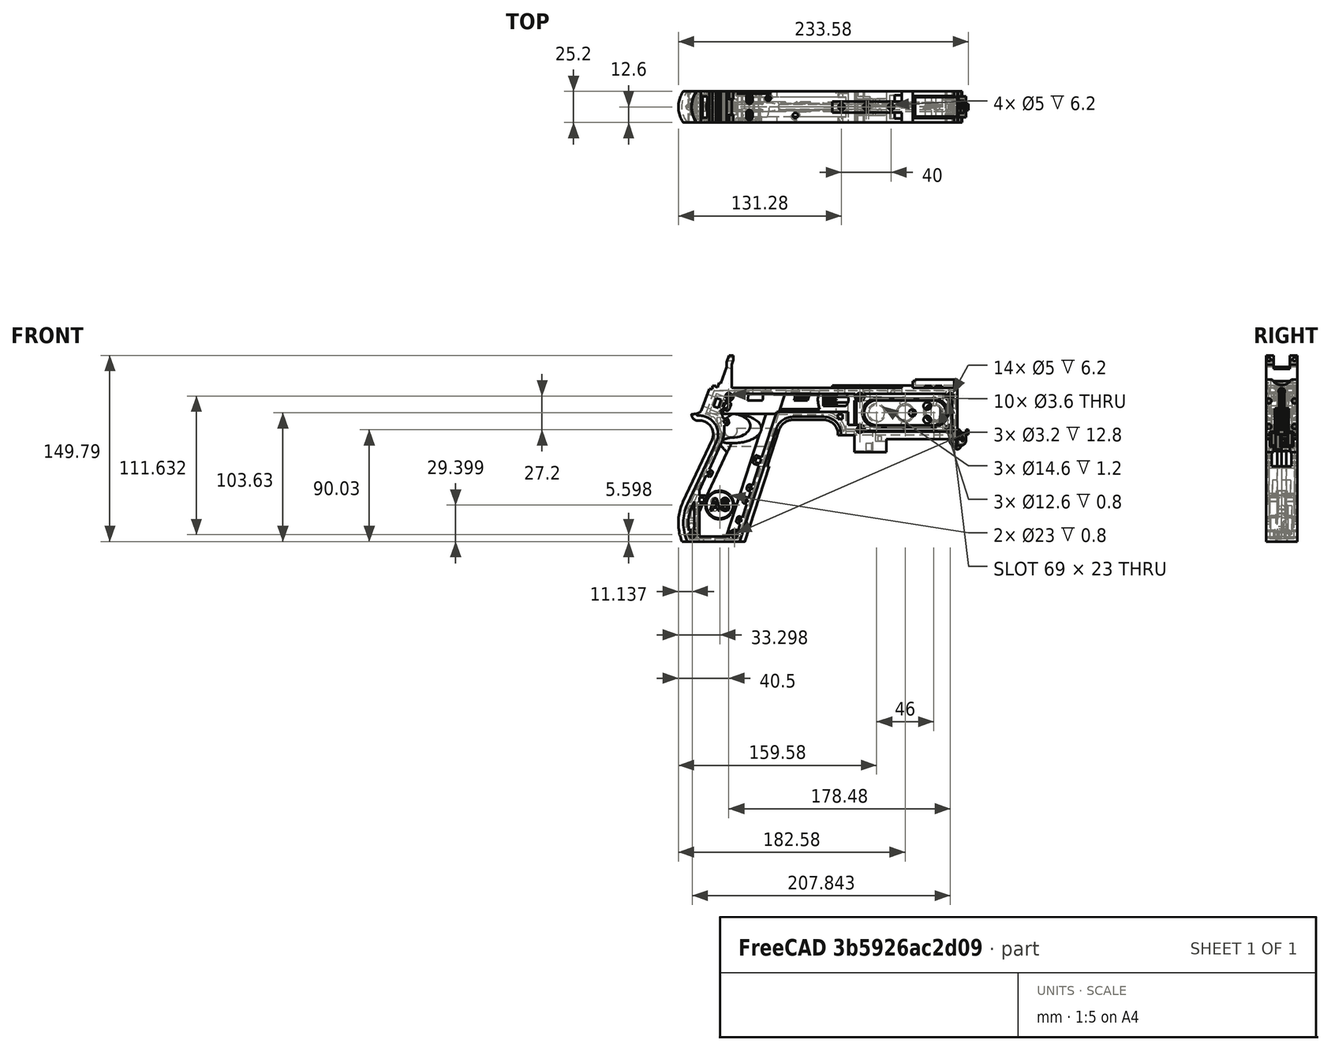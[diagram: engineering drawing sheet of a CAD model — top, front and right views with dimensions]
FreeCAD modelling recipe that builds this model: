
FCSTD DOCUMENT  (FreeCAD 1.0R39319 (Git))
Label: PICON-OF_ver_50
License: All rights reserved
LicenseURL: https://en.wikipedia.org/wiki/All_rights_reserved
objects: Sketcher::SketchObject×122, Part::Extrusion×62, Part::Cut×48, PartDesign::Pad×29, PartDesign::Pocket×20, PartDesign::Chamfer×15, PartDesign::Body×10, PartDesign::Fillet×6, Part::MultiFuse×4, Part::Part2DObjectPython×4, PartDesign::SubtractivePipe×4, PartDesign::SubtractiveLoft×4, PartDesign::Plane×3, PartDesign::SubShapeBinder×2, Part::Sweep×1, PartDesign::ShapeBinder×1, Mesh::Feature×1, PartDesign::Point×1, PartDesign::Groove×1
note: 617 computed .brp shape members not serialized (recipe doc carries the construction recipe); baked Part::Feature solids carry a one-line shape summary decoded from their .brp

FEATURE [Sketcher::SketchObject] Sketch  label="corpo principale"
  ArcFitTolerance = 1e-06
  AttacherType = Attacher::AttachEngine3D
  AttachmentSupport = -> [XZ_Plane]
  FullyConstrained = true
  MakeInternals = false
  MapMode = 5
  Placement = pos=(0,0,0) rot=(1,0,0;1.5708rad)
  sketch-geometry (65):
    g0: LineSegment StartX=0 StartY=0 StartZ=0 EndX=-57.2 EndY=0 EndZ=0
    g1: LineSegment StartX=-57.2 StartY=0 StartZ=0 EndX=-57.2 EndY=-10.4 EndZ=0
    g2: LineSegment StartX=-57.2 StartY=-10.4 StartZ=0 EndX=-82.8 EndY=-10.4 EndZ=0
    g3: LineSegment StartX=-82.8 StartY=-10.4 StartZ=0 EndX=-82.8 EndY=3.2 EndZ=0
    g4: LineSegment StartX=-82.8 StartY=3.2 StartZ=0 EndX=-93.6 EndY=3.2 EndZ=0
    g5: LineSegment StartX=-93.6 StartY=3.2 StartZ=0 EndX=-93.6 EndY=4 EndZ=0
    g6: LineSegment StartX=-107.6 StartY=18 StartZ=0 EndX=-132.428 EndY=18 EndZ=0
    g7: LineSegment StartX=-145.743 StartY=8.32624 StartZ=0 EndX=-175.232 EndY=-82.4316 EndZ=0
    g8: LineSegment StartX=-175.232 StartY=-82.4316 StartZ=0 EndX=-217.232 EndY=-82.4316 EndZ=0
    g9: LineSegment StartX=-217.232 StartY=-52.1862 StartZ=0 EndX=-193.988 EndY=-2.33927 EndZ=0
    g10: LineSegment StartX=-206.196 StartY=23.0857 StartZ=0 EndX=-199.861 EndY=40.4914 EndZ=0
    g11: LineSegment StartX=-199.861 StartY=40.4914 StartZ=0 EndX=-197.061 EndY=40.4914 EndZ=0
    g12: LineSegment StartX=-197.061 StartY=40.4914 StartZ=0 EndX=-197.061 EndY=42.8914 EndZ=0
    g13: LineSegment StartX=-197.061 StartY=42.8914 StartZ=0 EndX=-194.261 EndY=42.8914 EndZ=0
    g14: LineSegment StartX=-194.261 StartY=42.8914 StartZ=0 EndX=-194.535 EndY=42.1397 EndZ=0
    g15: LineSegment StartX=-194.535 StartY=42.1397 StartZ=0 EndX=-193.031 EndY=41.5924 EndZ=0
    g16: LineSegment StartX=-193.031 StartY=41.5924 StartZ=0 EndX=-191.663 EndY=45.3512 EndZ=0
    g17: LineSegment StartX=-191.663 StartY=45.3512 StartZ=0 EndX=-190.536 EndY=44.9408 EndZ=0
    g18: LineSegment StartX=-190.536 StartY=44.9408 StartZ=0 EndX=-185.747 EndY=58.0965 EndZ=0
    g19: LineSegment StartX=-185.747 StartY=58.0965 StartZ=0 EndX=-185.747 EndY=62.0965 EndZ=0
    g20: LineSegment StartX=-185.747 StartY=62.0965 StartZ=0 EndX=-183.832 EndY=67.3588 EndZ=0
    g21: LineSegment StartX=-183.832 StartY=67.3588 StartZ=0 EndX=-180.232 EndY=67.3588 EndZ=0
    g22: LineSegment StartX=-180.232 StartY=67.3588 StartZ=0 EndX=-180.232 EndY=63.7588 EndZ=0
    g23: LineSegment StartX=-180.232 StartY=63.7588 StartZ=0 EndX=-181.6 EndY=60 EndZ=0
    g24: LineSegment StartX=-181.6 StartY=60 StartZ=0 EndX=-181.6 EndY=41.2 EndZ=0
    g25: LineSegment StartX=-181.6 StartY=41.2 StartZ=0 EndX=-100.8 EndY=41.2 EndZ=0
    g26: LineSegment StartX=-36 StartY=43.2 StartZ=0 EndX=-36 EndY=41.2 EndZ=0
    g27: LineSegment StartX=0 StartY=48 StartZ=0 EndX=0 EndY=0 EndZ=0
    g28: LineSegment StartX=-209.901 StartY=19.85 StartZ=0 EndX=-209.901 EndY=20.1 EndZ=0
    g29: LineSegment StartX=-208.001 StartY=22 StartZ=0 EndX=-207.747 EndY=22 EndZ=0
    g30: LineSegment StartX=-207.583 StartY=19 StartZ=0 EndX=-209.051 EndY=19 EndZ=0
    g31: ArcOfCircle CenterX=-208.001 CenterY=20.1 CenterZ=0 NormalX=0 NormalY=0 NormalZ=1 AngleXU=0 Radius=1.9 StartAngle=1.5708 EndAngle=3.14159
    g32: GeomPoint [constr] X=-209.901 Y=22 Z=0
    g33: ArcOfCircle CenterX=-209.051 CenterY=19.85 CenterZ=0 NormalX=0 NormalY=0 NormalZ=1 AngleXU=0 Radius=0.85 StartAngle=3.14159 EndAngle=4.71239
    g34: GeomPoint [constr] X=-209.901 Y=19 Z=0
    g35: ArcOfCircle CenterX=-207.747 CenterY=23.65 CenterZ=0 NormalX=0 NormalY=0 NormalZ=1 AngleXU=0 Radius=1.65 StartAngle=4.71239 EndAngle=5.93412
    g36: GeomPoint [constr] X=-206.591 Y=22 Z=0
    g37: LineSegment StartX=-4 StartY=6 StartZ=0 EndX=-4 EndY=36.4 EndZ=0
    g38: LineSegment StartX=-4 StartY=36.4 StartZ=0 EndX=-185.2 EndY=36.4 EndZ=0
    g39: LineSegment StartX=-185.2 StartY=36.4 StartZ=0 EndX=-190.441 EndY=22 EndZ=0
    g40: LineSegment StartX=-214.575 StartY=-78.4316 StartZ=0 EndX=-178.142 EndY=-78.4316 EndZ=0
    g41: LineSegment StartX=-178.142 StartY=-78.4316 StartZ=0 EndX=-145.51 EndY=22 EndZ=0
    g42: LineSegment StartX=-145.51 StartY=22 StartZ=0 EndX=-87.91 EndY=22 EndZ=0
    g43: LineSegment StartX=-87.91 StartY=22 StartZ=0 EndX=-87.91 EndY=11.6 EndZ=0
    g44: LineSegment StartX=-87.91 StartY=11.6 StartZ=0 EndX=-80.11 EndY=11.6 EndZ=0
    g45: LineSegment StartX=-80.11 StartY=11.6 StartZ=0 EndX=-80.11 EndY=6 EndZ=0
    g46: LineSegment StartX=-80.11 StartY=6 StartZ=0 EndX=-4 EndY=6 EndZ=0
    g47: LineSegment StartX=-190.363 StartY=-4.02975 StartZ=0 EndX=-213.607 EndY=-53.8767 EndZ=0
    g48: ArcOfCircle CenterX=-132.428 CenterY=4 CenterZ=0 NormalX=0 NormalY=0 NormalZ=1 AngleXU=0 Radius=14 StartAngle=1.5708 EndAngle=2.82743
    g49: GeomPoint [constr] X=-142.6 Y=18 Z=0
    g50: ArcOfCircle CenterX=-107.6 CenterY=4 CenterZ=0 NormalX=0 NormalY=0 NormalZ=1 AngleXU=0 Radius=14 StartAngle=0 EndAngle=1.5708
    g51: GeomPoint [constr] X=-93.6 Y=18 Z=0
    g52: ArcOfCircle CenterX=-184.801 CenterY=-67.3089 CenterZ=0 NormalX=0 NormalY=0 NormalZ=1 AngleXU=0 Radius=35.7833 StartAngle=2.70526 EndAngle=3.57792
    g53: ArcOfCircle CenterX=-207.583 CenterY=4 CenterZ=0 NormalX=0 NormalY=0 NormalZ=1 AngleXU=0 Radius=15 StartAngle=5.84685 EndAngle=7.85398
    g54: LineSegment [constr] StartX=-213.607 StartY=-53.8767 StartZ=0 EndX=-217.232 EndY=-52.1862 EndZ=0
    g55: ArcOfCircle CenterX=-184.801 CenterY=-67.3089 CenterZ=0 NormalX=0 NormalY=0 NormalZ=1 AngleXU=0 Radius=31.7833 StartAngle=2.70526 EndAngle=3.49911
    g56: ArcOfCircle CenterX=-218.095 CenterY=8.90192 CenterZ=0 NormalX=0 NormalY=0 NormalZ=1 AngleXU=0 Radius=30.5989 StartAngle=5.84685 EndAngle=6.72553
    g57: LineSegment StartX=-44.6 StartY=43.2 StartZ=0 EndX=-36 EndY=43.2 EndZ=0
    g58: LineSegment StartX=-100.8 StartY=41.2 StartZ=0 EndX=-44.6 EndY=41.2 EndZ=0
    g59: LineSegment StartX=-44.6 StartY=41.2 StartZ=0 EndX=-44.6 EndY=43.2 EndZ=0
    g60: LineSegment StartX=-2.4 StartY=48 StartZ=0 EndX=0 EndY=48 EndZ=0
    g61: LineSegment StartX=-36 StartY=41.2 StartZ=0 EndX=-2.4 EndY=41.2 EndZ=0
    g62: LineSegment StartX=-2.4 StartY=41.2 StartZ=0 EndX=-2.4 EndY=48 EndZ=0
    g63: LineSegment [constr] StartX=-181.6 StartY=36.4 StartZ=0 EndX=-152.209 EndY=36.4 EndZ=0
    g64: LineSegment [constr] StartX=-181.6 StartY=36.4 StartZ=0 EndX=-130.41 EndY=36.4 EndZ=0
  constraints (183):
    c: Coincident(g-1,g0)
    c: PointOnObject(g0,g-1)
    c: Coincident(g0,g1)
    c: Vertical(g1)
    c: Coincident(g1,g2)
    c: Horizontal(g2)
    c: Coincident(g2,g3)
    c: Vertical(g3)
    c: Coincident(g3,g4)
    c: Coincident(g4,g5)
    c: Vertical(g5)
    c: Horizontal(g6)
    c: Coincident(g7,g8)
    c: Horizontal(g8)
    c: Coincident(g10,g11)
    c: Horizontal(g11)
    c: Coincident(g11,g12)
    c: Vertical(g12)
    c: Coincident(g12,g13)
    c: Horizontal(g13)
    c: Coincident(g13,g14)
    c: Coincident(g14,g15)
    c: Coincident(g15,g16)
    c: Coincident(g16,g17)
    c: Coincident(g17,g18)
    c: Coincident(g18,g19)
    c: Vertical(g19)
    c: Coincident(g19,g20)
    c: Coincident(g20,g21)
    c: Horizontal(g21)
    c: Coincident(g21,g22)
    c: Vertical(g22)
    c: Coincident(g22,g23)
    c: Coincident(g23,g24)
    c: Vertical(g24)
    c: Coincident(g24,g25)
    c: Horizontal(g25)
    c: Coincident(g57,g26)
    c: Vertical(g26)
    c: Coincident(g26,g61)
    c: PointOnObject(g60,g-2)
    c: Coincident(g60,g27)
    c: Coincident(g27,g0)
    c: DistanceY(g27,g27) = 48
    c: DistanceY(g1,g1) = 10.4
    c: DistanceX(g0,g0) = 57.2
    c: DistanceX(g2,g2) = 25.6
    c: Horizontal(g4)
    c: DistanceY(g3,g3) = 13.6
    c: DistanceX(g4,g4) = 10.8
    c: DistanceY(g5,g51) = 14.8
    c: DistanceX(g49,g51) = 49
    c: Distance(g7,g49) = 105.6
    c: DistanceX(g61,g60) = 36
    c: DistanceX(g25,g25) = 80.8
    c: DistanceY(g24,g24) = 18.8
    c: DistanceY(g22,g22) = 3.6
    c: Distance(g23) = 4
    c: Angle(g-1,g23) = 1.22173
    c: DistanceX(g21,g21) = 3.6
    c: Distance(g20) = 5.6
    c: Angle(g-1,g20) = 1.22173
    c: DistanceY(g19,g19) = 4
    c: Distance(g18) = 14
    c: Angle(g-1,g18) = 1.22173
    c: Distance(g17) = 1.2
    c: Distance(g16) = 4
    c: Angle(g16) = 1.22173
    c: Perpendicular(g18,g17)
    c: Distance(g15) = 1.6
    c: Perpendicular(g16,g15)
    c: Distance(g14) = 0.8
    c: DistanceX(g13,g13) = 2.8
    c: Perpendicular(g15,g14)
    c: DistanceY(g12,g12) = 2.4
    c: DistanceX(g11,g11) = 2.8
    c: Distance(g9) = 55
    c: Angle(g9,g-1) = 2.00713
    c: Horizontal(g29)
    c: Vertical(g28)
    c: Horizontal(g30)
    c: PointOnObject(g32,g29)
    c: PointOnObject(g32,g28)
    c: Tangent(g29,g31) = 1.5708
    c: Tangent(g28,g31) = 1.5708
    c: PointOnObject(g34,g28)
    c: PointOnObject(g34,g30)
    c: Tangent(g28,g33) = 1.5708
    c: Tangent(g30,g33) = 1.5708
    c: PointOnObject(g36,g29)
    c: PointOnObject(g36,g10)
    c: Tangent(g29,g35) = -1.5708
    c: Tangent(g10,g35) = -1.5708
    c: Angle(g-1,g10) = 1.22173
    c: Radius(g35) = 1.65
    c: Vertical(g37)
    c: Coincident(g37,g38)
    c: Horizontal(g38)
    c: Coincident(g38,g39)
    c: Horizontal(g40)
    c: Coincident(g40,g41)
    c: Coincident(g41,g42)
    c: Horizontal(g42)
    c: Coincident(g42,g43)
    c: Vertical(g43)
    c: Coincident(g43,g44)
    c: Horizontal(g44)
    c: Coincident(g44,g45)
    c: Vertical(g45)
    c: Coincident(g45,g46)
    c: Coincident(g46,g37)
    c: Horizontal(g46)
    c: DistanceY(g0,g37) = 6
    c: DistanceX(g37,g0) = 4
    c: DistanceY(g37,g25) = 4.8
    c: DistanceX(g38,g38) = 181.2
    c: DistanceX(g42,g42) = 57.6
    c: DistanceY(g49,g41) = 4
    c: DistanceX(g41,g49) = 2.91
    c: DistanceY(g43,g43) = 10.4
    c: DistanceX(g44,g44) = 7.8
    c: DistanceY(g7,g40) = 4
    c: Distance(g47) = 55
    c: Angle(g-1,g39) = 1.22173
    c: PointOnObject(g49,g7)
    c: PointOnObject(g49,g6)
    c: Tangent(g7,g48) = -1.5708
    c: Tangent(g6,g48) = -1.5708
    c: PointOnObject(g51,g5)
    c: PointOnObject(g51,g6)
    c: Tangent(g5,g50) = -1.5708
    c: Tangent(g6,g50) = -1.5708
    c: Radius(g50) = 14
    c: Radius(g48) = 14
    c: DistanceX(g8,g8) = 42
    c: Angle(g7,g-1) = 1.88496
    c: Parallel(g41,g7)
    c: Parallel(g47,g9)
    c: Coincident(g52,g8)
    c: Tangent(g52,g9) = 1.5708
    c: DistanceX(g9,g8) = 0
    c: Tangent(g53,g9) = -1.5708
    c: Tangent(g53,g30) = -1.5708
    c: Diameter(g53) = 30
    c: DistanceY(g53,g0) = -4
    c: Coincident(g54,g47)
    c: Distance(g54) = 4
    c: Coincident(g54,g9)
    c: Coincident(g55,g40)
    c: Tangent(g55,g47) = -1.5708
    c: Coincident(g52,g55)
    c: Coincident(g56,g39)
    c: Tangent(g56,g47) = 1.5708
    c: Horizontal(g57)
    c: DistanceX(g57,g57) = 8.6
    c: Coincident(g58,g25)
    c: Horizontal(g58)
    c: Coincident(g59,g58)
    c: Vertical(g59)
    c: DistanceY(g58,g57) = 2
    c: DistanceX(g58,g58) = 56.2
    c: Coincident(g59,g57)
    c: DistanceY(g41,g36) = 0
    c: DistanceY(g36,g39) = 0
    c: DistanceY(g28,g28) = 0.25
    c: DistanceX(g30,g36) = 2.46
    c: DistanceX(g28,g29) = 1.9
    c: Coincident(g62,g60)
    c: Horizontal(g60)
    c: DistanceX(g62,g27) = 2.4
    c: Coincident(g61,g62)
    c: DistanceY(g26,g26) = 2
    c: Vertical(g62)
    c: DistanceY(g61,g60) = 6.8
    c: Horizontal(g61)
    c: Distance(g63) = 29.391
    c: PointOnObject(g63,g38)
    c: PointOnObject(g63,g38)
    c: Distance(g64) = 51.19
    c: PointOnObject(g64,g38)
    c: PointOnObject(g64,g38)
    c: DistanceX(g24,g63) = 0
    c: DistanceX(g24,g64) = 0
FEATURE [Part::Extrusion] Extrude  label="Extrude corpo principale"
  Base = -> Sketch
  Dir = (0,-1,2e-16)
  DirMode = 2
  FaceMakerClass = Part::FaceMakerBullseye
  FaceMakerMode = 3
  LengthFwd = 25.2
  LengthRev = 12.6
  Solid = true
  Symmetric = true
FEATURE [Sketcher::SketchObject] Sketch002  label="scavo grilletto"
  ArcFitTolerance = 1e-06
  AttachmentSupport = -> [XZ_Plane]
  ExternalGeometry = -> [Sketch]
  FullyConstrained = true
  MakeInternals = false
  MapMode = 5
  Placement = pos=(0,0,0) rot=(1,0,0;1.5708rad)
  sketch-geometry (4):
    g0: LineSegment StartX=-89.51 StartY=22 StartZ=0 EndX=-152.71 EndY=22 EndZ=0
    g1: LineSegment StartX=-152.71 StartY=22 StartZ=0 EndX=-167.006 EndY=-22 EndZ=0
    g2: LineSegment StartX=-167.006 StartY=-22 StartZ=0 EndX=-89.51 EndY=-22 EndZ=0
    g3: LineSegment StartX=-89.51 StartY=-22 StartZ=0 EndX=-89.51 EndY=22 EndZ=0
  constraints (12):
    c: Horizontal(g0)
    c: Coincident(g0,g1)
    c: Coincident(g1,g2)
    c: Horizontal(g2)
    c: Coincident(g2,g3)
    c: Coincident(g3,g0)
    c: Vertical(g3)
    c: Angle(g1,g0) = 1.88496
    c: DistanceY(g3,g3) = 44
    c: DistanceX(g0,g0) = 63.2
    c: DistanceX(g0,g-3) = 1.6
    c: DistanceY(g-3,g0) = 0
FEATURE [Sketcher::SketchObject] Sketch004  label="traiettoria arrotondamento impugnatura anteriore"
  ArcFitTolerance = 1e-06
  AttachmentSupport = -> [XZ_Plane]
  ExternalGeometry = -> [Sketch]
  FullyConstrained = true
  MakeInternals = false
  MapMode = 5
  Placement = pos=(0,0,0) rot=(1,0,0;1.5708rad)
  sketch-geometry (13):
    g0: LineSegment StartX=-175.232 StartY=-82.4316 StartZ=0 EndX=-145.743 EndY=8.32624 EndZ=0
    g1: LineSegment StartX=-93.6 StartY=3.2 StartZ=0 EndX=-93.6 EndY=4 EndZ=0
    g2: LineSegment StartX=-132.428 StartY=18 StartZ=0 EndX=-107.6 EndY=18 EndZ=0
    g3: ArcOfCircle CenterX=-132.428 CenterY=4 CenterZ=0 NormalX=0 NormalY=0 NormalZ=1 AngleXU=0 Radius=14 StartAngle=1.5708 EndAngle=2.82743
    g4: ArcOfCircle CenterX=-107.6 CenterY=4 CenterZ=0 NormalX=0 NormalY=0 NormalZ=1 AngleXU=0 Radius=14 StartAngle=0 EndAngle=1.5708
    g5: LineSegment StartX=-175.232 StartY=-82.4316 StartZ=0 EndX=-217.232 EndY=-82.4316 EndZ=0
    g6: LineSegment StartX=-217.232 StartY=-52.1862 StartZ=0 EndX=-193.988 EndY=-2.33927 EndZ=0
    g7: LineSegment StartX=-209.051 StartY=19 StartZ=0 EndX=-207.583 EndY=19 EndZ=0
    g8: LineSegment StartX=-209.901 StartY=20.1 StartZ=0 EndX=-209.901 EndY=19.85 EndZ=0
    g9: ArcOfCircle CenterX=-184.801 CenterY=-67.3089 CenterZ=0 NormalX=0 NormalY=0 NormalZ=1 AngleXU=0 Radius=35.7833 StartAngle=2.70526 EndAngle=3.57792
    g10: ArcOfCircle CenterX=-207.583 CenterY=4 CenterZ=0 NormalX=0 NormalY=0 NormalZ=1 AngleXU=0 Radius=15 StartAngle=5.84685 EndAngle=7.85398
    g11: ArcOfCircle CenterX=-209.051 CenterY=19.85 CenterZ=0 NormalX=0 NormalY=0 NormalZ=1 AngleXU=0 Radius=0.85 StartAngle=3.14159 EndAngle=4.71239
    g12: ArcOfCircle CenterX=-208.001 CenterY=20.1 CenterZ=0 NormalX=0 NormalY=0 NormalZ=1 AngleXU=0 Radius=1.9 StartAngle=1.5708 EndAngle=3.14159
  constraints (26):
    c: Coincident(g0,g-3)
    c: Coincident(g0,g-6)
    c: Coincident(g1,g-8)
    c: Coincident(g1,g-7)
    c: Coincident(g2,g-5)
    c: Coincident(g2,g-4)
    c: Coincident(g3,g2)
    c: Tangent(g3,g0) = 1.5708
    c: Coincident(g4,g1)
    c: Tangent(g4,g2) = 1.5708
    c: Coincident(g5,g0)
    c: Coincident(g5,g-9)
    c: Coincident(g6,g-12)
    c: Coincident(g6,g-11)
    c: Coincident(g7,g-15)
    c: Coincident(g7,g-14)
    c: Coincident(g8,g-16)
    c: Coincident(g8,g-17)
    c: Tangent(g9,g6) = 1.5708
    c: Coincident(g9,g5)
    c: Coincident(g10,g7)
    c: Tangent(g10,g6) = -1.5708
    c: Tangent(g11,g7) = -1.5708
    c: Coincident(g11,g8)
    c: Tangent(g12,g8) = -1.5708
    c: Coincident(g12,g-17)
FEATURE [PartDesign::Plane] DatumPlane  label="Piano per disegno arrotondamento impugnatura"
  AttachmentSupport = -> [Sketch]
  Length = 73.6581
  MapMode = 7
  Placement = pos=(-145.743,1.8e-15,8.32624) rot=(0.154555,0.154555,0.97582;1.59527rad)
  ResizeMode = 0
  Width = 303.511
FEATURE [Sketcher::SketchObject] Sketch005  label="forma arrotondamento impugnatura anteriore"
  ArcFitTolerance = 1e-06
  AttachmentSupport = -> [DatumPlane]
  FullyConstrained = true
  MakeInternals = false
  MapMode = 5
  Placement = pos=(-145.743,1.8e-15,8.32624) rot=(0.154555,0.154555,0.97582;1.59527rad)
  sketch-geometry (5):
    g0: GeomPoint [constr] X=0 Y=-4 Z=0
    g1: GeomPoint [constr] X=-12.6 Y=7.1e-15 Z=0
    g2: GeomPoint [constr] X=12.6 Y=4.97e-14 Z=0
    g3: LineSegment StartX=-12.6 StartY=7.1e-15 StartZ=0 EndX=12.6 EndY=4.97e-14 EndZ=0
    g4: ArcOfCircle CenterX=-3.88e-14 CenterY=17.845 CenterZ=0 NormalX=0 NormalY=0 NormalZ=1 AngleXU=0 Radius=21.845 StartAngle=4.09759 EndAngle=5.32718
  constraints (11):
    c: DistanceY(g0,g-1) = 4
    c: DistanceX(g-1,g0) = 0
    c: DistanceX(g1,g-1) = 12.6
    c: DistanceX(g-1,g2) = 12.6
    c: DistanceY(g-1,g2) = 0
    c: DistanceY(g-1,g1) = 0
    c: Coincident(g3,g1)
    c: Coincident(g3,g2)
    c: Coincident(g4,g1)
    c: Coincident(g4,g2)
    c: PointOnObject(g0,g4)
FEATURE [Part::Sweep] Sweep  label="Sweep impugnatura"
  Frenet = true
  Sections = -> [Sketch005]
  Solid = true
  Spine = -> Sketch [Edge32,Edge33,Edge34,Edge35,Edge36,Edge37,Edge38,Edge39,Edge40,Edge41,Edge42,Edge43,Edge44]
  Transition = 1
FEATURE [Sketcher::SketchObject] Sketch008  label="buchi e pulizie varie"
  ArcFitTolerance = 1e-06
  AttachmentSupport = -> [XZ_Plane]
  ExternalGeometry = -> [Sketch]
  FullyConstrained = true
  MakeInternals = false
  MapMode = 5
  Placement = pos=(0,0,0) rot=(1,0,0;1.5708rad)
  sketch-geometry (26):
    g0: LineSegment StartX=-96.278 StartY=20.155 StartZ=0 EndX=-92.278 EndY=20.155 EndZ=0
    g1: LineSegment StartX=-92.278 StartY=20.155 StartZ=0 EndX=-92.278 EndY=16.155 EndZ=0
    g2: LineSegment StartX=-92.278 StartY=16.155 StartZ=0 EndX=-96.278 EndY=16.155 EndZ=0
    g3: LineSegment StartX=-96.278 StartY=16.155 StartZ=0 EndX=-96.278 EndY=20.155 EndZ=0
    g4: LineSegment StartX=-222.232 StartY=-82.4316 StartZ=0 EndX=-170.232 EndY=-82.4316 EndZ=0
    g5: LineSegment StartX=-170.232 StartY=-82.4316 StartZ=0 EndX=-170.232 EndY=-86.4316 EndZ=0
    g6: LineSegment StartX=-170.232 StartY=-86.4316 StartZ=0 EndX=-222.232 EndY=-86.4316 EndZ=0
    g7: LineSegment StartX=-222.232 StartY=-86.4316 StartZ=0 EndX=-222.232 EndY=-82.4316 EndZ=0
    g8: LineSegment StartX=-213.901 StartY=20.1 StartZ=0 EndX=-213.901 EndY=26 EndZ=0
    g9: LineSegment StartX=-213.901 StartY=26 StartZ=0 EndX=-206.196 EndY=26 EndZ=0
    g10: LineSegment StartX=-17.4 StartY=42.8 StartZ=0 EndX=-12.4 EndY=42.8 EndZ=0
    g11: LineSegment StartX=-12.4 StartY=42.8 StartZ=0 EndX=-12.4 EndY=41.2 EndZ=0
    g12: LineSegment StartX=-12.4 StartY=41.2 StartZ=0 EndX=-17.4 EndY=41.2 EndZ=0
    g13: LineSegment StartX=-17.4 StartY=41.2 StartZ=0 EndX=-17.4 EndY=42.8 EndZ=0
    g14: LineSegment StartX=-25.9 StartY=42.8 StartZ=0 EndX=-20.9 EndY=42.8 EndZ=0
    g15: LineSegment StartX=-20.9 StartY=42.8 StartZ=0 EndX=-20.9 EndY=41.2 EndZ=0
    g16: LineSegment StartX=-20.9 StartY=41.2 StartZ=0 EndX=-25.9 EndY=41.2 EndZ=0
    g17: LineSegment StartX=-25.9 StartY=41.2 StartZ=0 EndX=-25.9 EndY=42.8 EndZ=0
    g18: GeomPoint [constr] X=-206.196 Y=23.0857 Z=0
    g19: GeomPoint [constr] X=-213.901 Y=20.1 Z=0
    g20: BSplineCurve PolesCount=4 KnotsCount=2 Degree=3 IsPeriodic=0
    g21-g24: Circle [constr] x4 (B-spline internal-alignment scaffolding for g20; pole/knot coordinates omitted)
    g25: LineSegment StartX=-206.196 StartY=26 StartZ=0 EndX=-206.196 EndY=23.0857 EndZ=0
  constraints (73):
    c: Horizontal(g0)
    c: Coincident(g1,g0)
    c: Vertical(g1)
    c: Coincident(g2,g1)
    c: Horizontal(g2)
    c: Coincident(g3,g2)
    c: Coincident(g3,g0)
    c: Vertical(g3)
    c: DistanceX(g0,g-4) = 4.368
    c: DistanceY(g0,g-4) = 1.845
    c: DistanceY(g1,g1) = 4
    c: DistanceX(g2,g2) = 4
    c: Horizontal(g4)
    c: Coincident(g5,g4)
    c: Vertical(g5)
    c: Coincident(g6,g5)
    c: Horizontal(g6)
    c: Coincident(g7,g6)
    c: Coincident(g7,g4)
    c: Vertical(g7)
    c: DistanceY(g7,g7) = 4
    c: DistanceX(g4,g-5) = 5
    c: DistanceX(g-5,g4) = 5
    c: DistanceY(g4,g-5) = 0
    c: Coincident(g9,g8)
    c: Parallel(g9,g-6)
    c: DistanceX(g8,g-8) = 4
    c: Horizontal(g10)
    c: Coincident(g11,g10)
    c: Vertical(g11)
    c: Coincident(g12,g11)
    c: Horizontal(g12)
    c: Coincident(g13,g12)
    c: Coincident(g13,g10)
    c: Vertical(g13)
    c: Horizontal(g14)
    c: Coincident(g15,g14)
    c: Vertical(g15)
    c: Coincident(g16,g15)
    c: Horizontal(g16)
    c: Coincident(g17,g16)
    c: Coincident(g17,g14)
    c: Vertical(g17)
    c: DistanceY(g11,g10) = 1.6
    c: DistanceX(g10,g10) = 5
    c: DistanceY(g15,g14) = 1.6
    c: DistanceX(g14,g14) = 5
    c: DistanceX(g15,g12) = 3.5
    c: DistanceX(g11,g-9) = 10
    c: DistanceY(g-9,g11) = 0
    c: DistanceY(g-9,g15) = 0
    c: Perpendicular(g8,g9)
    c: DistanceY(g-7,g9) = 4
    c: DistanceY(g8,g-8) = 0
    c: InternalAlignment(g18,g20)
    c: InternalAlignment(g19,g20)
    c: InternalAlignment(g21,g20)
    c: Weight(g21) = 1
    c: InternalAlignment(g22,g20)
    c: Equal(g22,g21)
    c: InternalAlignment(g23,g20)
    c: Equal(g23,g21)
    c: InternalAlignment(g24,g20)
    c: Equal(g24,g21)
    c: Coincident(g18,g-12)
    c: Coincident(g19,g8)
    c: Coincident(g25,g9)
    c: Coincident(g25,g20)
    c: Vertical(g25)
    c: DistanceY(g20,g23) = 0
    c: DistanceY(g22,g18) = 2.26
    c: DistanceX(g22,g18) = 0.93
    c: DistanceX(g20,g23) = 2.9
FEATURE [Part::Extrusion] Extrude004  label="Extrude Buchi e pulizie varie"
  Base = -> Sketch008
  Dir = (0,-1,2e-16)
  DirMode = 2
  FaceMakerClass = Part::FaceMakerBullseye
  FaceMakerMode = 3
  LengthFwd = 25.2
  LengthRev = 0
  Solid = true
  Symmetric = true
FEATURE [Sketcher::SketchObject] Sketch009  label="rinforzi"
  ArcFitTolerance = 1e-06
  AttachmentSupport = -> [XZ_Plane]
  ExternalGeometry = -> [Sketch]
  FullyConstrained = true
  MakeInternals = false
  MapMode = 5
  Placement = pos=(0,0,0) rot=(1,0,0;1.5708rad)
  sketch-geometry (9):
    g0: LineSegment StartX=-87.91 StartY=22 StartZ=0 EndX=-87.91 EndY=36.4 EndZ=0
    g1: LineSegment StartX=-87.91 StartY=36.4 StartZ=0 EndX=-97.91 EndY=36.4 EndZ=0
    g2: LineSegment StartX=-97.91 StartY=36.4 StartZ=0 EndX=-97.91 EndY=22 EndZ=0
    g3: LineSegment StartX=-97.91 StartY=22 StartZ=0 EndX=-87.91 EndY=22 EndZ=0
    g4: LineSegment StartX=-149.713 StartY=9.06563 StartZ=0 EndX=-154.586 EndY=-5.93437 EndZ=0
    g5: LineSegment StartX=-154.586 StartY=-5.93437 StartZ=0 EndX=-191.863 EndY=-5.93437 EndZ=0
    g6: LineSegment StartX=-191.863 StartY=-5.93437 StartZ=0 EndX=-191.863 EndY=9.06563 EndZ=0
    g7: LineSegment StartX=-191.863 StartY=9.06563 StartZ=0 EndX=-149.713 EndY=9.06563 EndZ=0
    g8: LineSegment [constr] StartX=-145.51 StartY=22 StartZ=0 EndX=-149.713 EndY=9.06563 EndZ=0
  constraints (25):
    c: Vertical(g0)
    c: Coincident(g1,g0)
    c: Horizontal(g1)
    c: Coincident(g2,g1)
    c: Vertical(g2)
    c: Coincident(g3,g2)
    c: Coincident(g3,g0)
    c: Horizontal(g3)
    c: Coincident(g0,g-4)
    c: DistanceX(g3,g3) = 10
    c: DistanceY(g0,g-3) = 0
    c: Coincident(g5,g4)
    c: Horizontal(g5)
    c: Coincident(g6,g5)
    c: Vertical(g6)
    c: Coincident(g7,g6)
    c: Coincident(g7,g4)
    c: Horizontal(g7)
    c: Distance(g8) = 13.6
    c: Parallel(g-6,g8)
    c: Coincident(g-6,g8)
    c: Parallel(g4,g-6)
    c: DistanceY(g4,g4) = 15
    c: Coincident(g4,g8)
    c: DistanceX(g-5,g5) = -1.5
FEATURE [Part::Extrusion] Extrude001  label="Extrude scavo grilletto"
  Base = -> Sketch002
  Dir = (0,-1,2e-16)
  DirMode = 2
  FaceMakerClass = Part::FaceMakerBullseye
  FaceMakerMode = 3
  LengthFwd = 16
  LengthRev = 0
  Solid = true
  Symmetric = true
FEATURE [Part::Extrusion] Extrude005  label="Extrude Rinforzi"
  Base = -> Sketch009
  Dir = (0,-1,2e-16)
  DirMode = 2
  FaceMakerClass = Part::FaceMakerBullseye
  FaceMakerMode = 3
  LengthFwd = 2
  LengthRev = 0
  Placement = pos=(0,12.6,0) rot=(0,0,1;0rad)
  Solid = true
  Symmetric = false
FEATURE [PartDesign::ShapeBinder] CopyCut
  TraceSupport = false
FEATURE [PartDesign::Plane] DatumPlane001
  AttachmentSupport = -> [CopyCut]
  Length = 283.944
  MapMode = 5
  Placement = pos=(0,12.6,0) rot=(0,0.707107,0.707107;3.14159rad)
  ResizeMode = 0
  Width = 188.15
FEATURE [Sketcher::SketchObject] Sketch010  label="buco neopixel"
  ArcFitTolerance = 1e-06
  AttachmentSupport = -> [XZ_Plane]
  ExternalGeometry = -> [Sketch]
  FullyConstrained = true
  MakeInternals = false
  MapMode = 5
  Placement = pos=(0,0,0) rot=(1,0,0;1.5708rad)
  sketch-geometry (5):
    g0: LineSegment [constr] StartX=-199.861 StartY=40.4914 StartZ=0 EndX=-201.368 EndY=36.3521 EndZ=0
    g1: LineSegment StartX=-201.368 StartY=36.3521 StartZ=0 EndX=-204.932 EndY=26.5605 EndZ=0
    g2: LineSegment StartX=-201.368 StartY=36.3521 StartZ=0 EndX=-180.2 EndY=28.6477 EndZ=0
    g3: LineSegment StartX=-180.2 StartY=28.6477 StartZ=0 EndX=-183.764 EndY=18.8561 EndZ=0
    g4: LineSegment StartX=-183.764 StartY=18.8561 StartZ=0 EndX=-204.932 EndY=26.5605 EndZ=0
  constraints (14):
    c: Parallel(g0,g-3)
    c: Distance(g0) = 4.405
    c: Coincident(g0,g-3)
    c: Coincident(g2,g1)
    c: Coincident(g3,g2)
    c: Coincident(g4,g3)
    c: Coincident(g4,g1)
    c: Parallel(g1,g-3)
    c: Distance(g1) = 10.42
    c: Coincident(g1,g0)
    c: Parallel(g2,g4)
    c: Perpendicular(g1,g2)
    c: DistanceX(g-4,g2) = 5
    c: Parallel(g3,g1)
FEATURE [Part::Extrusion] Extrude006  label="Extrude buco neopixel"
  Base = -> Sketch010
  Dir = (0,-1,2e-16)
  DirMode = 2
  FaceMakerClass = Part::FaceMakerBullseye
  FaceMakerMode = 3
  LengthFwd = 17.2
  LengthRev = 0
  Solid = true
  Symmetric = true
FEATURE [Sketcher::SketchObject] Sketch011  label="fermo grilletto"
  ArcFitTolerance = 1e-06
  AttachmentSupport = -> [XZ_Plane]
  ExternalGeometry = -> [Sketch]
  FullyConstrained = true
  MakeInternals = false
  MapMode = 5
  Placement = pos=(0,0,0) rot=(1,0,0;1.5708rad)
  sketch-geometry (18):
    g0: LineSegment [constr] StartX=-145.51 StartY=22 StartZ=0 EndX=-157.347 EndY=-14.4293 EndZ=0
    g1: LineSegment [constr] StartX=-157.347 StartY=-14.4293 StartZ=0 EndX=-157.841 EndY=-15.951 EndZ=0
    g2: LineSegment StartX=-161.151 StartY=-13.1932 StartZ=0 EndX=-155.825 EndY=-14.9237 EndZ=0
    g3: LineSegment StartX=-163.167 StartY=-14.2205 StartZ=0 EndX=-164.403 EndY=-18.0247 EndZ=0
    g4: LineSegment StartX=-163.376 StartY=-20.0408 StartZ=0 EndX=-158.05 EndY=-21.7713 EndZ=0
    g5: LineSegment StartX=-158.05 StartY=-21.7713 StartZ=0 EndX=-155.825 EndY=-14.9237 EndZ=0
    g6: LineSegment StartX=-161.645 StartY=-14.7149 StartZ=0 EndX=-157.841 EndY=-15.951 EndZ=0
    g7: LineSegment StartX=-157.841 StartY=-15.951 StartZ=0 EndX=-159.077 EndY=-19.7552 EndZ=0
    g8: LineSegment StartX=-159.077 StartY=-19.7552 StartZ=0 EndX=-162.881 EndY=-18.5191 EndZ=0
    g9: LineSegment StartX=-162.881 StartY=-18.5191 StartZ=0 EndX=-161.645 EndY=-14.7149 EndZ=0
    g10: LineSegment [constr] StartX=-161.645 StartY=-14.7149 StartZ=0 EndX=-161.151 EndY=-13.1932 EndZ=0
    g11: LineSegment [constr] StartX=-159.077 StartY=-19.7552 StartZ=0 EndX=-157.555 EndY=-20.2496 EndZ=0
    g12: LineSegment [constr] StartX=-159.077 StartY=-19.7552 StartZ=0 EndX=-159.572 EndY=-21.2769 EndZ=0
    g13: LineSegment [constr] StartX=-161.645 StartY=-14.7149 StartZ=0 EndX=-163.167 EndY=-14.2205 EndZ=0
    g14: ArcOfCircle CenterX=-161.645 CenterY=-14.7149 CenterZ=0 NormalX=0 NormalY=0 NormalZ=1 AngleXU=0 Radius=1.6 StartAngle=1.25664 EndAngle=2.82743
    g15: GeomPoint [constr] X=-162.673 Y=-12.6988 Z=0
    g16: ArcOfCircle CenterX=-162.881 CenterY=-18.5191 CenterZ=0 NormalX=0 NormalY=0 NormalZ=1 AngleXU=0 Radius=1.6 StartAngle=2.82743 EndAngle=4.39823
    g17: GeomPoint [constr] X=-164.897 Y=-19.5464 Z=0
  constraints (48):
    c: Parallel(g0,g-3)
    c: Distance(g0) = 38.304
    c: Coincident(g0,g-3)
    c: Parallel(g1,g-3)
    c: Distance(g1) = 1.6
    c: Coincident(g1,g0)
    c: Coincident(g5,g4)
    c: Coincident(g5,g2)
    c: Coincident(g7,g6)
    c: Coincident(g8,g7)
    c: Coincident(g9,g8)
    c: Coincident(g9,g6)
    c: Parallel(g7,g-3)
    c: Parallel(g9,g7)
    c: Perpendicular(g6,g7)
    c: Parallel(g6,g8)
    c: Distance(g6) = 4
    c: Distance(g9) = 4
    c: Parallel(g5,g7)
    c: Parallel(g9,g3)
    c: Parallel(g2,g6)
    c: Parallel(g4,g8)
    c: Parallel(g13,g6)
    c: Parallel(g10,g9)
    c: Parallel(g11,g8)
    c: Parallel(g12,g7)
    c: Distance(g10) = 1.6
    c: Distance(g13) = 1.6
    c: Distance(g12) = 1.6
    c: Distance(g11) = 1.6
    c: Coincident(g10,g6)
    c: Coincident(g13,g6)
    c: Coincident(g12,g7)
    c: Coincident(g11,g7)
    c: Distance(g10,g15) = 1.6
    c: Distance(g15,g13) = 1.6
    c: Distance(g4,g12) = 1.6
    c: Distance(g4,g11) = 1.6
    c: PointOnObject(g15,g2)
    c: Tangent(g3,g14) = -1.5708
    c: Tangent(g2,g14) = 1.5708
    c: PointOnObject(g17,g4)
    c: PointOnObject(g17,g3)
    c: Tangent(g4,g16) = -1.5708
    c: Tangent(g3,g16) = -1.5708
    c: Equal(g16,g14)
    c: Coincident(g16,g8)
    c: Coincident(g6,g1)
FEATURE [Part::Extrusion] Extrude007  label="Extrude fermo grilletto"
  Base = -> Sketch011
  Dir = (0,-1,2e-16)
  DirMode = 2
  FaceMakerClass = Part::FaceMakerBullseye
  FaceMakerMode = 3
  LengthFwd = 25.2
  LengthRev = 0
  Solid = true
  Symmetric = true
FEATURE [Sketcher::SketchObject] Sketch012  label="buco oled"
  ArcFitTolerance = 1e-06
  AttachmentSupport = -> [XZ_Plane]
  ExternalGeometry = -> [Sketch]
  FullyConstrained = true
  MakeInternals = false
  MapMode = 5
  Placement = pos=(0,0,0) rot=(1,0,0;1.5708rad)
  sketch-geometry (4):
    g0: LineSegment StartX=-185.747 StartY=58.0965 StartZ=0 EndX=-180.232 EndY=56.0891 EndZ=0
    g1: LineSegment StartX=-185.747 StartY=58.0965 StartZ=0 EndX=-185.747 EndY=67.3588 EndZ=0
    g2: LineSegment StartX=-185.747 StartY=67.3588 StartZ=0 EndX=-180.232 EndY=67.3588 EndZ=0
    g3: LineSegment StartX=-180.232 StartY=67.3588 StartZ=0 EndX=-180.232 EndY=56.0891 EndZ=0
  constraints (10):
    c: Coincident(g1,g0)
    c: Coincident(g2,g1)
    c: Coincident(g3,g2)
    c: Coincident(g3,g0)
    c: Parallel(g1,g-5)
    c: Perpendicular(g-3,g0)
    c: Parallel(g2,g-6)
    c: Parallel(g3,g-4)
    c: Coincident(g0,g-5)
    c: Coincident(g2,g-6)
FEATURE [Part::Extrusion] Extrude008  label="Extrude buco oled"
  Base = -> Sketch012
  Dir = (0,-1,2e-16)
  DirMode = 2
  FaceMakerClass = Part::FaceMakerBullseye
  FaceMakerMode = 3
  LengthFwd = 12.8
  LengthRev = 0
  Solid = true
  Symmetric = true
FEATURE [Sketcher::SketchObject] Sketch013  label="buco pompa"
  ArcFitTolerance = 1e-06
  AttachmentSupport = -> [XZ_Plane]
  ExternalGeometry = -> [Sketch]
  FullyConstrained = true
  MakeInternals = false
  MapMode = 5
  Placement = pos=(0,0,0) rot=(1,0,0;1.5708rad)
  sketch-geometry (8):
    g0: LineSegment StartX=-82.8 StartY=-10.4 StartZ=0 EndX=-82.8 EndY=-9.6 EndZ=0
    g1: LineSegment StartX=-82.8 StartY=-9.6 StartZ=0 EndX=-67.9 EndY=-9.6 EndZ=0
    g2: LineSegment StartX=-67.9 StartY=-9.6 StartZ=0 EndX=-67.9 EndY=6 EndZ=0
    g3: LineSegment StartX=-67.9 StartY=6 StartZ=0 EndX=-65.9 EndY=6 EndZ=0
    g4: LineSegment StartX=-65.9 StartY=6 StartZ=0 EndX=-65.9 EndY=-1.7 EndZ=0
    g5: LineSegment StartX=-65.9 StartY=-1.7 StartZ=0 EndX=-57.2 EndY=-1.7 EndZ=0
    g6: LineSegment StartX=-57.2 StartY=-1.7 StartZ=0 EndX=-57.2 EndY=-10.4 EndZ=0
    g7: LineSegment StartX=-57.2 StartY=-10.4 StartZ=0 EndX=-82.8 EndY=-10.4 EndZ=0
  constraints (22):
    c: Vertical(g0)
    c: Coincident(g1,g0)
    c: Horizontal(g1)
    c: Coincident(g2,g1)
    c: Vertical(g2)
    c: Coincident(g3,g2)
    c: Horizontal(g3)
    c: Coincident(g4,g3)
    c: Vertical(g4)
    c: Coincident(g5,g4)
    c: Horizontal(g5)
    c: Coincident(g6,g5)
    c: Vertical(g6)
    c: Coincident(g7,g6)
    c: Coincident(g7,g0)
    c: DistanceY(g0,g0) = 0.8
    c: DistanceY(g6,g6) = 8.7
    c: DistanceX(g1,g1) = 14.9
    c: DistanceX(g3,g3) = 2
    c: Coincident(g0,g-4)
    c: DistanceY(g2,g-6) = 0
    c: Coincident(g6,g-5)
FEATURE [Part::Extrusion] Extrude009  label="Extrude buco pompa"
  Base = -> Sketch013
  Dir = (0,-1,2e-16)
  DirMode = 2
  FaceMakerClass = Part::FaceMakerBullseye
  FaceMakerMode = 3
  LengthFwd = 13.2
  LengthRev = 0
  Solid = true
  Symmetric = true
FEATURE [Sketcher::SketchObject] Sketch014  label="buco frontale"
  ArcFitTolerance = 1e-06
  AttachmentSupport = -> [XZ_Plane]
  ExternalGeometry = -> [Sketch]
  FullyConstrained = true
  MakeInternals = false
  MapMode = 5
  Placement = pos=(0,0,0) rot=(1,0,0;1.5708rad)
  sketch-geometry (10):
    g0: LineSegment StartX=0 StartY=0 StartZ=0 EndX=0 EndY=24.671 EndZ=0
    g1: LineSegment StartX=0 StartY=24.671 StartZ=0 EndX=-4 EndY=24.671 EndZ=0
    g2: LineSegment StartX=-4 StartY=24.671 StartZ=0 EndX=-4 EndY=16 EndZ=0
    g3: LineSegment StartX=-4 StartY=16 StartZ=0 EndX=-2.4 EndY=16 EndZ=0
    g4: LineSegment StartX=-2.4 StartY=16 StartZ=0 EndX=-2.4 EndY=10 EndZ=0
    g5: LineSegment StartX=-2.4 StartY=10 StartZ=0 EndX=-12 EndY=10 EndZ=0
    g6: LineSegment StartX=-12 StartY=10 StartZ=0 EndX=-12 EndY=6 EndZ=0
    g7: LineSegment StartX=-12 StartY=6 StartZ=0 EndX=-2.4 EndY=6 EndZ=0
    g8: LineSegment StartX=-2.4 StartY=6 StartZ=0 EndX=-2.4 EndY=0 EndZ=0
    g9: LineSegment StartX=-2.4 StartY=0 StartZ=0 EndX=0 EndY=0 EndZ=0
  constraints (29):
    c: Vertical(g0)
    c: Coincident(g1,g0)
    c: Horizontal(g1)
    c: Coincident(g2,g1)
    c: Vertical(g2)
    c: Coincident(g3,g2)
    c: Horizontal(g3)
    c: Coincident(g4,g3)
    c: Vertical(g4)
    c: Coincident(g5,g4)
    c: Horizontal(g5)
    c: Coincident(g6,g5)
    c: Vertical(g6)
    c: Coincident(g7,g6)
    c: Coincident(g8,g7)
    c: Vertical(g8)
    c: Coincident(g9,g8)
    c: Coincident(g9,g0)
    c: Horizontal(g9)
    c: DistanceY(g0,g0) = 24.671
    c: Horizontal(g7)
    c: DistanceY(g6,g6) = 4
    c: DistanceY(g4,g4) = 6
    c: DistanceX(g9,g9) = 2.4
    c: Coincident(g0,g-1)
    c: DistanceY(g-3,g7) = 0
    c: DistanceX(g8,g4) = 0
    c: DistanceX(g-3,g1) = 0
    c: DistanceX(g6,g-3) = 8
FEATURE [Part::Extrusion] Extrude010  label="Extrude buco frontale"
  Base = -> Sketch014
  Dir = (0,-1,2e-16)
  DirMode = 2
  FaceMakerClass = Part::FaceMakerBullseye
  FaceMakerMode = 3
  LengthFwd = 11.2
  LengthRev = 0
  Solid = true
  Symmetric = true
FEATURE [Sketcher::SketchObject] Sketch015  label="guida rail"
  ArcFitTolerance = 1e-06
  AttachmentSupport = -> [XZ_Plane]
  ExternalGeometry = -> [Sketch]
  FullyConstrained = true
  MakeInternals = false
  MapMode = 5
  Placement = pos=(0,0,0) rot=(1,0,0;1.5708rad)
  sketch-geometry (4):
    g0: LineSegment StartX=-100.8 StartY=43.2 StartZ=0 EndX=-44.6 EndY=43.2 EndZ=0
    g1: LineSegment StartX=-44.6 StartY=43.2 StartZ=0 EndX=-44.6 EndY=41.2 EndZ=0
    g2: LineSegment StartX=-44.6 StartY=41.2 StartZ=0 EndX=-100.8 EndY=41.2 EndZ=0
    g3: LineSegment StartX=-100.8 StartY=41.2 StartZ=0 EndX=-100.8 EndY=43.2 EndZ=0
  constraints (9):
    c: Horizontal(g0)
    c: Coincident(g1,g0)
    c: Coincident(g2,g1)
    c: Coincident(g3,g2)
    c: Coincident(g3,g0)
    c: Vertical(g3)
    c: Coincident(g2,g-3)
    c: Coincident(g1,g-3)
    c: Coincident(g0,g-4)
FEATURE [Part::Extrusion] Extrude011  label="Extrude guida rail"
  Base = -> Sketch015
  Dir = (0,-1,2e-16)
  DirMode = 2
  FaceMakerClass = Part::FaceMakerBullseye
  FaceMakerMode = 3
  LengthFwd = 9
  LengthRev = 0
  Solid = true
  Symmetric = true
FEATURE [Sketcher::SketchObject] Sketch016  label="guide per coperture laterali"
  ArcFitTolerance = 1e-06
  AttachmentSupport = -> [XZ_Plane]
  ExternalGeometry = -> [Sketch]
  FullyConstrained = true
  MakeInternals = false
  MapMode = 5
  Placement = pos=(0,0,0) rot=(1,0,0;1.5708rad)
  sketch-geometry (14):
    g0: Circle CenterX=-5.6 CenterY=7.6 CenterZ=0 NormalX=0 NormalY=0 NormalZ=1 AngleXU=0 Radius=1.6
    g1: Circle CenterX=-5.6 CenterY=7.6 CenterZ=0 NormalX=0 NormalY=0 NormalZ=1 AngleXU=0 Radius=4
    g2: Circle CenterX=-5.6 CenterY=34.8 CenterZ=0 NormalX=0 NormalY=0 NormalZ=1 AngleXU=0 Radius=1.6
    g3: Circle CenterX=-5.6 CenterY=34.8 CenterZ=0 NormalX=0 NormalY=0 NormalZ=1 AngleXU=0 Radius=4
    g4: Circle CenterX=-184.08 CenterY=34.8 CenterZ=0 NormalX=0 NormalY=0 NormalZ=1 AngleXU=0 Radius=1.6
    g5: Circle CenterX=-184.08 CenterY=34.8 CenterZ=0 NormalX=0 NormalY=0 NormalZ=1 AngleXU=0 Radius=4
    g6: Circle CenterX=-179.305 CenterY=-76.8316 CenterZ=0 NormalX=0 NormalY=0 NormalZ=1 AngleXU=0 Radius=1.6
    g7: Circle CenterX=-179.305 CenterY=-76.8316 CenterZ=0 NormalX=0 NormalY=0 NormalZ=1 AngleXU=0 Radius=4
    g8: Circle CenterX=-213.443 CenterY=-76.8316 CenterZ=0 NormalX=0 NormalY=0 NormalZ=1 AngleXU=0 Radius=1.6
    g9: Circle CenterX=-213.443 CenterY=-76.8316 CenterZ=0 NormalX=0 NormalY=0 NormalZ=1 AngleXU=0 Radius=4
    g10: Circle CenterX=-78.51 CenterY=7.6 CenterZ=0 NormalX=0 NormalY=0 NormalZ=1 AngleXU=0 Radius=1.6
    g11: Circle CenterX=-78.51 CenterY=7.6 CenterZ=0 NormalX=0 NormalY=0 NormalZ=1 AngleXU=0 Radius=4
    g12: Circle CenterX=-78.51 CenterY=34.8 CenterZ=0 NormalX=0 NormalY=0 NormalZ=1 AngleXU=0 Radius=1.6
    g13: Circle CenterX=-78.51 CenterY=34.8 CenterZ=0 NormalX=0 NormalY=0 NormalZ=1 AngleXU=0 Radius=4
  constraints (35):
    c: Diameter(g0) = 3.2
    c: Diameter(g1) = 8
    c: Coincident(g0,g1)
    c: Diameter(g2) = 3.2
    c: Diameter(g3) = 8
    c: Coincident(g3,g2)
    c: Tangent(g2,g-7)
    c: Diameter(g4) = 3.2
    c: Diameter(g5) = 8
    c: Coincident(g5,g4)
    c: Tangent(g4,g-7)
    c: Tangent(g4,g-8)
    c: Diameter(g6) = 3.2
    c: Diameter(g7) = 8
    c: Coincident(g7,g6)
    c: Tangent(g6,g-9)
    c: Tangent(g6,g-10)
    c: Diameter(g8) = 3.2
    c: Diameter(g9) = 8
    c: Coincident(g9,g8)
    c: Tangent(g8,g-10)
    c: Tangent(g8,g-11)
    c: Diameter(g10) = 3.2
    c: Diameter(g11) = 8
    c: Diameter(g12) = 3.2
    c: Diameter(g13) = 8
    c: Coincident(g12,g13)
    c: Coincident(g10,g11)
    c: Tangent(g12,g-7)
    c: DistanceX(g12,g10) = 0
    c: Tangent(g2,g-6)
    c: Tangent(g0,g-6)
    c: Tangent(g0,g-3)
    c: Tangent(g10,g-3)
    c: Tangent(g10,g-4)
FEATURE [Part::Extrusion] Extrude012  label="extrude guide per coperture laterali"
  Base = -> Sketch016
  Dir = (0,-1,2e-16)
  DirMode = 2
  FaceMakerClass = Part::FaceMakerBullseye
  FaceMakerMode = 3
  LengthFwd = 25.2
  LengthRev = 0
  Solid = true
  Symmetric = true
FEATURE [Sketcher::SketchObject] Sketch017  label="supporto CAM"
  ArcFitTolerance = 1e-06
  AttachmentSupport = -> [XZ_Plane]
  ExternalGeometry = -> [Sketch]
  FullyConstrained = true
  MakeInternals = false
  MapMode = 5
  Placement = pos=(0,0,0) rot=(1,0,0;1.5708rad)
  sketch-geometry (6):
    g0: LineSegment StartX=-2.4 StartY=48 StartZ=0 EndX=-2.4 EndY=41.2 EndZ=0
    g1: LineSegment StartX=-2.4 StartY=48 StartZ=0 EndX=-34 EndY=48 EndZ=0
    g2: LineSegment StartX=-34 StartY=48 StartZ=0 EndX=-34 EndY=46.72 EndZ=0
    g3: LineSegment StartX=-34 StartY=46.72 StartZ=0 EndX=-36 EndY=46.72 EndZ=0
    g4: LineSegment StartX=-36 StartY=46.72 StartZ=0 EndX=-36 EndY=41.2 EndZ=0
    g5: LineSegment StartX=-36 StartY=41.2 StartZ=0 EndX=-2.4 EndY=41.2 EndZ=0
  constraints (15):
    c: Coincident(g1,g0)
    c: Horizontal(g1)
    c: Coincident(g2,g1)
    c: Vertical(g2)
    c: Coincident(g3,g2)
    c: Horizontal(g3)
    c: Coincident(g4,g3)
    c: Coincident(g5,g4)
    c: DistanceX(g1,g0) = 31.6
    c: Coincident(g5,g0)
    c: Vertical(g4)
    c: DistanceY(g2,g1) = 1.28
    c: Coincident(g0,g-3)
    c: Coincident(g0,g-3)
    c: Coincident(g4,g-4)
FEATURE [Part::Extrusion] Extrude013  label="Extrude supporto CAM"
  Base = -> Sketch017
  Dir = (0,-1,2e-16)
  DirMode = 2
  FaceMakerClass = Part::FaceMakerBullseye
  FaceMakerMode = 3
  LengthFwd = 17.8
  LengthRev = 0
  Solid = true
  Symmetric = true
FEATURE [Sketcher::SketchObject] Sketch018  label="Scavo CAM"
  ArcFitTolerance = 1e-06
  AttachmentSupport = -> [YZ_Plane]
  ExternalGeometry = -> [Sketch]
  FullyConstrained = true
  MakeInternals = false
  MapMode = 5
  Placement = pos=(0,0,0) rot=(0.57735,0.57735,0.57735;2.0944rad)
  sketch-geometry (4):
    g0: LineSegment StartX=-7.73 StartY=48 StartZ=0 EndX=7.73 EndY=48 EndZ=0
    g1: LineSegment [constr] StartX=1.07e-14 StartY=48 StartZ=0 EndX=0 EndY=43.5155 EndZ=0
    g2: ArcOfCircle CenterX=9e-15 CenterY=52.42 CenterZ=0 NormalX=0 NormalY=0 NormalZ=1 AngleXU=0 Radius=8.90445 StartAngle=3.66102 EndAngle=5.76376
    g3: Circle [constr] CenterX=9e-15 CenterY=52.42 CenterZ=0 NormalX=0 NormalY=0 NormalZ=1 AngleXU=0 Radius=8.9
  constraints (13):
    c: Horizontal(g0)
    c: DistanceY(g-3,g0) = 0
    c: DistanceX(g0,g0) = 15.46
    c: DistanceX(g0,g-3) = 7.73
    c: DistanceX(g-3) = 0
    c: Coincident(g1,g-3)
    c: PointOnObject(g1,g-2)
    c: Coincident(g2,g0)
    c: Coincident(g2,g0)
    c: PointOnObject(g1,g2)
    c: Diameter(g3) = 17.8
    c: DistanceY(g1,g3) = 4.42
    c: Coincident(g2,g3)
FEATURE [Part::Extrusion] Extrude014  label="Extrude Scavo CAM"
  Base = -> Sketch018
  Dir = (1,0,0)
  DirMode = 2
  FaceMakerClass = Part::FaceMakerBullseye
  FaceMakerMode = 3
  LengthFwd = -34
  LengthRev = 0
  Solid = true
  Symmetric = false
FEATURE [Sketcher::SketchObject] Sketch019  label="scavo rumble"
  ArcFitTolerance = 1e-06
  AttachmentSupport = -> [XZ_Plane]
  ExternalGeometry = -> [Sketch]
  FullyConstrained = true
  MakeInternals = false
  MapMode = 5
  Placement = pos=(0,0,0) rot=(1,0,0;1.5708rad)
  sketch-geometry (6):
    g0: LineSegment StartX=-163.771 StartY=-21.9058 StartZ=0 EndX=-158.636 EndY=-23.5745 EndZ=0
    g1: LineSegment StartX=-158.636 StartY=-23.5745 StartZ=0 EndX=-165.743 EndY=-45.4488 EndZ=0
    g2: LineSegment StartX=-165.743 StartY=-45.4488 StartZ=0 EndX=-170.879 EndY=-43.7801 EndZ=0
    g3: LineSegment StartX=-170.879 StartY=-43.7801 StartZ=0 EndX=-163.771 EndY=-21.9058 EndZ=0
    g4: LineSegment [constr] StartX=-145.51 StartY=22 StartZ=0 EndX=-160.157 EndY=-23.0801 EndZ=0
    g5: LineSegment [constr] StartX=-158.636 StartY=-23.5745 StartZ=0 EndX=-160.157 EndY=-23.0801 EndZ=0
  constraints (17):
    c: Coincident(g1,g0)
    c: Coincident(g2,g1)
    c: Coincident(g3,g2)
    c: Coincident(g3,g0)
    c: Parallel(g3,g-3)
    c: Parallel(g3,g1)
    c: Perpendicular(g3,g0)
    c: Perpendicular(g2,g3)
    c: Distance(g2,g0) = 23
    c: Parallel(g4,g-3)
    c: Distance(g4) = 47.4
    c: Coincident(g4,g-3)
    c: Parallel(g5,g0)
    c: Distance(g5) = 1.6
    c: Coincident(g5,g0)
    c: Distance(g5,g0) = 3.8
    c: Coincident(g5,g4)
FEATURE [Part::Extrusion] Extrude015  label="scavo rumble001"
  Base = -> Sketch019
  Dir = (0,-1,2e-16)
  DirMode = 2
  FaceMakerClass = Part::FaceMakerBullseye
  FaceMakerMode = 3
  LengthFwd = 21
  LengthRev = 0
  Solid = true
  Symmetric = true
FEATURE [Sketcher::SketchObject] Sketch020  label="fermo rumble"
  ArcFitTolerance = 1e-06
  AttachmentSupport = -> [XZ_Plane]
  ExternalGeometry = -> [Sketch019,Sketch]
  FullyConstrained = true
  MakeInternals = false
  MapMode = 5
  Placement = pos=(0,0,0) rot=(1,0,0;1.5708rad)
  sketch-geometry (16):
    g0: LineSegment [constr] StartX=-165.905 StartY=-40.7697 StartZ=0 EndX=-167.265 EndY=-44.9544 EndZ=0
    g1: LineSegment [constr] StartX=-167.265 StartY=-44.9544 StartZ=0 EndX=-165.743 EndY=-45.4488 EndZ=0
    g2: LineSegment StartX=-167.318 StartY=-37.9976 StartZ=0 EndX=-165.225 EndY=-38.6774 EndZ=0
    g3: LineSegment StartX=-165.225 StartY=-38.6774 StartZ=0 EndX=-165.905 EndY=-40.7697 EndZ=0
    g4: LineSegment StartX=-165.905 StartY=-40.7697 StartZ=0 EndX=-167.997 EndY=-40.0899 EndZ=0
    g5: LineSegment StartX=-167.997 StartY=-40.0899 StartZ=0 EndX=-167.318 EndY=-37.9976 EndZ=0
    g6: LineSegment StartX=-166.823 StartY=-36.4759 StartZ=0 EndX=-163.399 EndY=-37.5883 EndZ=0
    g7: LineSegment StartX=-163.399 StartY=-37.5883 StartZ=0 EndX=-165.006 EndY=-42.5338 EndZ=0
    g8: LineSegment StartX=-165.006 StartY=-42.5338 StartZ=0 EndX=-168.43 EndY=-41.4214 EndZ=0
    g9: LineSegment StartX=-169.457 StartY=-39.4053 StartZ=0 EndX=-168.839 EndY=-37.5031 EndZ=0
    g10: LineSegment [constr] StartX=-168.839 StartY=-37.5031 StartZ=0 EndX=-168.345 EndY=-35.9815 EndZ=0
    g11: LineSegment [constr] StartX=-168.345 StartY=-35.9815 StartZ=0 EndX=-166.823 EndY=-36.4759 EndZ=0
    g12: ArcOfCircle CenterX=-167.936 CenterY=-39.8997 CenterZ=0 NormalX=0 NormalY=0 NormalZ=1 AngleXU=0 Radius=1.6 StartAngle=2.82743 EndAngle=4.39823
    g13: GeomPoint [constr] X=-169.952 Y=-40.9269 Z=0
    g14: ArcOfCircle CenterX=-167.318 CenterY=-37.9976 CenterZ=0 NormalX=0 NormalY=0 NormalZ=1 AngleXU=0 Radius=1.6 StartAngle=1.25664 EndAngle=2.82743
    g15: GeomPoint [constr] X=-168.345 Y=-35.9815 Z=0
  constraints (42):
    c: Parallel(g0,g-4)
    c: Distance(g0) = 4.4
    c: Coincident(g1,g0)
    c: Perpendicular(g0,g1)
    c: Distance(g1) = 1.6
    c: Coincident(g1,g-5)
    c: Coincident(g3,g2)
    c: Coincident(g4,g3)
    c: Coincident(g5,g4)
    c: Coincident(g5,g2)
    c: Parallel(g3,g-4)
    c: Parallel(g3,g5)
    c: Perpendicular(g2,g3)
    c: Parallel(g4,g2)
    c: Distance(g2) = 2.2
    c: Distance(g3) = 2.2
    c: Coincident(g7,g6)
    c: Coincident(g8,g7)
    c: Parallel(g7,g-4)
    c: Parallel(g7,g9)
    c: Perpendicular(g6,g7)
    c: Parallel(g6,g8)
    c: Distance(g6,g15) = 5.2
    c: Distance(g7) = 5.2
    c: Coincident(g11,g10)
    c: Parallel(g10,g9)
    c: Parallel(g11,g6)
    c: Distance(g10) = 1.6
    c: Distance(g11) = 1.6
    c: Coincident(g10,g15)
    c: Distance(g11,g2) = 1.6
    c: Distance(g2,g10) = 1.6
    c: PointOnObject(g13,g8)
    c: PointOnObject(g13,g9)
    c: Tangent(g8,g12) = 1.5708
    c: Tangent(g9,g12) = 1.5708
    c: PointOnObject(g15,g9)
    c: Tangent(g6,g14) = 1.5708
    c: Tangent(g9,g14) = 1.5708
    c: Equal(g12,g14)
    c: Coincident(g6,g11)
    c: Coincident(g3,g0)
FEATURE [Part::Extrusion] Extrude016  label="Extrude fermo rumble"
  Base = -> Sketch020
  Dir = (0,-1,2e-16)
  DirMode = 2
  FaceMakerClass = Part::FaceMakerBullseye
  FaceMakerMode = 3
  LengthFwd = 25.2
  LengthRev = 0
  Solid = true
  Symmetric = true
FEATURE [Sketcher::SketchObject] Sketch021  label="perno fermo rumble001"
  ArcFitTolerance = 1e-06
  AttachmentSupport = -> [XZ_Plane001]
  FullyConstrained = true
  MakeInternals = false
  MapMode = 5
  Placement = pos=(0,0,0) rot=(1,0,0;1.5708rad)
  sketch-geometry (16):
    g0: LineSegment StartX=0 StartY=0.45 StartZ=0 EndX=0 EndY=1.55 EndZ=0
    g1: LineSegment StartX=0.45 StartY=2 StartZ=0 EndX=1.55 EndY=2 EndZ=0
    g2: LineSegment StartX=2 StartY=1.55 StartZ=0 EndX=2 EndY=0.45 EndZ=0
    g3: LineSegment StartX=1.55 StartY=0 StartZ=0 EndX=0.45 EndY=0 EndZ=0
    g4: ArcOfCircle [constr] CenterX=0.45 CenterY=1.55 CenterZ=0 NormalX=0 NormalY=0 NormalZ=1 AngleXU=0 Radius=0.45 StartAngle=1.5708 EndAngle=3.14159
    g5: GeomPoint [constr] X=0 Y=2 Z=0
    g6: LineSegment StartX=0.45 StartY=2 StartZ=0 EndX=0 EndY=1.55 EndZ=0
    g7: ArcOfCircle [constr] CenterX=1.55 CenterY=1.55 CenterZ=0 NormalX=0 NormalY=0 NormalZ=1 AngleXU=0 Radius=0.45 StartAngle=0 EndAngle=1.5708
    g8: GeomPoint [constr] X=2 Y=2 Z=0
    g9: LineSegment StartX=2 StartY=1.55 StartZ=0 EndX=1.55 EndY=2 EndZ=0
    g10: ArcOfCircle [constr] CenterX=1.55 CenterY=0.45 CenterZ=0 NormalX=0 NormalY=0 NormalZ=1 AngleXU=0 Radius=0.45 StartAngle=4.71239 EndAngle=6.28319
    g11: GeomPoint [constr] X=2 Y=0 Z=0
    g12: LineSegment StartX=1.55 StartY=0 StartZ=0 EndX=2 EndY=0.45 EndZ=0
    g13: ArcOfCircle [constr] CenterX=0.45 CenterY=0.45 CenterZ=0 NormalX=0 NormalY=0 NormalZ=1 AngleXU=0 Radius=0.45 StartAngle=3.14159 EndAngle=4.71239
    g14: GeomPoint [constr] X=0 Y=0 Z=0
    g15: LineSegment StartX=0 StartY=0.45 StartZ=0 EndX=0.45 EndY=0 EndZ=0
  constraints (35):
    c: Coincident(g14,g-1)
    c: PointOnObject(g5,g-2)
    c: Horizontal(g1)
    c: Vertical(g2)
    c: Horizontal(g3)
    c: DistanceX(g5,g8) = 2
    c: DistanceY(g11,g8) = 2
    c: PointOnObject(g5,g0)
    c: PointOnObject(g5,g1)
    c: Tangent(g0,g4) = 1.5708
    c: Tangent(g1,g4) = 1.5708
    c: Coincident(g6,g0)
    c: Coincident(g6,g1)
    c: PointOnObject(g8,g2)
    c: PointOnObject(g8,g1)
    c: Tangent(g2,g7) = 1.5708
    c: Tangent(g1,g7) = 1.5708
    c: Coincident(g9,g2)
    c: Coincident(g9,g1)
    c: PointOnObject(g11,g2)
    c: PointOnObject(g11,g3)
    c: Tangent(g2,g10) = 1.5708
    c: Tangent(g3,g10) = 1.5708
    c: Coincident(g12,g2)
    c: Coincident(g12,g3)
    c: PointOnObject(g14,g0)
    c: PointOnObject(g14,g3)
    c: Tangent(g0,g13) = 1.5708
    c: Tangent(g3,g13) = 1.5708
    c: Coincident(g15,g0)
    c: Coincident(g15,g3)
    c: Equal(g6,g9)
    c: Equal(g9,g12)
    c: Equal(g12,g15)
    c: DistanceX(g14,g3) = 0.45
FEATURE [Sketcher::SketchObject] Sketch022  label="fori per M3x5(OD)x6(L)"
  ArcFitTolerance = 1e-06
  AttachmentSupport = -> [XZ_Plane]
  ExternalGeometry = -> [Sketch016]
  FullyConstrained = true
  MakeInternals = false
  MapMode = 5
  Placement = pos=(0,0,0) rot=(1,0,0;1.5708rad)
  sketch-geometry (7):
    g0: Circle CenterX=-5.6 CenterY=34.8 CenterZ=0 NormalX=0 NormalY=0 NormalZ=1 AngleXU=0 Radius=2.5
    g1: Circle CenterX=-5.6 CenterY=7.6 CenterZ=0 NormalX=0 NormalY=0 NormalZ=1 AngleXU=0 Radius=2.5
    g2: Circle CenterX=-78.51 CenterY=34.8 CenterZ=0 NormalX=0 NormalY=0 NormalZ=1 AngleXU=0 Radius=2.5
    g3: Circle CenterX=-78.51 CenterY=7.6 CenterZ=0 NormalX=0 NormalY=0 NormalZ=1 AngleXU=0 Radius=2.5
    g4: Circle CenterX=-184.08 CenterY=34.8 CenterZ=0 NormalX=0 NormalY=0 NormalZ=1 AngleXU=0 Radius=2.5
    g5: Circle CenterX=-179.305 CenterY=-76.8316 CenterZ=0 NormalX=0 NormalY=0 NormalZ=1 AngleXU=0 Radius=2.5
    g6: Circle CenterX=-213.443 CenterY=-76.8316 CenterZ=0 NormalX=0 NormalY=0 NormalZ=1 AngleXU=0 Radius=2.5
  constraints (14):
    c: Diameter(g0) = 5
    c: Diameter(g1) = 5
    c: Diameter(g2) = 5
    c: Diameter(g3) = 5
    c: Diameter(g4) = 5
    c: Diameter(g5) = 5
    c: Diameter(g6) = 5
    c: Coincident(g0,g-8)
    c: Coincident(g1,g-9)
    c: Coincident(g2,g-6)
    c: Coincident(g3,g-7)
    c: Coincident(g4,g-5)
    c: Coincident(g5,g-4)
    c: Coincident(g6,g-3)
FEATURE [Part::Extrusion] Extrude018  label="Extrude fori M3x5x6 - dx"
  Base = -> Sketch022
  Dir = (0,-1,2e-16)
  DirMode = 2
  FaceMakerClass = Part::FaceMakerBullseye
  FaceMakerMode = 3
  LengthFwd = 6.2
  LengthRev = 0
  Placement = pos=(0,-9.5,0) rot=(0,0,1;0rad)
  Solid = true
  Symmetric = true
FEATURE [Part::Extrusion] Extrude019  label="Extrude fori M3x5x6 - sx"
  Base = -> Sketch022
  Dir = (0,-1,2e-16)
  DirMode = 2
  FaceMakerClass = Part::FaceMakerBullseye
  FaceMakerMode = 3
  LengthFwd = 6.2
  LengthRev = 0
  Placement = pos=(0,9.5,0) rot=(0,0,1;0rad)
  Solid = true
  Symmetric = true
FEATURE [Sketcher::SketchObject] Sketch023  label="foro anteriore M3x5x6"
  ArcFitTolerance = 1e-06
  AttachmentSupport = -> [YZ_Plane]
  FullyConstrained = true
  MakeInternals = false
  MapMode = 5
  Placement = pos=(0,0,0) rot=(0.57735,0.57735,0.57735;2.0944rad)
  sketch-geometry (2):
    g0: LineSegment [constr] StartX=0 StartY=0 StartZ=0 EndX=0 EndY=38.6 EndZ=0
    g1: Circle CenterX=0 CenterY=38.6 CenterZ=0 NormalX=0 NormalY=0 NormalZ=1 AngleXU=0 Radius=2.5
  constraints (5):
    c: Coincident(g0,g-1)
    c: PointOnObject(g0,g-2)
    c: DistanceY(g0,g0) = 38.6
    c: Diameter(g1) = 5
    c: Coincident(g1,g0)
FEATURE [Part::Extrusion] Extrude020  label="Extrude foro anteriore M3x5x6"
  Base = -> Sketch023
  Dir = (1,0,0)
  DirMode = 2
  FaceMakerClass = Part::FaceMakerBullseye
  FaceMakerMode = 3
  LengthFwd = -6.2
  LengthRev = 0
  Solid = true
  Symmetric = false
FEATURE [Sketcher::SketchObject] Sketch024  label="fori per viti frontale"
  ArcFitTolerance = 1e-06
  AttachmentSupport = -> [YZ_Plane]
  FullyConstrained = true
  MakeInternals = false
  MapMode = 5
  Placement = pos=(0,0,0) rot=(0.57735,0.57735,0.57735;2.0944rad)
  sketch-geometry (9):
    g0: LineSegment [constr] StartX=-10.3 StartY=30.721 StartZ=0 EndX=10.3 EndY=30.721 EndZ=0
    g1: LineSegment [constr] StartX=10.3 StartY=30.721 StartZ=0 EndX=10.3 EndY=10.121 EndZ=0
    g2: LineSegment [constr] StartX=10.3 StartY=10.121 StartZ=0 EndX=-10.3 EndY=10.121 EndZ=0
    g3: LineSegment [constr] StartX=-10.3 StartY=10.121 StartZ=0 EndX=-10.3 EndY=30.721 EndZ=0
    g4: LineSegment [constr] StartX=0 StartY=0 StartZ=0 EndX=0 EndY=10.121 EndZ=0
    g5: Circle CenterX=-10.3 CenterY=30.721 CenterZ=0 NormalX=0 NormalY=0 NormalZ=1 AngleXU=0 Radius=2
    g6: Circle CenterX=10.3 CenterY=30.721 CenterZ=0 NormalX=0 NormalY=0 NormalZ=1 AngleXU=0 Radius=2
    g7: Circle CenterX=-10.3 CenterY=10.121 CenterZ=0 NormalX=0 NormalY=0 NormalZ=1 AngleXU=0 Radius=2
    g8: Circle CenterX=10.3 CenterY=10.121 CenterZ=0 NormalX=0 NormalY=0 NormalZ=1 AngleXU=0 Radius=2
  constraints (22):
    c: Horizontal(g0)
    c: Coincident(g1,g0)
    c: Vertical(g1)
    c: Coincident(g2,g1)
    c: Horizontal(g2)
    c: Coincident(g3,g2)
    c: Coincident(g3,g0)
    c: Vertical(g3)
    c: DistanceX(g0,g0) = 20.6
    c: DistanceY(g3,g3) = 20.6
    c: Coincident(g4,g-1)
    c: PointOnObject(g4,g-2)
    c: DistanceY(g4,g4) = 10.121
    c: Symmetric(g2,g2,g4)
    c: Diameter(g5) = 4
    c: Diameter(g6) = 4
    c: Diameter(g7) = 4
    c: Diameter(g8) = 4
    c: Coincident(g5,g0)
    c: Coincident(g6,g0)
    c: Coincident(g7,g2)
    c: Coincident(g8,g1)
FEATURE [Part::Extrusion] Extrude021  label="Extrude fori per viti frontale"
  Base = -> Sketch024
  Dir = (1,0,0)
  DirMode = 2
  FaceMakerClass = Part::FaceMakerBullseye
  FaceMakerMode = 3
  LengthFwd = -2.4
  LengthRev = 0
  Solid = true
  Symmetric = false
FEATURE [Sketcher::SketchObject] Sketch025  label="foro per filo CAM"
  ArcFitTolerance = 1e-06
  AttachmentSupport = -> [XZ_Plane]
  ExternalGeometry = -> [Sketch]
  FullyConstrained = true
  MakeInternals = false
  MapMode = 5
  Placement = pos=(0,0,0) rot=(1,0,0;1.5708rad)
  sketch-geometry (4):
    g0: LineSegment StartX=-44.6 StartY=41.2 StartZ=0 EndX=-44.6 EndY=36.4 EndZ=0
    g1: LineSegment StartX=-44.6 StartY=36.4 StartZ=0 EndX=-54.6 EndY=36.4 EndZ=0
    g2: LineSegment StartX=-54.6 StartY=36.4 StartZ=0 EndX=-50.4 EndY=41.2 EndZ=0
    g3: LineSegment StartX=-50.4 StartY=41.2 StartZ=0 EndX=-44.6 EndY=41.2 EndZ=0
  constraints (11):
    c: Vertical(g0)
    c: Coincident(g1,g0)
    c: Horizontal(g1)
    c: Coincident(g2,g1)
    c: Coincident(g3,g2)
    c: Coincident(g3,g0)
    c: Horizontal(g3)
    c: Coincident(g0,g-3)
    c: DistanceY(g0,g-4) = 0
    c: DistanceX(g3,g3) = 5.8
    c: DistanceX(g1,g1) = 10
FEATURE [Part::Extrusion] Extrude022  label="Extrude foro per filo CAM dx"
  Base = -> Sketch025
  Dir = (0,-1,2e-16)
  DirMode = 2
  FaceMakerClass = Part::FaceMakerBullseye
  FaceMakerMode = 3
  LengthFwd = 4.9
  LengthRev = 0
  Placement = pos=(0,6.95,0) rot=(0,0,1;0rad)
  Solid = true
  Symmetric = true
FEATURE [Part::Extrusion] Extrude023  label="Extrude foro per filo CAM sx"
  Base = -> Sketch025
  Dir = (0,-1,2e-16)
  DirMode = 2
  FaceMakerClass = Part::FaceMakerBullseye
  FaceMakerMode = 3
  LengthFwd = 4.9
  LengthRev = 0
  Placement = pos=(0,-6.95,0) rot=(0,0,1;0rad)
  Solid = true
  Symmetric = true
FEATURE [Sketcher::SketchObject] Sketch026  label="foro sotto anteriore M3x5x6"
  ArcFitTolerance = 1e-06
  AttachmentSupport = -> [XY_Plane]
  FullyConstrained = true
  MakeInternals = false
  MapMode = 5
  sketch-geometry (2):
    g0: LineSegment [constr] StartX=0 StartY=0 StartZ=0 EndX=-16.5 EndY=0 EndZ=0
    g1: Circle CenterX=-16.5 CenterY=0 CenterZ=0 NormalX=0 NormalY=0 NormalZ=1 AngleXU=0 Radius=2.5
  constraints (5):
    c: Distance(g0) = 16.5
    c: Coincident(g0,g-1)
    c: PointOnObject(g0,g-1)
    c: Diameter(g1) = 5
    c: Coincident(g0,g1)
FEATURE [Sketcher::SketchObject] Sketch027  label="foro sotto posteriore M3x5x6"
  ArcFitTolerance = 1e-06
  AttachmentSupport = -> [XY_Plane]
  ExternalGeometry = -> [Sketch]
  FullyConstrained = true
  MakeInternals = false
  MapMode = 5
  sketch-geometry (2):
    g0: LineSegment [constr] StartX=-82.8 StartY=2e-16 StartZ=0 EndX=-71.3 EndY=2e-16 EndZ=0
    g1: Circle CenterX=-71.3 CenterY=2e-16 CenterZ=0 NormalX=0 NormalY=0 NormalZ=1 AngleXU=0 Radius=2.5
  constraints (5):
    c: Distance(g0) = 11.5
    c: Coincident(g0,g-3)
    c: PointOnObject(g0,g-3)
    c: Diameter(g1) = 5
    c: Coincident(g1,g0)
FEATURE [Sketcher::SketchObject] Sketch029  label="fori sotto impugnatura"
  ArcFitTolerance = 1e-06
  AttachmentSupport = -> [XY_Plane]
  ExternalGeometry = -> [Sketch]
  FullyConstrained = true
  MakeInternals = false
  MapMode = 5
  sketch-geometry (15):
    g0: LineSegment [constr] StartX=-175.232 StartY=-1.83e-14 StartZ=0 EndX=-191.232 EndY=0 EndZ=0
    g1: Circle CenterX=-191.232 CenterY=0 CenterZ=0 NormalX=0 NormalY=0 NormalZ=1 AngleXU=0 Radius=3.95
    g2: LineSegment [constr] StartX=-175.232 StartY=-1.83e-14 StartZ=0 EndX=-204.275 EndY=0 EndZ=0
    g3: LineSegment StartX=-204.275 StartY=3.525 StartZ=0 EndX=-204.275 EndY=-3.525 EndZ=0
    g4: LineSegment StartX=-205.4 StartY=-4.65 StartZ=0 EndX=-206.65 EndY=-4.65 EndZ=0
    g5: LineSegment StartX=-207.775 StartY=-3.525 StartZ=0 EndX=-207.775 EndY=3.525 EndZ=0
    g6: LineSegment StartX=-206.65 StartY=4.65 StartZ=0 EndX=-205.4 EndY=4.65 EndZ=0
    g7: ArcOfCircle CenterX=-206.65 CenterY=3.525 CenterZ=0 NormalX=0 NormalY=0 NormalZ=1 AngleXU=0 Radius=1.125 StartAngle=1.5708 EndAngle=3.14159
    g8: GeomPoint [constr] X=-207.775 Y=4.65 Z=0
    g9: ArcOfCircle CenterX=-205.4 CenterY=3.525 CenterZ=0 NormalX=0 NormalY=0 NormalZ=1 AngleXU=0 Radius=1.125 StartAngle=0 EndAngle=1.5708
    g10: GeomPoint [constr] X=-204.275 Y=4.65 Z=0
    g11: ArcOfCircle CenterX=-205.4 CenterY=-3.525 CenterZ=0 NormalX=0 NormalY=0 NormalZ=1 AngleXU=0 Radius=1.125 StartAngle=4.71239 EndAngle=6.28319
    g12: GeomPoint [constr] X=-204.275 Y=-4.65 Z=0
    g13: ArcOfCircle CenterX=-206.65 CenterY=-3.525 CenterZ=0 NormalX=0 NormalY=0 NormalZ=1 AngleXU=0 Radius=1.125 StartAngle=3.14159 EndAngle=4.71239
    g14: GeomPoint [constr] X=-207.775 Y=-4.65 Z=0
  constraints (35):
    c: Distance(g0) = 16
    c: Coincident(g0,g-3)
    c: PointOnObject(g0,g-1)
    c: Diameter(g1) = 7.9
    c: Coincident(g1,g0)
    c: Coincident(g2,g0)
    c: PointOnObject(g2,g-1)
    c: Vertical(g3)
    c: Horizontal(g4)
    c: Vertical(g5)
    c: Horizontal(g6)
    c: DistanceY(g12,g10) = 9.3
    c: DistanceX(g8,g10) = 3.5
    c: Symmetric(g10,g12,g2)
    c: PointOnObject(g8,g5)
    c: PointOnObject(g8,g6)
    c: Tangent(g5,g7) = 1.5708
    c: Tangent(g6,g7) = 1.5708
    c: PointOnObject(g10,g3)
    c: PointOnObject(g10,g6)
    c: Tangent(g3,g9) = 1.5708
    c: Tangent(g6,g9) = 1.5708
    c: PointOnObject(g12,g3)
    c: PointOnObject(g12,g4)
    c: Tangent(g3,g11) = 1.5708
    c: Tangent(g4,g11) = 1.5708
    c: PointOnObject(g14,g4)
    c: PointOnObject(g14,g5)
    c: Tangent(g4,g13) = 1.5708
    c: Tangent(g5,g13) = 1.5708
    c: Equal(g7,g9)
    c: Equal(g9,g11)
    c: Equal(g11,g13)
    c: DistanceX(g6,g6) = 1.25
    c: DistanceX(g-5,g5) = 6.8
FEATURE [Sketcher::SketchObject] Sketch030  label="fori superiori per solenoide e oled"
  ArcFitTolerance = 1e-06
  AttachmentSupport = -> [XY_Plane]
  ExternalGeometry = -> [Sketch]
  FullyConstrained = true
  MakeInternals = false
  MapMode = 5
  sketch-geometry (33):
    g0: LineSegment [constr] StartX=-181.6 StartY=1.12e-14 StartZ=0 EndX=-169.91 EndY=0 EndZ=0
    g1: LineSegment [constr] StartX=-169.91 StartY=0 StartZ=0 EndX=-169.91 EndY=-2.6 EndZ=0
    g2: LineSegment [constr] StartX=-169.91 StartY=0 StartZ=0 EndX=-169.91 EndY=2.6 EndZ=0
    g3: LineSegment StartX=-169.91 StartY=4.975 StartZ=0 EndX=-169.91 EndY=8.225 EndZ=0
    g4: LineSegment StartX=-167.535 StartY=10.6 StartZ=0 EndX=-167.285 EndY=10.6 EndZ=0
    g5: LineSegment StartX=-164.91 StartY=8.225 StartZ=0 EndX=-164.91 EndY=4.975 EndZ=0
    g6: LineSegment StartX=-167.285 StartY=2.6 StartZ=0 EndX=-167.535 EndY=2.6 EndZ=0
    g7: LineSegment StartX=-169.91 StartY=-4.975 StartZ=0 EndX=-169.91 EndY=-8.225 EndZ=0
    g8: LineSegment StartX=-167.535 StartY=-10.6 StartZ=0 EndX=-167.285 EndY=-10.6 EndZ=0
    g9: LineSegment StartX=-164.91 StartY=-8.225 StartZ=0 EndX=-164.91 EndY=-4.975 EndZ=0
    g10: LineSegment StartX=-167.285 StartY=-2.6 StartZ=0 EndX=-167.535 EndY=-2.6 EndZ=0
    g11: ArcOfCircle CenterX=-167.535 CenterY=8.225 CenterZ=0 NormalX=0 NormalY=0 NormalZ=1 AngleXU=0 Radius=2.375 StartAngle=1.5708 EndAngle=3.14159
    g12: GeomPoint [constr] X=-169.91 Y=10.6 Z=0
    g13: ArcOfCircle CenterX=-167.285 CenterY=8.225 CenterZ=0 NormalX=0 NormalY=0 NormalZ=1 AngleXU=0 Radius=2.375 StartAngle=0 EndAngle=1.5708
    g14: GeomPoint [constr] X=-164.91 Y=10.6 Z=0
    g15: ArcOfCircle CenterX=-167.285 CenterY=4.975 CenterZ=0 NormalX=0 NormalY=0 NormalZ=1 AngleXU=0 Radius=2.375 StartAngle=4.71239 EndAngle=6.28319
    g16: GeomPoint [constr] X=-164.91 Y=2.6 Z=0
    g17: ArcOfCircle CenterX=-167.535 CenterY=4.975 CenterZ=0 NormalX=0 NormalY=0 NormalZ=1 AngleXU=0 Radius=2.375 StartAngle=3.14159 EndAngle=4.71239
    g18: GeomPoint [constr] X=-169.91 Y=2.6 Z=0
    g19: ArcOfCircle CenterX=-167.535 CenterY=-4.975 CenterZ=0 NormalX=0 NormalY=0 NormalZ=1 AngleXU=0 Radius=2.375 StartAngle=1.5708 EndAngle=3.14159
    g20: GeomPoint [constr] X=-169.91 Y=-2.6 Z=0
    g21: ArcOfCircle CenterX=-167.285 CenterY=-4.975 CenterZ=0 NormalX=0 NormalY=0 NormalZ=1 AngleXU=0 Radius=2.375 StartAngle=0 EndAngle=1.5708
    g22: GeomPoint [constr] X=-164.91 Y=-2.6 Z=0
    g23: ArcOfCircle CenterX=-167.285 CenterY=-8.225 CenterZ=0 NormalX=0 NormalY=0 NormalZ=1 AngleXU=0 Radius=2.375 StartAngle=4.71239 EndAngle=6.28319
    g24: GeomPoint [constr] X=-164.91 Y=-10.6 Z=0
    g25: ArcOfCircle CenterX=-167.535 CenterY=-8.225 CenterZ=0 NormalX=0 NormalY=0 NormalZ=1 AngleXU=0 Radius=2.375 StartAngle=3.14159 EndAngle=4.71239
    g26: GeomPoint [constr] X=-169.91 Y=-10.6 Z=0
    g27: LineSegment [constr] StartX=-181.6 StartY=1.12e-14 StartZ=0 EndX=-152.209 EndY=0 EndZ=0
    g28: LineSegment [constr] StartX=-181.6 StartY=1.12e-14 StartZ=0 EndX=-130.41 EndY=0 EndZ=0
    g29: LineSegment [constr] StartX=-152.209 StartY=0 StartZ=0 EndX=-152.209 EndY=6.95 EndZ=0
    g30: LineSegment [constr] StartX=-130.41 StartY=0 StartZ=0 EndX=-130.41 EndY=-6.95 EndZ=0
    g31: Circle CenterX=-152.209 CenterY=6.95 CenterZ=0 NormalX=0 NormalY=0 NormalZ=1 AngleXU=0 Radius=2.1
    g32: Circle CenterX=-130.41 CenterY=-6.95 CenterZ=0 NormalX=0 NormalY=0 NormalZ=1 AngleXU=0 Radius=2.1
  constraints (79):
    c: Distance(g0) = 11.69
    c: PointOnObject(g0,g-1)
    c: Coincident(g-4,g0)
    c: Distance(g1) = 2.6
    c: Coincident(g1,g0)
    c: Vertical(g1)
    c: Distance(g2) = 2.6
    c: Coincident(g2,g0)
    c: Vertical(g2)
    c: Distance(g18,g12) = 8
    c: Coincident(g18,g2)
    c: Vertical(g3)
    c: Distance(g14,g12) = 5
    c: Horizontal(g4)
    c: Distance(g16,g14) = 8
    c: Vertical(g5)
    c: Distance(g26,g20) = 8
    c: Coincident(g20,g1)
    c: Vertical(g7)
    c: Distance(g26,g24) = 5
    c: Horizontal(g8)
    c: Distance(g24,g22) = 8
    c: Vertical(g9)
    c: PointOnObject(g12,g3)
    c: PointOnObject(g12,g4)
    c: Tangent(g3,g11) = 1.5708
    c: Tangent(g4,g11) = 1.5708
    c: PointOnObject(g14,g5)
    c: PointOnObject(g14,g4)
    c: Tangent(g5,g13) = 1.5708
    c: Tangent(g4,g13) = 1.5708
    c: PointOnObject(g16,g5)
    c: PointOnObject(g16,g6)
    c: Tangent(g5,g15) = 1.5708
    c: Tangent(g6,g15) = 1.5708
    c: PointOnObject(g18,g3)
    c: PointOnObject(g18,g6)
    c: Tangent(g3,g17) = 1.5708
    c: Tangent(g6,g17) = 1.5708
    c: Equal(g11,g13)
    c: Equal(g13,g15)
    c: Equal(g15,g17)
    c: DistanceX(g4,g4) = 0.25
    c: PointOnObject(g20,g7)
    c: PointOnObject(g20,g10)
    c: Tangent(g7,g19) = -1.5708
    c: Tangent(g10,g19) = -1.5708
    c: PointOnObject(g22,g9)
    c: PointOnObject(g22,g10)
    c: Tangent(g9,g21) = -1.5708
    c: Tangent(g10,g21) = -1.5708
    c: PointOnObject(g24,g9)
    c: PointOnObject(g24,g8)
    c: Tangent(g9,g23) = -1.5708
    c: Tangent(g8,g23) = -1.5708
    c: PointOnObject(g26,g8)
    c: PointOnObject(g26,g7)
    c: Tangent(g8,g25) = -1.5708
    c: Tangent(g7,g25) = -1.5708
    c: Equal(g19,g21)
    c: Equal(g21,g23)
    c: Equal(g23,g25)
    c: DistanceX(g10,g10) = 0.25
    c: Distance(g27) = 29.391
    c: Coincident(g27,g0)
    c: PointOnObject(g27,g-1)
    c: Distance(g28) = 51.19
    c: Coincident(g28,g0)
    c: PointOnObject(g28,g-1)
    c: Distance(g29) = 6.95
    c: Coincident(g29,g27)
    c: Vertical(g29)
    c: Distance(g30) = 6.95
    c: Coincident(g30,g28)
    c: Vertical(g30)
    c: Diameter(g31) = 4.2
    c: Diameter(g32) = 4.2
    c: Coincident(g32,g30)
    c: Coincident(g31,g29)
FEATURE [Sketcher::SketchObject] Sketch031  label="fori inferiori switch pompa"
  ArcFitTolerance = 1e-06
  AttachmentSupport = -> [XY_Plane]
  ExternalGeometry = -> [Sketch]
  FullyConstrained = true
  MakeInternals = false
  MapMode = 5
  sketch-geometry (4):
    g0: LineSegment [constr] StartX=-57.2 StartY=1.9e-15 StartZ=0 EndX=-62.45 EndY=1.9e-15 EndZ=0
    g1: LineSegment [constr] StartX=-62.45 StartY=3.25 StartZ=0 EndX=-62.45 EndY=-3.25 EndZ=0
    g2: Circle CenterX=-62.45 CenterY=3.25 CenterZ=0 NormalX=0 NormalY=0 NormalZ=1 AngleXU=0 Radius=1.6
    g3: Circle CenterX=-62.45 CenterY=-3.25 CenterZ=0 NormalX=0 NormalY=0 NormalZ=1 AngleXU=0 Radius=1.6
  constraints (10):
    c: Distance(g0) = 5.25
    c: Coincident(g0,g-3)
    c: PointOnObject(g0,g-3)
    c: Vertical(g1)
    c: DistanceY(g1,g1) = 6.5
    c: Symmetric(g1,g1,g0)
    c: Diameter(g2) = 3.2
    c: Diameter(g3) = 3.2
    c: Coincident(g2,g1)
    c: Coincident(g3,g1)
FEATURE [Sketcher::SketchObject] Sketch032  label="spazio per PILA 18650"
  ArcFitTolerance = 1e-06
  AttachmentSupport = -> [XY_Plane]
  ExternalGeometry = -> [Sketch]
  FullyConstrained = true
  MakeInternals = false
  MapMode = 5
  sketch-geometry (2):
    g0: LineSegment [constr] StartX=-178.142 StartY=-1.74e-14 StartZ=0 EndX=-191.142 EndY=-1.83e-14 EndZ=0
    g1: Circle CenterX=-191.142 CenterY=-1.83e-14 CenterZ=0 NormalX=0 NormalY=0 NormalZ=1 AngleXU=0 Radius=10.5
  constraints (5):
    c: Distance(g0) = 13
    c: Coincident(g0,g-3)
    c: PointOnObject(g0,g-4)
    c: Diameter(g1) = 21
    c: Coincident(g1,g0)
FEATURE [Part::Extrusion] Extrude030  label="Extrude spazio per PILA 18650"
  Base = -> Sketch032
  Dir = (0,0,1)
  DirLink = -> Sketch [Edge45]
  DirMode = 2
  FaceMakerClass = Part::FaceMakerBullseye
  FaceMakerMode = 3
  LengthFwd = 76
  LengthRev = 0
  Placement = pos=(6,0,-72) rot=(0,0,1;0rad)
  Solid = true
  Symmetric = false
FEATURE [Sketcher::SketchObject] Sketch033  label="fermo per scheda micro"
  ArcFitTolerance = 1e-06
  AttachmentSupport = -> [XZ_Plane]
  ExternalGeometry = -> [Sketch]
  FullyConstrained = true
  MakeInternals = false
  MapMode = 5
  Placement = pos=(0,0,0) rot=(1,0,0;1.5708rad)
  sketch-geometry (12):
    g0: LineSegment StartX=-11.6 StartY=6 StartZ=0 EndX=-4 EndY=6 EndZ=0
    g1: LineSegment StartX=-4 StartY=6 StartZ=0 EndX=-4 EndY=36.4 EndZ=0
    g2: LineSegment StartX=-4 StartY=36.4 StartZ=0 EndX=-11.6 EndY=36.4 EndZ=0
    g3: LineSegment StartX=-11.6 StartY=36.4 StartZ=0 EndX=-11.6 EndY=6 EndZ=0
    g4: LineSegment StartX=-80.11 StartY=11.6 StartZ=0 EndX=-70.51 EndY=11.6 EndZ=0
    g5: LineSegment StartX=-70.51 StartY=11.6 StartZ=0 EndX=-70.51 EndY=6 EndZ=0
    g6: LineSegment StartX=-70.51 StartY=6 StartZ=0 EndX=-80.11 EndY=6 EndZ=0
    g7: LineSegment StartX=-80.11 StartY=6 StartZ=0 EndX=-80.11 EndY=11.6 EndZ=0
    g8: LineSegment StartX=-78.51 StartY=36.4 StartZ=0 EndX=-70.51 EndY=36.4 EndZ=0
    g9: LineSegment StartX=-70.51 StartY=36.4 StartZ=0 EndX=-70.51 EndY=30.8 EndZ=0
    g10: LineSegment StartX=-70.51 StartY=30.8 StartZ=0 EndX=-78.51 EndY=30.8 EndZ=0
    g11: LineSegment StartX=-78.51 StartY=30.8 StartZ=0 EndX=-78.51 EndY=36.4 EndZ=0
  constraints (33):
    c: Horizontal(g0)
    c: Coincident(g1,g0)
    c: Coincident(g2,g1)
    c: Horizontal(g2)
    c: Coincident(g3,g2)
    c: Coincident(g3,g0)
    c: Vertical(g3)
    c: DistanceX(g2,g2) = 7.6
    c: Coincident(g1,g-3)
    c: Coincident(g0,g-3)
    c: Horizontal(g4)
    c: Coincident(g5,g4)
    c: Vertical(g5)
    c: Coincident(g6,g5)
    c: Horizontal(g6)
    c: Coincident(g7,g6)
    c: Coincident(g7,g4)
    c: Vertical(g7)
    c: DistanceY(g5,g5) = 5.6
    c: DistanceX(g4,g4) = 9.6
    c: Coincident(g9,g8)
    c: Vertical(g9)
    c: Coincident(g10,g9)
    c: Horizontal(g10)
    c: Coincident(g11,g10)
    c: Coincident(g11,g8)
    c: Vertical(g11)
    c: DistanceY(g9,g9) = 5.6
    c: DistanceX(g10,g10) = 8
    c: Coincident(g4,g-4)
    c: DistanceX(g4,g10) = 1.6
    c: Horizontal(g8)
    c: DistanceY(g8,g1) = 0
FEATURE [Sketcher::SketchObject] Sketch034  label="buchi guida rail"
  ArcFitTolerance = 1e-06
  AttachmentSupport = -> [XY_Plane]
  ExternalGeometry = -> [Sketch]
  FullyConstrained = true
  MakeInternals = false
  MapMode = 5
  sketch-geometry (6):
    g0: LineSegment [constr] StartX=-100.8 StartY=9.1e-15 StartZ=0 EndX=-93.3 EndY=0 EndZ=0
    g1: LineSegment [constr] StartX=-93.3 StartY=0 StartZ=0 EndX=-73.3 EndY=0 EndZ=0
    g2: LineSegment [constr] StartX=-73.3 StartY=0 StartZ=0 EndX=-53.3 EndY=0 EndZ=0
    g3: Circle CenterX=-93.3 CenterY=0 CenterZ=0 NormalX=0 NormalY=0 NormalZ=1 AngleXU=0 Radius=2.5
    g4: Circle CenterX=-73.3 CenterY=0 CenterZ=0 NormalX=0 NormalY=0 NormalZ=1 AngleXU=0 Radius=2.5
    g5: Circle CenterX=-53.3 CenterY=0 CenterZ=0 NormalX=0 NormalY=0 NormalZ=1 AngleXU=0 Radius=2.5
  constraints (15):
    c: Distance(g0) = 7.5
    c: Coincident(g0,g-3)
    c: PointOnObject(g0,g-1)
    c: Distance(g1) = 20
    c: Coincident(g1,g0)
    c: PointOnObject(g1,g-1)
    c: Distance(g2) = 20
    c: Coincident(g2,g1)
    c: PointOnObject(g2,g-1)
    c: Diameter(g3) = 5
    c: Diameter(g4) = 5
    c: Diameter(g5) = 5
    c: Coincident(g3,g0)
    c: Coincident(g4,g1)
    c: Coincident(g5,g2)
FEATURE [Part::Extrusion] Extrude032  label="Extrude buchi guida rail"
  Base = -> Sketch034
  Dir = (0,0,1)
  DirMode = 2
  FaceMakerClass = Part::FaceMakerBullseye
  FaceMakerMode = 3
  LengthFwd = -6.2
  LengthRev = 0
  Placement = pos=(0,0,43.2) rot=(0,0,1;0rad)
  Solid = true
  Symmetric = false
FEATURE [Part::Extrusion] Extrude033  label="Extrude fori superiori per solenoide e oled001"
  Base = -> Sketch030
  Dir = (0,0,1)
  DirMode = 2
  FaceMakerClass = Part::FaceMakerBullseye
  FaceMakerMode = 3
  LengthFwd = -4.8
  LengthRev = 0
  Placement = pos=(0,0,41.2) rot=(0,0,1;0rad)
  Solid = true
  Symmetric = false
FEATURE [Part::Extrusion] Extrude034  label="Extrude fori sotto impugnatura001"
  Base = -> Sketch029
  Dir = (0,0,1)
  DirMode = 2
  FaceMakerClass = Part::FaceMakerBullseye
  FaceMakerMode = 3
  LengthFwd = 5
  LengthRev = 0
  Placement = pos=(0,0,-83) rot=(0,0,1;0rad)
  Solid = true
  Symmetric = false
FEATURE [Part::Extrusion] Extrude035  label="Extrude fori inferiori switch pompa001"
  Base = -> Sketch031
  Dir = (0,0,1)
  DirMode = 2
  FaceMakerClass = Part::FaceMakerBullseye
  FaceMakerMode = 3
  LengthFwd = 4
  LengthRev = 0
  Placement = pos=(0,0,-1.7) rot=(0,0,1;0rad)
  Solid = true
  Symmetric = false
FEATURE [Part::Extrusion] Extrude036  label="Extrude foro sotto posteriore M3x5x007"
  Base = -> Sketch027
  Dir = (0,0,1)
  DirMode = 2
  FaceMakerClass = Part::FaceMakerBullseye
  FaceMakerMode = 3
  LengthFwd = 6.2
  LengthRev = 0
  Placement = pos=(0,0,-9.6) rot=(0,0,1;0rad)
  Solid = true
  Symmetric = false
FEATURE [Part::Extrusion] Extrude037  label="Extrude foro sotto anteriore M3x5x007"
  Base = -> Sketch026
  Dir = (0,0,1)
  DirMode = 2
  FaceMakerClass = Part::FaceMakerBullseye
  FaceMakerMode = 3
  LengthFwd = 6.2
  LengthRev = 0
  Solid = true
  Symmetric = false
FEATURE [Sketcher::SketchObject] Sketch035  label="foro per fissaggio micro"
  ArcFitTolerance = 1e-06
  AttachmentSupport = -> [XZ_Plane]
  ExternalGeometry = -> [Sketch,Sketch033]
  FullyConstrained = true
  MakeInternals = false
  MapMode = 5
  Placement = pos=(0,0,0) rot=(1,0,0;1.5708rad)
  sketch-geometry (3):
    g0: Circle CenterX=-7.8 CenterY=21.2 CenterZ=0 NormalX=0 NormalY=0 NormalZ=1 AngleXU=0 Radius=1.6
    g1: GeomPoint [constr] X=-4 Y=21.2 Z=0
    g2: LineSegment [constr] StartX=-4 StartY=21.2 StartZ=0 EndX=-11.6 EndY=21.2 EndZ=0
  constraints (6):
    c: Diameter(g0) = 3.2
    c: Symmetric(g-3,g-3,g1)
    c: Coincident(g2,g1)
    c: Horizontal(g2)
    c: DistanceX(g-4,g2) = 0
    c: Symmetric(g2,g1,g0)
FEATURE [Part::Extrusion] Extrude038  label="Extrude foro per fissaggio micro"
  Base = -> Sketch035
  Dir = (0,-1,2e-16)
  DirMode = 2
  FaceMakerClass = Part::FaceMakerBullseye
  FaceMakerMode = 3
  LengthFwd = 3
  LengthRev = 0
  Placement = pos=(0,8.6,0) rot=(0,0,1;0rad)
  Solid = true
  Symmetric = false
FEATURE [Sketcher::SketchObject] Sketch036  label="supporto per alimentatore"
  ArcFitTolerance = 1e-06
  AttachmentSupport = -> [XZ_Plane]
  ExternalGeometry = -> [Sketch,Sketch016,Sketch022]
  FullyConstrained = true
  MakeInternals = false
  MapMode = 5
  Placement = pos=(0,0,0) rot=(1,0,0;1.5708rad)
  sketch-geometry (5):
    g0: LineSegment StartX=-211.843 StartY=-50.0944 StartZ=0 EndX=-211.843 EndY=-80.4316 EndZ=0
    g1: LineSegment StartX=-211.843 StartY=-50.0944 StartZ=0 EndX=-207.775 EndY=-41.3701 EndZ=0
    g2: LineSegment [constr] StartX=-209.443 StartY=-50.0944 StartZ=0 EndX=-209.443 EndY=-80.4316 EndZ=0
    g3: LineSegment StartX=-207.775 StartY=-41.3701 StartZ=0 EndX=-207.775 EndY=-80.4316 EndZ=0
    g4: LineSegment StartX=-211.843 StartY=-80.4316 StartZ=0 EndX=-207.775 EndY=-80.4316 EndZ=0
  constraints (15):
    c: Vertical(g0)
    c: Coincident(g1,g0)
    c: Vertical(g2)
    c: Tangent(g2,g-5)
    c: Coincident(g3,g1)
    c: Vertical(g3)
    c: DistanceY(g-3,g3) = -2
    c: Tangent(g1,g-8)
    c: DistanceY(g-3,g0) = -2
    c: Coincident(g4,g0)
    c: Coincident(g4,g3)
    c: Tangent(g0,g-6)
    c: DistanceY(g-3,g2) = -2
    c: DistanceY(g2,g0) = 0
    c: DistanceX(g-3,g3) = 6.8
FEATURE [Part::Extrusion] Extrude039  label="Extrude039 supporto alimentatore"
  Base = -> Sketch036
  Dir = (0,-1,2e-16)
  DirMode = 2
  FaceMakerClass = Part::FaceMakerBullseye
  FaceMakerMode = 3
  LengthFwd = 25.2
  LengthRev = 0
  Solid = true
  Symmetric = true
FEATURE [Sketcher::SketchObject] Sketch037  label="scavo per alimentatore"
  ArcFitTolerance = 1e-06
  AttachmentSupport = -> [XZ_Plane]
  ExternalGeometry = -> [Sketch036]
  FullyConstrained = true
  MakeInternals = false
  MapMode = 5
  Placement = pos=(0,0,0) rot=(1,0,0;1.5708rad)
  sketch-geometry (4):
    g0: LineSegment StartX=-209.575 StartY=-50.4316 StartZ=0 EndX=-209.575 EndY=-80.4316 EndZ=0
    g1: LineSegment StartX=-209.575 StartY=-50.4316 StartZ=0 EndX=-207.775 EndY=-50.4316 EndZ=0
    g2: LineSegment StartX=-207.775 StartY=-50.4316 StartZ=0 EndX=-207.775 EndY=-80.4316 EndZ=0
    g3: LineSegment StartX=-207.775 StartY=-80.4316 StartZ=0 EndX=-209.575 EndY=-80.4316 EndZ=0
  constraints (11):
    c: Vertical(g0)
    c: Coincident(g1,g0)
    c: Horizontal(g1)
    c: Coincident(g2,g1)
    c: Vertical(g2)
    c: Coincident(g3,g2)
    c: Coincident(g3,g0)
    c: Horizontal(g3)
    c: DistanceX(g1,g1) = 1.8
    c: Coincident(g2,g-3)
    c: DistanceY(g2,g2) = 30
FEATURE [Part::Extrusion] Extrude040  label="Extrude040 scavo alimentatore"
  Base = -> Sketch037
  Dir = (0,-1,2e-16)
  DirMode = 2
  FaceMakerClass = Part::FaceMakerBullseye
  FaceMakerMode = 3
  LengthFwd = 19.5
  LengthRev = 0
  Solid = true
  Symmetric = true
FEATURE [Part::Extrusion] Extrude031  label="Extrude fermo per scheda micro"
  Base = -> Sketch033
  Dir = (0,-1,2e-16)
  DirMode = 2
  FaceMakerClass = Part::FaceMakerBullseye
  FaceMakerMode = 3
  LengthFwd = 3
  LengthRev = 0
  Placement = pos=(0,8.6,0) rot=(0,0,1;0rad)
  Solid = true
  Symmetric = false
FEATURE [Sketcher::SketchObject] Sketch038  label="scavo driver solenoide"
  ArcFitTolerance = 1e-06
  AttachmentSupport = -> [XZ_Plane]
  ExternalGeometry = -> [Sketch,Sketch036]
  FullyConstrained = true
  MakeInternals = false
  MapMode = 5
  Placement = pos=(0,0,0) rot=(1,0,0;1.5708rad)
  sketch-geometry (7):
    g0: LineSegment StartX=-192.222 StartY=-8.0175 StartZ=0 EndX=-194.941 EndY=-6.74965 EndZ=0
    g1: LineSegment StartX=-194.941 StartY=-6.74965 StartZ=0 EndX=-212.269 EndY=-43.9083 EndZ=0
    g2: LineSegment StartX=-192.222 StartY=-8.0175 StartZ=0 EndX=-188.779 EndY=-9.62345 EndZ=0
    g3: LineSegment StartX=-188.779 StartY=-9.62345 StartZ=0 EndX=-205.357 EndY=-45.1761 EndZ=0
    g4: LineSegment StartX=-205.357 StartY=-45.1761 StartZ=0 EndX=-209.55 EndY=-45.1761 EndZ=0
    g5: LineSegment [constr] StartX=-212.269 StartY=-43.9083 StartZ=0 EndX=-209.55 EndY=-45.1761 EndZ=0
    g6: LineSegment StartX=-212.269 StartY=-43.9083 StartZ=0 EndX=-209.55 EndY=-45.1761 EndZ=0
  constraints (20):
    c: Coincident(g1,g0)
    c: Coincident(g3,g2)
    c: Coincident(g4,g3)
    c: Distance(g2) = 3.8
    c: Distance(g1) = 41
    c: Coincident(g5,g1)
    c: Distance(g5) = 3
    c: Perpendicular(g5,g-3)
    c: Parallel(g1,g-3)
    c: Perpendicular(g1,g0)
    c: Distance(g0) = 3
    c: Coincident(g6,g1)
    c: Parallel(g3,g-3)
    c: Perpendicular(g2,g3)
    c: Coincident(g2,g0)
    c: Perpendicular(g-4,g4)
    c: PointOnObject(g5,g-3)
    c: Distance(g-3,g5) = 9.6
    c: Coincident(g4,g5)
    c: Coincident(g6,g4)
FEATURE [Part::Extrusion] Extrude041  label="Extrude scavo driver solenoide"
  Base = -> Sketch038
  Dir = (0,-1,2e-16)
  DirMode = 2
  FaceMakerClass = Part::FaceMakerBullseye
  FaceMakerMode = 3
  LengthFwd = 20.6
  LengthRev = 0
  Solid = true
  Symmetric = true
FEATURE [Sketcher::SketchObject] Sketch039  label="scavo per cavo usb per micro"
  ArcFitTolerance = 1e-06
  AttachmentSupport = -> [XZ_Plane]
  ExternalGeometry = -> [Sketch,Sketch016]
  FullyConstrained = true
  MakeInternals = false
  MapMode = 5
  Placement = pos=(0,0,0) rot=(1,0,0;1.5708rad)
  sketch-geometry (4):
    g0: LineSegment StartX=-82.51 StartY=36.4 StartZ=0 EndX=-74.51 EndY=36.4 EndZ=0
    g1: LineSegment StartX=-74.51 StartY=36.4 StartZ=0 EndX=-74.51 EndY=30.8 EndZ=0
    g2: LineSegment StartX=-74.51 StartY=30.8 StartZ=0 EndX=-82.51 EndY=30.8 EndZ=0
    g3: LineSegment StartX=-82.51 StartY=30.8 StartZ=0 EndX=-82.51 EndY=36.4 EndZ=0
  constraints (11):
    c: Coincident(g1,g0)
    c: Vertical(g1)
    c: Coincident(g2,g1)
    c: Horizontal(g2)
    c: Coincident(g3,g2)
    c: Coincident(g3,g0)
    c: Vertical(g3)
    c: Tangent(g0,g-3)
    c: Tangent(g2,g-4)
    c: Tangent(g3,g-4)
    c: Tangent(g1,g-4)
FEATURE [Part::Extrusion] Extrude042  label="Extrude scavo per cavo usb per micro"
  Base = -> Sketch039
  Dir = (0,-1,2e-16)
  DirMode = 2
  FaceMakerClass = Part::FaceMakerBullseye
  FaceMakerMode = 3
  LengthFwd = 11.2
  LengthRev = 0
  Solid = true
  Symmetric = true
FEATURE [Sketcher::SketchObject] Sketch040  label="scavo saldature alimentatore connettore 5v"
  ArcFitTolerance = 1e-06
  AttachmentSupport = -> [XZ_Plane]
  ExternalGeometry = -> [Sketch037]
  FullyConstrained = true
  MakeInternals = false
  MapMode = 5
  Placement = pos=(0,0,0) rot=(1,0,0;1.5708rad)
  sketch-geometry (4):
    g0: LineSegment StartX=-211.175 StartY=-52.4316 StartZ=0 EndX=-211.175 EndY=-56.4316 EndZ=0
    g1: LineSegment StartX=-211.175 StartY=-52.4316 StartZ=0 EndX=-209.575 EndY=-52.4316 EndZ=0
    g2: LineSegment StartX=-209.575 StartY=-52.4316 StartZ=0 EndX=-209.575 EndY=-56.4316 EndZ=0
    g3: LineSegment StartX=-209.575 StartY=-56.4316 StartZ=0 EndX=-211.175 EndY=-56.4316 EndZ=0
  constraints (11):
    c: Vertical(g0)
    c: Coincident(g1,g0)
    c: Horizontal(g1)
    c: Coincident(g2,g1)
    c: Coincident(g3,g2)
    c: Coincident(g3,g0)
    c: Horizontal(g3)
    c: DistanceX(g1,g1) = 1.6
    c: DistanceY(g2,g2) = 4
    c: Tangent(g2,g-3)
    c: DistanceY(g1,g-3) = 2
FEATURE [Part::Extrusion] Extrude043  label="Extrude scavo saldature alimentatore connettore 5v"
  Base = -> Sketch040
  Dir = (0,-1,2e-16)
  DirMode = 2
  FaceMakerClass = Part::FaceMakerBullseye
  FaceMakerMode = 3
  LengthFwd = 8
  LengthRev = 0
  Solid = true
  Symmetric = true
FEATURE [Sketcher::SketchObject] Sketch041  label="scavo saldature alimentatore connettore 5v verticali"
  ArcFitTolerance = 1e-06
  AttachmentSupport = -> [XZ_Plane]
  ExternalGeometry = -> [Sketch037]
  FullyConstrained = true
  MakeInternals = false
  MapMode = 5
  Placement = pos=(0,0,0) rot=(1,0,0;1.5708rad)
  sketch-geometry (4):
    g0: LineSegment StartX=-211.175 StartY=-53.6316 StartZ=0 EndX=-209.575 EndY=-53.6316 EndZ=0
    g1: LineSegment StartX=-209.575 StartY=-53.6316 StartZ=0 EndX=-209.575 EndY=-76.6316 EndZ=0
    g2: LineSegment StartX=-209.575 StartY=-76.6316 StartZ=0 EndX=-211.175 EndY=-76.6316 EndZ=0
    g3: LineSegment StartX=-211.175 StartY=-76.6316 StartZ=0 EndX=-211.175 EndY=-53.6316 EndZ=0
  constraints (11):
    c: Horizontal(g0)
    c: Coincident(g1,g0)
    c: Coincident(g2,g1)
    c: Horizontal(g2)
    c: Coincident(g3,g2)
    c: Coincident(g3,g0)
    c: Vertical(g3)
    c: DistanceY(g3,g3) = 23
    c: DistanceX(g0,g0) = 1.6
    c: Tangent(g1,g-3)
    c: DistanceY(g0,g-3) = 3.2
FEATURE [Part::Extrusion] Extrude044  label="Extrude scavo saldature alimentatore connettore 5v verticali"
  Base = -> Sketch041
  Dir = (0,-1,2e-16)
  DirMode = 2
  FaceMakerClass = Part::FaceMakerBullseye
  FaceMakerMode = 3
  LengthFwd = 3.2
  LengthRev = 0
  Placement = pos=(0,8.3,0) rot=(0,0,1;0rad)
  Solid = true
  Symmetric = false
FEATURE [Sketcher::SketchObject] Sketch042  label="fermi per driver solenoide e alimentatore"
  ArcFitTolerance = 1e-06
  AttachmentSupport = -> [XZ_Plane]
  ExternalGeometry = -> [Sketch036,Sketch037,Sketch,Sketch038]
  FullyConstrained = true
  MakeInternals = false
  MapMode = 5
  Placement = pos=(0,0,0) rot=(1,0,0;1.5708rad)
  sketch-geometry (27):
    g0: LineSegment StartX=-200.506 StartY=-25.7811 StartZ=0 EndX=-201.436 EndY=-27.775 EndZ=0
    g1: LineSegment StartX=-201.436 StartY=-27.775 StartZ=0 EndX=-199.442 EndY=-28.7048 EndZ=0
    g2: LineSegment StartX=-199.442 StartY=-28.7048 StartZ=0 EndX=-198.512 EndY=-26.7109 EndZ=0
    g3: LineSegment StartX=-198.512 StartY=-26.7109 StartZ=0 EndX=-200.506 EndY=-25.7811 EndZ=0
    g4: LineSegment StartX=-201.28 StartY=-23.6549 StartZ=0 EndX=-203.562 EndY=-28.5489 EndZ=0
    g5: LineSegment StartX=-203.562 StartY=-28.5489 StartZ=0 EndX=-200.118 EndY=-30.1549 EndZ=0
    g6: LineSegment StartX=-197.992 StartY=-29.381 StartZ=0 EndX=-197.062 EndY=-27.3871 EndZ=0
    g7: LineSegment StartX=-197.836 StartY=-25.2608 StartZ=0 EndX=-201.28 EndY=-23.6549 EndZ=0
    g8: LineSegment [constr] StartX=-198.668 StartY=-30.8311 StartZ=0 EndX=-197.992 EndY=-29.381 EndZ=0
    g9: LineSegment [constr] StartX=-198.668 StartY=-30.8311 StartZ=0 EndX=-200.118 EndY=-30.1549 EndZ=0
    g10: ArcOfCircle CenterX=-198.512 CenterY=-26.7109 CenterZ=0 NormalX=0 NormalY=0 NormalZ=1 AngleXU=0 Radius=1.6 StartAngle=5.84685 EndAngle=7.41765
    g11: GeomPoint [constr] X=-196.386 Y=-25.937 Z=0
    g12: ArcOfCircle CenterX=-199.442 CenterY=-28.7048 CenterZ=0 NormalX=0 NormalY=0 NormalZ=1 AngleXU=0 Radius=1.6 StartAngle=4.27606 EndAngle=5.84685
    g13: GeomPoint [constr] X=-198.668 Y=-30.8311 Z=0
    g14: LineSegment StartX=-207.775 StartY=-46.8316 StartZ=0 EndX=-207.775 EndY=-50.8316 EndZ=0
    g15: LineSegment StartX=-207.775 StartY=-46.8316 StartZ=0 EndX=-203.775 EndY=-46.8316 EndZ=0
    g16: LineSegment StartX=-203.775 StartY=-46.8316 StartZ=0 EndX=-203.775 EndY=-50.8316 EndZ=0
    g17: LineSegment StartX=-207.775 StartY=-50.8316 StartZ=0 EndX=-203.775 EndY=-50.8316 EndZ=0
    g18: LineSegment StartX=-209.375 StartY=-52.4316 StartZ=0 EndX=-203.775 EndY=-52.4316 EndZ=0
    g19: LineSegment StartX=-202.175 StartY=-50.8316 StartZ=0 EndX=-202.175 EndY=-46.8316 EndZ=0
    g20: LineSegment StartX=-203.775 StartY=-45.2316 StartZ=0 EndX=-209.375 EndY=-45.2316 EndZ=0
    g21: LineSegment StartX=-209.375 StartY=-45.2316 StartZ=0 EndX=-209.375 EndY=-52.4316 EndZ=0
    g22: ArcOfCircle CenterX=-203.775 CenterY=-46.8316 CenterZ=0 NormalX=0 NormalY=0 NormalZ=1 AngleXU=0 Radius=1.6 StartAngle=1.8e-15 EndAngle=1.5708
    g23: GeomPoint [constr] X=-202.175 Y=-45.2316 Z=0
    g24: ArcOfCircle CenterX=-203.775 CenterY=-50.8316 CenterZ=0 NormalX=0 NormalY=0 NormalZ=1 AngleXU=0 Radius=1.6 StartAngle=4.71239 EndAngle=6.28319
    g25: GeomPoint [constr] X=-202.175 Y=-52.4316 Z=0
    g26: LineSegment [constr] StartX=-207.775 StartY=-50.4316 StartZ=0 EndX=-207.775 EndY=-50.8316 EndZ=0
  constraints (69):
    c: Coincident(g1,g0)
    c: Coincident(g2,g1)
    c: Coincident(g3,g2)
    c: Coincident(g3,g0)
    c: Parallel(g0,g2)
    c: Perpendicular(g3,g0)
    c: Perpendicular(g1,g0)
    c: Coincident(g5,g4)
    c: Coincident(g7,g4)
    c: Distance(g3) = 2.2
    c: Distance(g2) = 2.2
    c: Parallel(g6,g2)
    c: Parallel(g6,g4)
    c: Perpendicular(g5,g6)
    c: Perpendicular(g7,g6)
    c: Distance(g13,g11) = 5.4
    c: Distance(g5,g13) = 5.4
    c: Coincident(g9,g8)
    c: Distance(g8) = 1.6
    c: Distance(g9) = 1.6
    c: Perpendicular(g9,g8)
    c: Parallel(g8,g6)
    c: Coincident(g8,g13)
    c: Distance(g8,g1) = 1.6
    c: Distance(g9,g1) = 1.6
    c: Tangent(g0,g-5)
    c: Distance(g0,g-6) = 19.2
    c: PointOnObject(g11,g7)
    c: PointOnObject(g11,g6)
    c: Tangent(g7,g10) = -1.5708
    c: Tangent(g6,g10) = -1.5708
    c: PointOnObject(g13,g5)
    c: Tangent(g5,g12) = -1.5708
    c: Tangent(g6,g12) = -1.5708
    c: Equal(g10,g12)
    c: Coincident(g10,g2)
    c: Vertical(g14)
    c: Coincident(g15,g14)
    c: Horizontal(g15)
    c: Coincident(g16,g15)
    c: Vertical(g16)
    c: Coincident(g17,g14)
    c: Coincident(g17,g16)
    c: Horizontal(g17)
    c: Distance(g16) = 4
    c: Distance(g15) = 4
    c: Horizontal(g18)
    c: Vertical(g19)
    c: Horizontal(g20)
    c: Coincident(g21,g20)
    c: Coincident(g21,g18)
    c: Vertical(g21)
    c: Distance(g20,g23) = 7.2
    c: Distance(g25,g23) = 7.2
    c: DistanceY(g18,g14) = 1.6
    c: DistanceX(g18,g14) = 1.6
    c: PointOnObject(g23,g20)
    c: PointOnObject(g23,g19)
    c: Tangent(g20,g22) = -1.5708
    c: Tangent(g19,g22) = -1.5708
    c: PointOnObject(g25,g19)
    c: Tangent(g18,g24) = -1.5708
    c: Tangent(g19,g24) = -1.5708
    c: Equal(g22,g24)
    c: Coincident(g22,g15)
    c: Vertical(g26)
    c: Distance(g26) = 0.4
    c: Coincident(g26,g-4)
    c: Coincident(g14,g26)
FEATURE [Part::Extrusion] Extrude045  label="Extrude fermi per driver solenoide e alimentatore"
  Base = -> Sketch042
  Dir = (0,-1,2e-16)
  DirMode = 2
  FaceMakerClass = Part::FaceMakerBullseye
  FaceMakerMode = 3
  LengthFwd = 25.2
  LengthRev = 0
  Solid = true
  Symmetric = true
FEATURE [Sketcher::SketchObject] Sketch043  label="scavo pulizia fermo alimentatore"
  ArcFitTolerance = 1e-06
  AttachmentSupport = -> [XZ_Plane]
  ExternalGeometry = -> [Sketch042,Sketch036,Sketch037]
  FullyConstrained = true
  MakeInternals = false
  MapMode = 5
  Placement = pos=(0,0,0) rot=(1,0,0;1.5708rad)
  sketch-geometry (6):
    g0: LineSegment StartX=-209.375 StartY=-52.4316 StartZ=0 EndX=-209.375 EndY=-50.4316 EndZ=0
    g1: LineSegment StartX=-209.375 StartY=-50.4316 StartZ=0 EndX=-207.775 EndY=-50.4316 EndZ=0
    g2: LineSegment StartX=-207.775 StartY=-50.4316 StartZ=0 EndX=-207.775 EndY=-45.2316 EndZ=0
    g3: LineSegment StartX=-207.775 StartY=-45.2316 StartZ=0 EndX=-202.175 EndY=-45.2316 EndZ=0
    g4: LineSegment StartX=-202.175 StartY=-45.2316 StartZ=0 EndX=-202.175 EndY=-52.4316 EndZ=0
    g5: LineSegment StartX=-202.175 StartY=-52.4316 StartZ=0 EndX=-209.375 EndY=-52.4316 EndZ=0
  constraints (13):
    c: Vertical(g0)
    c: Coincident(g1,g0)
    c: Coincident(g2,g1)
    c: Coincident(g3,g2)
    c: Coincident(g4,g3)
    c: Coincident(g5,g4)
    c: Coincident(g5,g0)
    c: Horizontal(g5)
    c: Coincident(g0,g-6)
    c: Tangent(g1,g-8)
    c: Tangent(g2,g-4)
    c: Tangent(g3,g-7)
    c: Tangent(g4,g-3)
FEATURE [Part::Extrusion] Extrude046  label="Extrude scavo pulizia fermo alimentatore"
  Base = -> Sketch043
  Dir = (0,-1,2e-16)
  DirMode = 2
  FaceMakerClass = Part::FaceMakerBullseye
  FaceMakerMode = 3
  LengthFwd = 19.5
  LengthRev = 0
  Solid = true
  Symmetric = true
FEATURE [Sketcher::SketchObject] Sketch044  label="buchini per fissaggio oled"
  ArcFitTolerance = 1e-06
  AttachmentSupport = -> [YZ_Plane]
  ExternalGeometry = -> [Sketch]
  FullyConstrained = true
  MakeInternals = false
  MapMode = 5
  Placement = pos=(0,0,0) rot=(0.57735,0.57735,0.57735;2.0944rad)
  sketch-geometry (5):
    g0: LineSegment [constr] StartX=1.5e-14 StartY=67.3588 StartZ=0 EndX=0 EndY=64.3588 EndZ=0
    g1: LineSegment [constr] StartX=0 StartY=64.3588 StartZ=0 EndX=10.4 EndY=64.3588 EndZ=0
    g2: LineSegment [constr] StartX=0 StartY=64.3588 StartZ=0 EndX=-10.4 EndY=64.3588 EndZ=0
    g3: Circle CenterX=10.4 CenterY=64.3588 CenterZ=0 NormalX=0 NormalY=0 NormalZ=1 AngleXU=0 Radius=1.5
    g4: Circle CenterX=-10.4 CenterY=64.3588 CenterZ=0 NormalX=0 NormalY=0 NormalZ=1 AngleXU=0 Radius=1.5
  constraints (13):
    c: Distance(g0) = 3
    c: PointOnObject(g0,g-2)
    c: Coincident(g1,g0)
    c: Horizontal(g1)
    c: Coincident(g2,g0)
    c: Horizontal(g2)
    c: DistanceX(g1,g1) = 10.4
    c: Coincident(g3,g1)
    c: Diameter(g4) = 3
    c: Coincident(g4,g2)
    c: Coincident(g0,g-7)
    c: Equal(g1,g2)
    c: Equal(g4,g3)
FEATURE [Part::Extrusion] Extrude047  label="Extrude buchini per fissaggio oled"
  Base = -> Sketch044
  Dir = (1,0,0)
  DirMode = 2
  FaceMakerClass = Part::FaceMakerBullseye
  FaceMakerMode = 3
  LengthFwd = 10
  LengthRev = 0
  Placement = pos=(-186,0,0) rot=(0,0,1;0rad)
  Solid = true
  Symmetric = false
FEATURE [Sketcher::SketchObject] Sketch046  label="scavo 5x5 neopixel"
  ArcFitTolerance = 1e-06
  AttachmentSupport = -> [YZ_Plane002]
  FullyConstrained = true
  MakeInternals = false
  MapMode = 5
  Placement = pos=(0,0,0) rot=(0.57735,0.57735,0.57735;2.0944rad)
  sketch-geometry (4):
    g0: LineSegment StartX=-2.7 StartY=2.7 StartZ=0 EndX=2.7 EndY=2.7 EndZ=0
    g1: LineSegment StartX=2.7 StartY=2.7 StartZ=0 EndX=2.7 EndY=-2.7 EndZ=0
    g2: LineSegment StartX=2.7 StartY=-2.7 StartZ=0 EndX=-2.7 EndY=-2.7 EndZ=0
    g3: LineSegment StartX=-2.7 StartY=-2.7 StartZ=0 EndX=-2.7 EndY=2.7 EndZ=0
  constraints (11):
    c: Horizontal(g0)
    c: Coincident(g1,g0)
    c: Vertical(g1)
    c: Coincident(g2,g1)
    c: Horizontal(g2)
    c: Coincident(g3,g2)
    c: Coincident(g3,g0)
    c: Vertical(g3)
    c: DistanceX(g0,g0) = 5.4
    c: DistanceY(g1,g1) = 5.4
    c: Symmetric(g0,g1,g-1)
FEATURE [Sketcher::SketchObject] Sketch047  label="scavo 10x10 neopixel corpo"
  ArcFitTolerance = 1e-06
  AttachmentOffset = pos=(0,0,1) rot=(0,0,1;0rad)
  AttachmentSupport = -> [YZ_Plane002]
  FullyConstrained = true
  MakeInternals = false
  MapMode = 5
  Placement = pos=(1,0,0) rot=(0.57735,0.57735,0.57735;2.0944rad)
  sketch-geometry (4):
    g0: LineSegment StartX=-5 StartY=5.1 StartZ=0 EndX=5 EndY=5.1 EndZ=0
    g1: LineSegment StartX=5 StartY=5.1 StartZ=0 EndX=5 EndY=-5.1 EndZ=0
    g2: LineSegment StartX=5 StartY=-5.1 StartZ=0 EndX=-5 EndY=-5.1 EndZ=0
    g3: LineSegment StartX=-5 StartY=-5.1 StartZ=0 EndX=-5 EndY=5.1 EndZ=0
  constraints (11):
    c: Horizontal(g0)
    c: Coincident(g1,g0)
    c: Vertical(g1)
    c: Coincident(g2,g1)
    c: Horizontal(g2)
    c: Coincident(g3,g2)
    c: Coincident(g3,g0)
    c: Vertical(g3)
    c: DistanceX(g0,g0) = 10
    c: DistanceY(g1,g1) = 10.2
    c: Symmetric(g0,g2,g-1)
FEATURE [Sketcher::SketchObject] Sketch048  label="buco per perno blocco neopixel"
  ArcFitTolerance = 1e-06
  AttachmentSupport = -> [XZ_Plane002]
  FullyConstrained = true
  MakeInternals = false
  MapMode = 5
  Placement = pos=(0,0,0) rot=(1,0,0;1.5708rad)
  sketch-geometry (4):
    g0: LineSegment StartX=3 StartY=1.2 StartZ=0 EndX=3 EndY=-1.2 EndZ=0
    g1: LineSegment StartX=3 StartY=-1.2 StartZ=0 EndX=5.4 EndY=-1.2 EndZ=0
    g2: LineSegment StartX=5.4 StartY=-1.2 StartZ=0 EndX=5.4 EndY=1.2 EndZ=0
    g3: LineSegment StartX=5.4 StartY=1.2 StartZ=0 EndX=3 EndY=1.2 EndZ=0
  constraints (11):
    c: Coincident(g1,g0)
    c: Horizontal(g1)
    c: Coincident(g2,g1)
    c: Vertical(g2)
    c: Coincident(g3,g2)
    c: Coincident(g3,g0)
    c: Horizontal(g3)
    c: DistanceX(g1,g1) = 2.4
    c: DistanceY(g2,g2) = 2.4
    c: Symmetric(g0,g0,g-1)
    c: DistanceX(g-1,g0) = 3
FEATURE [Sketcher::SketchObject] Sketch045  label="blocco principale per neopixel"
  ArcFitTolerance = 1e-06
  AttachmentSupport = -> [XZ_Plane002]
  ExternalGeometry = -> [Sketch048]
  FullyConstrained = true
  MakeInternals = false
  MapMode = 5
  Placement = pos=(0,0,0) rot=(1,0,0;1.5708rad)
  sketch-geometry (6):
    g0: LineSegment StartX=0 StartY=5.1 StartZ=0 EndX=0 EndY=-5.1 EndZ=0
    g1: LineSegment StartX=0 StartY=-5.1 StartZ=0 EndX=3 EndY=-5.1 EndZ=0
    g2: LineSegment StartX=7 StartY=-1.1 StartZ=0 EndX=7 EndY=5.1 EndZ=0
    g3: LineSegment StartX=7 StartY=5.1 StartZ=0 EndX=0 EndY=5.1 EndZ=0
    g4: ArcOfCircle CenterX=3 CenterY=-1.1 CenterZ=0 NormalX=0 NormalY=0 NormalZ=1 AngleXU=0 Radius=4 StartAngle=4.71239 EndAngle=6.28319
    g5: GeomPoint [constr] X=7 Y=-5.1 Z=0
  constraints (15):
    c: Vertical(g0)
    c: Coincident(g1,g0)
    c: Horizontal(g1)
    c: Vertical(g2)
    c: Coincident(g3,g2)
    c: Coincident(g3,g0)
    c: Horizontal(g3)
    c: DistanceY(g0,g0) = 10.2
    c: Symmetric(g0,g0,g-1)
    c: DistanceX(g3,g3) = 7
    c: PointOnObject(g5,g2)
    c: PointOnObject(g5,g1)
    c: Tangent(g2,g4) = -1.5708
    c: Tangent(g1,g4) = -1.5708
    c: DistanceX(g-3,g1) = 0
FEATURE [Sketcher::SketchObject] Sketch049  label="rinforzi esterni per corpo neopoixel"
  ArcFitTolerance = 1e-06
  AttachmentSupport = -> [XZ_Plane002]
  ExternalGeometry = -> [Sketch045]
  FullyConstrained = true
  MakeInternals = false
  MapMode = 5
  Placement = pos=(0,0,0) rot=(1,0,0;1.5708rad)
  sketch-geometry (8):
    g0: LineSegment StartX=1 StartY=-4.1 StartZ=0 EndX=2 EndY=-4.1 EndZ=0
    g1: LineSegment StartX=2 StartY=-4.1 StartZ=0 EndX=2 EndY=-5.1 EndZ=0
    g2: LineSegment StartX=2 StartY=-5.1 StartZ=0 EndX=1 EndY=-5.1 EndZ=0
    g3: LineSegment StartX=1 StartY=-5.1 StartZ=0 EndX=1 EndY=-4.1 EndZ=0
    g4: LineSegment StartX=1 StartY=5.1 StartZ=0 EndX=2 EndY=5.1 EndZ=0
    g5: LineSegment StartX=2 StartY=5.1 StartZ=0 EndX=2 EndY=4.1 EndZ=0
    g6: LineSegment StartX=2 StartY=4.1 StartZ=0 EndX=1 EndY=4.1 EndZ=0
    g7: LineSegment StartX=1 StartY=4.1 StartZ=0 EndX=1 EndY=5.1 EndZ=0
  constraints (24):
    c: Horizontal(g0)
    c: Coincident(g1,g0)
    c: Vertical(g1)
    c: Coincident(g2,g1)
    c: Horizontal(g2)
    c: Coincident(g3,g2)
    c: Coincident(g3,g0)
    c: Vertical(g3)
    c: Horizontal(g4)
    c: Coincident(g5,g4)
    c: Vertical(g5)
    c: Coincident(g6,g5)
    c: Horizontal(g6)
    c: Coincident(g7,g6)
    c: Coincident(g7,g4)
    c: Vertical(g7)
    c: DistanceX(g4,g4) = 1
    c: DistanceY(g5,g5) = 1
    c: DistanceX(g0,g0) = 1
    c: DistanceY(g1,g1) = 1
    c: DistanceX(g-3,g4) = 1
    c: DistanceY(g-3,g4) = 0
    c: DistanceX(g-4,g2) = 1
    c: DistanceY(g2,g-4) = 0
FEATURE [Sketcher::SketchObject] Sketch052  label="scavo saldature driver solenoide"
  ArcFitTolerance = 1e-06
  AttachmentSupport = -> [XZ_Plane]
  ExternalGeometry = -> [Sketch038]
  FullyConstrained = true
  MakeInternals = false
  MapMode = 5
  Placement = pos=(0,0,0) rot=(1,0,0;1.5708rad)
  sketch-geometry (4):
    g0: LineSegment StartX=-195.304 StartY=-6.5806 StartZ=0 EndX=-196.994 EndY=-10.2058 EndZ=0
    g1: LineSegment StartX=-196.994 StartY=-10.2058 StartZ=0 EndX=-196.632 EndY=-10.3749 EndZ=0
    g2: LineSegment StartX=-196.632 StartY=-10.3749 StartZ=0 EndX=-194.941 EndY=-6.74965 EndZ=0
    g3: LineSegment StartX=-194.941 StartY=-6.74965 StartZ=0 EndX=-195.304 EndY=-6.5806 EndZ=0
  constraints (11):
    c: Coincident(g1,g0)
    c: Coincident(g2,g1)
    c: Coincident(g3,g2)
    c: Coincident(g3,g0)
    c: Parallel(g2,g0)
    c: Perpendicular(g2,g3)
    c: Perpendicular(g1,g2,g1) = 1.5708
    c: Parallel(g2,g-3)
    c: Distance(g2) = 4
    c: Distance(g3) = 0.4
    c: Coincident(g2,g-3)
FEATURE [Part::Extrusion] Extrude055  label="Extrude scavo saldature driver solenoide"
  Base = -> Sketch052
  Dir = (0,-1,2e-16)
  DirMode = 2
  FaceMakerClass = Part::FaceMakerBullseye
  FaceMakerMode = 3
  LengthFwd = 6
  LengthRev = 0
  Solid = true
  Symmetric = true
FEATURE [Sketcher::SketchObject] Sketch053  label="scavo saldature rumble"
  ArcFitTolerance = 1e-06
  AttachmentSupport = -> [XZ_Plane]
  ExternalGeometry = -> [Sketch019]
  FullyConstrained = true
  MakeInternals = false
  MapMode = 5
  Placement = pos=(0,0,0) rot=(1,0,0;1.5708rad)
  sketch-geometry (4):
    g0: LineSegment StartX=-164.507 StartY=-41.6446 StartZ=0 EndX=-165.743 EndY=-45.4488 EndZ=0
    g1: LineSegment StartX=-165.743 StartY=-45.4488 StartZ=0 EndX=-164.602 EndY=-45.8196 EndZ=0
    g2: LineSegment StartX=-164.602 StartY=-45.8196 StartZ=0 EndX=-163.366 EndY=-42.0154 EndZ=0
    g3: LineSegment StartX=-163.366 StartY=-42.0154 StartZ=0 EndX=-164.507 EndY=-41.6446 EndZ=0
  constraints (11):
    c: Coincident(g1,g0)
    c: Coincident(g2,g1)
    c: Coincident(g3,g2)
    c: Coincident(g3,g0)
    c: Parallel(g0,g2)
    c: Perpendicular(g3,g0)
    c: Perpendicular(g1,g0)
    c: Parallel(g0,g-3)
    c: Distance(g0) = 4
    c: Distance(g1) = 1.2
    c: Coincident(g0,g-3)
FEATURE [Part::Extrusion] Extrude056  label="Extrude scavo saldature rumble"
  Base = -> Sketch053
  Dir = (0,-1,2e-16)
  DirMode = 2
  FaceMakerClass = Part::FaceMakerBullseye
  FaceMakerMode = 3
  LengthFwd = 8.4
  LengthRev = 0
  Solid = true
  Symmetric = true
FEATURE [Sketcher::SketchObject] Sketch054  label="scavo saldature alimentatore connettore USB"
  ArcFitTolerance = 1e-06
  AttachmentSupport = -> [XZ_Plane]
  ExternalGeometry = -> [Sketch037]
  FullyConstrained = true
  MakeInternals = false
  MapMode = 5
  Placement = pos=(0,0,0) rot=(1,0,0;1.5708rad)
  sketch-geometry (4):
    g0: LineSegment StartX=-209.575 StartY=-80.4316 StartZ=0 EndX=-210.375 EndY=-80.4316 EndZ=0
    g1: LineSegment StartX=-210.375 StartY=-80.4316 StartZ=0 EndX=-210.375 EndY=-72.4316 EndZ=0
    g2: LineSegment StartX=-210.375 StartY=-72.4316 StartZ=0 EndX=-209.575 EndY=-72.4316 EndZ=0
    g3: LineSegment StartX=-209.575 StartY=-72.4316 StartZ=0 EndX=-209.575 EndY=-80.4316 EndZ=0
  constraints (11):
    c: Horizontal(g0)
    c: Coincident(g1,g0)
    c: Vertical(g1)
    c: Coincident(g2,g1)
    c: Horizontal(g2)
    c: Coincident(g3,g2)
    c: Coincident(g3,g0)
    c: Vertical(g3)
    c: DistanceX(g0,g0) = 0.8
    c: DistanceY(g3,g3) = 8
    c: Coincident(g0,g-4)
FEATURE [Part::Extrusion] Extrude057  label="Extrude scavo saldature alimentatore connettore USB"
  Base = -> Sketch054
  Dir = (0,-1,2e-16)
  DirMode = 2
  FaceMakerClass = Part::FaceMakerBullseye
  FaceMakerMode = 3
  LengthFwd = 11
  LengthRev = 0
  Solid = true
  Symmetric = true
FEATURE [Sketcher::SketchObject] Sketch055  label="buco interno per micro switch"
  ArcFitTolerance = 1e-06
  AttachmentSupport = -> [XZ_Plane]
  ExternalGeometry = -> [Sketch]
  FullyConstrained = true
  MakeInternals = false
  MapMode = 5
  Placement = pos=(0,0,0) rot=(1,0,0;1.5708rad)
  sketch-geometry (11):
    g0: LineSegment [constr] StartX=-194.483 StartY=34.2854 StartZ=0 EndX=-196.022 EndY=30.0568 EndZ=0
    g1: LineSegment [constr] StartX=-196.022 StartY=30.0568 StartZ=0 EndX=-197.561 EndY=25.8282 EndZ=0
    g2: LineSegment [constr] StartX=-196.022 StartY=30.0568 StartZ=0 EndX=-194.143 EndY=29.3727 EndZ=0
    g3: LineSegment [constr] StartX=-196.022 StartY=30.0568 StartZ=0 EndX=-197.902 EndY=30.7408 EndZ=0
    g4: LineSegment StartX=-196.362 StartY=34.9694 StartZ=0 EndX=-192.604 EndY=33.6014 EndZ=0
    g5: LineSegment StartX=-199.441 StartY=26.5122 StartZ=0 EndX=-195.682 EndY=25.1441 EndZ=0
    g6: LineSegment StartX=-192.604 StartY=33.6014 StartZ=0 EndX=-195.682 EndY=25.1441 EndZ=0
    g7: LineSegment StartX=-196.362 StartY=34.9694 StartZ=0 EndX=-199.441 EndY=26.5122 EndZ=0
    g8: GeomPoint [constr] X=-187.821 Y=29.2 Z=0
    g9: LineSegment [constr] StartX=-188.505 StartY=27.3206 StartZ=0 EndX=-196.022 EndY=30.0568 EndZ=0
    g10: LineSegment [constr] StartX=-187.821 StartY=29.2 StartZ=0 EndX=-188.505 EndY=27.3206 EndZ=0
  constraints (27):
    c: Coincident(g2,g0)
    c: Parallel(g0,g-3)
    c: Tangent(g1,g0) = -1.5708
    c: Perpendicular(g0,g2)
    c: Tangent(g2,g3)
    c: Distance(g0,g1) = 9
    c: Equal(g0,g1)
    c: Distance(g3,g2) = 4
    c: Equal(g2,g3)
    c: Parallel(g3,g4)
    c: Symmetric(g4,g4,g0)
    c: Parallel(g6,g1)
    c: Parallel(g7,g1)
    c: Symmetric(g6,g6,g2)
    c: Symmetric(g5,g5,g1)
    c: Symmetric(g7,g7,g3)
    c: Coincident(g7,g4)
    c: Coincident(g6,g4)
    c: Coincident(g5,g6)
    c: Symmetric(g-3,g-3,g8)
    c: Perpendicular(g-3,g9)
    c: Distance(g9) = 8
    c: Coincident(g3,g9)
    c: Coincident(g10,g8)
    c: Parallel(g10,g-3)
    c: Distance(g10) = 2
    c: Coincident(g10,g9)
FEATURE [Sketcher::SketchObject] Sketch056  label="buco esterno per micro switch"
  ArcFitTolerance = 1e-06
  AttachmentSupport = -> [XZ_Plane]
  ExternalGeometry = -> [Sketch055]
  FullyConstrained = true
  MakeInternals = false
  MapMode = 5
  Placement = pos=(0,0,0) rot=(1,0,0;1.5708rad)
  sketch-geometry (17):
    g0: GeomPoint [constr] X=-194.143 Y=29.3727 Z=0
    g1: GeomPoint [constr] X=-194.483 Y=34.2854 Z=0
    g2: GeomPoint [constr] X=-197.902 Y=30.7408 Z=0
    g3: GeomPoint [constr] X=-197.561 Y=25.8282 Z=0
    g4: GeomPoint [constr] X=-196.022 Y=30.0568 Z=0
    g5: LineSegment [constr] StartX=-194.483 StartY=34.2854 StartZ=0 EndX=-196.022 EndY=30.0568 EndZ=0
    g6: LineSegment [constr] StartX=-196.022 StartY=30.0568 StartZ=0 EndX=-197.561 EndY=25.8282 EndZ=0
    g7: LineSegment [constr] StartX=-197.902 StartY=30.7408 StartZ=0 EndX=-196.022 EndY=30.0568 EndZ=0
    g8: LineSegment [constr] StartX=-196.022 StartY=30.0568 StartZ=0 EndX=-194.143 EndY=29.3727 EndZ=0
    g9: LineSegment [constr] StartX=-195.338 StartY=31.9362 StartZ=0 EndX=-196.022 EndY=30.0568 EndZ=0
    g10: LineSegment [constr] StartX=-196.022 StartY=30.0568 StartZ=0 EndX=-196.706 EndY=28.1774 EndZ=0
    g11: LineSegment [constr] StartX=-196.022 StartY=30.0568 StartZ=0 EndX=-196.821 EndY=30.3475 EndZ=0
    g12: LineSegment [constr] StartX=-196.022 StartY=30.0568 StartZ=0 EndX=-195.223 EndY=29.7661 EndZ=0
    g13: LineSegment StartX=-194.539 StartY=31.6454 StartZ=0 EndX=-195.907 EndY=27.8867 EndZ=0
    g14: LineSegment StartX=-196.137 StartY=32.2269 StartZ=0 EndX=-197.505 EndY=28.4681 EndZ=0
    g15: LineSegment StartX=-196.137 StartY=32.2269 StartZ=0 EndX=-194.539 EndY=31.6454 EndZ=0
    g16: LineSegment StartX=-197.505 StartY=28.4681 StartZ=0 EndX=-195.907 EndY=27.8867 EndZ=0
  constraints (34):
    c: Symmetric(g-5,g-5,g1)
    c: Symmetric(g-5,g-6,g0)
    c: Symmetric(g-6,g-6,g3)
    c: Symmetric(g-5,g-6,g2)
    c: Coincident(g5,g1)
    c: Coincident(g5,g4)
    c: Coincident(g6,g4)
    c: Coincident(g6,g3)
    c: Equal(g5,g6)
    c: Coincident(g7,g2)
    c: Coincident(g7,g4)
    c: Coincident(g8,g4)
    c: Coincident(g8,g0)
    c: Equal(g7,g8)
    c: Coincident(g11,g9)
    c: Coincident(g12,g9)
    c: Tangent(g10,g9) = -1.5708
    c: Perpendicular(g11,g9)
    c: Parallel(g9,g-4)
    c: Equal(g9,g10)
    c: Parallel(g12,g11)
    c: Equal(g11,g12)
    c: Distance(g11,g12) = 1.7
    c: Distance(g9,g10) = 4
    c: Symmetric(g13,g13,g12)
    c: Parallel(g13,g9)
    c: Symmetric(g14,g14,g11)
    c: Symmetric(g15,g15,g9)
    c: Parallel(g15,g11)
    c: Symmetric(g16,g16,g10)
    c: Coincident(g16,g14)
    c: Coincident(g15,g14)
    c: Coincident(g13,g15)
    c: Coincident(g9,g4)
FEATURE [Sketcher::SketchObject] Sketch057  label="buco interno per SWITCH"
  ArcFitTolerance = 1e-06
  AttachmentSupport = -> [XZ_Plane]
  ExternalGeometry = -> [Sketch]
  FullyConstrained = true
  MakeInternals = false
  MapMode = 5
  Placement = pos=(0,0,0) rot=(1,0,0;1.5708rad)
  sketch-geometry (10):
    g0: GeomPoint [constr] X=-187.821 Y=29.2 Z=0
    g1: LineSegment [constr] StartX=-188.505 StartY=27.3206 StartZ=0 EndX=-193.203 EndY=29.0307 EndZ=0
    g2: LineSegment [constr] StartX=-190.809 StartY=35.6086 StartZ=0 EndX=-195.597 EndY=22.4529 EndZ=0
    g3: GeomPoint [constr] X=-193.203 Y=29.0307 Z=0
    g4: LineSegment [constr] StartX=-196.492 StartY=30.2278 StartZ=0 EndX=-189.914 EndY=27.8336 EndZ=0
    g5: LineSegment StartX=-194.098 StartY=36.8056 StartZ=0 EndX=-187.52 EndY=34.4115 EndZ=0
    g6: LineSegment StartX=-194.098 StartY=36.8056 StartZ=0 EndX=-198.886 EndY=23.6499 EndZ=0
    g7: LineSegment StartX=-187.52 StartY=34.4115 StartZ=0 EndX=-192.308 EndY=21.2558 EndZ=0
    g8: LineSegment StartX=-198.886 StartY=23.6499 StartZ=0 EndX=-192.308 EndY=21.2558 EndZ=0
    g9: LineSegment [constr] StartX=-187.821 StartY=29.2 StartZ=0 EndX=-188.505 EndY=27.3206 EndZ=0
  constraints (23):
    c: Symmetric(g-3,g-3,g0)
    c: Perpendicular(g1,g-3)
    c: Parallel(g2,g-3)
    c: Symmetric(g2,g2,g3)
    c: Perpendicular(g2,g4)
    c: Symmetric(g4,g4,g3)
    c: Distance(g2) = 14
    c: Distance(g4) = 7
    c: Distance(g1) = 5
    c: Parallel(g5,g4)
    c: Parallel(g7,g2)
    c: Symmetric(g5,g5,g2)
    c: Symmetric(g6,g6,g4)
    c: Symmetric(g7,g7,g4)
    c: Symmetric(g8,g8,g2)
    c: Coincident(g6,g5)
    c: Coincident(g7,g5)
    c: Coincident(g8,g7)
    c: Coincident(g3,g1)
    c: Coincident(g9,g0)
    c: Parallel(g9,g-3)
    c: Distance(g9) = 2
    c: Coincident(g1,g9)
FEATURE [Sketcher::SketchObject] Sketch058  label="buco esterno per SWITCH"
  ArcFitTolerance = 1e-06
  AttachmentSupport = -> [XZ_Plane]
  ExternalGeometry = -> [Sketch057]
  FullyConstrained = true
  MakeInternals = false
  MapMode = 5
  Placement = pos=(0,0,0) rot=(1,0,0;1.5708rad)
  sketch-geometry (12):
    g0: GeomPoint [constr] X=-190.809 Y=35.6086 Z=0
    g1: GeomPoint [constr] X=-196.492 Y=30.2278 Z=0
    g2: GeomPoint [constr] X=-189.914 Y=27.8336 Z=0
    g3: GeomPoint [constr] X=-195.597 Y=22.4529 Z=0
    g4: GeomPoint [constr] X=-193.203 Y=29.0307 Z=0
    g5: LineSegment [constr] StartX=-192.006 StartY=32.3196 StartZ=0 EndX=-194.4 EndY=25.7418 EndZ=0
    g6: GeomPoint [constr] X=-193.203 Y=29.0307 Z=0
    g7: LineSegment [constr] StartX=-195.082 StartY=29.7148 StartZ=0 EndX=-191.324 EndY=28.3467 EndZ=0
    g8: LineSegment StartX=-193.885 StartY=33.0037 StartZ=0 EndX=-190.127 EndY=31.6356 EndZ=0
    g9: LineSegment StartX=-190.127 StartY=31.6356 StartZ=0 EndX=-192.521 EndY=25.0578 EndZ=0
    g10: LineSegment StartX=-196.28 StartY=26.4258 StartZ=0 EndX=-192.521 EndY=25.0578 EndZ=0
    g11: LineSegment StartX=-193.885 StartY=33.0037 StartZ=0 EndX=-196.28 EndY=26.4258 EndZ=0
  constraints (21):
    c: Symmetric(g-6,g-6,g3)
    c: Symmetric(g-4,g-6,g2)
    c: Symmetric(g-5,g-4,g0)
    c: Symmetric(g-5,g-6,g1)
    c: Symmetric(g1,g2,g4)
    c: Parallel(g5,g-4)
    c: Symmetric(g5,g5,g6)
    c: Perpendicular(g7,g5)
    c: Symmetric(g7,g7,g6)
    c: Distance(g5) = 7
    c: Distance(g7) = 4
    c: Parallel(g8,g7)
    c: Parallel(g11,g5)
    c: Symmetric(g8,g8,g5)
    c: Symmetric(g9,g9,g7)
    c: Symmetric(g10,g10,g5)
    c: Symmetric(g11,g11,g7)
    c: Coincident(g11,g8)
    c: Coincident(g9,g8)
    c: Coincident(g9,g10)
    c: Coincident(g6,g4)
FEATURE [Part::Extrusion] Extrude060  label="Extrude buco interno per SWITCH destro"
  Base = -> Sketch057
  Dir = (0,-1,2e-16)
  DirMode = 2
  FaceMakerClass = Part::FaceMakerBullseye
  FaceMakerMode = 3
  LengthFwd = 13.2
  LengthRev = 0
  Placement = pos=(0,2.6,0) rot=(0,0,1;0rad)
  Solid = true
  Symmetric = false
FEATURE [Part::Extrusion] Extrude061  label="Extrude buco esterno per SWITCH destro"
  Base = -> Sketch058
  Dir = (0,-1,2e-16)
  DirMode = 2
  FaceMakerClass = Part::FaceMakerBullseye
  FaceMakerMode = 3
  LengthFwd = 2
  LengthRev = 0
  Placement = pos=(0,-10.6,0) rot=(0,0,1;0rad)
  Solid = true
  Symmetric = false
FEATURE [Sketcher::SketchObject] Sketch059  label="buco per spazio introduzione SWITCH"
  ArcFitTolerance = 1e-06
  AttachmentSupport = -> [XZ_Plane]
  ExternalGeometry = -> [Sketch057,Sketch010]
  FullyConstrained = true
  MakeInternals = false
  MapMode = 5
  Placement = pos=(0,0,0) rot=(1,0,0;1.5708rad)
  sketch-geometry (8):
    g0: LineSegment [constr] StartX=-201.368 StartY=36.3521 StartZ=0 EndX=-195.094 EndY=34.0687 EndZ=0
    g1: LineSegment [constr] StartX=-194.098 StartY=36.8056 StartZ=0 EndX=-195.094 EndY=34.0687 EndZ=0
    g2: LineSegment StartX=-198.658 StartY=24.2771 StartZ=0 EndX=-199.654 EndY=21.5401 EndZ=0
    g3: LineSegment StartX=-199.654 StartY=21.5401 StartZ=0 EndX=-181.196 EndY=14.822 EndZ=0
    g4: LineSegment StartX=-181.196 StartY=14.822 StartZ=0 EndX=-180.2 EndY=17.559 EndZ=0
    g5: LineSegment StartX=-180.2 StartY=17.559 StartZ=0 EndX=-198.658 EndY=24.2771 EndZ=0
    g6: LineSegment [constr] StartX=-204.932 StartY=26.5605 StartZ=0 EndX=-198.658 EndY=24.2771 EndZ=0
    g7: LineSegment [constr] StartX=-198.658 StartY=24.2771 StartZ=0 EndX=-199.654 EndY=21.5401 EndZ=0
  constraints (20):
    c: Parallel(g1,g-3)
    c: Parallel(g0,g-4)
    c: Coincident(g0,g-4)
    c: Coincident(g1,g-3)
    c: Coincident(g0,g1)
    c: Coincident(g3,g2)
    c: Coincident(g4,g3)
    c: Coincident(g5,g4)
    c: Coincident(g5,g2)
    c: Parallel(g5,g-5)
    c: Parallel(g3,g-5)
    c: Parallel(g4,g-6)
    c: DistanceX(g-6,g4) = 0
    c: Coincident(g6,g-5)
    c: Equal(g6,g0)
    c: Coincident(g7,g6)
    c: Equal(g7,g1)
    c: Tangent(g7,g-3)
    c: Coincident(g2,g6)
    c: Coincident(g2,g7)
FEATURE [Part::Extrusion] Extrude062  label="Extrude buco per spazio introduzione SWITCH"
  Base = -> Sketch059
  Dir = (0,-1,2e-16)
  DirMode = 2
  FaceMakerClass = Part::FaceMakerBullseye
  FaceMakerMode = 3
  LengthFwd = 13.2
  LengthRev = 0
  Solid = true
  Symmetric = true
FEATURE [Part::Extrusion] Extrude063  label="Extrude buco interno per SWITCH sinistro"
  Base = -> Sketch057
  Dir = (0,-1,2e-16)
  DirMode = 2
  FaceMakerClass = Part::FaceMakerBullseye
  FaceMakerMode = 3
  LengthFwd = 13.2
  LengthRev = 0
  Placement = pos=(0,10.6,0) rot=(0,0,1;0rad)
  Solid = true
  Symmetric = false
FEATURE [Part::Extrusion] Extrude064  label="Extrude buco esterno per SWITCH sinistro"
  Base = -> Sketch058
  Dir = (0,-1,2e-16)
  DirMode = 2
  FaceMakerClass = Part::FaceMakerBullseye
  FaceMakerMode = 3
  LengthFwd = 2
  LengthRev = 0
  Placement = pos=(0,12.6,0) rot=(0,0,1;0rad)
  Solid = true
  Symmetric = false
FEATURE [Sketcher::SketchObject] Sketch061  label="struttura esterna blocco switch"
  ArcFitTolerance = 1e-06
  AttachmentSupport = -> [XZ_Plane003]
  FullyConstrained = true
  MakeInternals = false
  MapMode = 5
  Placement = pos=(0,0,0) rot=(1,0,0;1.5708rad)
  sketch-geometry (5):
    g0: LineSegment StartX=-1 StartY=-5.1 StartZ=0 EndX=1 EndY=-5.1 EndZ=0
    g1: LineSegment StartX=1 StartY=-5.1 StartZ=0 EndX=1 EndY=5.1 EndZ=0
    g2: LineSegment StartX=1 StartY=5.1 StartZ=0 EndX=-1 EndY=5.1 EndZ=0
    g3: LineSegment StartX=-1 StartY=5.1 StartZ=0 EndX=-1 EndY=-5.1 EndZ=0
    g4: GeomPoint [constr] X=0 Y=0 Z=0
  constraints (12):
    c: Coincident(g0,g1)
    c: Coincident(g1,g2)
    c: Coincident(g2,g3)
    c: Coincident(g3,g0)
    c: Horizontal(g0)
    c: Horizontal(g2)
    c: Vertical(g1)
    c: Vertical(g3)
    c: Symmetric(g2,g0,g4)
    c: Distance(g1,g3) = 2
    c: Distance(g0,g2) = 10.2
    c: Coincident(g4,g-1)
FEATURE [Sketcher::SketchObject] Sketch062  label="struttura interna blocco switch"
  ArcFitTolerance = 1e-06
  AttachmentSupport = -> [XZ_Plane003]
  ExternalGeometry = -> [Sketch061]
  FullyConstrained = true
  MakeInternals = false
  MapMode = 5
  Placement = pos=(0,0,0) rot=(1,0,0;1.5708rad)
  sketch-geometry (5):
    g0: LineSegment StartX=-1 StartY=3.1 StartZ=0 EndX=-1 EndY=-3.1 EndZ=0
    g1: LineSegment StartX=-1 StartY=-3.1 StartZ=0 EndX=1 EndY=-3.1 EndZ=0
    g2: LineSegment StartX=1 StartY=-3.1 StartZ=0 EndX=1 EndY=3.1 EndZ=0
    g3: LineSegment StartX=1 StartY=3.1 StartZ=0 EndX=-1 EndY=3.1 EndZ=0
    g4: GeomPoint [constr] X=0 Y=0 Z=0
  constraints (12):
    c: Coincident(g0,g1)
    c: Coincident(g1,g2)
    c: Coincident(g2,g3)
    c: Coincident(g3,g0)
    c: Vertical(g0)
    c: Vertical(g2)
    c: Horizontal(g1)
    c: Horizontal(g3)
    c: Symmetric(g2,g0,g4)
    c: Coincident(g4,g-1)
    c: Distance(g0) = 6.2
    c: Equal(g3,g-3)
FEATURE [Sketcher::SketchObject] Sketch063  label="blocchi tra switch"
  ArcFitTolerance = 1e-06
  AttachmentSupport = -> [XZ_Plane003]
  ExternalGeometry = -> [Sketch061,Sketch062]
  FullyConstrained = true
  MakeInternals = false
  MapMode = 5
  Placement = pos=(0,0,0) rot=(1,0,0;1.5708rad)
  sketch-geometry (8):
    g0: LineSegment StartX=-3 StartY=5.1 StartZ=0 EndX=-1 EndY=5.1 EndZ=0
    g1: LineSegment StartX=-1 StartY=5.1 StartZ=0 EndX=-1 EndY=3.1 EndZ=0
    g2: LineSegment StartX=-1 StartY=3.1 StartZ=0 EndX=-3 EndY=3.1 EndZ=0
    g3: LineSegment StartX=-3 StartY=3.1 StartZ=0 EndX=-3 EndY=5.1 EndZ=0
    g4: LineSegment StartX=-3 StartY=-3.1 StartZ=0 EndX=-1 EndY=-3.1 EndZ=0
    g5: LineSegment StartX=-1 StartY=-3.1 StartZ=0 EndX=-1 EndY=-5.1 EndZ=0
    g6: LineSegment StartX=-1 StartY=-5.1 StartZ=0 EndX=-3 EndY=-5.1 EndZ=0
    g7: LineSegment StartX=-3 StartY=-5.1 StartZ=0 EndX=-3 EndY=-3.1 EndZ=0
  constraints (20):
    c: Horizontal(g0)
    c: Coincident(g1,g0)
    c: Coincident(g2,g1)
    c: Horizontal(g2)
    c: Coincident(g3,g2)
    c: Coincident(g3,g0)
    c: Vertical(g3)
    c: Horizontal(g4)
    c: Coincident(g5,g4)
    c: Coincident(g6,g5)
    c: Horizontal(g6)
    c: Coincident(g7,g6)
    c: Coincident(g7,g4)
    c: Vertical(g7)
    c: Coincident(g0,g-4)
    c: Coincident(g1,g-5)
    c: Coincident(g4,g-6)
    c: Coincident(g5,g-7)
    c: Distance(g0) = 2
    c: Distance(g4) = 2
FEATURE [Sketcher::SketchObject] Sketch066  label="piano per rampino"
  ArcFitTolerance = 1e-06
  AttachmentSupport = -> [XZ_Plane002]
  ExternalGeometry = -> [Sketch045]
  FullyConstrained = true
  MakeInternals = false
  MapMode = 5
  Placement = pos=(0,0,0) rot=(1,0,0;1.5708rad)
  sketch-geometry (4):
    g0: LineSegment StartX=5.4 StartY=5.1 StartZ=0 EndX=5.4 EndY=3.9 EndZ=0
    g1: LineSegment StartX=5.4 StartY=3.9 StartZ=0 EndX=7 EndY=3.9 EndZ=0
    g2: LineSegment StartX=7 StartY=3.9 StartZ=0 EndX=7 EndY=5.1 EndZ=0
    g3: LineSegment StartX=7 StartY=5.1 StartZ=0 EndX=5.4 EndY=5.1 EndZ=0
  constraints (11):
    c: Coincident(g0,g1)
    c: Coincident(g1,g2)
    c: Coincident(g2,g3)
    c: Coincident(g3,g0)
    c: Vertical(g0)
    c: Vertical(g2)
    c: Horizontal(g1)
    c: Horizontal(g3)
    c: Distance(g0,g2) = 1.6
    c: Distance(g1,g3) = 1.2
    c: Coincident(g2,g-3)
FEATURE [Sketcher::SketchObject] Sketch064  label="rampini_per_serraggio_struttura"
  ArcFitTolerance = 1e-06
  AttachmentSupport = -> [XZ_Plane002]
  ExternalGeometry = -> [Sketch066,Sketch045]
  FullyConstrained = true
  MakeInternals = false
  MapMode = 5
  Placement = pos=(0,0,0) rot=(1,0,0;1.5708rad)
  sketch-geometry (7):
    g0: LineSegment StartX=7 StartY=5.1 StartZ=0 EndX=7 EndY=3.9 EndZ=0
    g1: LineSegment StartX=7 StartY=3.9 StartZ=0 EndX=9 EndY=3.9 EndZ=0
    g2: LineSegment StartX=7 StartY=5.1 StartZ=0 EndX=7 EndY=5.1 EndZ=0
    g3: LineSegment StartX=7 StartY=5.1 StartZ=0 EndX=7 EndY=7.5 EndZ=0
    g4: LineSegment StartX=9 StartY=5.1 StartZ=0 EndX=9 EndY=3.9 EndZ=0
    g5: LineSegment StartX=7 StartY=7.5 StartZ=0 EndX=9 EndY=7.5 EndZ=0
    g6: LineSegment StartX=9 StartY=7.5 StartZ=0 EndX=9 EndY=5.1 EndZ=0
  constraints (20):
    c: Vertical(g0)
    c: Coincident(g1,g0)
    c: Horizontal(g1)
    c: Coincident(g2,g0)
    c: Horizontal(g2)
    c: Coincident(g3,g2)
    c: Vertical(g3)
    c: Coincident(g5,g3)
    c: Coincident(g4,g6)
    c: Coincident(g4,g1)
    c: Vertical(g4)
    c: Coincident(g0,g-3)
    c: DistanceY(g-4,g3) = 2.4
    c: DistanceX(g1,g1) = 2
    c: DistanceY(g2,g6) = 0
    c: DistanceX(g2,g2) = 0
    c: DistanceY(g0,g0) = 1.2
    c: Coincident(g5,g6)
    c: Horizontal(g5)
    c: Vertical(g6)
FEATURE [Sketcher::SketchObject] Sketch067  label="perno per blocco switch"
  ArcFitTolerance = 1e-06
  AttachmentSupport = -> [XZ_Plane]
  ExternalGeometry = -> [Sketch,Sketch010]
  FullyConstrained = true
  MakeInternals = false
  MapMode = 5
  Placement = pos=(0,0,0) rot=(1,0,0;1.5708rad)
  sketch-geometry (14):
    g0: LineSegment StartX=-191.073 StartY=24.9429 StartZ=0 EndX=-185.81 EndY=23.0276 EndZ=0
    g1: LineSegment StartX=-183.76 StartY=23.9839 StartZ=0 EndX=-182.392 EndY=27.7427 EndZ=0
    g2: LineSegment StartX=-183.348 StartY=29.7934 StartZ=0 EndX=-188.61 EndY=31.7087 EndZ=0
    g3: LineSegment StartX=-188.61 StartY=31.7087 StartZ=0 EndX=-191.073 EndY=24.9429 EndZ=0
    g4: GeomPoint [constr] X=-186.459 Y=27.0946 Z=0
    g5: LineSegment StartX=-189.022 StartY=25.8992 StartZ=0 EndX=-185.263 EndY=24.5311 EndZ=0
    g6: LineSegment StartX=-185.263 StartY=24.5311 StartZ=0 EndX=-183.895 EndY=28.2899 EndZ=0
    g7: LineSegment StartX=-183.895 StartY=28.2899 StartZ=0 EndX=-187.654 EndY=29.658 EndZ=0
    g8: LineSegment StartX=-187.654 StartY=29.658 StartZ=0 EndX=-189.022 EndY=25.8992 EndZ=0
    g9: GeomPoint [constr] X=-186.459 Y=27.0946 Z=0
    g10: ArcOfCircle CenterX=-185.263 CenterY=24.5311 CenterZ=0 NormalX=0 NormalY=0 NormalZ=1 AngleXU=0 Radius=1.6 StartAngle=4.36332 EndAngle=5.93412
    g11: GeomPoint [constr] X=-184.307 Y=22.4804 Z=0
    g12: ArcOfCircle CenterX=-183.895 CenterY=28.2899 CenterZ=0 NormalX=0 NormalY=0 NormalZ=1 AngleXU=0 Radius=1.6 StartAngle=5.93412 EndAngle=7.50492
    g13: GeomPoint [constr] X=-181.844 Y=29.2462 Z=0
  constraints (30):
    c: Coincident(g2,g3)
    c: Coincident(g3,g0)
    c: Symmetric(g13,g0,g4)
    c: Distance(g11,g3) = 7.2
    c: Distance(g0,g2) = 7.2
    c: Parallel(g3,g1)
    c: Parallel(g2,g0)
    c: Perpendicular(g2,g3)
    c: Coincident(g5,g6)
    c: Coincident(g6,g7)
    c: Coincident(g7,g8)
    c: Coincident(g8,g5)
    c: Symmetric(g7,g5,g9)
    c: Distance(g6,g8) = 4
    c: Distance(g5,g7) = 4
    c: Coincident(g9,g4)
    c: Parallel(g8,g6)
    c: Parallel(g7,g5)
    c: Perpendicular(g7,g8)
    c: Tangent(g8,g-3)
    c: Tangent(g2,g-4)
    c: PointOnObject(g11,g1)
    c: PointOnObject(g11,g0)
    c: Tangent(g1,g10) = -1.5708
    c: Tangent(g0,g10) = -1.5708
    c: PointOnObject(g13,g1)
    c: Tangent(g1,g12) = -1.5708
    c: Tangent(g2,g12) = -1.5708
    c: Equal(g10,g12)
    c: Coincident(g10,g5)
FEATURE [Part::Extrusion] Extrude072  label="Extrude perno per blocco switch"
  Base = -> Sketch067
  Dir = (0,-1,2e-16)
  DirMode = 2
  FaceMakerClass = Part::FaceMakerBullseye
  FaceMakerMode = 3
  LengthFwd = 25.2
  LengthRev = 0
  Solid = true
  Symmetric = true
FEATURE [Part::MultiFuse] Fusion
  Refine = true
  Shapes = -> [Extrude,Sweep,Extrude007,Extrude011,Extrude005,Extrude012,Extrude013,Extrude016,Extrude031,Extrude039,Extrude045,Extrude072]
FEATURE [Part::Cut] Cut
  Base = -> Fusion
  Refine = true
  Tool = -> Extrude001
FEATURE [Part::Cut] Cut001
  Base = -> Cut
  Refine = true
  Tool = -> Extrude004
FEATURE [Part::Cut] Cut002
  Base = -> Cut001
  Refine = true
  Tool = -> Extrude006
FEATURE [Part::Cut] Cut003
  Base = -> Cut002
  Refine = true
  Tool = -> Extrude008
FEATURE [Part::Cut] Cut004
  Base = -> Cut003
  Refine = true
  Tool = -> Extrude009
FEATURE [Part::Cut] Cut005
  Base = -> Cut004
  Refine = true
  Tool = -> Extrude010
FEATURE [Part::Cut] Cut006
  Base = -> Cut005
  Refine = true
  Tool = -> Extrude014
FEATURE [Part::Cut] Cut007
  Base = -> Cut006
  Refine = true
  Tool = -> Extrude015
FEATURE [Part::Cut] Cut008
  Base = -> Cut007
  Refine = true
  Tool = -> Extrude018
FEATURE [Part::Cut] Cut009
  Base = -> Cut008
  Refine = true
  Tool = -> Extrude019
FEATURE [Part::Cut] Cut010
  Base = -> Cut009
  Refine = true
  Tool = -> Extrude020
FEATURE [Part::Cut] Cut011
  Base = -> Cut010
  Refine = true
  Tool = -> Extrude021
FEATURE [Part::Cut] Cut012
  Base = -> Cut011
  Refine = true
  Tool = -> Extrude022
FEATURE [Part::Cut] Cut013
  Base = -> Cut012
  Refine = true
  Tool = -> Extrude023
FEATURE [Part::Cut] Cut014
  Base = -> Cut013
  Refine = true
  Tool = -> Extrude032
FEATURE [Part::Cut] Cut015
  Base = -> Cut014
  Refine = true
  Tool = -> Extrude033
FEATURE [Part::Cut] Cut016
  Base = -> Cut015
  Refine = true
  Tool = -> Extrude034
FEATURE [Part::Cut] Cut017
  Base = -> Cut016
  Refine = true
  Tool = -> Extrude035
FEATURE [Part::Cut] Cut018
  Base = -> Cut017
  Refine = true
  Tool = -> Extrude036
FEATURE [Part::Cut] Cut019
  Base = -> Cut018
  Refine = true
  Tool = -> Extrude037
FEATURE [Part::Cut] Cut020
  Base = -> Cut019
  Refine = true
  Tool = -> Extrude030
FEATURE [Part::Cut] Cut022
  Base = -> Cut020
  Refine = true
  Tool = -> Extrude038
FEATURE [Part::Cut] Cut023
  Base = -> Cut022
  Refine = true
  Tool = -> Extrude041
FEATURE [Part::Cut] Cut024
  Base = -> Cut023
  Refine = true
  Tool = -> Extrude040
FEATURE [Part::Cut] Cut025
  Base = -> Cut024
  Refine = true
  Tool = -> Extrude042
FEATURE [Part::Cut] Cut026
  Base = -> Cut025
  Refine = true
  Tool = -> Extrude043
FEATURE [Part::Cut] Cut027
  Base = -> Cut026
  Refine = true
  Tool = -> Extrude044
FEATURE [Part::Cut] Cut028
  Base = -> Cut027
  Refine = true
  Tool = -> Extrude046
FEATURE [Part::Cut] Cut029
  Base = -> Cut028
  Refine = true
  Tool = -> Extrude047
FEATURE [Part::Cut] Cut033
  Base = -> Cut029
  Refine = true
  Tool = -> Extrude055
FEATURE [Part::Cut] Cut034
  Base = -> Cut033
  Refine = true
  Tool = -> Extrude056
FEATURE [Part::Cut] Cut035
  Base = -> Cut034
  Refine = true
  Tool = -> Extrude057
FEATURE [Part::Cut] Cut037
  Base = -> Cut035
  Refine = true
  Tool = -> Extrude060
FEATURE [Part::Cut] Cut038
  Base = -> Cut037
  Refine = true
  Tool = -> Extrude061
FEATURE [Part::Cut] Cut039
  Base = -> Cut038
  Refine = true
  Tool = -> Extrude063
FEATURE [Part::Cut] Cut040
  Base = -> Cut039
  Refine = true
  Tool = -> Extrude064
FEATURE [Part::Cut] Cut041
  Base = -> Cut040
  Refine = true
  Tool = -> Extrude062
FEATURE [Sketcher::SketchObject] Sketch068  label="base con smusso sopra neopixel"
  ArcFitTolerance = 1e-06
  AttachmentSupport = -> [YZ_Plane002]
  FullyConstrained = true
  MakeInternals = false
  MapMode = 5
  Placement = pos=(0,0,0) rot=(0.57735,0.57735,0.57735;2.0944rad)
  sketch-geometry (5):
    g0: LineSegment StartX=-9.5 StartY=-6.1 StartZ=0 EndX=9.5 EndY=-6.1 EndZ=0
    g1: LineSegment StartX=9.5 StartY=-6.1 StartZ=0 EndX=9.5 EndY=6.1 EndZ=0
    g2: LineSegment StartX=9.5 StartY=6.1 StartZ=0 EndX=-9.5 EndY=6.1 EndZ=0
    g3: LineSegment StartX=-9.5 StartY=6.1 StartZ=0 EndX=-9.5 EndY=-6.1 EndZ=0
    g4: GeomPoint [constr] X=0 Y=0 Z=0
  constraints (12):
    c: Coincident(g0,g1)
    c: Coincident(g1,g2)
    c: Coincident(g2,g3)
    c: Coincident(g3,g0)
    c: Horizontal(g0)
    c: Horizontal(g2)
    c: Vertical(g1)
    c: Vertical(g3)
    c: Symmetric(g2,g0,g4)
    c: Distance(g1,g3) = 19
    c: Distance(g0,g2) = 12.2
    c: Coincident(g4,g-1)
FEATURE [Sketcher::SketchObject] Sketch069  label="cilindro minore"
  ArcFitTolerance = 1e-06
  AttachmentSupport = -> [XZ_Plane004]
  FullyConstrained = true
  MakeInternals = false
  MapMode = 5
  Placement = pos=(0,0,0) rot=(1,0,0;1.5708rad)
  sketch-geometry (1):
    g0: Circle CenterX=0 CenterY=0 CenterZ=0 NormalX=0 NormalY=0 NormalZ=1 AngleXU=0 Radius=5.8
  constraints (2):
    c: Diameter(g0) = 11.6
    c: Coincident(g0,g-1)
FEATURE [Sketcher::SketchObject] Sketch070  label="cilindro maggiore"
  ArcFitTolerance = 1e-06
  AttachmentSupport = -> [XZ_Plane004]
  ExternalGeometry = -> [Sketch069]
  FullyConstrained = true
  MakeInternals = false
  MapMode = 5
  Placement = pos=(0,0,0) rot=(1,0,0;1.5708rad)
  sketch-geometry (1):
    g0: Circle CenterX=0 CenterY=0 CenterZ=0 NormalX=0 NormalY=0 NormalZ=1 AngleXU=0 Radius=6.5
  constraints (2):
    c: Coincident(g0,g-1)
    c: Diameter(g0) = 13
FEATURE [Sketcher::SketchObject] Sketch071  label="buco interno"
  ArcFitTolerance = 1e-06
  AttachmentSupport = -> [XZ_Plane004]
  ExternalGeometry = -> [Sketch069]
  FullyConstrained = true
  MakeInternals = false
  MapMode = 5
  Placement = pos=(0,0,0) rot=(1,0,0;1.5708rad)
  sketch-geometry (1):
    g0: Circle CenterX=0 CenterY=0 CenterZ=0 NormalX=0 NormalY=0 NormalZ=1 AngleXU=0 Radius=5
  constraints (2):
    c: Coincident(g0,g-1)
    c: Diameter(g0) = 10
FEATURE [PartDesign::Pad] Pad
  Direction = (0,-1,2e-16)
  Length = 1.2
  Length2 = 10
  Placement = pos=(0,0,0) rot=(1,0,0;1.5708rad)
  Profile = -> Sketch070
  ReferenceAxis = -> Sketch070 [N_Axis]
  Refine = true
  Suppressed = false
  Type = 0
FEATURE [PartDesign::Pad] Pad001
  BaseFeature = -> Pad
  Direction = (0,-1,2e-16)
  Length = 5.6
  Length2 = 10
  Placement = pos=(0,0,0) rot=(1,0,0;1.5708rad)
  Profile = -> Sketch069
  ReferenceAxis = -> Sketch069 [N_Axis]
  Refine = true
  Suppressed = false
  Type = 0
FEATURE [PartDesign::Pocket] Pocket
  BaseFeature = -> Pad001
  Direction = (0,1,-2e-16)
  Length = 7
  Length2 = 5
  Midplane = true
  Placement = pos=(0,0,0) rot=(1,0,0;1.5708rad)
  Profile = -> Sketch071
  ReferenceAxis = -> Sketch071 [N_Axis]
  Refine = true
  Suppressed = false
  Type = 0
FEATURE [PartDesign::Fillet] Fillet
  Base = -> Pocket [Face7]
  BaseFeature = -> Pocket
  Placement = pos=(0,0,0) rot=(1,0,0;1.5708rad)
  Radius = 1
  Refine = true
  SupportTransform = false
  Suppressed = false
  UseAllEdges = false
FEATURE [PartDesign::Body] Body004  label="pulsanti lato sinistro"
  AllowCompound = false
  Group = -> [Sketch069,Sketch070,Sketch071,Pad,Pad001,Pocket,Fillet]
  Origin = -> Origin004
  Tip = -> Fillet
FEATURE [Sketcher::SketchObject] Sketch072  label="buco per saldature e diodo driver solenoide"
  ArcFitTolerance = 1e-06
  AttachmentSupport = -> [XZ_Plane]
  ExternalGeometry = -> [Sketch038]
  FullyConstrained = true
  MakeInternals = false
  MapMode = 5
  Placement = pos=(0,0,0) rot=(1,0,0;1.5708rad)
  sketch-geometry (4):
    g0: LineSegment StartX=-212.269 StartY=-43.9083 StartZ=0 EndX=-207.197 EndY=-33.0326 EndZ=0
    g1: LineSegment StartX=-207.197 StartY=-33.0326 StartZ=0 EndX=-207.56 EndY=-32.8635 EndZ=0
    g2: LineSegment StartX=-207.56 StartY=-32.8635 StartZ=0 EndX=-212.631 EndY=-43.7392 EndZ=0
    g3: LineSegment StartX=-212.631 StartY=-43.7392 StartZ=0 EndX=-212.269 EndY=-43.9083 EndZ=0
  constraints (11):
    c: Coincident(g1,g0)
    c: Coincident(g2,g1)
    c: Coincident(g3,g2)
    c: Coincident(g3,g0)
    c: Parallel(g-3,g0)
    c: Parallel(g0,g2)
    c: Perpendicular(g0,g3)
    c: Perpendicular(g1,g0)
    c: Distance(g3) = 0.4
    c: Distance(g2) = 12
    c: Coincident(g0,g-3)
FEATURE [Part::Extrusion] Extrude074  label="Extrude buco per saldature e diodo driver solenoide"
  Base = -> Sketch072
  Dir = (0,-1,2e-16)
  DirMode = 2
  FaceMakerClass = Part::FaceMakerBullseye
  FaceMakerMode = 3
  LengthFwd = 14.6
  LengthRev = 0
  Solid = true
  Symmetric = true
FEATURE [Part::Cut] Cut042
  Base = -> Cut041
  Refine = true
  Tool = -> Extrude074
FEATURE [Sketcher::SketchObject] Sketch073  label="fori slargati blocco solenoide"
  ArcFitTolerance = 1e-06
  AttachmentSupport = -> [XY_Plane]
  ExternalGeometry = -> [Sketch030]
  FullyConstrained = true
  MakeInternals = false
  MapMode = 5
  sketch-geometry (2):
    g0: Circle CenterX=-152.209 CenterY=6.95 CenterZ=0 NormalX=0 NormalY=0 NormalZ=1 AngleXU=0 Radius=3.7
    g1: Circle CenterX=-130.41 CenterY=-6.95 CenterZ=0 NormalX=0 NormalY=0 NormalZ=1 AngleXU=0 Radius=3.7
  constraints (4):
    c: Diameter(g0) = 7.4
    c: Coincident(g0,g-3)
    c: Diameter(g1) = 7.4
    c: Coincident(g1,g-4)
FEATURE [Part::Extrusion] Extrude075  label="Extrude fori slargati blocco solenoide"
  Base = -> Sketch073
  Dir = (0,0,1)
  DirMode = 2
  FaceMakerClass = Part::FaceMakerBullseye
  FaceMakerMode = 3
  LengthFwd = 1.5
  LengthRev = 0
  Placement = pos=(0,0,36.4) rot=(0,0,1;0rad)
  Solid = true
  Symmetric = false
FEATURE [Part::Cut] Cut043
  Base = -> Cut042
  Refine = true
  Tool = -> Extrude075
FEATURE [Sketcher::SketchObject] Sketch074  label="lato sx pistola"
  ArcFitTolerance = 1e-06
  AttachmentSupport = -> [XZ_Plane]
  ExternalGeometry = -> [Sketch016,Sketch,Sketch058]
  FullyConstrained = true
  MakeInternals = false
  MapMode = 5
  Placement = pos=(0,0,0) rot=(1,0,0;1.5708rad)
  sketch-geometry (37):
    g0: LineSegment StartX=-82.8 StartY=3.2 StartZ=0 EndX=0 EndY=3.2 EndZ=0
    g1: LineSegment StartX=-82.8 StartY=3.2 StartZ=0 EndX=-82.8 EndY=6.2 EndZ=0
    g2: LineSegment [constr] StartX=-107.6 StartY=18 StartZ=0 EndX=-107.6 EndY=20 EndZ=0
    g3: LineSegment [constr] StartX=-132.428 StartY=18 StartZ=0 EndX=-132.428 EndY=20 EndZ=0
    g4: LineSegment StartX=-132.428 StartY=20 StartZ=0 EndX=-107.6 EndY=20 EndZ=0
    g5: ArcOfCircle CenterX=-107.6 CenterY=4 CenterZ=0 NormalX=0 NormalY=0 NormalZ=1 AngleXU=0 Radius=16 StartAngle=0.137937 EndAngle=1.5708
    g6: LineSegment StartX=-82.8 StartY=6.2 StartZ=0 EndX=-91.752 EndY=6.2 EndZ=0
    g7: LineSegment [constr] StartX=-145.743 StartY=8.32624 StartZ=0 EndX=-147.645 EndY=8.94427 EndZ=0
    g8: ArcOfCircle CenterX=-132.428 CenterY=4 CenterZ=0 NormalX=0 NormalY=0 NormalZ=1 AngleXU=0 Radius=16 StartAngle=1.5708 EndAngle=2.82743
    g9: LineSegment StartX=-215.932 StartY=-80.4316 StartZ=0 EndX=-176.685 EndY=-80.4316 EndZ=0
    g10: LineSegment StartX=-147.645 StartY=8.94427 StartZ=0 EndX=-176.685 EndY=-80.4316 EndZ=0
    g11: LineSegment [constr] StartX=-193.988 StartY=-2.33927 StartZ=0 EndX=-192.176 EndY=-3.18451 EndZ=0
    g12: LineSegment [constr] StartX=-217.232 StartY=-52.1862 StartZ=0 EndX=-215.42 EndY=-53.0314 EndZ=0
    g13: LineSegment StartX=-192.176 StartY=-3.18451 StartZ=0 EndX=-215.42 EndY=-53.0314 EndZ=0
    g14: ArcOfCircle CenterX=-184.801 CenterY=-67.3089 CenterZ=0 NormalX=0 NormalY=0 NormalZ=1 AngleXU=0 Radius=33.7833 StartAngle=2.70526 EndAngle=3.54053
    g15: ArcOfCircle CenterX=-207.583 CenterY=4 CenterZ=0 NormalX=0 NormalY=0 NormalZ=1 AngleXU=0 Radius=17 StartAngle=5.84685 EndAngle=7.56663
    g16: LineSegment StartX=-202.765 StartY=20.303 StartZ=0 EndX=-195.887 EndY=39.2 EndZ=0
    g17: LineSegment [constr] StartX=-193.885 StartY=33.0037 StartZ=0 EndX=-197.644 EndY=34.3718 EndZ=0
    g18: LineSegment StartX=-195.887 StartY=39.2 StartZ=0 EndX=0 EndY=39.2 EndZ=0
    g19: LineSegment StartX=0 StartY=3.2 StartZ=0 EndX=0 EndY=39.2 EndZ=0
    g20: LineSegment StartX=-189.939 StartY=31.5672 StartZ=0 EndX=-192.333 EndY=24.9893 EndZ=0
    g21: LineSegment StartX=-196.467 StartY=26.4942 StartZ=0 EndX=-194.073 EndY=33.0721 EndZ=0
    g22: Circle CenterX=-213.443 CenterY=-76.8316 CenterZ=0 NormalX=0 NormalY=0 NormalZ=1 AngleXU=0 Radius=1.8
    g23: Circle CenterX=-179.305 CenterY=-76.8316 CenterZ=0 NormalX=0 NormalY=0 NormalZ=1 AngleXU=0 Radius=1.8
    g24: Circle CenterX=-184.08 CenterY=34.8 CenterZ=0 NormalX=0 NormalY=0 NormalZ=1 AngleXU=0 Radius=1.8
    g25: Circle CenterX=-78.51 CenterY=34.8 CenterZ=0 NormalX=0 NormalY=0 NormalZ=1 AngleXU=0 Radius=1.8
    g26: Circle CenterX=-78.51 CenterY=7.6 CenterZ=0 NormalX=0 NormalY=0 NormalZ=1 AngleXU=0 Radius=1.8
    g27: Circle CenterX=-5.6 CenterY=34.8 CenterZ=0 NormalX=0 NormalY=0 NormalZ=1 AngleXU=0 Radius=1.8
    g28: Circle CenterX=-5.6 CenterY=7.6 CenterZ=0 NormalX=0 NormalY=0 NormalZ=1 AngleXU=0 Radius=1.8
    g29: LineSegment StartX=-190.127 StartY=31.6356 StartZ=0 EndX=-189.939 EndY=31.5672 EndZ=0
    g30: LineSegment StartX=-194.073 StartY=33.0721 StartZ=0 EndX=-193.885 EndY=33.0037 EndZ=0
    g31: LineSegment StartX=-193.885 StartY=33.0037 StartZ=0 EndX=-190.127 EndY=31.6356 EndZ=0
    g32: LineSegment StartX=-196.467 StartY=26.4942 StartZ=0 EndX=-192.333 EndY=24.9893 EndZ=0
    g33: Circle CenterX=-19 CenterY=21.2 CenterZ=0 NormalX=0 NormalY=0 NormalZ=1 AngleXU=0 Radius=6.3
    g34: Circle CenterX=-42 CenterY=21.2 CenterZ=0 NormalX=0 NormalY=0 NormalZ=1 AngleXU=0 Radius=6.3
    g35: Circle CenterX=-65 CenterY=21.2 CenterZ=0 NormalX=0 NormalY=0 NormalZ=1 AngleXU=0 Radius=6.3
    g36: LineSegment [constr] StartX=-4 StartY=21.2 StartZ=0 EndX=-65 EndY=21.2 EndZ=0
  constraints (96):
    c: Coincident(g0,g-41)
    c: Horizontal(g0)
    c: PointOnObject(g0,g-39)
    c: Coincident(g1,g0)
    c: Vertical(g1)
    c: DistanceY(g1,g1) = 3
    c: Coincident(g2,g-17)
    c: Vertical(g2)
    c: Coincident(g3,g-16)
    c: Vertical(g3)
    c: DistanceY(g2,g2) = 2
    c: DistanceY(g3,g3) = 2
    c: Coincident(g4,g3)
    c: Coincident(g4,g2)
    c: Coincident(g5,g-17)
    c: Coincident(g5,g2)
    c: Coincident(g6,g1)
    c: Horizontal(g6)
    c: Coincident(g6,g5)
    c: Coincident(g7,g-15)
    c: Coincident(g8,g7)
    c: Coincident(g8,g3)
    c: Coincident(g8,g-15)
    c: Horizontal(g9)
    c: DistanceY(g-13,g9) = 2
    c: Coincident(g10,g7)
    c: Parallel(g10,g-14)
    c: Coincident(g9,g10)
    c: Distance(g11) = 2
    c: Coincident(g11,g-11)
    c: Perpendicular(g-11,g11)
    c: Distance(g12) = 2
    c: Coincident(g12,g-12)
    c: Perpendicular(g-11,g12)
    c: Coincident(g13,g11)
    c: Coincident(g13,g12)
    c: Coincident(g14,g-32)
    c: Coincident(g14,g12)
    c: Coincident(g14,g9)
    c: Coincident(g15,g-10)
    c: Coincident(g15,g11)
    c: Parallel(g16,g-22)
    c: Distance(g17) = 4
    c: PointOnObject(g17,g16)
    c: Coincident(g15,g16)
    c: Horizontal(g18)
    c: Coincident(g18,g16)
    c: Coincident(g19,g0)
    c: PointOnObject(g19,g-39)
    c: DistanceY(g19,g-36) = 2
    c: Coincident(g18,g19)
    c: Diameter(g22) = 3.6
    c: Coincident(g22,g-9)
    c: Diameter(g23) = 3.6
    c: Coincident(g23,g-8)
    c: Diameter(g24) = 3.6
    c: Diameter(g25) = 3.6
    c: Diameter(g26) = 3.6
    c: Diameter(g27) = 3.6
    c: Diameter(g28) = 3.6
    c: Coincident(g27,g-4)
    c: Coincident(g28,g-3)
    c: Coincident(g25,g-6)
    c: Coincident(g26,g-5)
    c: Coincident(g24,g-7)
    c: Parallel(g20,g-21)
    c: Equal(g20,g-21)
    c: Parallel(g21,g-19)
    c: Equal(g21,g-19)
    c: Distance(g29) = 0.2
    c: Distance(g30) = 0.2
    c: Parallel(g29,g-20)
    c: Parallel(g31,g-20)
    c: Equal(g31,g-20)
    c: Coincident(g30,g31)
    c: Coincident(g31,g29)
    c: Coincident(g29,g-21)
    c: Parallel(g30,g31)
    c: Coincident(g17,g30)
    c: Coincident(g20,g29)
    c: Coincident(g21,g30)
    c: Perpendicular(g16,g17)
    c: Coincident(g32,g21)
    c: Coincident(g32,g20)
    c: Perpendicular(g10,g7)
    c: Diameter(g33) = 12.6
    c: Diameter(g34) = 12.6
    c: Diameter(g35) = 12.6
    c: Horizontal(g36)
    c: PointOnObject(g33,g36)
    c: PointOnObject(g34,g36)
    c: DistanceX(g34,g33) = 23
    c: DistanceX(g35,g34) = 23
    c: DistanceX(g33,g36) = 15
    c: Symmetric(g-24,g-24,g36)
    c: Coincident(g36,g35)
FEATURE [Sketcher::SketchObject] Sketch075  label="lato dx pistola"
  ArcFitTolerance = 1e-06
  AttachmentSupport = -> [XZ_Plane]
  ExternalGeometry = -> [Sketch016,Sketch,Sketch058,Sketch074]
  FullyConstrained = true
  MakeInternals = false
  MapMode = 5
  Placement = pos=(0,0,0) rot=(1,0,0;1.5708rad)
  sketch-geometry (61):
    g0: LineSegment StartX=-82.8 StartY=3.2 StartZ=0 EndX=0 EndY=3.2 EndZ=0
    g1: LineSegment StartX=-82.8 StartY=3.2 StartZ=0 EndX=-82.8 EndY=6.2 EndZ=0
    g2: LineSegment [constr] StartX=-107.6 StartY=18 StartZ=0 EndX=-107.6 EndY=20 EndZ=0
    g3: LineSegment [constr] StartX=-132.428 StartY=18 StartZ=0 EndX=-132.428 EndY=20 EndZ=0
    g4: LineSegment StartX=-132.428 StartY=20 StartZ=0 EndX=-107.6 EndY=20 EndZ=0
    g5: ArcOfCircle CenterX=-107.6 CenterY=4 CenterZ=0 NormalX=0 NormalY=0 NormalZ=1 AngleXU=0 Radius=16 StartAngle=0.137937 EndAngle=1.5708
    g6: LineSegment StartX=-82.8 StartY=6.2 StartZ=0 EndX=-91.752 EndY=6.2 EndZ=0
    g7: LineSegment [constr] StartX=-145.743 StartY=8.32624 StartZ=0 EndX=-147.645 EndY=8.94427 EndZ=0
    g8: ArcOfCircle CenterX=-132.428 CenterY=4 CenterZ=0 NormalX=0 NormalY=0 NormalZ=1 AngleXU=0 Radius=16 StartAngle=1.5708 EndAngle=2.82743
    g9: LineSegment StartX=-215.932 StartY=-80.4316 StartZ=0 EndX=-176.685 EndY=-80.4316 EndZ=0
    g10: LineSegment StartX=-147.645 StartY=8.94427 StartZ=0 EndX=-176.685 EndY=-80.4316 EndZ=0
    g11: LineSegment [constr] StartX=-193.988 StartY=-2.33927 StartZ=0 EndX=-192.176 EndY=-3.18451 EndZ=0
    g12: LineSegment [constr] StartX=-217.232 StartY=-52.1862 StartZ=0 EndX=-215.42 EndY=-53.0314 EndZ=0
    g13: LineSegment StartX=-192.176 StartY=-3.18451 StartZ=0 EndX=-215.42 EndY=-53.0314 EndZ=0
    g14: ArcOfCircle CenterX=-184.801 CenterY=-67.3089 CenterZ=0 NormalX=0 NormalY=0 NormalZ=1 AngleXU=0 Radius=33.7833 StartAngle=2.70526 EndAngle=3.54053
    g15: ArcOfCircle CenterX=-207.583 CenterY=4 CenterZ=0 NormalX=0 NormalY=0 NormalZ=1 AngleXU=0 Radius=17 StartAngle=5.84685 EndAngle=7.56663
    g16: LineSegment StartX=-202.765 StartY=20.303 StartZ=0 EndX=-195.887 EndY=39.2 EndZ=0
    g17: LineSegment [constr] StartX=-193.885 StartY=33.0037 StartZ=0 EndX=-197.644 EndY=34.3718 EndZ=0
    g18: LineSegment StartX=-195.887 StartY=39.2 StartZ=0 EndX=0 EndY=39.2 EndZ=0
    g19: LineSegment StartX=0 StartY=3.2 StartZ=0 EndX=0 EndY=39.2 EndZ=0
    g20: LineSegment StartX=-189.939 StartY=31.5672 StartZ=0 EndX=-192.333 EndY=24.9893 EndZ=0
    g21: LineSegment StartX=-196.467 StartY=26.4942 StartZ=0 EndX=-194.073 EndY=33.0721 EndZ=0
    g22: Circle CenterX=-213.443 CenterY=-76.8316 CenterZ=0 NormalX=0 NormalY=0 NormalZ=1 AngleXU=0 Radius=1.8
    g23: Circle CenterX=-179.305 CenterY=-76.8316 CenterZ=0 NormalX=0 NormalY=0 NormalZ=1 AngleXU=0 Radius=1.8
    g24: Circle CenterX=-184.08 CenterY=34.8 CenterZ=0 NormalX=0 NormalY=0 NormalZ=1 AngleXU=0 Radius=1.8
    g25: Circle CenterX=-78.51 CenterY=34.8 CenterZ=0 NormalX=0 NormalY=0 NormalZ=1 AngleXU=0 Radius=1.8
    g26: Circle CenterX=-78.51 CenterY=7.6 CenterZ=0 NormalX=0 NormalY=0 NormalZ=1 AngleXU=0 Radius=1.8
    g27: Circle CenterX=-5.6 CenterY=34.8 CenterZ=0 NormalX=0 NormalY=0 NormalZ=1 AngleXU=0 Radius=1.8
    g28: Circle CenterX=-5.6 CenterY=7.6 CenterZ=0 NormalX=0 NormalY=0 NormalZ=1 AngleXU=0 Radius=1.8
    g29: LineSegment StartX=-190.127 StartY=31.6356 StartZ=0 EndX=-189.939 EndY=31.5672 EndZ=0
    g30: LineSegment StartX=-194.073 StartY=33.0721 StartZ=0 EndX=-193.885 EndY=33.0037 EndZ=0
    g31: LineSegment StartX=-193.885 StartY=33.0037 StartZ=0 EndX=-190.127 EndY=31.6356 EndZ=0
    g32: LineSegment StartX=-196.467 StartY=26.4942 StartZ=0 EndX=-192.333 EndY=24.9893 EndZ=0
    g33: LineSegment [constr] StartX=-4 StartY=21.2 StartZ=0 EndX=-87.91 EndY=21.2 EndZ=0
    g34: GeomPoint [constr] X=-4 Y=21.2 Z=0
    g35: LineSegment [constr] StartX=-15.2 StartY=33.7 StartZ=0 EndX=-15.2 EndY=8.7 EndZ=0
    g36: LineSegment [constr] StartX=-15.2 StartY=33.7 StartZ=0 EndX=-56.2 EndY=33.7 EndZ=0
    g37: LineSegment [constr] StartX=-15.2 StartY=8.7 StartZ=0 EndX=-56.2 EndY=8.7 EndZ=0
    g38: LineSegment [constr] StartX=-56.2 StartY=33.7 StartZ=0 EndX=-56.2 EndY=8.7 EndZ=0
    g39: Circle CenterX=-18.6 CenterY=30.3 CenterZ=0 NormalX=0 NormalY=0 NormalZ=1 AngleXU=0 Radius=3.4
    g40: Circle CenterX=-18.6 CenterY=12.1 CenterZ=0 NormalX=0 NormalY=0 NormalZ=1 AngleXU=0 Radius=3.4
    g41: Circle CenterX=-43.2 CenterY=30.3 CenterZ=0 NormalX=0 NormalY=0 NormalZ=1 AngleXU=0 Radius=3.4
    g42: Circle CenterX=-43.2 CenterY=12.1 CenterZ=0 NormalX=0 NormalY=0 NormalZ=1 AngleXU=0 Radius=3.4
    g43: LineSegment [constr] StartX=-4 StartY=21.2 StartZ=0 EndX=-15.2 EndY=21.2 EndZ=0
    g44: LineSegment [constr] StartX=-15.2 StartY=21.2 StartZ=0 EndX=-36.2 EndY=21.2 EndZ=0
    g45: LineSegment [constr] StartX=-41.5 StartY=16.2 StartZ=0 EndX=-30.9 EndY=16.2 EndZ=0
    g46: LineSegment [constr] StartX=-30.9 StartY=16.2 StartZ=0 EndX=-30.9 EndY=26.2 EndZ=0
    g47: LineSegment [constr] StartX=-30.9 StartY=26.2 StartZ=0 EndX=-41.5 EndY=26.2 EndZ=0
    g48: LineSegment [constr] StartX=-41.5 StartY=26.2 StartZ=0 EndX=-41.5 EndY=16.2 EndZ=0
    g49: GeomPoint [constr] X=-36.2 Y=21.2 Z=0
    g50: Circle CenterX=-36.2 CenterY=21.2 CenterZ=0 NormalX=0 NormalY=0 NormalZ=1 AngleXU=0 Radius=2.8
    g51: LineSegment [constr] StartX=-24.2 StartY=26.7 StartZ=0 EndX=-24.2 EndY=15.7 EndZ=0
    g52: Circle CenterX=-24.2 CenterY=26.7 CenterZ=0 NormalX=0 NormalY=0 NormalZ=1 AngleXU=0 Radius=3
    g53: Circle CenterX=-24.2 CenterY=15.7 CenterZ=0 NormalX=0 NormalY=0 NormalZ=1 AngleXU=0 Radius=3
    g54: GeomPoint X=-18.6 Y=30.3 Z=0
    g55: GeomPoint X=-18.6 Y=12.1 Z=0
    g56: GeomPoint X=-43.2 Y=12.1 Z=0
    g57: GeomPoint X=-43.2 Y=30.3 Z=0
    g58: Circle CenterX=-65 CenterY=21.2 CenterZ=0 NormalX=0 NormalY=0 NormalZ=1 AngleXU=0 Radius=1.5
    g59: Circle CenterX=-42 CenterY=21.2 CenterZ=0 NormalX=0 NormalY=0 NormalZ=1 AngleXU=0 Radius=1.5
    g60: Circle CenterX=-19 CenterY=21.2 CenterZ=0 NormalX=0 NormalY=0 NormalZ=1 AngleXU=0 Radius=1.5
  constraints (149):
    c: Coincident(g0,g-41)
    c: Horizontal(g0)
    c: PointOnObject(g0,g-39)
    c: Coincident(g1,g0)
    c: Vertical(g1)
    c: DistanceY(g1,g1) = 3
    c: Coincident(g2,g-17)
    c: Vertical(g2)
    c: Coincident(g3,g-16)
    c: Vertical(g3)
    c: DistanceY(g2,g2) = 2
    c: DistanceY(g3,g3) = 2
    c: Coincident(g4,g3)
    c: Coincident(g4,g2)
    c: Coincident(g5,g-17)
    c: Coincident(g5,g2)
    c: Coincident(g6,g1)
    c: Horizontal(g6)
    c: Coincident(g6,g5)
    c: Coincident(g7,g-15)
    c: Coincident(g8,g7)
    c: Coincident(g8,g3)
    c: Coincident(g8,g-15)
    c: Horizontal(g9)
    c: DistanceY(g-13,g9) = 2
    c: Coincident(g10,g7)
    c: Parallel(g10,g-14)
    c: Coincident(g9,g10)
    c: Distance(g11) = 2
    c: Coincident(g11,g-11)
    c: Perpendicular(g-11,g11)
    c: Distance(g12) = 2
    c: Coincident(g12,g-12)
    c: Perpendicular(g-11,g12)
    c: Coincident(g13,g11)
    c: Coincident(g13,g12)
    c: Coincident(g14,g-32)
    c: Coincident(g14,g12)
    c: Coincident(g14,g9)
    c: Coincident(g15,g-10)
    c: Coincident(g15,g11)
    c: Parallel(g16,g-22)
    c: Distance(g17) = 4
    c: PointOnObject(g17,g16)
    c: Coincident(g15,g16)
    c: Horizontal(g18)
    c: Coincident(g18,g16)
    c: Coincident(g19,g0)
    c: PointOnObject(g19,g-39)
    c: DistanceY(g19,g-36) = 2
    c: Coincident(g18,g19)
    c: Diameter(g22) = 3.6
    c: Coincident(g22,g-9)
    c: Diameter(g23) = 3.6
    c: Coincident(g23,g-8)
    c: Diameter(g24) = 3.6
    c: Diameter(g25) = 3.6
    c: Diameter(g26) = 3.6
    c: Diameter(g27) = 3.6
    c: Diameter(g28) = 3.6
    c: Coincident(g27,g-4)
    c: Coincident(g28,g-3)
    c: Coincident(g25,g-6)
    c: Coincident(g26,g-5)
    c: Coincident(g24,g-7)
    c: Parallel(g20,g-21)
    c: Equal(g20,g-21)
    c: Parallel(g21,g-19)
    c: Equal(g21,g-19)
    c: Distance(g29) = 0.2
    c: Distance(g30) = 0.2
    c: Parallel(g29,g-20)
    c: Parallel(g31,g-20)
    c: Equal(g31,g-20)
    c: Coincident(g30,g31)
    c: Coincident(g31,g29)
    c: Coincident(g29,g-21)
    c: Parallel(g30,g31)
    c: Coincident(g17,g30)
    c: Coincident(g20,g29)
    c: Coincident(g21,g30)
    c: Perpendicular(g16,g17)
    c: Coincident(g32,g21)
    c: Coincident(g32,g20)
    c: Perpendicular(g10,g7)
    c: Horizontal(g33)
    c: Symmetric(g-24,g-24,g33)
    c: PointOnObject(g33,g-28)
    c: Symmetric(g-24,g-24,g34)
    c: DistanceY(g35,g35) = 25
    c: Symmetric(g35,g35,g33)
    c: Distance(g36) = 41
    c: Coincident(g36,g35)
    c: Horizontal(g36)
    c: Coincident(g37,g35)
    c: Horizontal(g37)
    c: Coincident(g38,g36)
    c: Vertical(g38)
    c: Coincident(g37,g38)
    c: Diameter(g39) = 6.8
    c: Diameter(g40) = 6.8
    c: Tangent(g39,g36)
    c: Tangent(g40,g37)
    c: Tangent(g39,g35)
    c: Tangent(g40,g35)
    c: Diameter(g41) = 6.8
    c: Diameter(g42) = 6.8
    c: Tangent(g41,g36)
    c: Tangent(g42,g37)
    c: DistanceX(g41,g39) = 24.6
    c: DistanceX(g42,g40) = 24.6
    c: Distance(g43) = 11.2
    c: Coincident(g43,g33)
    c: PointOnObject(g43,g33)
    c: PointOnObject(g43,g35)
    c: Distance(g44) = 21
    c: Coincident(g44,g43)
    c: PointOnObject(g44,g33)
    c: Coincident(g45,g46)
    c: Coincident(g46,g47)
    c: Coincident(g47,g48)
    c: Coincident(g48,g45)
    c: Horizontal(g45)
    c: Horizontal(g47)
    c: Vertical(g46)
    c: Vertical(g48)
    c: Symmetric(g47,g45,g49)
    c: Distance(g46,g48) = 10.6
    c: Distance(g45,g47) = 10
    c: Coincident(g49,g44)
    c: Diameter(g50) = 5.6
    c: Coincident(g50,g44)
    c: Distance(g51) = 11
    c: Symmetric(g51,g51,g33)
    c: DistanceX(g51,g43) = 9
    c: Diameter(g52) = 6
    c: Coincident(g52,g51)
    c: Diameter(g53) = 6
    c: Coincident(g53,g51)
    c: Coincident(g40,g55)
    c: Coincident(g39,g54)
    c: Coincident(g41,g57)
    c: Coincident(g42,g56)
    c: Diameter(g58) = 3
    c: Diameter(g59) = 3
    c: Diameter(g60) = 3
    c: Coincident(g58,g-44)
    c: Coincident(g59,g-46)
    c: Coincident(g60,g-45)
FEATURE [Sketcher::SketchObject] Sketch078
  ArcFitTolerance = 1e-06
  AttachmentSupport = -> [XZ_Plane005]
  FullyConstrained = true
  MakeInternals = false
  MapMode = 5
  Placement = pos=(0,0,0) rot=(1,0,0;1.5708rad)
  sketch-geometry (5):
    g0: LineSegment [constr] StartX=0 StartY=5.5 StartZ=0 EndX=0 EndY=-5.5 EndZ=0
    g1: ArcOfCircle CenterX=0 CenterY=5.5 CenterZ=0 NormalX=0 NormalY=0 NormalZ=1 AngleXU=0 Radius=2.7 StartAngle=0 EndAngle=3.14159
    g2: ArcOfCircle CenterX=0 CenterY=-5.5 CenterZ=0 NormalX=0 NormalY=0 NormalZ=1 AngleXU=0 Radius=2.7 StartAngle=3.1416 EndAngle=6.28318
    g3: LineSegment StartX=-2.7 StartY=5.5 StartZ=0 EndX=-2.7 EndY=-5.50001 EndZ=0
    g4: LineSegment StartX=2.7 StartY=5.5 StartZ=0 EndX=2.7 EndY=-5.50001 EndZ=0
  constraints (13):
    c: Distance(g0) = 11
    c: Vertical(g0)
    c: Symmetric(g0,g0,g-1)
    c: Radius(g1) = 2.7
    c: Coincident(g1,g0)
    c: Radius(g2) = 2.7
    c: Coincident(g2,g0)
    c: Vertical(g3)
    c: Vertical(g4)
    c: Coincident(g2,g4)
    c: Coincident(g2,g3)
    c: Tangent(g3,g1) = -1.5708
    c: Tangent(g4,g1) = 1.5708
FEATURE [PartDesign::Pad] Pad002
  Direction = (0,-1,2e-16)
  Length = 0.8
  Length2 = 10
  Placement = pos=(0,0,0) rot=(1,0,0;1.5708rad)
  Profile = -> Sketch078
  ReferenceAxis = -> Sketch078 [N_Axis]
  Refine = true
  Suppressed = false
  Type = 0
FEATURE [Sketcher::SketchObject] Sketch079
  ArcFitTolerance = 1e-06
  AttachmentSupport = -> [XZ_Plane005]
  ExternalGeometry = -> [Sketch078]
  FullyConstrained = true
  MakeInternals = false
  MapMode = 5
  Placement = pos=(0,0,0) rot=(1,0,0;1.5708rad)
  sketch-geometry (2):
    g0: Circle CenterX=-1e-16 CenterY=5.5 CenterZ=0 NormalX=0 NormalY=0 NormalZ=1 AngleXU=0 Radius=2.7
    g1: Circle CenterX=0 CenterY=-5.5 CenterZ=0 NormalX=0 NormalY=0 NormalZ=1 AngleXU=0 Radius=2.7
  constraints (4):
    c: Coincident(g0,g-3)
    c: PointOnObject(g-3,g0)
    c: Coincident(g1,g-4)
    c: Equal(g1,g-4)
FEATURE [PartDesign::Pad] Pad003
  BaseFeature = -> Pad002
  Direction = (0,-1,2e-16)
  Length = 5
  Length2 = 10
  Placement = pos=(0,0,0) rot=(1,0,0;1.5708rad)
  Profile = -> Sketch079
  ReferenceAxis = -> Sketch079 [N_Axis]
  Refine = true
  Suppressed = false
  Type = 0
FEATURE [PartDesign::Fillet] Fillet001
  Base = -> Pad003 [Edge16,Edge14]
  BaseFeature = -> Pad003
  Placement = pos=(0,0,0) rot=(1,0,0;1.5708rad)
  Radius = 0.4
  Refine = true
  SupportTransform = false
  Suppressed = false
  UseAllEdges = false
FEATURE [PartDesign::Body] Body005  label="pulsanti lato destro"
  AllowCompound = false
  Group = -> [Sketch078,Pad002,Sketch079,Pad003,Fillet001]
  Origin = -> Origin005
  Tip = -> Fillet001
FEATURE [PartDesign::SubShapeBinder] Binder
  BindCopyOnChange = 0
  BindMode = 0
  ClaimChildren = false
  Context = -> Body006 [Binder.]
  Fuse = false
  MakeFace = true
  OffsetFill = false
  OffsetIntersection = false
  OffsetJoinType = 0
  OffsetOpenResult = false
  PartialLoad = false
  Refine = true
  Relative = true
  Support = -> [Body[Sketch074.]]
  _Version = 2
FEATURE [PartDesign::SubShapeBinder] Binder001
  BindCopyOnChange = 0
  BindMode = 0
  ClaimChildren = false
  Context = -> Body007 [Binder001.]
  Fuse = false
  MakeFace = true
  OffsetFill = false
  OffsetIntersection = false
  OffsetJoinType = 0
  OffsetOpenResult = false
  PartialLoad = false
  Refine = true
  Relative = true
  Support = -> [Body[Sketch075.]]
  _Version = 2
FEATURE [Mesh::Feature] logo_per_PCB_definitivo_positivo
  Placement = pos=(-191,17,-66) rot=(0,1,1;0rad)
FEATURE [Sketcher::SketchObject] Sketch114  label="Sketch114 - base lato DX"
  ArcFitTolerance = 1e-06
  AttachmentSupport = -> [Binder001]
  ExternalGeometry = -> [Binder001]
  FullyConstrained = true
  MakeInternals = false
  MapMode = 5
  Placement = pos=(0,1e-15,0) rot=(0,0.707107,0.707107;3.14159rad)
  sketch-geometry (30):
    g0: Circle CenterX=5.6 CenterY=34.8 CenterZ=0 NormalX=0 NormalY=0 NormalZ=1 AngleXU=0 Radius=1.8
    g1: Circle CenterX=5.6 CenterY=7.6 CenterZ=0 NormalX=0 NormalY=0 NormalZ=1 AngleXU=0 Radius=1.8
    g2: Circle CenterX=24.2 CenterY=26.7 CenterZ=0 NormalX=0 NormalY=0 NormalZ=1 AngleXU=0 Radius=3
    g3: Circle CenterX=24.2 CenterY=15.7 CenterZ=0 NormalX=0 NormalY=0 NormalZ=1 AngleXU=0 Radius=3
    g4: Circle CenterX=36.2 CenterY=21.2 CenterZ=0 NormalX=0 NormalY=0 NormalZ=1 AngleXU=0 Radius=2.8
    g5: Circle CenterX=78.51 CenterY=34.8 CenterZ=0 NormalX=0 NormalY=0 NormalZ=1 AngleXU=0 Radius=1.8
    g6: Circle CenterX=78.51 CenterY=7.6 CenterZ=0 NormalX=0 NormalY=0 NormalZ=1 AngleXU=0 Radius=1.8
    g7: Circle CenterX=184.08 CenterY=34.8 CenterZ=0 NormalX=0 NormalY=0 NormalZ=1 AngleXU=0 Radius=1.8
    g8: Circle CenterX=213.443 CenterY=-76.8316 CenterZ=0 NormalX=0 NormalY=0 NormalZ=1 AngleXU=0 Radius=1.8
    g9: Circle CenterX=179.305 CenterY=-76.8316 CenterZ=0 NormalX=0 NormalY=0 NormalZ=1 AngleXU=0 Radius=1.8
    g10: ArcOfCircle [constr] CenterX=132.428 CenterY=4 CenterZ=0 NormalX=0 NormalY=0 NormalZ=1 AngleXU=0 Radius=16 StartAngle=0.314159 EndAngle=1.5708
    g11: ArcOfCircle CenterX=107.6 CenterY=4 CenterZ=0 NormalX=0 NormalY=0 NormalZ=1 AngleXU=0 Radius=16 StartAngle=1.5708 EndAngle=3.00366
    g12: ArcOfCircle CenterX=207.583 CenterY=4 CenterZ=0 NormalX=0 NormalY=0 NormalZ=1 AngleXU=0 Radius=17 StartAngle=1.85815 EndAngle=3.57792
    g13: ArcOfCircle CenterX=184.801 CenterY=-67.3089 CenterZ=0 NormalX=0 NormalY=0 NormalZ=1 AngleXU=0 Radius=33.7833 StartAngle=5.88425 EndAngle=6.71952
    g14: LineSegment StartX=0 StartY=39.2 StartZ=0 EndX=0 EndY=3.2 EndZ=0
    g15: LineSegment StartX=0 StartY=3.2 StartZ=0 EndX=82.8 EndY=3.2 EndZ=0
    g16: LineSegment StartX=82.8 StartY=3.2 StartZ=0 EndX=82.8 EndY=6.2 EndZ=0
    g17: LineSegment StartX=82.8 StartY=6.2 StartZ=0 EndX=91.752 EndY=6.2 EndZ=0
    g18: LineSegment StartX=107.6 StartY=20 StartZ=0 EndX=132.428 EndY=20 EndZ=0
    g19: LineSegment StartX=147.645 StartY=8.94427 StartZ=0 EndX=176.685 EndY=-80.4316 EndZ=0
    g20: LineSegment StartX=176.685 StartY=-80.4316 StartZ=0 EndX=215.932 EndY=-80.4316 EndZ=0
    g21: LineSegment StartX=215.42 StartY=-53.0314 StartZ=0 EndX=192.176 EndY=-3.18451 EndZ=0
    g22: LineSegment StartX=202.765 StartY=20.303 StartZ=0 EndX=195.887 EndY=39.2 EndZ=0
    g23: LineSegment StartX=195.887 StartY=39.2 StartZ=0 EndX=0 EndY=39.2 EndZ=0
    g24: LineSegment StartX=196.467 StartY=26.4942 StartZ=0 EndX=194.073 EndY=33.0721 EndZ=0
    g25: LineSegment StartX=194.073 StartY=33.0721 StartZ=0 EndX=189.939 EndY=31.5672 EndZ=0
    g26: LineSegment StartX=189.939 StartY=31.5672 StartZ=0 EndX=192.333 EndY=24.9893 EndZ=0
    g27: LineSegment StartX=192.333 StartY=24.9893 StartZ=0 EndX=196.467 EndY=26.4942 EndZ=0
    g28: LineSegment StartX=132.428 StartY=20 StartZ=0 EndX=144.053 EndY=20 EndZ=0
    g29: LineSegment StartX=144.053 StartY=20 StartZ=0 EndX=147.645 EndY=8.94427 EndZ=0
  constraints (65):
    c: Equal(g0,g-25)
    c: Equal(g2,g-29)
    c: Equal(g3,g-30)
    c: Equal(g4,g-28)
    c: Equal(g1,g-26)
    c: Coincident(g0,g-25)
    c: Coincident(g1,g-26)
    c: Coincident(g2,g-29)
    c: Coincident(g3,g-30)
    c: Coincident(g4,g-28)
    c: Equal(g5,g-23)
    c: Equal(g6,g-24)
    c: Coincident(g5,g-23)
    c: Coincident(g6,g-24)
    c: Equal(g7,g-20)
    c: Coincident(g7,g-20)
    c: Equal(g9,g-22)
    c: Coincident(g9,g-22)
    c: Equal(g8,g-21)
    c: Coincident(g8,g-21)
    c: Equal(g13,g-12)
    c: Equal(g12,g-14)
    c: Equal(g10,g-9)
    c: Equal(g11,g-7)
    c: Coincident(g14,g-27)
    c: Coincident(g14,g-27)
    c: Coincident(g15,g14)
    c: Coincident(g15,g-5)
    c: Coincident(g16,g15)
    c: Coincident(g16,g-6)
    c: Coincident(g17,g16)
    c: Coincident(g17,g-7)
    c: Coincident(g11,g17)
    c: Coincident(g11,g-8)
    c: Coincident(g18,g11)
    c: Coincident(g18,g-9)
    c: Coincident(g10,g18)
    c: Coincident(g10,g-10)
    c: Coincident(g19,g10)
    c: Coincident(g19,g-11)
    c: Coincident(g20,g19)
    c: Coincident(g20,g-12)
    c: Coincident(g13,g20)
    c: Coincident(g13,g-13)
    c: Coincident(g21,g13)
    c: Coincident(g21,g-14)
    c: Coincident(g12,g21)
    c: Coincident(g12,g-15)
    c: Coincident(g22,g12)
    c: Coincident(g22,g-15)
    c: Coincident(g23,g22)
    c: Coincident(g23,g14)
    c: Coincident(g24,g-18)
    c: Coincident(g24,g-16)
    c: Coincident(g25,g24)
    c: Coincident(g25,g-19)
    c: Coincident(g26,g25)
    c: Coincident(g26,g-19)
    c: Coincident(g27,g26)
    c: Coincident(g27,g24)
    c: Coincident(g29,g10)
    c: Coincident(g28,g10)
    c: Coincident(g29,g28)
    c: Parallel(g28,g18)
    c: Parallel(g29,g19)
FEATURE [PartDesign::Pad] Pad011
  Direction = (0,1,-2e-16)
  Length = 2
  Length2 = 10
  Profile = -> Sketch114
  ReferenceAxis = -> Sketch114 [N_Axis]
  Refine = true
  Reversed = true
  Suppressed = false
  Type = 0
FEATURE [Sketcher::SketchObject] Sketch115
  ArcFitTolerance = 1e-06
  AttachmentSupport = -> [Pad011]
  ExternalGeometry = -> [Binder001]
  FullyConstrained = true
  MakeInternals = false
  MapMode = 5
  Placement = pos=(0,1.7e-15,0) rot=(0,0.707107,0.707107;3.14159rad)
  sketch-geometry (4):
    g0: ArcOfCircle CenterX=24.2 CenterY=26.7 CenterZ=0 NormalX=0 NormalY=0 NormalZ=1 AngleXU=0 Radius=3 StartAngle=4.48384e-08 EndAngle=3.14159
    g1: ArcOfCircle CenterX=24.2 CenterY=15.7 CenterZ=0 NormalX=0 NormalY=0 NormalZ=1 AngleXU=0 Radius=3 StartAngle=3.14159 EndAngle=6.28318
    g2: LineSegment StartX=21.2 StartY=26.7 StartZ=0 EndX=21.2 EndY=15.7 EndZ=0
    g3: LineSegment StartX=27.2 StartY=26.7 StartZ=0 EndX=27.2 EndY=15.7 EndZ=0
  constraints (12):
    c: Equal(g1,g-4)
    c: Equal(g0,g-3)
    c: Coincident(g0,g-3)
    c: Coincident(g1,g-4)
    c: Vertical(g2)
    c: Vertical(g3)
    c: Tangent(g3,g-3)
    c: Tangent(g2,g-3)
    c: Coincident(g0,g2)
    c: Coincident(g0,g3)
    c: Coincident(g1,g2)
    c: Coincident(g3,g1)
FEATURE [Sketcher::SketchObject] Sketch117  label="Sketch117 - fori per inserto M3 x 3 x 4.5"
  ArcFitTolerance = 1e-06
  AttachmentSupport = -> [Pad011]
  ExternalGeometry = -> [Binder001]
  FullyConstrained = true
  MakeInternals = false
  MapMode = 5
  Placement = pos=(0,1.7e-15,0) rot=(0,0.707107,0.707107;3.14159rad)
  sketch-geometry (4):
    g0: Circle CenterX=43.2 CenterY=30.3 CenterZ=0 NormalX=0 NormalY=0 NormalZ=1 AngleXU=0 Radius=2.25
    g1: Circle CenterX=43.2 CenterY=12.1 CenterZ=0 NormalX=0 NormalY=0 NormalZ=1 AngleXU=0 Radius=2.25
    g2: Circle CenterX=18.6 CenterY=30.3 CenterZ=0 NormalX=0 NormalY=0 NormalZ=1 AngleXU=0 Radius=2.25
    g3: Circle CenterX=18.6 CenterY=12.1 CenterZ=0 NormalX=0 NormalY=0 NormalZ=1 AngleXU=0 Radius=2.25
  constraints (8):
    c: Diameter(g0) = 4.5
    c: Diameter(g1) = 4.5
    c: Diameter(g2) = 4.5
    c: Diameter(g3) = 4.5
    c: Coincident(g2,g-3)
    c: Coincident(g3,g-6)
    c: Coincident(g0,g-4)
    c: Coincident(g1,g-5)
FEATURE [Sketcher::SketchObject] Sketch118
  ArcFitTolerance = 1e-06
  AttachmentSupport = -> [Pad011]
  ExternalGeometry = -> [Binder001]
  FullyConstrained = true
  MakeInternals = false
  MapMode = 5
  Placement = pos=(0,-2,0) rot=(1,0,0;1.5708rad)
  sketch-geometry (12):
    g0: Circle CenterX=-78.51 CenterY=34.8 CenterZ=0 NormalX=0 NormalY=0 NormalZ=1 AngleXU=0 Radius=1.8
    g1: Circle CenterX=-78.51 CenterY=7.6 CenterZ=0 NormalX=0 NormalY=0 NormalZ=1 AngleXU=0 Radius=1.8
    g2: Circle CenterX=-5.6 CenterY=34.8 CenterZ=0 NormalX=0 NormalY=0 NormalZ=1 AngleXU=0 Radius=1.8
    g3: Circle CenterX=-5.6 CenterY=7.6 CenterZ=0 NormalX=0 NormalY=0 NormalZ=1 AngleXU=0 Radius=1.8
    g4: LineSegment StartX=0 StartY=39.2 StartZ=0 EndX=0 EndY=3.2 EndZ=0
    g5: LineSegment StartX=0 StartY=3.2 StartZ=0 EndX=-82.8 EndY=3.2 EndZ=0
    g6: LineSegment StartX=-82.8 StartY=3.2 StartZ=0 EndX=-82.8 EndY=39.2 EndZ=0
    g7: LineSegment StartX=-82.8 StartY=39.2 StartZ=0 EndX=0 EndY=39.2 EndZ=0
    g8: ArcOfCircle CenterX=-65 CenterY=21.2 CenterZ=0 NormalX=0 NormalY=0 NormalZ=1 AngleXU=0 Radius=10 StartAngle=1.5708 EndAngle=4.71239
    g9: ArcOfCircle CenterX=-19 CenterY=21.2 CenterZ=0 NormalX=0 NormalY=0 NormalZ=1 AngleXU=0 Radius=10 StartAngle=4.71239 EndAngle=7.85398
    g10: LineSegment StartX=-65 StartY=31.2 StartZ=0 EndX=-19 EndY=31.2 EndZ=0
    g11: LineSegment StartX=-65 StartY=11.2 StartZ=0 EndX=-19 EndY=11.2 EndZ=0
  constraints (25):
    c: Equal(g2,g-5)
    c: Equal(g3,g-7)
    c: Equal(g1,g-6)
    c: Equal(g0,g-4)
    c: Coincident(g0,g-4)
    c: Coincident(g1,g-6)
    c: Coincident(g3,g-7)
    c: Coincident(g2,g-5)
    c: Coincident(g4,g-8)
    c: Coincident(g4,g-9)
    c: Coincident(g5,g4)
    c: Coincident(g5,g-10)
    c: Coincident(g6,g5)
    c: PointOnObject(g6,g-3)
    c: Vertical(g6)
    c: Coincident(g7,g6)
    c: Coincident(g7,g4)
    c: Tangent(g8,g10) = 1.5708
    c: Tangent(g8,g11) = -1.5708
    c: Tangent(g9,g10) = 1.5708
    c: Tangent(g9,g11) = -1.5708
    c: Equal(g8,g9)
    c: Radius(g8) = 10
    c: Coincident(g8,g-11)
    c: Coincident(g9,g-12)
FEATURE [Sketcher::SketchObject] Sketch120
  ArcFitTolerance = 1e-06
  AttachmentSupport = -> [Pad011]
  ExternalGeometry = -> [Binder001]
  FullyConstrained = true
  MakeInternals = false
  MapMode = 5
  Placement = pos=(0,-2,0) rot=(1,0,0;1.5708rad)
  sketch-geometry (4):
    g0: LineSegment StartX=-137.815 StartY=39.2 StartZ=0 EndX=-142.655 EndY=24.303 EndZ=0
    g1: LineSegment StartX=-137.815 StartY=39.2 StartZ=0 EndX=-110.815 EndY=39.2 EndZ=0
    g2: LineSegment StartX=-142.655 StartY=24.303 StartZ=0 EndX=-110.815 EndY=24.303 EndZ=0
    g3: ArcOfCircle CenterX=-92.2534 CenterY=31.7515 CenterZ=0 NormalX=0 NormalY=0 NormalZ=1 AngleXU=0 Radius=20 StartAngle=2.75997 EndAngle=3.52321
  constraints (12):
    c: PointOnObject(g0,g-3)
    c: Coincident(g1,g0)
    c: PointOnObject(g1,g-3)
    c: Coincident(g2,g0)
    c: Horizontal(g2)
    c: Tangent(g0,g-4)
    c: Vertical(g2,g1)
    c: DistanceX(g1,g1) = 27
    c: DistanceY(g-6,g0) = 4
    c: Radius(g3) = 20
    c: Coincident(g3,g1)
    c: Coincident(g3,g2)
FEATURE [Sketcher::SketchObject] Sketch121
  ArcFitTolerance = 1e-06
  AttachmentSupport = -> [Pad011]
  ExternalGeometry = -> [Binder001]
  FullyConstrained = true
  MakeInternals = false
  MapMode = 5
  Placement = pos=(0,-2,0) rot=(1,0,0;1.5708rad)
  sketch-geometry (15):
    g0: LineSegment StartX=-137.815 StartY=39.2 StartZ=0 EndX=-143.955 EndY=20.303 EndZ=0
    g1: LineSegment StartX=-143.955 StartY=20.303 StartZ=0 EndX=-190.141 EndY=20.303 EndZ=0
    g2: LineSegment StartX=-190.141 StartY=20.303 StartZ=0 EndX=-186.139 EndY=31.3 EndZ=0
    g3: LineSegment StartX=-178.754 StartY=39.2 StartZ=0 EndX=-180.791 EndY=33.6029 EndZ=0
    g4: ArcOfCircle CenterX=-184.08 CenterY=34.8 CenterZ=0 NormalX=0 NormalY=0 NormalZ=1 AngleXU=0 Radius=3.5 StartAngle=4.71239 EndAngle=5.93412
    g5: LineSegment StartX=-184.08 StartY=31.3 StartZ=0 EndX=-186.139 EndY=31.3 EndZ=0
    g6: LineSegment StartX=-137.815 StartY=39.2 StartZ=0 EndX=-156.815 EndY=39.2 EndZ=0
    g7: LineSegment StartX=-168.815 StartY=39.2 StartZ=0 EndX=-178.754 EndY=39.2 EndZ=0
    g8: LineSegment StartX=-157.815 StartY=39.2 StartZ=0 EndX=-167.815 EndY=39.2 EndZ=0
    g9: LineSegment StartX=-168.815 StartY=31.2 StartZ=0 EndX=-156.815 EndY=31.2 EndZ=0
    g10: LineSegment StartX=-167.436 StartY=36.2 StartZ=0 EndX=-157.436 EndY=36.2 EndZ=0
    g11: ArcOfCircle CenterX=-176.411 CenterY=35.2 CenterZ=0 NormalX=0 NormalY=0 NormalZ=1 AngleXU=0 Radius=20 StartAngle=6.08183 EndAngle=6.48454
    g12: ArcOfCircle CenterX=-188.411 CenterY=35.2 CenterZ=0 NormalX=0 NormalY=0 NormalZ=1 AngleXU=0 Radius=20 StartAngle=6.08183 EndAngle=6.48454
    g13: ArcOfCircle CenterX=-177.411 CenterY=35.2 CenterZ=0 NormalX=0 NormalY=0 NormalZ=1 AngleXU=0 Radius=20 StartAngle=0.0500209 EndAngle=0.201358
    g14: ArcOfCircle CenterX=-187.411 CenterY=35.2 CenterZ=0 NormalX=0 NormalY=0 NormalZ=1 AngleXU=0 Radius=20 StartAngle=0.0500209 EndAngle=0.201358
  constraints (46):
    c: PointOnObject(g0,g-3)
    c: Tangent(g0,g-5)
    c: Coincident(g1,g0)
    c: Horizontal(g1)
    c: Coincident(g2,g1)
    c: PointOnObject(g3,g-3)
    c: Parallel(g3,g-6)
    c: Parallel(g2,g-6)
    c: Radius(g4) = 3.5
    c: Coincident(g4,g-7)
    c: Tangent(g3,g4) = 1.5708
    c: Horizontal(g5)
    c: Tangent(g5,g4) = 1.5708
    c: DistanceX(g-8,g5) = 3.8
    c: Coincident(g2,g5)
    c: Coincident(g6,g0)
    c: PointOnObject(g6,g-3)
    c: DistanceX(g6,g6) = 19
    c: PointOnObject(g7,g-3)
    c: DistanceX(g7,g6) = 12
    c: Coincident(g7,g3)
    c: PointOnObject(g8,g-3)
    c: PointOnObject(g8,g-3)
    c: DistanceX(g8,g8) = 10
    c: DistanceX(g8,g6) = 1
    c: Horizontal(g9)
    c: Vertical(g7,g9)
    c: Vertical(g6,g9)
    c: DistanceY(g9,g7) = 8
    c: Horizontal(g10)
    c: Equal(g8,g10)
    c: DistanceY(g10,g8) = 3
    c: Radius(g11) = 20
    c: Coincident(g11,g6)
    c: Coincident(g11,g9)
    c: Radius(g12) = 20
    c: Coincident(g12,g7)
    c: Coincident(g12,g9)
    c: Equal(g13,g11)
    c: Coincident(g13,g8)
    c: Coincident(g13,g10)
    c: Horizontal(g13,g11)
    c: Equal(g14,g12)
    c: Coincident(g14,g8)
    c: Coincident(g14,g10)
    c: Horizontal(g1,g-6)
FEATURE [Sketcher::SketchObject] Sketch122
  ArcFitTolerance = 1e-06
  AttachmentSupport = -> [Pad011]
  ExternalGeometry = -> [Binder001]
  FullyConstrained = true
  MakeInternals = false
  MapMode = 5
  Placement = pos=(0,-2,0) rot=(1,0,0;1.5708rad)
  sketch-geometry (8):
    g0: LineSegment StartX=-202.765 StartY=20.303 StartZ=0 EndX=-143.955 EndY=20.303 EndZ=0
    g1: ArcOfCircle CenterX=-184.801 CenterY=-67.3089 CenterZ=0 NormalX=0 NormalY=0 NormalZ=1 AngleXU=0 Radius=33.7833 StartAngle=2.70526 EndAngle=3.54053
    g2: LineSegment StartX=-176.685 StartY=-80.4316 StartZ=0 EndX=-215.932 EndY=-80.4316 EndZ=0
    g3: LineSegment StartX=-215.42 StartY=-53.0315 StartZ=0 EndX=-192.176 EndY=-3.18454 EndZ=0
    g4: ArcOfCircle CenterX=-207.583 CenterY=4 CenterZ=0 NormalX=0 NormalY=0 NormalZ=1 AngleXU=0 Radius=17 StartAngle=5.84685 EndAngle=7.56663
    g5: Circle CenterX=-213.443 CenterY=-76.8316 CenterZ=0 NormalX=0 NormalY=0 NormalZ=1 AngleXU=0 Radius=3
    g6: Circle CenterX=-179.305 CenterY=-76.8316 CenterZ=0 NormalX=0 NormalY=0 NormalZ=1 AngleXU=0 Radius=3
    g7: LineSegment StartX=-143.955 StartY=20.303 StartZ=0 EndX=-176.685 EndY=-80.4316 EndZ=0
  constraints (18):
    c: Coincident(g0,g-6)
    c: Coincident(g1,g-7)
    c: Coincident(g1,g-8)
    c: Coincident(g2,g1)
    c: Tangent(g3,g-5)
    c: Coincident(g4,g-6)
    c: Coincident(g4,g0)
    c: Coincident(g3,g4)
    c: Coincident(g1,g3)
    c: Diameter(g5) = 6
    c: Diameter(g6) = 6
    c: Coincident(g5,g-9)
    c: Coincident(g6,g-10)
    c: Horizontal(g0)
    c: Horizontal(g2)
    c: Coincident(g7,g0)
    c: Coincident(g7,g2)
    c: Tangent(g7,g-4)
FEATURE [Sketcher::SketchObject] Sketch123
  ArcFitTolerance = 1e-06
  AttachmentSupport = -> [Pad011]
  ExternalGeometry = -> [Binder001]
  FullyConstrained = true
  MakeInternals = false
  MapMode = 5
  Placement = pos=(0,-2,0) rot=(1,0,0;1.5708rad)
  sketch-geometry (4):
    g0: LineSegment StartX=-108 StartY=36.8 StartZ=0 EndX=-90 EndY=36.8 EndZ=0
    g1: LineSegment StartX=-108 StartY=36.8 StartZ=0 EndX=-108 EndY=26.8 EndZ=0
    g2: LineSegment StartX=-108 StartY=26.8 StartZ=0 EndX=-90 EndY=26.8 EndZ=0
    g3: ArcOfCircle CenterX=-94 CenterY=31.8 CenterZ=0 NormalX=0 NormalY=0 NormalZ=1 AngleXU=0 Radius=6.40312 StartAngle=5.38713 EndAngle=7.17924
  constraints (13):
    c: Horizontal(g0)
    c: Coincident(g1,g0)
    c: Vertical(g1)
    c: Coincident(g2,g1)
    c: Horizontal(g2)
    c: DistanceX(g0,g0) = 18
    c: DistanceY(g1,g1) = 10
    c: Equal(g0,g2)
    c: DistanceX(g0,g-3) = 90
    c: DistanceY(g0,g-3) = 2.4
    c: Coincident(g3,g0)
    c: Coincident(g3,g2)
    c: DistanceX(g3,g0) = 4
FEATURE [PartDesign::Chamfer] Chamfer014
  Angle = 45
  Base = -> Pad011 [Edge80,Edge4,Edge7]
  BaseFeature = -> Pad011
  ChamferType = 0
  FlipDirection = false
  Refine = true
  Size = 1.9
  Size2 = 1
  SupportTransform = false
  Suppressed = false
  UseAllEdges = false
FEATURE [PartDesign::Pocket] Pocket006
  BaseFeature = -> Chamfer014
  Direction = (0,-1,2e-16)
  Length = 1.2
  Length2 = 5
  Profile = -> Sketch115
  ReferenceAxis = -> Sketch115 [N_Axis]
  Refine = true
  Suppressed = false
  Type = 0
FEATURE [Sketcher::SketchObject] Sketch116  label="Sketch116 - pieno per inserto M3 x 3 x 4,5"
  ArcFitTolerance = 1e-06
  AttachmentSupport = -> [Pocket006]
  ExternalGeometry = -> [Binder001]
  FullyConstrained = true
  MakeInternals = false
  MapMode = 5
  Placement = pos=(0,1.7e-15,0) rot=(0,0.707107,0.707107;3.14159rad)
  sketch-geometry (4):
    g0: Circle CenterX=43.2 CenterY=30.3 CenterZ=0 NormalX=0 NormalY=0 NormalZ=1 AngleXU=0 Radius=3.4
    g1: Circle CenterX=43.2 CenterY=12.1 CenterZ=0 NormalX=0 NormalY=0 NormalZ=1 AngleXU=0 Radius=3.4
    g2: Circle CenterX=18.6 CenterY=30.3 CenterZ=0 NormalX=0 NormalY=0 NormalZ=1 AngleXU=0 Radius=3.4
    g3: Circle CenterX=18.6 CenterY=12.1 CenterZ=0 NormalX=0 NormalY=0 NormalZ=1 AngleXU=0 Radius=3.4
  constraints (8):
    c: Diameter(g0) = 6.8
    c: Diameter(g1) = 6.8
    c: Diameter(g2) = 6.8
    c: Diameter(g3) = 6.8
    c: Coincident(g2,g-3)
    c: Coincident(g0,g-4)
    c: Coincident(g3,g-6)
    c: Coincident(g1,g-5)
FEATURE [PartDesign::Pad] Pad012
  BaseFeature = -> Pocket006
  Direction = (0,1,-2e-16)
  Length = 2.4
  Length2 = 10
  Profile = -> Sketch116
  ReferenceAxis = -> Sketch116 [N_Axis]
  Refine = true
  Suppressed = false
  Type = 0
FEATURE [PartDesign::Pocket] Pocket007
  BaseFeature = -> Pad012
  Direction = (0,-1,2e-16)
  Length = 0.6
  Length2 = 2.4
  Profile = -> Sketch117
  ReferenceAxis = -> Sketch117 [N_Axis]
  Refine = true
  Suppressed = false
  Type = 4
FEATURE [PartDesign::Pad] Pad013
  BaseFeature = -> Pocket007
  Direction = (0,-1,2e-16)
  Length = 1.6
  Length2 = 10
  Profile = -> Sketch118
  ReferenceAxis = -> Sketch118 [N_Axis]
  Refine = true
  Suppressed = false
  Type = 0
FEATURE [Sketcher::SketchObject] Sketch119
  ArcFitTolerance = 1e-06
  AttachmentSupport = -> [Pad013]
  ExternalGeometry = -> [Binder001]
  FullyConstrained = true
  MakeInternals = false
  MapMode = 5
  Placement = pos=(0,-3.6,0) rot=(1,0,0;1.5708rad)
  sketch-geometry (21):
    g0: LineSegment [constr] StartX=-82.8 StartY=3.2 StartZ=0 EndX=-82.8 EndY=39.2 EndZ=0
    g1: ArcOfCircle CenterX=-78.51 CenterY=34.8 CenterZ=0 NormalX=0 NormalY=0 NormalZ=1 AngleXU=0 Radius=3.5 StartAngle=4.71239 EndAngle=6.28319
    g2: ArcOfCircle CenterX=-78.51 CenterY=7.6 CenterZ=0 NormalX=0 NormalY=0 NormalZ=1 AngleXU=0 Radius=3.5 StartAngle=0 EndAngle=1.5708
    g3: ArcOfCircle CenterX=-5.6 CenterY=34.8 CenterZ=0 NormalX=0 NormalY=0 NormalZ=1 AngleXU=0 Radius=3.5 StartAngle=3.14159 EndAngle=4.71239
    g4: ArcOfCircle CenterX=-5.6 CenterY=7.6 CenterZ=0 NormalX=0 NormalY=0 NormalZ=1 AngleXU=0 Radius=3.5 StartAngle=1.5708 EndAngle=3.14159
    g5: LineSegment StartX=0 StartY=39.2 StartZ=0 EndX=0 EndY=31.3 EndZ=0
    g6: LineSegment StartX=0 StartY=39.2 StartZ=0 EndX=-9.1 EndY=39.2 EndZ=0
    g7: LineSegment StartX=0 StartY=3.2 StartZ=0 EndX=0 EndY=11.1 EndZ=0
    g8: LineSegment StartX=0 StartY=3.2 StartZ=0 EndX=-9.1 EndY=3.2 EndZ=0
    g9: LineSegment StartX=-82.8 StartY=3.2 StartZ=0 EndX=-75.01 EndY=3.2 EndZ=0
    g10: LineSegment StartX=-82.8 StartY=3.2 StartZ=0 EndX=-82.8 EndY=11.1 EndZ=0
    g11: LineSegment StartX=-82.8 StartY=39.2 StartZ=0 EndX=-82.8 EndY=31.3 EndZ=0
    g12: LineSegment StartX=-82.8 StartY=39.2 StartZ=0 EndX=-75.01 EndY=39.2 EndZ=0
    g13: LineSegment StartX=-82.8 StartY=31.3 StartZ=0 EndX=-78.51 EndY=31.3 EndZ=0
    g14: LineSegment StartX=-75.01 StartY=39.2 StartZ=0 EndX=-75.01 EndY=34.8 EndZ=0
    g15: LineSegment StartX=-82.8 StartY=11.1 StartZ=0 EndX=-78.51 EndY=11.1 EndZ=0
    g16: LineSegment StartX=-75.01 StartY=3.2 StartZ=0 EndX=-75.01 EndY=7.6 EndZ=0
    g17: LineSegment StartX=-9.1 StartY=39.2 StartZ=0 EndX=-9.1 EndY=34.8 EndZ=0
    g18: LineSegment StartX=0 StartY=31.3 StartZ=0 EndX=-5.6 EndY=31.3 EndZ=0
    g19: LineSegment StartX=0 StartY=11.1 StartZ=0 EndX=-5.6 EndY=11.1 EndZ=0
    g20: LineSegment StartX=-9.1 StartY=3.2 StartZ=0 EndX=-9.1 EndY=7.6 EndZ=0
  constraints (51):
    c: Coincident(g0,g-10)
    c: PointOnObject(g0,g-8)
    c: Vertical(g0)
    c: Coincident(g1,g-3)
    c: Coincident(g2,g-4)
    c: Coincident(g3,g-5)
    c: Coincident(g4,g-6)
    c: Radius(g4) = 3.5
    c: Radius(g3) = 3.5
    c: Radius(g1) = 3.5
    c: Radius(g2) = 3.5
    c: Coincident(g5,g-9)
    c: PointOnObject(g5,g-9)
    c: Coincident(g6,g5)
    c: PointOnObject(g6,g-8)
    c: Coincident(g7,g-9)
    c: PointOnObject(g7,g-9)
    c: Coincident(g8,g7)
    c: PointOnObject(g8,g-7)
    c: Coincident(g9,g0)
    c: PointOnObject(g9,g-7)
    c: Coincident(g10,g0)
    c: PointOnObject(g10,g0)
    c: Coincident(g11,g0)
    c: PointOnObject(g11,g0)
    c: Coincident(g12,g0)
    c: PointOnObject(g12,g-8)
    c: Coincident(g13,g11)
    c: Horizontal(g13)
    c: Coincident(g14,g12)
    c: Vertical(g14)
    c: Coincident(g15,g10)
    c: Horizontal(g15)
    c: Coincident(g16,g9)
    c: Vertical(g16)
    c: Coincident(g17,g6)
    c: Vertical(g17)
    c: Coincident(g18,g5)
    c: Horizontal(g18)
    c: Coincident(g19,g7)
    c: Horizontal(g19)
    c: Coincident(g20,g8)
    c: Vertical(g20)
    c: Tangent(g20,g4) = 1.5708
    c: Tangent(g4,g19) = -1.5708
    c: Tangent(g18,g3) = 1.5708
    c: Tangent(g3,g17) = -1.5708
    c: Tangent(g13,g1) = -1.5708
    c: Tangent(g1,g14) = 1.5708
    c: Tangent(g16,g2) = -1.5708
    c: Tangent(g2,g15) = 1.5708
FEATURE [PartDesign::Pocket] Pocket008
  BaseFeature = -> Pad013
  Direction = (0,1,-2e-16)
  Length = 1.6
  Length2 = 5
  Profile = -> Sketch119
  ReferenceAxis = -> Sketch119 [N_Axis]
  Refine = true
  Suppressed = false
  Type = 0
FEATURE [PartDesign::Pad] Pad017
  BaseFeature = -> Pocket008
  Direction = (0,-1,2e-16)
  Length = 1.6
  Length2 = 10
  Profile = -> Sketch123
  ReferenceAxis = -> Sketch123 [N_Axis]
  Refine = true
  Suppressed = false
  Type = 0
FEATURE [Sketcher::SketchObject] Sketch125
  ArcFitTolerance = 1e-06
  AttachmentSupport = -> [Pad017]
  ExternalGeometry = -> [Pad017]
  FullyConstrained = true
  MakeInternals = false
  MapMode = 5
  Placement = pos=(0,-3.6,8e-16) rot=(1,0,0;1.5708rad)
  sketch-geometry (20):
    g0: LineSegment StartX=-108 StartY=35.8 StartZ=0 EndX=-108 EndY=35 EndZ=0
    g1: LineSegment StartX=-108 StartY=35 StartZ=0 EndX=-97 EndY=35 EndZ=0
    g2: LineSegment StartX=-97 StartY=35 StartZ=0 EndX=-97 EndY=35.8 EndZ=0
    g3: LineSegment StartX=-97 StartY=35.8 StartZ=0 EndX=-108 EndY=35.8 EndZ=0
    g4: LineSegment StartX=-108 StartY=28.6 StartZ=0 EndX=-108 EndY=27.8 EndZ=0
    g5: LineSegment StartX=-108 StartY=27.8 StartZ=0 EndX=-97 EndY=27.8 EndZ=0
    g6: LineSegment StartX=-97 StartY=27.8 StartZ=0 EndX=-97 EndY=28.6 EndZ=0
    g7: LineSegment StartX=-97 StartY=28.6 StartZ=0 EndX=-108 EndY=28.6 EndZ=0
    g8: LineSegment StartX=-108 StartY=30.4 StartZ=0 EndX=-108 EndY=29.6 EndZ=0
    g9: LineSegment StartX=-108 StartY=29.6 StartZ=0 EndX=-97 EndY=29.6 EndZ=0
    g10: LineSegment StartX=-97 StartY=29.6 StartZ=0 EndX=-97 EndY=30.4 EndZ=0
    g11: LineSegment StartX=-97 StartY=30.4 StartZ=0 EndX=-108 EndY=30.4 EndZ=0
    g12: LineSegment StartX=-108 StartY=32.2 StartZ=0 EndX=-108 EndY=31.4 EndZ=0
    g13: LineSegment StartX=-108 StartY=31.4 StartZ=0 EndX=-97 EndY=31.4 EndZ=0
    g14: LineSegment StartX=-97 StartY=31.4 StartZ=0 EndX=-97 EndY=32.2 EndZ=0
    g15: LineSegment StartX=-97 StartY=32.2 StartZ=0 EndX=-108 EndY=32.2 EndZ=0
    g16: LineSegment StartX=-108 StartY=34 StartZ=0 EndX=-108 EndY=33.2 EndZ=0
    g17: LineSegment StartX=-108 StartY=33.2 StartZ=0 EndX=-97 EndY=33.2 EndZ=0
    g18: LineSegment StartX=-97 StartY=33.2 StartZ=0 EndX=-97 EndY=34 EndZ=0
    g19: LineSegment StartX=-97 StartY=34 StartZ=0 EndX=-108 EndY=34 EndZ=0
  constraints (55):
    c: Coincident(g1,g0)
    c: Horizontal(g1)
    c: Coincident(g2,g1)
    c: Vertical(g2)
    c: Coincident(g3,g2)
    c: Horizontal(g3)
    c: Coincident(g3,g0)
    c: DistanceX(g1,g1) = 11
    c: DistanceY(g2,g2) = 0.8
    c: Coincident(g5,g4)
    c: Horizontal(g5)
    c: Coincident(g6,g5)
    c: Vertical(g6)
    c: Coincident(g7,g6)
    c: Horizontal(g7)
    c: Coincident(g7,g4)
    c: Coincident(g9,g8)
    c: Horizontal(g9)
    c: Coincident(g10,g9)
    c: Vertical(g10)
    c: Coincident(g11,g10)
    c: Horizontal(g11)
    c: Coincident(g11,g8)
    c: Coincident(g13,g12)
    c: Horizontal(g13)
    c: Coincident(g14,g13)
    c: Vertical(g14)
    c: Coincident(g15,g14)
    c: Horizontal(g15)
    c: Coincident(g15,g12)
    c: Coincident(g17,g16)
    c: Horizontal(g17)
    c: Coincident(g18,g17)
    c: Vertical(g18)
    c: Coincident(g19,g18)
    c: Horizontal(g19)
    c: Coincident(g19,g16)
    c: Equal(g3,g19)
    c: Equal(g3,g15)
    c: Equal(g3,g11)
    c: Equal(g3,g7)
    c: Equal(g2,g18)
    c: Equal(g2,g14)
    c: Equal(g2,g10)
    c: Equal(g2,g6)
    c: DistanceY(g-4,g4) = 1
    c: DistanceY(g4,g8) = 1
    c: DistanceY(g8,g12) = 1
    c: DistanceY(g12,g16) = 1
    c: DistanceY(g16,g0) = 1
    c: Tangent(g0,g-5)
    c: Tangent(g16,g-5)
    c: Tangent(g12,g-5)
    c: Tangent(g8,g-5)
    c: Tangent(g4,g-5)
FEATURE [PartDesign::Chamfer] Chamfer009
  Angle = 45
  Base = -> Pad017 [Edge151,Edge154]
  BaseFeature = -> Pad017
  ChamferType = 1
  FlipDirection = false
  Refine = true
  Size = 1.5
  Size2 = 2.8
  SupportTransform = false
  Suppressed = false
  UseAllEdges = false
FEATURE [PartDesign::Pocket] Pocket009
  BaseFeature = -> Chamfer009
  Direction = (0,1,-2e-16)
  Length = 1
  Length2 = 5
  Profile = -> Sketch125
  ReferenceAxis = -> Sketch125 [N_Axis]
  Refine = true
  Suppressed = false
  Type = 0
FEATURE [PartDesign::Pad] Pad014
  BaseFeature = -> Pocket009
  Direction = (0,-1,2e-16)
  Length = 0.8
  Length2 = 10
  Profile = -> Sketch120
  ReferenceAxis = -> Sketch120 [N_Axis]
  Refine = true
  Suppressed = false
  Type = 0
FEATURE [Sketcher::SketchObject] Sketch124
  ArcFitTolerance = 1e-06
  AttachmentSupport = -> [Pad014]
  ExternalGeometry = -> [Binder001]
  FullyConstrained = true
  MakeInternals = false
  MapMode = 5
  Placement = pos=(0,-2.8,6e-16) rot=(1,0,0;1.5708rad)
  sketch-geometry (4):
    g0: LineSegment StartX=-129 StartY=39.2 StartZ=0 EndX=-131.599 EndY=31.2 EndZ=0
    g1: LineSegment StartX=-118 StartY=39.2 StartZ=0 EndX=-120.599 EndY=31.2 EndZ=0
    g2: LineSegment StartX=-129 StartY=39.2 StartZ=0 EndX=-118 EndY=39.2 EndZ=0
    g3: LineSegment StartX=-120.599 StartY=31.2 StartZ=0 EndX=-131.599 EndY=31.2 EndZ=0
  constraints (12):
    c: PointOnObject(g0,g-3)
    c: PointOnObject(g1,g-3)
    c: Parallel(g-4,g0)
    c: Parallel(g-4,g1)
    c: Coincident(g2,g0)
    c: Coincident(g2,g1)
    c: DistanceX(g2,g2) = 11
    c: DistanceY(g1,g1) = 8
    c: Coincident(g3,g1)
    c: Horizontal(g3)
    c: Coincident(g3,g0)
    c: DistanceX(g1,g-3) = 118
FEATURE [PartDesign::Pad] Pad018
  BaseFeature = -> Pad014
  Direction = (0,-1,2e-16)
  Length = 1.2
  Length2 = 10
  Profile = -> Sketch124
  ReferenceAxis = -> Sketch124 [N_Axis]
  Refine = true
  Suppressed = false
  Type = 0
FEATURE [Sketcher::SketchObject] Sketch126
  ArcFitTolerance = 1e-06
  AttachmentSupport = -> [Pad018]
  ExternalGeometry = -> [Pad018]
  FullyConstrained = true
  MakeInternals = false
  MapMode = 5
  Placement = pos=(0,-4,0) rot=(1,0,0;1.5708rad)
  sketch-geometry (8):
    g0: LineSegment StartX=-129.877 StartY=36.5 StartZ=0 EndX=-130.137 EndY=35.7 EndZ=0
    g1: LineSegment StartX=-130.69 StartY=34 StartZ=0 EndX=-130.95 EndY=33.2 EndZ=0
    g2: LineSegment StartX=-129.877 StartY=36.5 StartZ=0 EndX=-118.877 EndY=36.5 EndZ=0
    g3: LineSegment StartX=-130.137 StartY=35.7 StartZ=0 EndX=-119.137 EndY=35.7 EndZ=0
    g4: LineSegment StartX=-130.69 StartY=34 StartZ=0 EndX=-119.69 EndY=34 EndZ=0
    g5: LineSegment StartX=-130.95 StartY=33.2 StartZ=0 EndX=-119.95 EndY=33.2 EndZ=0
    g6: LineSegment StartX=-118.877 StartY=36.5 StartZ=0 EndX=-119.137 EndY=35.7 EndZ=0
    g7: LineSegment StartX=-119.69 StartY=34 StartZ=0 EndX=-119.95 EndY=33.2 EndZ=0
  constraints (20):
    c: Coincident(g2,g0)
    c: Horizontal(g2)
    c: Coincident(g3,g0)
    c: Horizontal(g3)
    c: Coincident(g4,g1)
    c: Horizontal(g4)
    c: Coincident(g5,g1)
    c: Horizontal(g5)
    c: Coincident(g6,g2)
    c: Coincident(g6,g3)
    c: Coincident(g7,g4)
    c: Coincident(g7,g5)
    c: Tangent(g0,g-4)
    c: Tangent(g6,g-5)
    c: Tangent(g1,g-4)
    c: Tangent(g7,g-5)
    c: DistanceY(g3,g2) = 0.8
    c: DistanceY(g5,g4) = 0.8
    c: DistanceY(g-6,g1) = 2
    c: DistanceY(g-6,g0) = 4.5
FEATURE [PartDesign::Chamfer] Chamfer008
  Angle = 45
  Base = -> Pad018 [Edge257]
  BaseFeature = -> Pad018
  ChamferType = 1
  FlipDirection = false
  Refine = true
  Size = 1
  Size2 = 6
  SupportTransform = false
  Suppressed = false
  UseAllEdges = false
FEATURE [PartDesign::Pocket] Pocket010
  BaseFeature = -> Chamfer008
  Direction = (0,1,-2e-16)
  Length = 1
  Length2 = 5
  Profile = -> Sketch126
  ReferenceAxis = -> Sketch126 [N_Axis]
  Refine = true
  Suppressed = false
  Type = 0
FEATURE [PartDesign::Pad] Pad015
  BaseFeature = -> Pocket010
  Direction = (0,-1,2e-16)
  Length = 2
  Length2 = 10
  Profile = -> Sketch121
  ReferenceAxis = -> Sketch121 [N_Axis]
  Refine = true
  Suppressed = false
  Type = 0
FEATURE [PartDesign::Pad] Pad016
  BaseFeature = -> Pad015
  Direction = (0,-1,2e-16)
  Length = 1.6
  Length2 = 10
  Profile = -> Sketch122
  ReferenceAxis = -> Sketch122 [N_Axis]
  Refine = true
  Suppressed = false
  Type = 0
FEATURE [Sketcher::SketchObject] Sketch129
  ArcFitTolerance = 1e-06
  AttachmentSupport = -> [Pad016]
  ExternalGeometry = -> [Binder001]
  FullyConstrained = true
  MakeInternals = false
  MapMode = 5
  Placement = pos=(0,-3.6,0) rot=(1,0,0;1.5708rad)
  sketch-geometry (12):
    g0: LineSegment [constr] StartX=-192.176 StartY=-3.18451 StartZ=0 EndX=-181.223 EndY=20.303 EndZ=0
    g1: LineSegment [constr] StartX=-202.765 StartY=20.303 StartZ=0 EndX=-181.223 EndY=20.303 EndZ=0
    g2: LineSegment StartX=-202.765 StartY=20.303 StartZ=0 EndX=-181.223 EndY=20.303 EndZ=0
    g3: LineSegment StartX=-192.176 StartY=-3.18451 StartZ=0 EndX=-196.804 EndY=-13.1107 EndZ=0
    g4: ArcOfCircle CenterX=-207.583 CenterY=4 CenterZ=0 NormalX=0 NormalY=0 NormalZ=1 AngleXU=0 Radius=17 StartAngle=5.84685 EndAngle=7.56663
    g5: ArcOfEllipse CenterX=-181.223 CenterY=8.55923 CenterZ=0 NormalX=0 NormalY=0 NormalZ=1 MajorRadius=23.4779 MinorRadius=11.7437 AngleXU=2e-16 StartAngle=4.71239 EndAngle=7.85398
    g6: LineSegment [constr] StartX=-157.745 StartY=8.55923 StartZ=0 EndX=-204.701 EndY=8.55923 EndZ=0
    g7: LineSegment [constr] StartX=-181.223 StartY=20.303 StartZ=0 EndX=-181.223 EndY=-3.18451 EndZ=0
    g8: GeomPoint [constr] X=-160.894 Y=8.55923 Z=0
    g9: GeomPoint [constr] X=-201.553 Y=8.55923 Z=0
    g10: ArcOfCircle CenterX=-181.223 CenterY=-20.3763 CenterZ=0 NormalX=0 NormalY=0 NormalZ=1 AngleXU=0 Radius=17.1918 StartAngle=1.57079 EndAngle=2.70526
    g11: GeomPoint [constr] X=-181.223 Y=-3.18451 Z=0
  constraints (23):
    c: Coincident(g0,g-5)
    c: Coincident(g1,g-6)
    c: Horizontal(g1)
    c: Coincident(g1,g0)
    c: Parallel(g0,g-4)
    c: Coincident(g2,g1)
    c: Coincident(g2,g0)
    c: Coincident(g3,g0)
    c: Equal(g4,g-5)
    c: Coincident(g4,g1)
    c: Coincident(g4,g0)
    c: InternalAlignment(g6-g9 -> g5) x4
    c: Vertical(g5,g0)
    c: Horizontal(g6)
    c: Coincident(g5,g0)
    c: DistanceX(g6,g-3) = 10.1
    c: Tangent(g10,g3) = -1.5708
    c: PointOnObject(g11,g10)
    c: Tangent(g5,g10,g11) = 1.5708
    c: Coincident(g10,g5)
    c: Coincident(g11,g7)
    c: Parallel(g3,g-4)
    c: Horizontal(g5,g0)
FEATURE [Sketcher::SketchObject] Sketch130
  ArcFitTolerance = 1e-06
  AttachmentOffset = pos=(0,0,-1.6) rot=(0,0,1;0rad)
  AttachmentSupport = -> [Pad016]
  ExternalGeometry = -> [Binder001]
  FullyConstrained = true
  MakeInternals = false
  MapMode = 5
  Placement = pos=(0,-2,-4e-16) rot=(1,0,0;1.5708rad)
  sketch-geometry (12):
    g0: LineSegment [constr] StartX=-192.176 StartY=-3.18451 StartZ=0 EndX=-181.223 EndY=20.303 EndZ=0
    g1: LineSegment [constr] StartX=-202.765 StartY=20.303 StartZ=0 EndX=-181.223 EndY=20.303 EndZ=0
    g2: LineSegment StartX=-202.765 StartY=20.303 StartZ=0 EndX=-181.223 EndY=20.303 EndZ=0
    g3: LineSegment StartX=-192.176 StartY=-3.18451 StartZ=0 EndX=-193.827 EndY=-6.72678 EndZ=0
    g4: ArcOfCircle CenterX=-207.583 CenterY=4 CenterZ=0 NormalX=0 NormalY=0 NormalZ=1 AngleXU=0 Radius=17 StartAngle=5.84685 EndAngle=7.56663
    g5: ArcOfEllipse CenterX=-181.223 CenterY=10.803 CenterZ=0 NormalX=0 NormalY=0 NormalZ=1 MajorRadius=14.4779 MinorRadius=9.5 AngleXU=0 StartAngle=4.71239 EndAngle=7.85398
    g6: LineSegment [constr] StartX=-166.745 StartY=10.803 StartZ=0 EndX=-195.701 EndY=10.803 EndZ=0
    g7: LineSegment [constr] StartX=-181.223 StartY=20.303 StartZ=0 EndX=-181.223 EndY=1.30297 EndZ=0
    g8: GeomPoint [constr] X=-170.298 Y=10.803 Z=0
    g9: GeomPoint [constr] X=-192.148 Y=10.803 Z=0
    g10: ArcOfCircle CenterX=-181.223 CenterY=-12.6042 CenterZ=0 NormalX=0 NormalY=0 NormalZ=1 AngleXU=0 Radius=13.9072 StartAngle=1.5708 EndAngle=2.70526
    g11: GeomPoint [constr] X=-181.223 Y=1.30297 Z=0
  constraints (23):
    c: Coincident(g0,g-5)
    c: Coincident(g1,g-6)
    c: Horizontal(g1)
    c: Coincident(g1,g0)
    c: Parallel(g0,g-4)
    c: Coincident(g2,g1)
    c: Coincident(g2,g0)
    c: Coincident(g3,g0)
    c: Equal(g4,g-5)
    c: Coincident(g4,g1)
    c: Coincident(g4,g0)
    c: InternalAlignment(g6-g9 -> g5) x4
    c: Vertical(g5,g0)
    c: Horizontal(g6)
    c: Coincident(g5,g0)
    c: DistanceX(g6,g-3) = 19.1
    c: Tangent(g10,g3) = -1.5708
    c: PointOnObject(g11,g10)
    c: Tangent(g5,g10,g11) = 1.5708
    c: Coincident(g10,g5)
    c: Coincident(g11,g7)
    c: Parallel(g3,g-4)
    c: DistanceY(g5,g0) = 19
FEATURE [Part::Part2DObjectPython] Clone2D001  label="Sketch130 (2D)"  # Draft 2D object (typed FeaturePython)
  Fuse = false
  Objects = -> [Sketch130]
  Placement = pos=(0,-2,-4e-16) rot=(1,0,0;1.5708rad)
  Scale = (1,1,1)
FEATURE [Sketcher::SketchObject] Sketch131
  ArcFitTolerance = 1e-06
  AttachmentOffset = pos=(0,0,-3.5) rot=(0,0,1;0rad)
  AttachmentSupport = -> [Pad016]
  ExternalGeometry = -> [Binder001]
  FullyConstrained = true
  MakeInternals = false
  MapMode = 5
  Placement = pos=(0,-0.1,-8e-16) rot=(1,0,0;1.5708rad)
  sketch-geometry (1):
    g0: GeomPoint X=-197.47 Y=8.55923 Z=0
  constraints (1):
    c: Symmetric(g-6,g-4,g0)
FEATURE [Sketcher::SketchObject] Sketch132
  ArcFitTolerance = 1e-06
  AttachmentSupport = -> [Pad016]
  ExternalGeometry = -> [Binder001]
  FullyConstrained = true
  MakeInternals = false
  MapMode = 5
  Placement = pos=(0,-3.6,0) rot=(1,0,0;1.5708rad)
  sketch-geometry (3):
    g0: LineSegment [constr] StartX=-215.42 StartY=-53.0314 StartZ=0 EndX=-167.782 EndY=-53.0314 EndZ=0
    g1: Circle CenterX=-191.282 CenterY=-53.0314 CenterZ=0 NormalX=0 NormalY=0 NormalZ=1 AngleXU=0 Radius=11.5
    g2: Circle CenterX=-191.282 CenterY=-53.0314 CenterZ=0 NormalX=0 NormalY=0 NormalZ=1 AngleXU=0 Radius=10.7
  constraints (8):
    c: Coincident(g0,g-3)
    c: PointOnObject(g0,g-4)
    c: Horizontal(g0)
    c: Diameter(g1) = 23
    c: PointOnObject(g1,g0)
    c: DistanceX(g1,g0) = 23.5
    c: Diameter(g2) = 21.4
    c: Coincident(g2,g1)
FEATURE [Part::Part2DObjectPython] ShapeString  # Draft 2D object (typed FeaturePython)
  FontFile = <path>
  Fuse = false
  Justification = 6
  JustificationReference = 0
  KeepLeftMargin = false
  MakeFace = true
  ObliqueAngle = 0
  Placement = pos=(-199,-3.6,-57.5) rot=(1,0,0;1.5708rad)
  ScaleToSize = true
  Size = 10
  String = AS
  Tracking = 0
FEATURE [Sketcher::SketchObject] Sketch133
  ArcFitTolerance = 1e-06
  AttachmentSupport = -> [Binder]
  ExternalGeometry = -> [Binder]
  FullyConstrained = true
  MakeInternals = false
  MapMode = 5
  Placement = pos=(0,9e-16,0) rot=(0,0.707107,0.707107;3.14159rad)
  sketch-geometry (30):
    g0: LineSegment StartX=0 StartY=39.2 StartZ=0 EndX=0 EndY=3.2 EndZ=0
    g1: LineSegment StartX=0 StartY=3.2 StartZ=0 EndX=82.8 EndY=3.2 EndZ=0
    g2: LineSegment StartX=82.8 StartY=3.2 StartZ=0 EndX=82.8 EndY=6.2 EndZ=0
    g3: LineSegment StartX=82.8 StartY=6.2 StartZ=0 EndX=91.752 EndY=6.2 EndZ=0
    g4: LineSegment StartX=0 StartY=39.2 StartZ=0 EndX=195.887 EndY=39.2 EndZ=0
    g5: LineSegment StartX=195.887 StartY=39.2 StartZ=0 EndX=202.765 EndY=20.303 EndZ=0
    g6: LineSegment StartX=192.333 StartY=24.9893 StartZ=0 EndX=196.467 EndY=26.4942 EndZ=0
    g7: LineSegment StartX=196.467 StartY=26.4942 StartZ=0 EndX=194.073 EndY=33.0721 EndZ=0
    g8: LineSegment StartX=194.073 StartY=33.0721 StartZ=0 EndX=189.939 EndY=31.5672 EndZ=0
    g9: LineSegment StartX=189.939 StartY=31.5672 StartZ=0 EndX=192.333 EndY=24.9893 EndZ=0
    g10: ArcOfCircle CenterX=107.6 CenterY=4 CenterZ=0 NormalX=0 NormalY=0 NormalZ=1 AngleXU=0 Radius=16 StartAngle=1.5708 EndAngle=3.00366
    g11: LineSegment StartX=107.6 StartY=20 StartZ=0 EndX=132.428 EndY=20 EndZ=0
    g12: ArcOfCircle [constr] CenterX=132.428 CenterY=4 CenterZ=0 NormalX=0 NormalY=0 NormalZ=1 AngleXU=0 Radius=16 StartAngle=0.314159 EndAngle=1.5708
    g13: LineSegment StartX=147.645 StartY=8.94427 StartZ=0 EndX=176.685 EndY=-80.4316 EndZ=0
    g14: LineSegment StartX=176.685 StartY=-80.4316 StartZ=0 EndX=215.932 EndY=-80.4316 EndZ=0
    g15: ArcOfCircle CenterX=207.583 CenterY=4 CenterZ=0 NormalX=0 NormalY=0 NormalZ=1 AngleXU=0 Radius=17 StartAngle=1.85815 EndAngle=3.57792
    g16: ArcOfCircle CenterX=184.801 CenterY=-67.3089 CenterZ=0 NormalX=0 NormalY=0 NormalZ=1 AngleXU=0 Radius=33.7833 StartAngle=5.88425 EndAngle=6.71952
    g17: LineSegment StartX=192.176 StartY=-3.18451 StartZ=0 EndX=215.42 EndY=-53.0314 EndZ=0
    g18: Circle CenterX=5.6 CenterY=34.8 CenterZ=0 NormalX=0 NormalY=0 NormalZ=1 AngleXU=0 Radius=1.8
    g19: Circle CenterX=5.6 CenterY=7.6 CenterZ=0 NormalX=0 NormalY=0 NormalZ=1 AngleXU=0 Radius=1.8
    g20: Circle CenterX=78.51 CenterY=34.8 CenterZ=0 NormalX=0 NormalY=0 NormalZ=1 AngleXU=0 Radius=1.8
    g21: Circle CenterX=78.51 CenterY=7.6 CenterZ=0 NormalX=0 NormalY=0 NormalZ=1 AngleXU=0 Radius=1.8
    g22: Circle CenterX=184.08 CenterY=34.8 CenterZ=0 NormalX=0 NormalY=0 NormalZ=1 AngleXU=0 Radius=1.8
    g23: Circle CenterX=179.305 CenterY=-76.8316 CenterZ=0 NormalX=0 NormalY=0 NormalZ=1 AngleXU=0 Radius=1.8
    g24: Circle CenterX=213.443 CenterY=-76.8316 CenterZ=0 NormalX=0 NormalY=0 NormalZ=1 AngleXU=0 Radius=1.8
    g25: Circle CenterX=19 CenterY=21.2 CenterZ=0 NormalX=0 NormalY=0 NormalZ=1 AngleXU=0 Radius=6.3
    g26: Circle CenterX=42 CenterY=21.2 CenterZ=0 NormalX=0 NormalY=0 NormalZ=1 AngleXU=0 Radius=6.3
    g27: Circle CenterX=65 CenterY=21.2 CenterZ=0 NormalX=0 NormalY=0 NormalZ=1 AngleXU=0 Radius=6.3
    g28: LineSegment StartX=132.428 StartY=20 StartZ=0 EndX=144.053 EndY=20 EndZ=0
    g29: LineSegment StartX=147.645 StartY=8.94427 StartZ=0 EndX=144.053 EndY=20 EndZ=0
  constraints (65):
    c: Coincident(g0,g-4)
    c: Coincident(g0,g-5)
    c: Coincident(g1,g0)
    c: Coincident(g1,g-6)
    c: Coincident(g2,g1)
    c: Coincident(g2,g-7)
    c: Coincident(g3,g2)
    c: Coincident(g3,g-8)
    c: Coincident(g4,g0)
    c: Coincident(g4,g-16)
    c: Coincident(g5,g4)
    c: Coincident(g5,g-16)
    c: Coincident(g6,g-20)
    c: Coincident(g6,g-21)
    c: Coincident(g7,g6)
    c: Coincident(g7,g-23)
    c: Coincident(g8,g7)
    c: Coincident(g8,g-22)
    c: Coincident(g9,g8)
    c: Coincident(g9,g6)
    c: Equal(g10,g-8)
    c: Coincident(g10,g3)
    c: Coincident(g10,g-9)
    c: Coincident(g11,g10)
    c: Coincident(g11,g-10)
    c: Equal(g12,g-10)
    c: Coincident(g12,g11)
    c: Coincident(g12,g-11)
    c: Coincident(g13,g12)
    c: Coincident(g13,g-12)
    c: Coincident(g14,g13)
    c: Coincident(g14,g-13)
    c: Equal(g15,g-15)
    c: Coincident(g15,g5)
    c: Coincident(g15,g-15)
    c: Equal(g16,g-13)
    c: Coincident(g16,g14)
    c: Coincident(g16,g-14)
    c: Coincident(g17,g15)
    c: Coincident(g17,g16)
    c: Equal(g18,g-28)
    c: Equal(g19,g-29)
    c: Equal(g20,g-26)
    c: Equal(g21,g-27)
    c: Equal(g22,g-17)
    c: Equal(g24,g-25)
    c: Equal(g23,g-24)
    c: Coincident(g23,g-24)
    c: Coincident(g24,g-25)
    c: Coincident(g22,g-17)
    c: Coincident(g20,g-26)
    c: Coincident(g21,g-27)
    c: Coincident(g18,g-28)
    c: Coincident(g19,g-29)
    c: Equal(g25,g-30)
    c: Equal(g26,g-31)
    c: Equal(g27,g-32)
    c: Coincident(g25,g-30)
    c: Coincident(g26,g-31)
    c: Coincident(g27,g-32)
    c: Parallel(g28,g11)
    c: Parallel(g29,g13)
    c: Coincident(g28,g11)
    c: Coincident(g29,g12)
    c: Coincident(g29,g28)
FEATURE [PartDesign::Pad] Pad019
  Direction = (0,1,-2e-16)
  Length = 2
  Length2 = 10
  Profile = -> Sketch133
  ReferenceAxis = -> Sketch133 [N_Axis]
  Refine = true
  Suppressed = false
  Type = 0
FEATURE [Sketcher::SketchObject] Sketch091  label="Sketch091 - forma anteriore"
  ArcFitTolerance = 1e-06
  AttachmentSupport = -> [Pad019]
  ExternalGeometry = -> [Binder]
  FullyConstrained = true
  MakeInternals = false
  MapMode = 5
  Placement = pos=(0,2,0) rot=(0,0.707107,0.707107;3.14159rad)
  sketch-geometry (12):
    g0: Circle CenterX=5.6 CenterY=34.8 CenterZ=0 NormalX=0 NormalY=0 NormalZ=1 AngleXU=0 Radius=1.8
    g1: Circle CenterX=5.6 CenterY=7.6 CenterZ=0 NormalX=0 NormalY=0 NormalZ=1 AngleXU=0 Radius=1.8
    g2: Circle CenterX=78.51 CenterY=34.8 CenterZ=0 NormalX=0 NormalY=0 NormalZ=1 AngleXU=0 Radius=1.8
    g3: Circle CenterX=78.51 CenterY=7.6 CenterZ=0 NormalX=0 NormalY=0 NormalZ=1 AngleXU=0 Radius=1.8
    g4: LineSegment StartX=0 StartY=39.2 StartZ=0 EndX=0 EndY=3.2 EndZ=0
    g5: LineSegment StartX=0 StartY=3.2 StartZ=0 EndX=82.8 EndY=3.2 EndZ=0
    g6: LineSegment StartX=82.8 StartY=3.2 StartZ=0 EndX=82.8 EndY=39.2 EndZ=0
    g7: LineSegment StartX=82.8 StartY=39.2 StartZ=0 EndX=0 EndY=39.2 EndZ=0
    g8: ArcOfCircle CenterX=19 CenterY=21.2 CenterZ=0 NormalX=0 NormalY=0 NormalZ=1 AngleXU=0 Radius=10 StartAngle=1.5708 EndAngle=4.71239
    g9: ArcOfCircle CenterX=65 CenterY=21.2 CenterZ=0 NormalX=0 NormalY=0 NormalZ=1 AngleXU=0 Radius=10 StartAngle=4.71239 EndAngle=7.85398
    g10: LineSegment StartX=19 StartY=31.2 StartZ=0 EndX=65 EndY=31.2 EndZ=0
    g11: LineSegment StartX=19 StartY=11.2 StartZ=0 EndX=65 EndY=11.2 EndZ=0
  constraints (25):
    c: Equal(g2,g-7)
    c: Equal(g3,g-8)
    c: Equal(g1,g-13)
    c: Equal(g0,g-12)
    c: Coincident(g0,g-12)
    c: Coincident(g1,g-13)
    c: Coincident(g3,g-8)
    c: Coincident(g2,g-7)
    c: Coincident(g4,g-4)
    c: Coincident(g4,g-5)
    c: Coincident(g5,g4)
    c: Coincident(g5,g-6)
    c: Coincident(g6,g5)
    c: PointOnObject(g6,g-3)
    c: Vertical(g6)
    c: Coincident(g7,g6)
    c: Coincident(g7,g4)
    c: Tangent(g8,g10) = 1.5708
    c: Tangent(g8,g11) = -1.5708
    c: Tangent(g9,g10) = 1.5708
    c: Tangent(g9,g11) = -1.5708
    c: Equal(g8,g9)
    c: Radius(g8) = 10
    c: Coincident(g8,g-11)
    c: Coincident(g9,g-9)
FEATURE [Sketcher::SketchObject] Sketch093  label="Sketch093 - scavi interni pulsanti"
  ArcFitTolerance = 1e-06
  AttachmentSupport = -> [Pad019]
  ExternalGeometry = -> [Binder]
  FullyConstrained = true
  MakeInternals = false
  MapMode = 5
  Placement = pos=(0,1.8e-15,0) rot=(1,0,0;1.5708rad)
  sketch-geometry (3):
    g0: Circle CenterX=-65 CenterY=21.2 CenterZ=0 NormalX=0 NormalY=0 NormalZ=1 AngleXU=0 Radius=7.3
    g1: Circle CenterX=-42 CenterY=21.2 CenterZ=0 NormalX=0 NormalY=0 NormalZ=1 AngleXU=0 Radius=7.3
    g2: Circle CenterX=-19 CenterY=21.2 CenterZ=0 NormalX=0 NormalY=0 NormalZ=1 AngleXU=0 Radius=7.3
  constraints (6):
    c: Coincident(g0,g-3)
    c: Coincident(g1,g-4)
    c: Coincident(g2,g-5)
    c: Diameter(g0) = 14.6
    c: Diameter(g1) = 14.6
    c: Diameter(g2) = 14.6
FEATURE [Sketcher::SketchObject] Sketch094  label="Sketch094 - forma centrale"
  ArcFitTolerance = 1e-06
  AttachmentSupport = -> [Pad019]
  ExternalGeometry = -> [Binder]
  FullyConstrained = true
  MakeInternals = false
  MapMode = 5
  Placement = pos=(0,2,0) rot=(0,0.707107,0.707107;3.14159rad)
  sketch-geometry (4):
    g0: LineSegment StartX=137.815 StartY=39.2 StartZ=0 EndX=142.655 EndY=24.303 EndZ=0
    g1: LineSegment StartX=110.815 StartY=24.303 StartZ=0 EndX=142.655 EndY=24.303 EndZ=0
    g2: LineSegment StartX=137.815 StartY=39.2 StartZ=0 EndX=110.815 EndY=39.2 EndZ=0
    g3: ArcOfCircle CenterX=92.2534 CenterY=31.7515 CenterZ=0 NormalX=0 NormalY=0 NormalZ=1 AngleXU=0 Radius=20 StartAngle=5.90156 EndAngle=6.66481
  constraints (12):
    c: PointOnObject(g0,g-3)
    c: Tangent(g0,g-5)
    c: Horizontal(g1)
    c: Coincident(g1,g0)
    c: Coincident(g2,g0)
    c: PointOnObject(g2,g-3)
    c: DistanceX(g2,g2) = 27
    c: Vertical(g1,g2)
    c: Coincident(g3,g2)
    c: Radius(g3) = 20
    c: Coincident(g3,g1)
    c: DistanceY(g-6,g0) = 4
FEATURE [Sketcher::SketchObject] Sketch095  label="Sketch095 - forma posteriore"
  ArcFitTolerance = 1e-06
  AttachmentSupport = -> [Pad019]
  ExternalGeometry = -> [Binder]
  FullyConstrained = true
  MakeInternals = false
  MapMode = 5
  Placement = pos=(0,2,0) rot=(0,0.707107,0.707107;3.14159rad)
  sketch-geometry (15):
    g0: LineSegment StartX=137.815 StartY=39.2 StartZ=0 EndX=143.955 EndY=20.303 EndZ=0
    g1: LineSegment StartX=143.955 StartY=20.303 StartZ=0 EndX=190.141 EndY=20.303 EndZ=0
    g2: ArcOfCircle CenterX=184.08 CenterY=34.8 CenterZ=0 NormalX=0 NormalY=0 NormalZ=1 AngleXU=0 Radius=3.5 StartAngle=3.49066 EndAngle=4.71239
    g3: LineSegment StartX=180.791 StartY=33.6029 StartZ=0 EndX=178.754 EndY=39.2 EndZ=0
    g4: LineSegment StartX=184.08 StartY=31.3 StartZ=0 EndX=186.139 EndY=31.3 EndZ=0
    g5: LineSegment StartX=190.141 StartY=20.303 StartZ=0 EndX=186.139 EndY=31.3 EndZ=0
    g6: LineSegment StartX=137.815 StartY=39.2 StartZ=0 EndX=156.815 EndY=39.2 EndZ=0
    g7: LineSegment StartX=178.754 StartY=39.2 StartZ=0 EndX=168.815 EndY=39.2 EndZ=0
    g8: LineSegment StartX=156.815 StartY=31.2 StartZ=0 EndX=168.815 EndY=31.2 EndZ=0
    g9: ArcOfCircle CenterX=176.411 CenterY=35.2 CenterZ=0 NormalX=0 NormalY=0 NormalZ=1 AngleXU=0 Radius=20 StartAngle=2.94023 EndAngle=3.34295
    g10: ArcOfCircle CenterX=188.411 CenterY=35.2 CenterZ=0 NormalX=0 NormalY=0 NormalZ=1 AngleXU=0 Radius=20 StartAngle=2.94023 EndAngle=3.34295
    g11: LineSegment StartX=157.815 StartY=39.2 StartZ=0 EndX=167.815 EndY=39.2 EndZ=0
    g12: LineSegment StartX=157.436 StartY=36.2 StartZ=0 EndX=167.436 EndY=36.2 EndZ=0
    g13: ArcOfCircle CenterX=177.411 CenterY=35.2 CenterZ=0 NormalX=0 NormalY=0 NormalZ=1 AngleXU=0 Radius=20 StartAngle=2.94023 EndAngle=3.09157
    g14: ArcOfCircle CenterX=187.411 CenterY=35.2 CenterZ=0 NormalX=0 NormalY=0 NormalZ=1 AngleXU=0 Radius=20 StartAngle=2.94023 EndAngle=3.09157
  constraints (46):
    c: PointOnObject(g0,g-3)
    c: Tangent(g0,g-6)
    c: Coincident(g1,g0)
    c: Horizontal(g1)
    c: Radius(g2) = 3.5
    c: Coincident(g2,g-5)
    c: PointOnObject(g3,g-3)
    c: Parallel(g3,g-4)
    c: Tangent(g3,g2) = 1.5708
    c: Horizontal(g4)
    c: Tangent(g4,g2) = -1.5708
    c: Coincident(g5,g1)
    c: Parallel(g5,g-4)
    c: Coincident(g5,g4)
    c: DistanceX(g4,g-8) = 3.8
    c: Coincident(g6,g0)
    c: PointOnObject(g6,g-3)
    c: Coincident(g7,g3)
    c: PointOnObject(g7,g-3)
    c: Horizontal(g8)
    c: DistanceX(g6,g7) = 12
    c: Vertical(g8,g6)
    c: Vertical(g7,g8)
    c: DistanceY(g8,g6) = 8
    c: Coincident(g9,g8)
    c: Coincident(g9,g6)
    c: Coincident(g10,g7)
    c: Coincident(g10,g8)
    c: Radius(g9) = 20
    c: Radius(g10) = 20
    c: PointOnObject(g11,g-3)
    c: PointOnObject(g11,g-3)
    c: DistanceX(g11,g11) = 10
    c: DistanceX(g6,g11) = 1
    c: Horizontal(g12)
    c: Equal(g12,g11)
    c: DistanceY(g12,g11) = 3
    c: Coincident(g13,g11)
    c: Coincident(g13,g12)
    c: Radius(g13) = 20
    c: Coincident(g14,g11)
    c: Coincident(g14,g12)
    c: Radius(g14) = 20
    c: DistanceX(g0,g6) = 19
    c: Horizontal(g9,g13)
    c: Horizontal(g0,g-4)
FEATURE [Sketcher::SketchObject] Sketch096  label="Sketch096 - forma impugnatura"
  ArcFitTolerance = 1e-06
  AttachmentSupport = -> [Pad019]
  ExternalGeometry = -> [Binder]
  FullyConstrained = true
  MakeInternals = false
  MapMode = 5
  Placement = pos=(0,2,0) rot=(0,0.707107,0.707107;3.14159rad)
  sketch-geometry (8):
    g0: LineSegment StartX=176.685 StartY=-80.4316 StartZ=0 EndX=143.955 EndY=20.303 EndZ=0
    g1: LineSegment StartX=176.685 StartY=-80.4316 StartZ=0 EndX=215.932 EndY=-80.4316 EndZ=0
    g2: Circle CenterX=179.305 CenterY=-76.8316 CenterZ=0 NormalX=0 NormalY=0 NormalZ=1 AngleXU=0 Radius=3
    g3: Circle CenterX=213.443 CenterY=-76.8316 CenterZ=0 NormalX=0 NormalY=0 NormalZ=1 AngleXU=0 Radius=3
    g4: LineSegment StartX=143.955 StartY=20.303 StartZ=0 EndX=202.765 EndY=20.303 EndZ=0
    g5: LineSegment StartX=215.42 StartY=-53.0314 StartZ=0 EndX=192.176 EndY=-3.18451 EndZ=0
    g6: ArcOfCircle CenterX=184.801 CenterY=-67.3089 CenterZ=0 NormalX=0 NormalY=0 NormalZ=1 AngleXU=0 Radius=33.7833 StartAngle=5.88425 EndAngle=6.71952
    g7: ArcOfCircle CenterX=207.583 CenterY=4 CenterZ=0 NormalX=0 NormalY=0 NormalZ=1 AngleXU=0 Radius=17 StartAngle=1.85815 EndAngle=3.57792
  constraints (19):
    c: Coincident(g0,g-4)
    c: PointOnObject(g0,g-3)
    c: Horizontal(g0,g-7)
    c: Coincident(g1,g0)
    c: Coincident(g1,g-5)
    c: Diameter(g2) = 6
    c: Diameter(g3) = 6
    c: Coincident(g2,g-9)
    c: Coincident(g3,g-10)
    c: Coincident(g4,g0)
    c: Coincident(g5,g-6)
    c: Coincident(g6,g1)
    c: Coincident(g6,g5)
    c: Equal(g-5,g6)
    c: Coincident(g5,g-7)
    c: Coincident(g4,g-7)
    c: Tangent(g7,g-7)
    c: Coincident(g7,g4)
    c: Coincident(g7,g5)
FEATURE [Sketcher::SketchObject] Sketch097
  ArcFitTolerance = 1e-06
  AttachmentSupport = -> [Pad019]
  ExternalGeometry = -> [Binder]
  FullyConstrained = true
  MakeInternals = false
  MapMode = 5
  Placement = pos=(0,2,0) rot=(0,0.707107,0.707107;3.14159rad)
  sketch-geometry (4):
    g0: LineSegment StartX=90 StartY=36.8 StartZ=0 EndX=108 EndY=36.8 EndZ=0
    g1: LineSegment StartX=108 StartY=36.8 StartZ=0 EndX=108 EndY=26.8 EndZ=0
    g2: LineSegment StartX=108 StartY=26.8 StartZ=0 EndX=90 EndY=26.8 EndZ=0
    g3: ArcOfCircle CenterX=94 CenterY=31.8 CenterZ=0 NormalX=0 NormalY=0 NormalZ=1 AngleXU=0 Radius=6.40312 StartAngle=2.24554 EndAngle=4.03765
  constraints (13):
    c: Horizontal(g0)
    c: Coincident(g1,g0)
    c: Vertical(g1)
    c: DistanceX(g0,g0) = 18
    c: DistanceY(g1,g1) = 10
    c: Coincident(g2,g1)
    c: Horizontal(g2)
    c: Equal(g2,g0)
    c: DistanceY(g0,g-3) = 2.4
    c: Coincident(g3,g0)
    c: Coincident(g3,g2)
    c: DistanceX(g2,g3) = 4
    c: DistanceX(g-3,g0) = 90
FEATURE [PartDesign::Chamfer] Chamfer015
  Angle = 45
  Base = -> Pad019 [Edge19,Edge22,Edge79]
  BaseFeature = -> Pad019
  ChamferType = 0
  FlipDirection = false
  Refine = true
  Size = 1.9
  Size2 = 1
  SupportTransform = false
  Suppressed = false
  UseAllEdges = false
FEATURE [PartDesign::Pocket] Pocket002
  BaseFeature = -> Chamfer015
  Direction = (0,1,-2e-16)
  Length = 1.2
  Length2 = 5
  Profile = -> Sketch093
  ReferenceAxis = -> Sketch093 [N_Axis]
  Refine = true
  Suppressed = false
  Type = 0
FEATURE [PartDesign::Pad] Pad005
  BaseFeature = -> Pocket002
  Direction = (0,1,-2e-16)
  Length = 1.6
  Length2 = 10
  Profile = -> Sketch091
  ReferenceAxis = -> Sketch091 [N_Axis]
  Refine = true
  Suppressed = false
  Type = 0
FEATURE [Sketcher::SketchObject] Sketch092  label="Sketch092 - scavi per viti anteriori"
  ArcFitTolerance = 1e-06
  AttachmentSupport = -> [Pad005]
  ExternalGeometry = -> [Binder]
  FullyConstrained = true
  MakeInternals = false
  MapMode = 5
  Placement = pos=(0,3.6,0) rot=(0,0.707107,0.707107;3.14159rad)
  sketch-geometry (20):
    g0: ArcOfCircle CenterX=5.6 CenterY=7.6 CenterZ=0 NormalX=0 NormalY=0 NormalZ=1 AngleXU=0 Radius=3.5 StartAngle=0 EndAngle=1.5708
    g1: ArcOfCircle CenterX=5.6 CenterY=34.8 CenterZ=0 NormalX=0 NormalY=0 NormalZ=1 AngleXU=0 Radius=3.5 StartAngle=4.71239 EndAngle=6.28319
    g2: ArcOfCircle CenterX=78.51 CenterY=34.8 CenterZ=0 NormalX=0 NormalY=0 NormalZ=1 AngleXU=0 Radius=3.5 StartAngle=3.14159 EndAngle=4.71239
    g3: ArcOfCircle CenterX=78.51 CenterY=7.6 CenterZ=0 NormalX=0 NormalY=0 NormalZ=1 AngleXU=0 Radius=3.5 StartAngle=1.5708 EndAngle=3.14159
    g4: LineSegment StartX=0 StartY=3.2 StartZ=0 EndX=0 EndY=11.1 EndZ=0
    g5: LineSegment StartX=0 StartY=11.1 StartZ=0 EndX=5.6 EndY=11.1 EndZ=0
    g6: LineSegment StartX=0 StartY=3.2 StartZ=0 EndX=9.1 EndY=3.2 EndZ=0
    g7: LineSegment StartX=9.1 StartY=3.2 StartZ=0 EndX=9.1 EndY=7.6 EndZ=0
    g8: LineSegment StartX=0 StartY=39.2 StartZ=0 EndX=0 EndY=31.3 EndZ=0
    g9: LineSegment StartX=0 StartY=31.3 StartZ=0 EndX=5.6 EndY=31.3 EndZ=0
    g10: LineSegment StartX=0 StartY=39.2 StartZ=0 EndX=9.1 EndY=39.2 EndZ=0
    g11: LineSegment StartX=9.1 StartY=39.2 StartZ=0 EndX=9.1 EndY=34.8 EndZ=0
    g12: LineSegment StartX=82.8 StartY=39.2 StartZ=0 EndX=75.01 EndY=39.2 EndZ=0
    g13: LineSegment StartX=82.8 StartY=39.2 StartZ=0 EndX=82.8 EndY=31.3 EndZ=0
    g14: LineSegment StartX=82.8 StartY=31.3 StartZ=0 EndX=78.51 EndY=31.3 EndZ=0
    g15: LineSegment StartX=82.8 StartY=3.2 StartZ=0 EndX=75.01 EndY=3.2 EndZ=0
    g16: LineSegment StartX=75.01 StartY=3.2 StartZ=0 EndX=75.01 EndY=7.6 EndZ=0
    g17: LineSegment StartX=82.8 StartY=3.2 StartZ=0 EndX=82.8 EndY=11.1 EndZ=0
    g18: LineSegment StartX=82.8 StartY=11.1 StartZ=0 EndX=78.51 EndY=11.1 EndZ=0
    g19: LineSegment StartX=75.01 StartY=39.2 StartZ=0 EndX=75.01 EndY=34.8 EndZ=0
  constraints (48):
    c: Radius(g0) = 3.5
    c: Coincident(g0,g-10)
    c: Radius(g1) = 3.5
    c: Coincident(g1,g-9)
    c: Radius(g2) = 3.5
    c: Coincident(g2,g-8)
    c: Radius(g3) = 3.5
    c: Coincident(g3,g-7)
    c: Coincident(g4,g-5)
    c: PointOnObject(g4,g-4)
    c: Coincident(g5,g4)
    c: Horizontal(g5)
    c: Coincident(g6,g4)
    c: PointOnObject(g6,g-5)
    c: Coincident(g7,g6)
    c: Vertical(g7)
    c: Coincident(g8,g-4)
    c: PointOnObject(g8,g-4)
    c: Coincident(g9,g8)
    c: Horizontal(g9)
    c: Coincident(g10,g8)
    c: PointOnObject(g10,g-3)
    c: Coincident(g11,g10)
    c: Vertical(g11)
    c: PointOnObject(g12,g-3)
    c: PointOnObject(g12,g-3)
    c: Coincident(g13,g12)
    c: Vertical(g13)
    c: Coincident(g14,g13)
    c: Horizontal(g14)
    c: Coincident(g15,g-6)
    c: PointOnObject(g15,g-5)
    c: Coincident(g16,g15)
    c: Vertical(g16)
    c: Coincident(g17,g15)
    c: Coincident(g18,g17)
    c: Horizontal(g18)
    c: Tangent(g3,g18) = -1.5708
    c: Tangent(g16,g3) = 1.5708
    c: Coincident(g19,g12)
    c: Vertical(g19)
    c: Tangent(g2,g19) = -1.5708
    c: Tangent(g2,g14) = 1.5708
    c: Tangent(g0,g7) = -1.5708
    c: Tangent(g0,g5) = 1.5708
    c: Tangent(g9,g1) = -1.5708
    c: Tangent(g1,g11) = 1.5708
    c: Tangent(g17,g13)
FEATURE [PartDesign::Pocket] Pocket001
  BaseFeature = -> Pad005
  Direction = (0,-1,2e-16)
  Length = 1.6
  Length2 = 5
  Profile = -> Sketch092
  ReferenceAxis = -> Sketch092 [N_Axis]
  Refine = true
  Suppressed = false
  Type = 0
FEATURE [PartDesign::Pad] Pad006
  BaseFeature = -> Pocket001
  Direction = (0,1,-2e-16)
  Length = 0.8
  Length2 = 10
  Profile = -> Sketch094
  ReferenceAxis = -> Sketch094 [N_Axis]
  Refine = true
  Suppressed = false
  Type = 0
FEATURE [PartDesign::Pad] Pad007
  BaseFeature = -> Pad006
  Direction = (0,1,-2e-16)
  Length = 2
  Length2 = 10
  Profile = -> Sketch095
  ReferenceAxis = -> Sketch095 [N_Axis]
  Refine = true
  Suppressed = false
  Type = 0
FEATURE [PartDesign::Pad] Pad008  label="Pad008 - forma impugnatura"
  BaseFeature = -> Pad007
  Direction = (0,1,-2e-16)
  Length = 1.6
  Length2 = 10
  Profile = -> Sketch096
  ReferenceAxis = -> Sketch096 [N_Axis]
  Refine = true
  Suppressed = false
  Type = 0
FEATURE [PartDesign::Pad] Pad009
  BaseFeature = -> Pad008
  Direction = (0,1,-2e-16)
  Length = 1.6
  Length2 = 10
  Profile = -> Sketch097
  ReferenceAxis = -> Sketch097 [N_Axis]
  Refine = true
  Suppressed = false
  Type = 0
FEATURE [Sketcher::SketchObject] Sketch098
  ArcFitTolerance = 1e-06
  AttachmentSupport = -> [Pad006]
  ExternalGeometry = -> [Binder]
  FullyConstrained = true
  MakeInternals = false
  MapMode = 5
  Placement = pos=(0,2.8,-7e-16) rot=(0,0.707107,0.707107;3.14159rad)
  sketch-geometry (4):
    g0: LineSegment StartX=118 StartY=39.2 StartZ=0 EndX=129 EndY=39.2 EndZ=0
    g1: LineSegment StartX=120.599 StartY=31.2 StartZ=0 EndX=131.599 EndY=31.2 EndZ=0
    g2: LineSegment StartX=129 StartY=39.2 StartZ=0 EndX=131.599 EndY=31.2 EndZ=0
    g3: LineSegment StartX=118 StartY=39.2 StartZ=0 EndX=120.599 EndY=31.2 EndZ=0
  constraints (12):
    c: PointOnObject(g0,g-3)
    c: PointOnObject(g0,g-3)
    c: DistanceX(g0,g0) = 11
    c: Horizontal(g1)
    c: Equal(g1,g0)
    c: Coincident(g2,g0)
    c: Coincident(g3,g0)
    c: Parallel(g-4,g2)
    c: Coincident(g1,g2)
    c: Coincident(g1,g3)
    c: DistanceY(g1,g0) = 8
    c: DistanceX(g-3,g0) = 118
FEATURE [Sketcher::SketchObject] Sketch099
  ArcFitTolerance = 1e-06
  AttachmentSupport = -> [Pad008]
  ExternalGeometry = -> [Binder]
  FullyConstrained = true
  MakeInternals = false
  MapMode = 5
  Placement = pos=(0,3.6,0) rot=(0,0.707107,0.707107;3.14159rad)
  sketch-geometry (13):
    g0: LineSegment StartX=192.176 StartY=-3.18451 StartZ=0 EndX=196.804 EndY=-13.1108 EndZ=0
    g1: LineSegment [constr] StartX=202.765 StartY=20.303 StartZ=0 EndX=181.223 EndY=20.303 EndZ=0
    g2: LineSegment [constr] StartX=181.223 StartY=20.303 StartZ=0 EndX=181.223 EndY=-3.18451 EndZ=0
    g3: ArcOfCircle CenterX=181.223 CenterY=-20.3764 CenterZ=0 NormalX=0 NormalY=0 NormalZ=1 AngleXU=0 Radius=17.1918 StartAngle=0.436332 EndAngle=1.57079
    g4: ArcOfEllipse CenterX=181.223 CenterY=8.55923 CenterZ=0 NormalX=0 NormalY=0 NormalZ=1 MajorRadius=23.4779 MinorRadius=11.7437 AngleXU=0 StartAngle=1.5708 EndAngle=4.71239
    g5: LineSegment [constr] StartX=204.701 StartY=8.55923 StartZ=0 EndX=157.745 EndY=8.55923 EndZ=0
    g6: LineSegment [constr] StartX=181.223 StartY=20.303 StartZ=0 EndX=181.223 EndY=-3.18451 EndZ=0
    g7: GeomPoint [constr] X=201.553 Y=8.55923 Z=0
    g8: GeomPoint [constr] X=160.894 Y=8.55923 Z=0
    g9: GeomPoint [constr] X=181.223 Y=-3.18451 Z=0
    g10: LineSegment StartX=181.223 StartY=20.303 StartZ=0 EndX=202.765 EndY=20.303 EndZ=0
    g11: ArcOfCircle CenterX=207.583 CenterY=4 CenterZ=0 NormalX=0 NormalY=0 NormalZ=1 AngleXU=0 Radius=17 StartAngle=1.85815 EndAngle=3.57792
    g12: LineSegment [constr] StartX=172.411 StartY=39.2 StartZ=0 EndX=192.176 EndY=-3.18451 EndZ=0
  constraints (27):
    c: Coincident(g1,g-7)
    c: Horizontal(g1)
    c: Coincident(g2,g1)
    c: Vertical(g2)
    c: Horizontal(g2,g0)
    c: Coincident(g3,g0)
    c: Coincident(g3,g2)
    c: InternalAlignment(g5-g8 -> g4) x4
    c: Horizontal(g5)
    c: PointOnObject(g4,g2)
    c: Coincident(g4,g1)
    c: DistanceX(g-3,g5) = 10.1
    c: Coincident(g4,g2)
    c: Tangent(g3,g-5)
    c: PointOnObject(g9,g4)
    c: PointOnObject(g9,g3)
    c: Tangent(g4,g3,g9) = 1.5708
    c: Coincident(g10,g1)
    c: Coincident(g10,g1)
    c: Equal(g11,g-4)
    c: Coincident(g11,g1)
    c: Coincident(g11,g0)
    c: PointOnObject(g12,g-6)
    c: PointOnObject(g1,g12)
    c: Tangent(g12,g-5) = -1.5708
    c: Tangent(g0,g-5) = -1.5708
    c: Horizontal(g9,g12)
FEATURE [Sketcher::SketchObject] Sketch106  label="Sketch106 - smusso impuniatura interno"
  ArcFitTolerance = 1e-06
  AttachmentSupport = -> [Pad008]
  ExternalGeometry = -> [Pad008]
  FullyConstrained = true
  MakeInternals = false
  MapMode = 5
  Placement = pos=(0,-1.585e-13,-80.4316) rot=(1,0,0;3.14159rad)
  sketch-geometry (9):
    g0: LineSegment StartX=-176.685 StartY=-3.6 StartZ=0 EndX=-176.685 EndY=2.66e-14 EndZ=0
    g1: LineSegment [constr] StartX=-176.685 StartY=-7.37e-14 StartZ=0 EndX=-176.685 EndY=2.65e-14 EndZ=0
    g2: LineSegment [constr] StartX=-186.685 StartY=-3.6 StartZ=0 EndX=-186.685 EndY=2.66e-14 EndZ=0
    g3: ArcOfEllipse CenterX=-186.685 CenterY=2.65e-14 CenterZ=0 NormalX=0 NormalY=0 NormalZ=1 MajorRadius=10 MinorRadius=3.6 AngleXU=-3.14159 StartAngle=1.5708 EndAngle=3.14159
    g4: LineSegment [constr] StartX=-196.685 StartY=-5.9e-15 StartZ=0 EndX=-176.685 EndY=-5.9e-15 EndZ=0
    g5: LineSegment [constr] StartX=-186.685 StartY=-3.6 StartZ=0 EndX=-186.685 EndY=3.6 EndZ=0
    g6: GeomPoint [constr] X=-196.015 Y=-9.7e-15 Z=0
    g7: GeomPoint [constr] X=-177.356 Y=-4.9e-15 Z=0
    g8: LineSegment StartX=-176.685 StartY=-3.6 StartZ=0 EndX=-186.685 EndY=-3.6 EndZ=0
  constraints (15):
    c: PointOnObject(g2,g-3)
    c: Coincident(g1,g-5)
    c: DistanceY(g1,g1) = 0
    c: Coincident(g0,g1)
    c: DistanceX(g2,g-5) = 10
    c: Vertical(g2)
    c: Horizontal(g2,g0)
    c: InternalAlignment(g4-g7 -> g3) x4
    c: Coincident(g3,g2)
    c: Horizontal(g4)
    c: Coincident(g3,g0)
    c: Tangent(g0,g-5) = 1.5708
    c: Coincident(g3,g2)
    c: Coincident(g8,g0)
    c: Coincident(g8,g2)
FEATURE [Sketcher::SketchObject] Sketch107  label="Sketch107 - smusso impugnatura esterno"
  ArcFitTolerance = 1e-06
  AttachmentSupport = -> [Pad008]
  ExternalGeometry = -> [Pad008]
  FullyConstrained = true
  MakeInternals = false
  MapMode = 5
  Placement = pos=(0,-1.585e-13,-80.4316) rot=(1,0,0;3.14159rad)
  sketch-geometry (9):
    g0: LineSegment [constr] StartX=-215.932 StartY=-1.416e-13 StartZ=0 EndX=-215.932 EndY=-3.86e-14 EndZ=0
    g1: LineSegment StartX=-215.932 StartY=-3.6 StartZ=0 EndX=-215.932 EndY=-3.86e-14 EndZ=0
    g2: LineSegment StartX=-215.932 StartY=-3.6 StartZ=0 EndX=-205.932 EndY=-3.6 EndZ=0
    g3: LineSegment [constr] StartX=-205.932 StartY=-3.6 StartZ=0 EndX=-205.932 EndY=-3.86e-14 EndZ=0
    g4: ArcOfEllipse CenterX=-205.932 CenterY=-3.86e-14 CenterZ=0 NormalX=0 NormalY=0 NormalZ=1 MajorRadius=10 MinorRadius=3.6 AngleXU=-3.14159 StartAngle=-2.66e-14 EndAngle=1.5708
    g5: LineSegment [constr] StartX=-215.932 StartY=-1.416e-13 StartZ=0 EndX=-195.932 EndY=-1.416e-13 EndZ=0
    g6: LineSegment [constr] StartX=-205.932 StartY=-3.6 StartZ=0 EndX=-205.932 EndY=3.6 EndZ=0
    g7: GeomPoint [constr] X=-215.262 Y=-1.309e-13 Z=0
    g8: GeomPoint [constr] X=-196.602 Y=-1.551e-13 Z=0
  constraints (16):
    c: Coincident(g0,g-6)
    c: PointOnObject(g0,g-6)
    c: DistanceY(g0,g0) = 0
    c: Coincident(g1,g-6)
    c: Coincident(g1,g0)
    c: Tangent(g2,g-3)
    c: DistanceX(g2,g2) = 10
    c: Coincident(g3,g2)
    c: Vertical(g3)
    c: Horizontal(g3,g0)
    c: InternalAlignment(g5-g8 -> g4) x4
    c: Coincident(g4,g3)
    c: Horizontal(g5)
    c: Coincident(g4,g0)
    c: Coincident(g4,g2)
    c: PointOnObject(g2,g1)
FEATURE [Sketcher::SketchObject] Sketch108
  ArcFitTolerance = 1e-06
  AttachmentOffset = pos=(0,0,-1.6) rot=(0,0,1;0rad)
  AttachmentSupport = -> [Pad008]
  ExternalGeometry = -> [Binder]
  FullyConstrained = true
  MakeInternals = false
  MapMode = 5
  Placement = pos=(0,2,4e-16) rot=(0,0.707107,0.707107;3.14159rad)
  sketch-geometry (14):
    g0: LineSegment StartX=192.176 StartY=-3.18451 StartZ=0 EndX=193.827 EndY=-6.72678 EndZ=0
    g1: LineSegment [constr] StartX=202.765 StartY=20.303 StartZ=0 EndX=181.223 EndY=20.303 EndZ=0
    g2: LineSegment [constr] StartX=181.223 StartY=20.303 StartZ=0 EndX=181.223 EndY=1.30297 EndZ=0
    g3: ArcOfCircle CenterX=181.223 CenterY=-12.6042 CenterZ=0 NormalX=0 NormalY=0 NormalZ=1 AngleXU=0 Radius=13.9072 StartAngle=0.436332 EndAngle=1.5708
    g4: ArcOfEllipse CenterX=181.223 CenterY=10.803 CenterZ=0 NormalX=0 NormalY=0 NormalZ=1 MajorRadius=14.4779 MinorRadius=9.5 AngleXU=0 StartAngle=1.5708 EndAngle=4.71239
    g5: LineSegment [constr] StartX=195.701 StartY=10.803 StartZ=0 EndX=166.745 EndY=10.803 EndZ=0
    g6: LineSegment [constr] StartX=181.223 StartY=20.303 StartZ=0 EndX=181.223 EndY=1.30297 EndZ=0
    g7: GeomPoint [constr] X=192.148 Y=10.803 Z=0
    g8: GeomPoint [constr] X=170.298 Y=10.803 Z=0
    g9: LineSegment StartX=181.223 StartY=20.303 StartZ=0 EndX=202.765 EndY=20.303 EndZ=0
    g10: ArcOfCircle CenterX=207.583 CenterY=4 CenterZ=0 NormalX=0 NormalY=0 NormalZ=1 AngleXU=0 Radius=17 StartAngle=1.85815 EndAngle=3.57792
    g11: LineSegment [constr] StartX=172.411 StartY=39.2 StartZ=0 EndX=192.176 EndY=-3.18451 EndZ=0
    g12: GeomPoint [constr] X=181.223 Y=1.30297 Z=0
    g13: GeomPoint [constr] X=181.223 Y=1.30297 Z=0
  constraints (28):
    c: Coincident(g1,g-7)
    c: Horizontal(g1)
    c: Coincident(g2,g1)
    c: Vertical(g2)
    c: Coincident(g3,g2)
    c: InternalAlignment(g5-g8 -> g4) x4
    c: Horizontal(g5)
    c: PointOnObject(g4,g2)
    c: Coincident(g4,g1)
    c: DistanceX(g-3,g5) = 19.1
    c: Coincident(g4,g2)
    c: Coincident(g9,g1)
    c: Coincident(g9,g1)
    c: Coincident(g10,g1)
    c: Coincident(g10,g0)
    c: PointOnObject(g11,g-6)
    c: PointOnObject(g1,g11)
    c: DistanceY(g2,g1) = 19
    c: Coincident(g10,g-4)
    c: PointOnObject(g12,g4)
    c: PointOnObject(g12,g3)
    c: Tangent(g11,g-5) = -1.5708
    c: Tangent(g0,g-5) = -1.5708
    c: Tangent(g3,g0) = 1.5708
    c: PointOnObject(g13,g4)
    c: PointOnObject(g13,g3)
    c: Tangent(g4,g3,g13) = 1.5708
    c: Horizontal(g11,g0)
FEATURE [Part::Part2DObjectPython] Clone2D  label="Sketch108 (2D)"  # Draft 2D object (typed FeaturePython)
  Fuse = false
  Objects = -> [Sketch108]
  Placement = pos=(0,2,4e-16) rot=(0,0.707107,0.707107;3.14159rad)
  Scale = (1,1,1)
FEATURE [Sketcher::SketchObject] Sketch109
  ArcFitTolerance = 1e-06
  AttachmentOffset = pos=(0,0,-3.5) rot=(0,0,1;0rad)
  AttachmentSupport = -> [Pad008]
  ExternalGeometry = -> [Binder]
  FullyConstrained = true
  MakeInternals = false
  MapMode = 5
  Placement = pos=(0,0.1,8e-16) rot=(0,0.707107,0.707107;3.14159rad)
  sketch-geometry (1):
    g0: GeomPoint X=197.47 Y=8.55923 Z=0
  constraints (1):
    c: Symmetric(g-7,g-5,g0)
FEATURE [PartDesign::Chamfer] Chamfer005
  Angle = 45
  Base = -> Pad009 [Edge215,Edge212]
  BaseFeature = -> Pad009
  ChamferType = 1
  FlipDirection = false
  Refine = true
  Size = 1.5
  Size2 = 2.8
  SupportTransform = false
  Suppressed = false
  UseAllEdges = false
FEATURE [Sketcher::SketchObject] Sketch111
  ArcFitTolerance = 1e-06
  AttachmentSupport = -> [Pad009]
  ExternalGeometry = -> [Pad009]
  FullyConstrained = true
  MakeInternals = false
  MapMode = 5
  Placement = pos=(0,3.6,-8e-16) rot=(0,0.707107,0.707107;3.14159rad)
  sketch-geometry (21):
    g0: LineSegment [constr] StartX=97 StartY=36.8 StartZ=0 EndX=97 EndY=26.8 EndZ=0
    g1: LineSegment StartX=97 StartY=28.6 StartZ=0 EndX=97 EndY=27.8 EndZ=0
    g2: LineSegment StartX=97 StartY=27.8 StartZ=0 EndX=108 EndY=27.8 EndZ=0
    g3: LineSegment StartX=108 StartY=27.8 StartZ=0 EndX=108 EndY=28.6 EndZ=0
    g4: LineSegment StartX=108 StartY=28.6 StartZ=0 EndX=97 EndY=28.6 EndZ=0
    g5: LineSegment StartX=97 StartY=35.8 StartZ=0 EndX=97 EndY=35 EndZ=0
    g6: LineSegment StartX=97 StartY=35 StartZ=0 EndX=108 EndY=35 EndZ=0
    g7: LineSegment StartX=108 StartY=35 StartZ=0 EndX=108 EndY=35.8 EndZ=0
    g8: LineSegment StartX=108 StartY=35.8 StartZ=0 EndX=97 EndY=35.8 EndZ=0
    g9: LineSegment StartX=97 StartY=30.4 StartZ=0 EndX=97 EndY=29.6 EndZ=0
    g10: LineSegment StartX=97 StartY=29.6 StartZ=0 EndX=108 EndY=29.6 EndZ=0
    g11: LineSegment StartX=108 StartY=29.6 StartZ=0 EndX=108 EndY=30.4 EndZ=0
    g12: LineSegment StartX=108 StartY=30.4 StartZ=0 EndX=97 EndY=30.4 EndZ=0
    g13: LineSegment StartX=97 StartY=34 StartZ=0 EndX=97 EndY=33.2 EndZ=0
    g14: LineSegment StartX=97 StartY=33.2 StartZ=0 EndX=108 EndY=33.2 EndZ=0
    g15: LineSegment StartX=108 StartY=33.2 StartZ=0 EndX=108 EndY=34 EndZ=0
    g16: LineSegment StartX=108 StartY=34 StartZ=0 EndX=97 EndY=34 EndZ=0
    g17: LineSegment StartX=97 StartY=32.2 StartZ=0 EndX=97 EndY=31.4 EndZ=0
    g18: LineSegment StartX=97 StartY=31.4 StartZ=0 EndX=108 EndY=31.4 EndZ=0
    g19: LineSegment StartX=108 StartY=31.4 StartZ=0 EndX=108 EndY=32.2 EndZ=0
    g20: LineSegment StartX=108 StartY=32.2 StartZ=0 EndX=97 EndY=32.2 EndZ=0
  constraints (54):
    c: Vertical(g0)
    c: PointOnObject(g0,g-3)
    c: PointOnObject(g0,g-4)
    c: DistanceX(g0,g-5) = 11
    c: Coincident(g1,g2)
    c: Coincident(g2,g3)
    c: Coincident(g3,g4)
    c: Coincident(g4,g1)
    c: Horizontal(g2)
    c: Horizontal(g4)
    c: Tangent(g1,g0)
    c: Tangent(g3,g-5)
    c: DistanceY(g2,g3) = 0.8
    c: Coincident(g5,g6)
    c: Coincident(g6,g7)
    c: Coincident(g7,g8)
    c: Coincident(g8,g5)
    c: Horizontal(g6)
    c: Horizontal(g8)
    c: DistanceY(g6,g7) = 0.8
    c: Coincident(g9,g10)
    c: Coincident(g10,g11)
    c: Coincident(g11,g12)
    c: Coincident(g12,g9)
    c: Horizontal(g10)
    c: Horizontal(g12)
    c: DistanceY(g10,g11) = 0.8
    c: Tangent(g5,g0)
    c: Tangent(g7,g-5)
    c: Tangent(g9,g0)
    c: Tangent(g11,g-5)
    c: Coincident(g13,g14)
    c: Coincident(g14,g15)
    c: Coincident(g15,g16)
    c: Coincident(g16,g13)
    c: Horizontal(g14)
    c: Horizontal(g16)
    c: DistanceY(g14,g15) = 0.8
    c: Tangent(g13,g0)
    c: Tangent(g15,g-5)
    c: Coincident(g17,g18)
    c: Coincident(g18,g19)
    c: Coincident(g19,g20)
    c: Coincident(g20,g17)
    c: Horizontal(g18)
    c: Horizontal(g20)
    c: DistanceY(g18,g19) = 0.8
    c: Tangent(g17,g0)
    c: Tangent(g19,g-5)
    c: DistanceY(g1,g9) = 1
    c: DistanceY(g9,g17) = 1
    c: DistanceY(g17,g13) = 1
    c: DistanceY(g13,g5) = 1
    c: DistanceY(g0,g1) = 1
FEATURE [PartDesign::Pocket] Pocket004
  BaseFeature = -> Chamfer005
  Direction = (0,-1,2e-16)
  Length = 1
  Length2 = 5
  Profile = -> Sketch111
  ReferenceAxis = -> Sketch111 [N_Axis]
  Refine = true
  Suppressed = false
  Type = 0
FEATURE [PartDesign::Pad] Pad010
  BaseFeature = -> Pocket004
  Direction = (0,1,-2e-16)
  Length = 1.2
  Length2 = 10
  Profile = -> Sketch098
  ReferenceAxis = -> Sketch098 [N_Axis]
  Refine = true
  Suppressed = false
  Type = 0
FEATURE [PartDesign::Chamfer] Chamfer006
  Angle = 45
  Base = -> Pad010 [Edge291]
  BaseFeature = -> Pad010
  ChamferType = 1
  FlipDirection = false
  Refine = true
  Size = 1
  Size2 = 6
  SupportTransform = false
  Suppressed = false
  UseAllEdges = false
FEATURE [Sketcher::SketchObject] Sketch110
  ArcFitTolerance = 1e-06
  AttachmentSupport = -> [Pad010]
  ExternalGeometry = -> [Sketch098]
  FullyConstrained = true
  MakeInternals = false
  MapMode = 5
  Placement = pos=(0,4,-9e-16) rot=(0,0.707107,0.707107;3.14159rad)
  sketch-geometry (8):
    g0: LineSegment StartX=119.69 StartY=34 StartZ=0 EndX=130.69 EndY=34 EndZ=0
    g1: LineSegment StartX=119.95 StartY=33.2 StartZ=0 EndX=130.95 EndY=33.2 EndZ=0
    g2: LineSegment StartX=119.137 StartY=35.7 StartZ=0 EndX=130.137 EndY=35.7 EndZ=0
    g3: LineSegment StartX=118.877 StartY=36.5 StartZ=0 EndX=129.877 EndY=36.5 EndZ=0
    g4: LineSegment StartX=118.877 StartY=36.5 StartZ=0 EndX=119.137 EndY=35.7 EndZ=0
    g5: LineSegment StartX=129.877 StartY=36.5 StartZ=0 EndX=130.137 EndY=35.7 EndZ=0
    g6: LineSegment StartX=119.69 StartY=34 StartZ=0 EndX=119.95 EndY=33.2 EndZ=0
    g7: LineSegment StartX=130.69 StartY=34 StartZ=0 EndX=130.95 EndY=33.2 EndZ=0
  constraints (24):
    c: Horizontal(g0)
    c: Horizontal(g1)
    c: Horizontal(g2)
    c: Horizontal(g3)
    c: Equal(g1,g-5)
    c: Equal(g0,g-5)
    c: Equal(g2,g-5)
    c: Equal(g3,g-5)
    c: PointOnObject(g0,g-3)
    c: PointOnObject(g1,g-3)
    c: PointOnObject(g2,g-3)
    c: PointOnObject(g3,g-3)
    c: Coincident(g4,g3)
    c: Coincident(g4,g2)
    c: Coincident(g5,g3)
    c: Coincident(g5,g2)
    c: Coincident(g6,g0)
    c: Coincident(g6,g1)
    c: Coincident(g7,g0)
    c: Coincident(g7,g1)
    c: DistanceY(g1,g0) = 0.8
    c: DistanceY(g2,g3) = 0.8
    c: DistanceY(g-5,g1) = 2
    c: DistanceY(g-5,g2) = 4.5
FEATURE [PartDesign::Pocket] Pocket003
  BaseFeature = -> Chamfer006
  Direction = (0,-1,2e-16)
  Length = 1
  Length2 = 5
  Profile = -> Sketch110
  ReferenceAxis = -> Sketch110 [N_Axis]
  Refine = true
  Suppressed = false
  Type = 0
FEATURE [PartDesign::SubtractivePipe] SubtractivePipe
  AuxilleryCurvelinear = true
  AuxillerySpineTangent = false
  BaseFeature = -> Pocket003
  Binormal = (0,0,0)
  Mode = 0
  Profile = -> Sketch106
  Refine = true
  Spine = -> Pad008 [Edge215]
  SpineTangent = false
  Suppressed = false
  Transformation = 0
  Transition = 0
FEATURE [PartDesign::SubtractivePipe] SubtractivePipe001
  AuxilleryCurvelinear = true
  AuxillerySpineTangent = false
  BaseFeature = -> SubtractivePipe
  Binormal = (0,0,0)
  Mode = 0
  Profile = -> Sketch107
  Refine = true
  Spine = -> Pad008 [Edge213,Edge216,Edge210]
  SpineTangent = false
  Suppressed = false
  Transformation = 0
  Transition = 0
FEATURE [PartDesign::SubtractiveLoft] SubtractiveLoft
  BaseFeature = -> SubtractivePipe001
  Closed = false
  Profile = -> Sketch099
  Refine = true
  Ruled = false
  Sections = -> [Sketch108]
  Suppressed = false
FEATURE [PartDesign::SubtractiveLoft] SubtractiveLoft001
  BaseFeature = -> SubtractiveLoft
  Closed = false
  Profile = -> Clone2D
  Refine = true
  Ruled = false
  Sections = -> [Sketch109]
  Suppressed = false
FEATURE [Sketcher::SketchObject] Sketch112
  ArcFitTolerance = 1e-06
  AttachmentSupport = -> [Pad008]
  ExternalGeometry = -> [Binder]
  FullyConstrained = true
  MakeInternals = false
  MapMode = 5
  Placement = pos=(0,3.6,0) rot=(0,0.707107,0.707107;3.14159rad)
  sketch-geometry (4):
    g0: LineSegment [constr] StartX=167.782 StartY=-53.0314 StartZ=0 EndX=215.42 EndY=-53.0314 EndZ=0
    g1: GeomPoint [constr] X=191.282 Y=-53.0314 Z=0
    g2: Circle CenterX=191.282 CenterY=-53.0314 CenterZ=0 NormalX=0 NormalY=0 NormalZ=1 AngleXU=0 Radius=11.5
    g3: Circle CenterX=191.282 CenterY=-53.0314 CenterZ=0 NormalX=0 NormalY=0 NormalZ=1 AngleXU=0 Radius=10.7
  constraints (9):
    c: Horizontal(g0)
    c: PointOnObject(g0,g-3)
    c: Diameter(g2) = 23
    c: Coincident(g2,g1)
    c: Diameter(g3) = 21.4
    c: Coincident(g3,g1)
    c: DistanceX(g0,g1) = 23.5
    c: PointOnObject(g1,g0)
    c: Coincident(g0,g-4)
FEATURE [PartDesign::Chamfer] Chamfer016
  Angle = 45
  Base = -> SubtractiveLoft001 [Edge118,Edge117,Edge119,Edge120,Edge109]
  BaseFeature = -> SubtractiveLoft001
  ChamferType = 0
  FlipDirection = false
  Refine = true
  Size = 1.5
  Size2 = 1
  SupportTransform = false
  Suppressed = false
  UseAllEdges = false
FEATURE [PartDesign::Chamfer] Chamfer017
  Angle = 45
  Base = -> Chamfer016 [Edge15]
  BaseFeature = -> Chamfer016
  ChamferType = 0
  FlipDirection = false
  Refine = true
  Size = 1.6
  Size2 = 1
  SupportTransform = false
  Suppressed = false
  UseAllEdges = false
FEATURE [PartDesign::Chamfer] Chamfer018
  Angle = 45
  Base = -> Chamfer017 [Edge10]
  BaseFeature = -> Chamfer017
  ChamferType = 0
  FlipDirection = false
  Refine = true
  Size = 3.5
  Size2 = 1
  SupportTransform = false
  Suppressed = false
  UseAllEdges = false
FEATURE [PartDesign::Chamfer] Chamfer019
  Angle = 45
  Base = -> Chamfer018 [Edge94]
  BaseFeature = -> Chamfer018
  ChamferType = 0
  FlipDirection = false
  Refine = true
  Size = 1.9
  Size2 = 1
  SupportTransform = false
  Suppressed = false
  UseAllEdges = false
FEATURE [PartDesign::Fillet] Fillet009
  Base = -> Chamfer019 [Edge83]
  BaseFeature = -> Chamfer019
  Radius = 1.1
  Refine = true
  SupportTransform = false
  Suppressed = false
  UseAllEdges = false
FEATURE [PartDesign::Fillet] Fillet010
  Base = -> Fillet009 [Edge76]
  BaseFeature = -> Fillet009
  Radius = 1.9
  Refine = true
  SupportTransform = false
  Suppressed = false
  UseAllEdges = false
FEATURE [PartDesign::Pocket] Pocket005
  BaseFeature = -> Fillet010
  Direction = (0,-1,2e-16)
  Length = 0.8
  Length2 = 5
  Profile = -> Sketch112
  ReferenceAxis = -> Sketch112 [N_Axis]
  Refine = true
  Suppressed = false
  Type = 0
FEATURE [Part::Part2DObjectPython] ShapeString001  # Draft 2D object (typed FeaturePython)
  FontFile = <path>
  Fuse = false
  Justification = 6
  JustificationReference = 0
  KeepLeftMargin = false
  MakeFace = true
  ObliqueAngle = 0
  Placement = pos=(-183.5,3.6,-57.5) rot=(0,0.707107,0.707107;3.14159rad)
  ScaleToSize = true
  Size = 10
  String = AS
  Tracking = 0
FEATURE [PartDesign::Pocket] Pocket013
  BaseFeature = -> Pocket005
  Direction = (-1e-16,-1,2e-16)
  Length = 1
  Length2 = 5
  Profile = -> ShapeString001
  ReferenceAxis = -> ShapeString001 [N_Axis]
  Refine = true
  Suppressed = false
  Type = 0
FEATURE [PartDesign::Pad] Pad020
  Direction = (0,-1,2e-16)
  Length = 25.2
  Length2 = 10
  Midplane = true
  Placement = pos=(0,0,0) rot=(1,0,0;1.5708rad)
  Profile = -> Sketch021
  ReferenceAxis = -> Sketch021 [N_Axis]
  Refine = true
  Suppressed = false
  Type = 0
FEATURE [PartDesign::Body] Body001  label="perno fermo rumble e driver solenoide"
  AllowCompound = false
  Group = -> [Sketch021,Pad020]
  Origin = -> Origin001
  Tip = -> Pad020
FEATURE [PartDesign::Pad] Pad021
  Direction = (0,-1,2e-16)
  Length = 16.8
  Length2 = 10
  Midplane = true
  Placement = pos=(0,0,0) rot=(1,0,0;1.5708rad)
  Profile = -> Sketch061
  ReferenceAxis = -> Sketch061 [N_Axis]
  Refine = true
  Suppressed = false
  Type = 0
FEATURE [PartDesign::Pocket] Pocket014
  BaseFeature = -> Pad021
  Direction = (0,1,-2e-16)
  Length = 12.8
  Length2 = 5
  Midplane = true
  Placement = pos=(0,0,0) rot=(1,0,0;1.5708rad)
  Profile = -> Sketch062
  ReferenceAxis = -> Sketch062 [N_Axis]
  Refine = true
  Suppressed = false
  Type = 0
FEATURE [PartDesign::Pad] Pad022
  BaseFeature = -> Pocket014
  Direction = (0,-1,2e-16)
  Length = 7.6
  Length2 = 10
  Midplane = true
  Placement = pos=(0,0,0) rot=(1,0,0;1.5708rad)
  Profile = -> Sketch063
  ReferenceAxis = -> Sketch063 [N_Axis]
  Refine = true
  Suppressed = false
  Type = 0
FEATURE [PartDesign::Body] Body003  label="blocco switch"
  AllowCompound = false
  Group = -> [Sketch061,Sketch062,Sketch063,Pad021,Pocket014,Pad022]
  Origin = -> Origin003
  Tip = -> Pad022
FEATURE [PartDesign::Pad] Pad024
  Direction = (0,-1,2e-16)
  Length = 17
  Length2 = 10
  Midplane = true
  Placement = pos=(0,0,0) rot=(1,0,0;1.5708rad)
  Profile = -> Sketch045
  ReferenceAxis = -> Sketch045 [N_Axis]
  Refine = true
  Suppressed = false
  Type = 0
FEATURE [PartDesign::Pocket] Pocket015
  BaseFeature = -> Pad024
  Direction = (-1,0,0)
  Length = 8
  Length2 = 5
  Placement = pos=(0,0,0) rot=(1,0,0;1.5708rad)
  Profile = -> Sketch047
  ReferenceAxis = -> Sketch047 [N_Axis]
  Refine = true
  Reversed = true
  Suppressed = false
  Type = 0
FEATURE [PartDesign::Pocket] Pocket016
  BaseFeature = -> Pocket015
  Direction = (-1,0,0)
  Length = 1
  Length2 = 5
  Placement = pos=(0,0,0) rot=(1,0,0;1.5708rad)
  Profile = -> Sketch046
  ReferenceAxis = -> Sketch046 [N_Axis]
  Refine = true
  Reversed = true
  Suppressed = false
  Type = 0
FEATURE [PartDesign::Pocket] Pocket017
  BaseFeature = -> Pocket016
  Direction = (0,1,-2e-16)
  Length = 17
  Length2 = 5
  Midplane = true
  Placement = pos=(0,0,0) rot=(1,0,0;1.5708rad)
  Profile = -> Sketch048
  ReferenceAxis = -> Sketch048 [N_Axis]
  Refine = true
  Suppressed = false
  Type = 0
FEATURE [PartDesign::Pad] Pad025
  BaseFeature = -> Pocket017
  Direction = (0,-1,2e-16)
  Length = 17
  Length2 = 10
  Midplane = true
  Placement = pos=(0,0,0) rot=(1,0,0;1.5708rad)
  Profile = -> Sketch049
  ReferenceAxis = -> Sketch049 [N_Axis]
  Refine = true
  Suppressed = false
  Type = 0
FEATURE [PartDesign::Pad] Pad026
  BaseFeature = -> Pad025
  Direction = (0,-1,2e-16)
  Length = 17
  Length2 = 10
  Midplane = true
  Placement = pos=(0,0,0) rot=(1,0,0;1.5708rad)
  Profile = -> Sketch066
  ReferenceAxis = -> Sketch066 [N_Axis]
  Refine = true
  Suppressed = false
  Type = 0
FEATURE [PartDesign::Pad] Pad027
  BaseFeature = -> Pad026
  Direction = (0,-1,2e-16)
  Length = 5
  Length2 = 10
  Midplane = true
  Placement = pos=(0,0,0) rot=(1,0,0;1.5708rad)
  Profile = -> Sketch064
  ReferenceAxis = -> Sketch064 [N_Axis]
  Refine = true
  Suppressed = false
  Type = 0
FEATURE [PartDesign::Pad] Pad028
  BaseFeature = -> Pad027
  Direction = (1,0,0)
  Length = 1
  Length2 = 10
  Placement = pos=(0,0,0) rot=(1,0,0;1.5708rad)
  Profile = -> Sketch068
  ReferenceAxis = -> Sketch068 [N_Axis]
  Refine = true
  Reversed = true
  Suppressed = false
  Type = 0
FEATURE [PartDesign::Chamfer] Chamfer020
  Angle = 45
  Base = -> Pad028 [Edge73,Edge75,Edge78,Edge77]
  BaseFeature = -> Pad028
  ChamferType = 0
  FlipDirection = false
  Placement = pos=(0,0,0) rot=(1,0,0;1.5708rad)
  Refine = true
  Size = 0.5
  Size2 = 1
  SupportTransform = false
  Suppressed = false
  UseAllEdges = false
FEATURE [PartDesign::Body] Body002  label="supporto per neopixel"
  AllowCompound = false
  Group = -> [Sketch045,Sketch047,Sketch046,Sketch048,Sketch049,Sketch066,Sketch064,Sketch068,Pad024,Pocket015,Pocket016,Pocket017,Pad025,Pad026,Pad027,Pad028,Chamfer020]
  Origin = -> Origin002
  Tip = -> Chamfer020
FEATURE [Sketcher::SketchObject] Sketch134  label="perno fermo rumble002"
  ArcFitTolerance = 1e-06
  AttachmentSupport = -> [XZ_Plane008]
  FullyConstrained = true
  MakeInternals = false
  MapMode = 5
  Placement = pos=(0,0,0) rot=(1,0,0;1.5708rad)
  sketch-geometry (16):
    g0: LineSegment StartX=0 StartY=0.45 StartZ=0 EndX=0 EndY=1.55 EndZ=0
    g1: LineSegment StartX=0.45 StartY=2 StartZ=0 EndX=1.55 EndY=2 EndZ=0
    g2: LineSegment StartX=2 StartY=1.55 StartZ=0 EndX=2 EndY=0.45 EndZ=0
    g3: LineSegment StartX=1.55 StartY=0 StartZ=0 EndX=0.45 EndY=0 EndZ=0
    g4: ArcOfCircle [constr] CenterX=0.45 CenterY=1.55 CenterZ=0 NormalX=0 NormalY=0 NormalZ=1 AngleXU=0 Radius=0.45 StartAngle=1.5708 EndAngle=3.14159
    g5: GeomPoint [constr] X=0 Y=2 Z=0
    g6: LineSegment StartX=0.45 StartY=2 StartZ=0 EndX=0 EndY=1.55 EndZ=0
    g7: ArcOfCircle [constr] CenterX=1.55 CenterY=1.55 CenterZ=0 NormalX=0 NormalY=0 NormalZ=1 AngleXU=0 Radius=0.45 StartAngle=0 EndAngle=1.5708
    g8: GeomPoint [constr] X=2 Y=2 Z=0
    g9: LineSegment StartX=2 StartY=1.55 StartZ=0 EndX=1.55 EndY=2 EndZ=0
    g10: ArcOfCircle [constr] CenterX=1.55 CenterY=0.45 CenterZ=0 NormalX=0 NormalY=0 NormalZ=1 AngleXU=0 Radius=0.45 StartAngle=4.71239 EndAngle=6.28319
    g11: GeomPoint [constr] X=2 Y=0 Z=0
    g12: LineSegment StartX=1.55 StartY=0 StartZ=0 EndX=2 EndY=0.45 EndZ=0
    g13: ArcOfCircle [constr] CenterX=0.45 CenterY=0.45 CenterZ=0 NormalX=0 NormalY=0 NormalZ=1 AngleXU=0 Radius=0.45 StartAngle=3.14159 EndAngle=4.71239
    g14: GeomPoint [constr] X=0 Y=0 Z=0
    g15: LineSegment StartX=0 StartY=0.45 StartZ=0 EndX=0.45 EndY=0 EndZ=0
  constraints (35):
    c: Coincident(g14,g-1)
    c: PointOnObject(g5,g-2)
    c: Horizontal(g1)
    c: Vertical(g2)
    c: Horizontal(g3)
    c: DistanceX(g5,g8) = 2
    c: DistanceY(g11,g8) = 2
    c: PointOnObject(g5,g0)
    c: PointOnObject(g5,g1)
    c: Tangent(g0,g4) = 1.5708
    c: Tangent(g1,g4) = 1.5708
    c: Coincident(g6,g0)
    c: Coincident(g6,g1)
    c: PointOnObject(g8,g2)
    c: PointOnObject(g8,g1)
    c: Tangent(g2,g7) = 1.5708
    c: Tangent(g1,g7) = 1.5708
    c: Coincident(g9,g2)
    c: Coincident(g9,g1)
    c: PointOnObject(g11,g2)
    c: PointOnObject(g11,g3)
    c: Tangent(g2,g10) = 1.5708
    c: Tangent(g3,g10) = 1.5708
    c: Coincident(g12,g2)
    c: Coincident(g12,g3)
    c: PointOnObject(g14,g0)
    c: PointOnObject(g14,g3)
    c: Tangent(g0,g13) = 1.5708
    c: Tangent(g3,g13) = 1.5708
    c: Coincident(g15,g0)
    c: Coincident(g15,g3)
    c: Equal(g6,g9)
    c: Equal(g9,g12)
    c: Equal(g12,g15)
    c: DistanceX(g14,g3) = 0.45
FEATURE [PartDesign::Pad] Pad029
  Direction = (0,-1,2e-16)
  Length = 17
  Length2 = 10
  Midplane = true
  Placement = pos=(0,0,0) rot=(1,0,0;1.5708rad)
  Profile = -> Sketch134
  ReferenceAxis = -> Sketch134 [N_Axis]
  Refine = true
  Suppressed = false
  Type = 0
FEATURE [PartDesign::Body] Body008  label="perno fermo neopixel"
  AllowCompound = false
  Group = -> [Sketch134,Pad029]
  Origin = -> Origin008
  Tip = -> Pad029
FEATURE [Sketcher::SketchObject] Sketch135  label="perno fermo rumble003"
  ArcFitTolerance = 1e-06
  AttachmentSupport = -> [XZ_Plane009]
  FullyConstrained = true
  MakeInternals = false
  MapMode = 5
  Placement = pos=(0,0,0) rot=(1,0,0;1.5708rad)
  sketch-geometry (16):
    g0: LineSegment StartX=4.69e-14 StartY=0.8 StartZ=0 EndX=-3.04e-14 EndY=3.1 EndZ=0
    g1: LineSegment StartX=0.8 StartY=3.9 StartZ=0 EndX=3.1 EndY=3.9 EndZ=0
    g2: LineSegment StartX=3.9 StartY=3.1 StartZ=0 EndX=3.9 EndY=0.8 EndZ=0
    g3: LineSegment StartX=3.1 StartY=0 StartZ=0 EndX=0.8 EndY=0 EndZ=0
    g4: ArcOfCircle [constr] CenterX=0.8 CenterY=3.1 CenterZ=0 NormalX=0 NormalY=0 NormalZ=1 AngleXU=0 Radius=0.8 StartAngle=1.5708 EndAngle=3.14159
    g5: GeomPoint [constr] X=0 Y=3.9 Z=0
    g6: LineSegment StartX=0.8 StartY=3.9 StartZ=0 EndX=-3.04e-14 EndY=3.1 EndZ=0
    g7: ArcOfCircle [constr] CenterX=3.1 CenterY=3.1 CenterZ=0 NormalX=0 NormalY=0 NormalZ=1 AngleXU=0 Radius=0.8 StartAngle=-2.4e-14 EndAngle=1.5708
    g8: GeomPoint [constr] X=3.9 Y=3.9 Z=0
    g9: LineSegment StartX=3.9 StartY=3.1 StartZ=0 EndX=3.1 EndY=3.9 EndZ=0
    g10: ArcOfCircle [constr] CenterX=3.1 CenterY=0.8 CenterZ=0 NormalX=0 NormalY=0 NormalZ=1 AngleXU=0 Radius=0.8 StartAngle=4.71239 EndAngle=6.28319
    g11: GeomPoint [constr] X=3.9 Y=0 Z=0
    g12: LineSegment StartX=3.1 StartY=0 StartZ=0 EndX=3.9 EndY=0.8 EndZ=0
    g13: ArcOfCircle [constr] CenterX=0.8 CenterY=0.8 CenterZ=0 NormalX=0 NormalY=0 NormalZ=1 AngleXU=0 Radius=0.8 StartAngle=3.14159 EndAngle=4.71239
    g14: GeomPoint [constr] X=0 Y=0 Z=0
    g15: LineSegment StartX=4.69e-14 StartY=0.8 StartZ=0 EndX=0.8 EndY=0 EndZ=0
  constraints (35):
    c: Coincident(g14,g-1)
    c: PointOnObject(g5,g-2)
    c: Horizontal(g1)
    c: Vertical(g2)
    c: Horizontal(g3)
    c: DistanceX(g5,g8) = 3.9
    c: DistanceY(g11,g8) = 3.9
    c: PointOnObject(g5,g0)
    c: PointOnObject(g5,g1)
    c: Tangent(g0,g4) = 1.5708
    c: Tangent(g1,g4) = 1.5708
    c: Coincident(g6,g0)
    c: Coincident(g6,g1)
    c: PointOnObject(g8,g2)
    c: PointOnObject(g8,g1)
    c: Tangent(g2,g7) = 1.5708
    c: Tangent(g1,g7) = 1.5708
    c: Coincident(g9,g2)
    c: Coincident(g9,g1)
    c: PointOnObject(g11,g2)
    c: PointOnObject(g11,g3)
    c: Tangent(g2,g10) = 1.5708
    c: Tangent(g3,g10) = 1.5708
    c: Coincident(g12,g2)
    c: Coincident(g12,g3)
    c: PointOnObject(g14,g0)
    c: PointOnObject(g14,g3)
    c: Tangent(g0,g13) = 1.5708
    c: Tangent(g3,g13) = 1.5708
    c: Coincident(g15,g0)
    c: Coincident(g15,g3)
    c: Equal(g6,g9)
    c: Equal(g9,g12)
    c: Equal(g12,g15)
    c: DistanceX(g14,g3) = 0.8
FEATURE [PartDesign::Pad] Pad030
  Direction = (0,-1,2e-16)
  Length = 25.2
  Length2 = 10
  Midplane = true
  Placement = pos=(0,0,0) rot=(1,0,0;1.5708rad)
  Profile = -> Sketch135
  ReferenceAxis = -> Sketch135 [N_Axis]
  Refine = true
  Suppressed = false
  Type = 0
FEATURE [PartDesign::Body] Body009  label="perno fermo switch - caricabatterie - grilletto"
  AllowCompound = false
  Group = -> [Sketch135,Pad030]
  Origin = -> Origin009
  Tip = -> Pad030
FEATURE [Sketcher::SketchObject] Sketch136  label="scavo_rele"
  ArcFitTolerance = 1e-06
  AttachmentSupport = -> [XZ_Plane]
  ExternalGeometry = -> [Sketch]
  FullyConstrained = true
  MakeInternals = false
  MapMode = 5
  Placement = pos=(0,0,0) rot=(1,0,0;1.5708rad)
  sketch-geometry (7):
    g0: LineSegment [constr] StartX=-173.013 StartY=-62.644 StartZ=0 EndX=-176.535 EndY=-73.4861 EndZ=0
    g1: LineSegment [constr] StartX=-173.013 StartY=-62.644 StartZ=0 EndX=-170.35 EndY=-63.5093 EndZ=0
    g2: LineSegment [constr] StartX=-173.013 StartY=-62.644 StartZ=0 EndX=-176.627 EndY=-61.4698 EndZ=0
    g3: LineSegment StartX=-176.627 StartY=-61.4698 StartZ=0 EndX=-170.35 EndY=-63.5093 EndZ=0
    g4: LineSegment StartX=-176.627 StartY=-61.4698 StartZ=0 EndX=-180.149 EndY=-72.3118 EndZ=0
    g5: LineSegment StartX=-170.35 StartY=-63.5093 StartZ=0 EndX=-173.872 EndY=-74.3513 EndZ=0
    g6: LineSegment StartX=-180.149 StartY=-72.3118 StartZ=0 EndX=-173.872 EndY=-74.3513 EndZ=0
  constraints (19):
    c: Tangent(g0,g-3)
    c: Distance(g0,g-3) = 89
    c: Distance(g0,g0) = 11.4
    c: Coincident(g1,g0)
    c: Coincident(g2,g0)
    c: Distance(g2) = 3.8
    c: Distance(g1) = 2.8
    c: Perpendicular(g0,g1)
    c: Perpendicular(g0,g2)
    c: Coincident(g3,g2)
    c: Coincident(g3,g1)
    c: Equal(g4,g0)
    c: Equal(g5,g0)
    c: Parallel(g4,g0)
    c: Parallel(g5,g0)
    c: Coincident(g4,g2)
    c: Coincident(g5,g1)
    c: Coincident(g6,g4)
    c: Coincident(g6,g5)
FEATURE [Part::Extrusion] Extrude076  label="Extrude076 - scavo_rele"
  Base = -> Sketch136
  Dir = (0,-1,2e-16)
  DirMode = 2
  FaceMakerClass = Part::FaceMakerBullseye
  FaceMakerMode = 3
  LengthFwd = 17.8
  LengthRev = 0
  Solid = true
  Symmetric = true
FEATURE [Sketcher::SketchObject] Sketch137  label="scavo_nuovo_driver"
  ArcFitTolerance = 1e-06
  AttachmentSupport = -> [XZ_Plane]
  ExternalGeometry = -> [Sketch]
  FullyConstrained = true
  MakeInternals = false
  MapMode = 5
  Placement = pos=(0,0,0) rot=(1,0,0;1.5708rad)
  sketch-geometry (7):
    g0: LineSegment [constr] StartX=-167.759 StartY=-46.4761 StartZ=0 EndX=-172.58 EndY=-61.3126 EndZ=0
    g1: LineSegment [constr] StartX=-167.759 StartY=-46.4761 StartZ=0 EndX=-165.477 EndY=-47.2177 EndZ=0
    g2: LineSegment [constr] StartX=-167.759 StartY=-46.4761 StartZ=0 EndX=-171.373 EndY=-45.3018 EndZ=0
    g3: LineSegment StartX=-171.373 StartY=-45.3018 StartZ=0 EndX=-165.477 EndY=-47.2177 EndZ=0
    g4: LineSegment StartX=-171.373 StartY=-45.3018 StartZ=0 EndX=-176.194 EndY=-60.1383 EndZ=0
    g5: LineSegment StartX=-165.477 StartY=-47.2177 StartZ=0 EndX=-170.297 EndY=-62.0542 EndZ=0
    g6: LineSegment StartX=-176.194 StartY=-60.1383 StartZ=0 EndX=-170.297 EndY=-62.0542 EndZ=0
  constraints (19):
    c: Distance(g0,g-3) = 72
    c: Distance(g0) = 15.6
    c: Tangent(g0,g-3)
    c: Coincident(g1,g0)
    c: Coincident(g2,g0)
    c: Distance(g1) = 2.4
    c: Distance(g2) = 3.8
    c: Perpendicular(g0,g1)
    c: Perpendicular(g0,g2)
    c: Coincident(g3,g2)
    c: Coincident(g3,g1)
    c: Equal(g4,g0)
    c: Equal(g5,g0)
    c: Parallel(g4,g0)
    c: Parallel(g5,g0)
    c: Coincident(g4,g2)
    c: Coincident(g5,g1)
    c: Coincident(g6,g4)
    c: Coincident(g6,g5)
FEATURE [Part::Extrusion] Extrude077  label="Extrude077 - scavo_nuovo_driver"
  Base = -> Sketch137
  Dir = (0,-1,2e-16)
  DirMode = 2
  FaceMakerClass = Part::FaceMakerBullseye
  FaceMakerMode = 3
  LengthFwd = 20.8
  LengthRev = 0
  Solid = true
  Symmetric = true
FEATURE [Sketcher::SketchObject] Sketch138  label="scavo_nuovo_driver_alto"
  ArcFitTolerance = 1e-06
  AttachmentSupport = -> [XZ_Plane]
  ExternalGeometry = -> [Sketch]
  FullyConstrained = true
  MakeInternals = false
  MapMode = 5
  Placement = pos=(0,0,0) rot=(1,0,0;1.5708rad)
  sketch-geometry (7):
    g0: LineSegment [constr] StartX=-188.796 StartY=17.7274 StartZ=0 EndX=-187.75 EndY=4.97025 EndZ=0
    g1: LineSegment StartX=-187.75 StartY=4.97025 StartZ=0 EndX=-189.743 EndY=4.8067 EndZ=0
    g2: LineSegment StartX=-187.75 StartY=4.97025 StartZ=0 EndX=-182.766 EndY=5.37913 EndZ=0
    g3: LineSegment StartX=-190.79 StartY=17.5638 StartZ=0 EndX=-189.743 EndY=4.8067 EndZ=0
    g4: LineSegment StartX=-183.813 StartY=18.1363 StartZ=0 EndX=-182.766 EndY=5.37913 EndZ=0
    g5: LineSegment StartX=-190.79 StartY=17.5638 StartZ=0 EndX=-188.796 EndY=17.7274 EndZ=0
    g6: LineSegment StartX=-188.796 StartY=17.7274 StartZ=0 EndX=-183.813 EndY=18.1363 EndZ=0
  constraints (20):
    c: Distance(g0) = 12.8
    c: DistanceY(g-3,g0) = 9
    c: PointOnObject(g0,g-4)
    c: PointOnObject(g0,g-4)
    c: Coincident(g1,g0)
    c: Coincident(g2,g0)
    c: Distance(g1) = 2
    c: Distance(g2) = 5
    c: Perpendicular(g0,g1)
    c: Perpendicular(g0,g2)
    c: Equal(g3,g0)
    c: Parallel(g3,g0)
    c: Coincident(g3,g1)
    c: Equal(g4,g0)
    c: Parallel(g4,g0)
    c: Coincident(g4,g2)
    c: Coincident(g5,g3)
    c: Coincident(g5,g0)
    c: Coincident(g6,g0)
    c: Coincident(g6,g4)
FEATURE [Part::Extrusion] Extrude078  label="Extrude078 - scavo_nuovo_driver_alto"
  Base = -> Sketch138
  Dir = (0,-1,2e-16)
  DirMode = 2
  FaceMakerClass = Part::FaceMakerBullseye
  FaceMakerMode = 3
  LengthFwd = 16.6
  LengthRev = 0
  Solid = true
  Symmetric = true
FEATURE [Sketcher::SketchObject] Sketch139  label="fermi_nuovo_driver_alto"
  ArcFitTolerance = 1e-06
  AttachmentSupport = -> [XZ_Plane]
  ExternalGeometry = -> [Sketch138,Sketch]
  FullyConstrained = true
  MakeInternals = false
  MapMode = 5
  Placement = pos=(0,0,0) rot=(1,0,0;1.5708rad)
  sketch-geometry (17):
    g0: LineSegment [constr] StartX=-188.314 StartY=16.4295 StartZ=0 EndX=-187.885 EndY=13.7638 EndZ=0
    g1: LineSegment [constr] StartX=-187.885 StartY=13.7638 StartZ=0 EndX=-187.456 EndY=11.0981 EndZ=0
    g2: LineSegment StartX=-187.885 StartY=13.7638 StartZ=0 EndX=-187.71 EndY=12.6778 EndZ=0
    g3: LineSegment StartX=-187.885 StartY=13.7638 StartZ=0 EndX=-188.06 EndY=14.8499 EndZ=0
    g4: LineSegment StartX=-187.71 StartY=12.6778 StartZ=0 EndX=-185.538 EndY=13.0274 EndZ=0
    g5: LineSegment StartX=-188.06 StartY=14.8499 StartZ=0 EndX=-185.888 EndY=15.1994 EndZ=0
    g6: LineSegment StartX=-185.888 StartY=15.1994 StartZ=0 EndX=-185.538 EndY=13.0274 EndZ=0
    g7: LineSegment StartX=-187.456 StartY=11.0981 StartZ=0 EndX=-189.035 EndY=10.8439 EndZ=0
    g8: LineSegment StartX=-188.314 StartY=16.4295 StartZ=0 EndX=-189.893 EndY=16.1753 EndZ=0
    g9: LineSegment StartX=-189.893 StartY=16.1753 StartZ=0 EndX=-189.035 EndY=10.8439 EndZ=0
    g10: LineSegment StartX=-187.456 StartY=11.0981 StartZ=0 EndX=-185.284 EndY=11.4477 EndZ=0
    g11: LineSegment StartX=-188.314 StartY=16.4295 StartZ=0 EndX=-186.142 EndY=16.7791 EndZ=0
    g12: LineSegment StartX=-184.308 StartY=15.4537 StartZ=0 EndX=-183.958 EndY=13.2816 EndZ=0
    g13: ArcOfCircle CenterX=-185.888 CenterY=15.1994 CenterZ=0 NormalX=0 NormalY=0 NormalZ=1 AngleXU=0 Radius=1.6 StartAngle=0.15957 EndAngle=1.73037
    g14: GeomPoint [constr] X=-184.562 Y=17.0333 Z=0
    g15: ArcOfCircle CenterX=-185.538 CenterY=13.0274 CenterZ=0 NormalX=0 NormalY=0 NormalZ=1 AngleXU=0 Radius=1.6 StartAngle=4.87196 EndAngle=6.44276
    g16: GeomPoint [constr] X=-183.704 Y=11.7019 Z=0
  constraints (43):
    c: Tangent(g1,g0) = -1.5708
    c: Distance(g0) = 2.7
    c: Equal(g1,g0)
    c: Tangent(g1,g-5)
    c: Coincident(g2,g0)
    c: Coincident(g3,g0)
    c: Distance(g2) = 1.1
    c: Equal(g3,g2)
    c: PointOnObject(g3,g2)
    c: Coincident(g4,g2)
    c: Coincident(g5,g3)
    c: Distance(g4) = 2.2
    c: Equal(g4,g5)
    c: Perpendicular(g1,g4)
    c: Perpendicular(g0,g5)
    c: Coincident(g6,g5)
    c: Coincident(g6,g4)
    c: Coincident(g7,g1)
    c: Coincident(g8,g0)
    c: Distance(g7) = 1.6
    c: Equal(g7,g8)
    c: Perpendicular(g1,g7)
    c: Perpendicular(g8,g0)
    c: Coincident(g9,g8)
    c: Coincident(g9,g7)
    c: Coincident(g10,g1)
    c: Coincident(g11,g0)
    c: Distance(g10,g16) = 3.8
    c: Perpendicular(g1,g10)
    c: Perpendicular(g1,g11)
    c: DistanceY(g0,g-4) = 3.8
    c: PointOnObject(g14,g12)
    c: PointOnObject(g14,g11)
    c: Tangent(g12,g13) = 1.5708
    c: Tangent(g11,g13) = 1.5708
    c: PointOnObject(g16,g12)
    c: PointOnObject(g16,g10)
    c: Tangent(g12,g15) = 1.5708
    c: Tangent(g10,g15) = -1.5708
    c: Equal(g13,g15)
    c: Coincident(g13,g5)
    c: Parallel(g2,g0)
    c: PointOnObject(g0,g-5)
FEATURE [Part::Extrusion] Extrude079  label="Extrude079 - fermi_nuovo_driver_alto"
  Base = -> Sketch139
  Dir = (0,-1,2e-16)
  DirMode = 2
  FaceMakerClass = Part::FaceMakerBullseye
  FaceMakerMode = 3
  LengthFwd = 25.2
  LengthRev = 0
  Solid = true
  Symmetric = true
FEATURE [Sketcher::SketchObject] Sketch140  label="scavo_diodo_nuovo_driver_alto"
  ArcFitTolerance = 1e-06
  AttachmentSupport = -> [XZ_Plane]
  ExternalGeometry = -> [Sketch138]
  FullyConstrained = true
  MakeInternals = false
  MapMode = 5
  Placement = pos=(0,0,0) rot=(1,0,0;1.5708rad)
  sketch-geometry (4):
    g0: LineSegment StartX=-190.79 StartY=17.5638 StartZ=0 EndX=-189.743 EndY=4.8067 EndZ=0
    g1: LineSegment StartX=-193.78 StartY=17.3185 StartZ=0 EndX=-192.733 EndY=4.56137 EndZ=0
    g2: LineSegment StartX=-190.79 StartY=17.5638 StartZ=0 EndX=-193.78 EndY=17.3185 EndZ=0
    g3: LineSegment StartX=-192.733 StartY=4.56137 StartZ=0 EndX=-189.743 EndY=4.8067 EndZ=0
  constraints (11):
    c: Equal(g0,g-3)
    c: Parallel(g0,g-3)
    c: Equal(g1,g-3)
    c: Parallel(g1,g-3)
    c: Coincident(g2,g0)
    c: Distance(g2) = 3
    c: Perpendicular(g0,g2)
    c: Coincident(g1,g2)
    c: Coincident(g3,g1)
    c: Coincident(g3,g0)
    c: Coincident(g0,g-3)
FEATURE [Part::Extrusion] Extrude080  label="Extrude080 - scavo_diodo_nuovo_driver_alto"
  Base = -> Sketch140
  Dir = (0,-1,2e-16)
  DirMode = 2
  FaceMakerClass = Part::FaceMakerBullseye
  FaceMakerMode = 3
  LengthFwd = 4
  LengthRev = 0
  Placement = pos=(0,7.8,0) rot=(0,0,1;0rad)
  Solid = true
  Symmetric = false
FEATURE [Part::MultiFuse] Fusion001
  Refine = true
  Shapes = -> [Cut043,Extrude079]
FEATURE [Part::Cut] Cut044
  Base = -> Fusion001
  Refine = true
  Tool = -> Extrude078
FEATURE [Part::Cut] Cut045
  Base = -> Cut044
  Refine = true
  Tool = -> Extrude080
FEATURE [Sketcher::SketchObject] Sketch141  label="fermi_nuovo_driver"
  ArcFitTolerance = 1e-06
  AttachmentSupport = -> [XZ_Plane]
  ExternalGeometry = -> [Sketch,Sketch137]
  FullyConstrained = true
  MakeInternals = false
  MapMode = 5
  Placement = pos=(0,0,0) rot=(1,0,0;1.5708rad)
  sketch-geometry (16):
    g0: LineSegment [constr] StartX=-165.477 StartY=-47.2177 StartZ=0 EndX=-167.759 EndY=-46.4761 EndZ=0
    g1: LineSegment [constr] StartX=-167.759 StartY=-46.4761 StartZ=0 EndX=-168.006 EndY=-47.2369 EndZ=0
    g2: LineSegment [constr] StartX=-168.006 StartY=-47.2369 StartZ=0 EndX=-169.675 EndY=-52.3726 EndZ=0
    g3: LineSegment StartX=-169.675 StartY=-52.3726 StartZ=0 EndX=-171.767 EndY=-51.6928 EndZ=0
    g4: LineSegment StartX=-172.795 StartY=-49.6767 StartZ=0 EndX=-172.115 EndY=-47.5843 EndZ=0
    g5: LineSegment StartX=-170.099 StartY=-46.5571 StartZ=0 EndX=-166.485 EndY=-47.7313 EndZ=0
    g6: LineSegment StartX=-166.485 StartY=-47.7313 StartZ=0 EndX=-168.153 EndY=-52.867 EndZ=0
    g7: LineSegment StartX=-169.675 StartY=-52.3726 StartZ=0 EndX=-168.153 EndY=-52.867 EndZ=0
    g8: LineSegment StartX=-170.593 StartY=-48.0788 StartZ=0 EndX=-171.273 EndY=-50.1711 EndZ=0
    g9: LineSegment StartX=-171.273 StartY=-50.1711 StartZ=0 EndX=-169.181 EndY=-50.8509 EndZ=0
    g10: LineSegment StartX=-169.181 StartY=-50.8509 StartZ=0 EndX=-168.501 EndY=-48.7586 EndZ=0
    g11: LineSegment StartX=-168.501 StartY=-48.7586 StartZ=0 EndX=-170.593 EndY=-48.0788 EndZ=0
    g12: ArcOfCircle CenterX=-170.593 CenterY=-48.0788 CenterZ=0 NormalX=0 NormalY=0 NormalZ=1 AngleXU=0 Radius=1.6 StartAngle=1.25664 EndAngle=2.82743
    g13: GeomPoint [constr] X=-171.62 Y=-46.0626 Z=0
    g14: ArcOfCircle CenterX=-171.273 CenterY=-50.1711 CenterZ=0 NormalX=0 NormalY=0 NormalZ=1 AngleXU=0 Radius=1.6 StartAngle=2.82743 EndAngle=4.39823
    g15: GeomPoint [constr] X=-173.289 Y=-51.1984 Z=0
  constraints (41):
    c: Coincident(g0,g-4)
    c: PointOnObject(g0,g-3)
    c: Parallel(g0,g-4)
    c: Coincident(g1,g0)
    c: Parallel(g1,g-3)
    c: Distance(g1) = 0.8
    c: Coincident(g2,g1)
    c: Distance(g2) = 5.4
    c: Coincident(g3,g2)
    c: Parallel(g2,g-3)
    c: Distance(g15,g13) = 5.4
    c: Perpendicular(g3,g2)
    c: Parallel(g4,g2)
    c: Distance(g5,g13) = 5.4
    c: Distance(g3,g15) = 3.8
    c: Perpendicular(g4,g5)
    c: Coincident(g6,g5)
    c: Distance(g6) = 5.4
    c: Parallel(g6,g4)
    c: Coincident(g7,g2)
    c: Coincident(g7,g6)
    c: Coincident(g8,g9)
    c: Coincident(g9,g10)
    c: Coincident(g10,g11)
    c: Coincident(g11,g8)
    c: Distance(g8,g10) = 2.2
    c: Distance(g9,g11) = 2.2
    c: Perpendicular(g11,g8)
    c: Equal(g8,g10)
    c: Equal(g11,g9)
    c: Tangent(g10,g2)
    c: Distance(g10,g1) = 1.6
    c: PointOnObject(g13,g4)
    c: PointOnObject(g13,g5)
    c: Tangent(g4,g12) = 1.5708
    c: Tangent(g5,g12) = 1.5708
    c: PointOnObject(g15,g4)
    c: Tangent(g4,g14) = 1.5708
    c: Tangent(g3,g14) = 1.5708
    c: Equal(g14,g12)
    c: Coincident(g12,g8)
FEATURE [Part::Extrusion] Extrude081  label="Extrude081 - fermi_nuovo_driver"
  Base = -> Sketch141
  Dir = (0,-1,2e-16)
  DirMode = 2
  FaceMakerClass = Part::FaceMakerBullseye
  FaceMakerMode = 3
  LengthFwd = 25.2
  LengthRev = 0
  Solid = true
  Symmetric = true
FEATURE [Part::MultiFuse] Fusion002
  Refine = true
  Shapes = -> [Cut045,Extrude081]
FEATURE [Part::Cut] Cut046
  Base = -> Fusion002
  Refine = true
  Tool = -> Extrude077
FEATURE [Sketcher::SketchObject] Sketch142  label="fermi_rele"
  ArcFitTolerance = 1e-06
  AttachmentSupport = -> [XZ_Plane]
  ExternalGeometry = -> [Sketch,Sketch136]
  FullyConstrained = true
  MakeInternals = false
  MapMode = 5
  Placement = pos=(0,0,0) rot=(1,0,0;1.5708rad)
  sketch-geometry (15):
    g0: LineSegment StartX=-177.245 StartY=-63.3719 StartZ=0 EndX=-177.924 EndY=-65.4642 EndZ=0
    g1: LineSegment StartX=-175.228 StartY=-62.3446 StartZ=0 EndX=-171.614 EndY=-63.5189 EndZ=0
    g2: LineSegment StartX=-171.614 StartY=-63.5189 StartZ=0 EndX=-173.283 EndY=-68.6546 EndZ=0
    g3: LineSegment StartX=-176.897 StartY=-67.4803 StartZ=0 EndX=-173.283 EndY=-68.6546 EndZ=0
    g4: LineSegment StartX=-175.723 StartY=-63.8663 StartZ=0 EndX=-173.631 EndY=-64.5461 EndZ=0
    g5: LineSegment StartX=-175.723 StartY=-63.8663 StartZ=0 EndX=-176.403 EndY=-65.9586 EndZ=0
    g6: LineSegment StartX=-173.631 StartY=-64.5461 StartZ=0 EndX=-174.31 EndY=-66.6385 EndZ=0
    g7: LineSegment StartX=-176.403 StartY=-65.9586 StartZ=0 EndX=-174.31 EndY=-66.6385 EndZ=0
    g8: LineSegment [constr] StartX=-173.631 StartY=-64.5461 StartZ=0 EndX=-173.136 EndY=-63.0245 EndZ=0
    g9: LineSegment [constr] StartX=-173.631 StartY=-64.5461 StartZ=0 EndX=-172.109 EndY=-65.0406 EndZ=0
    g10: LineSegment [constr] StartX=-170.35 StartY=-63.5093 StartZ=0 EndX=-173.013 EndY=-62.644 EndZ=0
    g11: ArcOfCircle CenterX=-175.723 CenterY=-63.8663 CenterZ=0 NormalX=0 NormalY=0 NormalZ=1 AngleXU=0 Radius=1.6 StartAngle=1.25664 EndAngle=2.82743
    g12: GeomPoint [constr] X=-176.75 Y=-61.8502 Z=0
    g13: ArcOfCircle CenterX=-176.403 CenterY=-65.9586 CenterZ=0 NormalX=0 NormalY=0 NormalZ=1 AngleXU=0 Radius=1.6 StartAngle=2.82743 EndAngle=4.39823
    g14: GeomPoint [constr] X=-178.419 Y=-66.9859 Z=0
  constraints (39):
    c: Distance(g14,g12) = 5.4
    c: Distance(g1,g12) = 5.4
    c: Perpendicular(g1,g0)
    c: Coincident(g2,g1)
    c: Parallel(g2,g0)
    c: Coincident(g3,g2)
    c: Parallel(g2,g-3)
    c: Coincident(g5,g4)
    c: Distance(g5) = 2.2
    c: Distance(g4) = 2.2
    c: Perpendicular(g4,g5)
    c: Coincident(g6,g4)
    c: Equal(g6,g5)
    c: Parallel(g6,g5)
    c: Coincident(g7,g5)
    c: Coincident(g7,g6)
    c: Coincident(g8,g4)
    c: Coincident(g9,g4)
    c: Distance(g8) = 1.6
    c: Distance(g9) = 1.6
    c: Parallel(g8,g6)
    c: Parallel(g9,g4)
    c: PointOnObject(g8,g1)
    c: PointOnObject(g9,g2)
    c: Coincident(g10,g-4)
    c: Parallel(g10,g-4)
    c: PointOnObject(g10,g-3)
    c: Tangent(g6,g-3) = 1.5708
    c: Distance(g4,g10) = 2
    c: PointOnObject(g12,g1)
    c: Tangent(g1,g11) = 1.5708
    c: Tangent(g0,g11) = -1.5708
    c: PointOnObject(g14,g3)
    c: PointOnObject(g14,g0)
    c: Tangent(g3,g13) = -1.5708
    c: Tangent(g0,g13) = -1.5708
    c: Equal(g11,g13)
    c: Coincident(g11,g4)
    c: Parallel(g3,g1)
FEATURE [Part::Extrusion] Extrude082  label="Extrude082 - fermi_rele"
  Base = -> Sketch142
  Dir = (0,-1,2e-16)
  DirMode = 2
  FaceMakerClass = Part::FaceMakerBullseye
  FaceMakerMode = 3
  LengthFwd = 25.2
  LengthRev = 0
  Solid = true
  Symmetric = true
FEATURE [Part::MultiFuse] Fusion003
  Refine = true
  Shapes = -> [Cut046,Extrude082]
FEATURE [Part::Cut] Cut047
  Base = -> Fusion003
  Refine = true
  Tool = -> Extrude076
FEATURE [Sketcher::SketchObject] Sketch143  label="foro_passaggio_cavi_led_batteria"
  ArcFitTolerance = 1e-06
  AttachmentSupport = -> [XZ_Plane]
  ExternalGeometry = -> [Sketch,Sketch042,Sketch036]
  FullyConstrained = true
  MakeInternals = false
  MapMode = 5
  Placement = pos=(0,0,0) rot=(1,0,0;1.5708rad)
  sketch-geometry (4):
    g0: LineSegment StartX=-207.775 StartY=-41.3701 StartZ=0 EndX=-213.607 EndY=-53.8767 EndZ=0
    g1: LineSegment StartX=-213.607 StartY=-53.8767 StartZ=0 EndX=-211.843 EndY=-59.5559 EndZ=0
    g2: LineSegment StartX=-207.775 StartY=-41.3701 StartZ=0 EndX=-207.775 EndY=-50.8316 EndZ=0
    g3: LineSegment StartX=-207.775 StartY=-50.8316 StartZ=0 EndX=-211.843 EndY=-59.5559 EndZ=0
  constraints (9):
    c: Coincident(g0,g-3)
    c: PointOnObject(g1,g-6)
    c: Coincident(g1,g0)
    c: Coincident(g2,g0)
    c: Coincident(g2,g-7)
    c: Coincident(g3,g2)
    c: Parallel(g3,g0)
    c: Coincident(g3,g1)
    c: Coincident(g0,g-5)
FEATURE [Part::Extrusion] Extrude083  label="Extrude083 - foro_passaggio_cavi_led_batteria"
  Base = -> Sketch143
  Dir = (0,-1,2e-16)
  DirMode = 2
  FaceMakerClass = Part::FaceMakerBullseye
  FaceMakerMode = 3
  LengthFwd = 6
  LengthRev = 0
  Solid = true
  Symmetric = true
FEATURE [Part::Cut] Cut048
  Base = -> Cut047
  Refine = true
  Tool = -> Extrude083
FEATURE [Sketcher::SketchObject] Sketch144  label="foro_areazione_alimentatore"
  ArcFitTolerance = 1e-06
  AttachmentSupport = -> [XZ_Plane]
  ExternalGeometry = -> [Sketch036]
  FullyConstrained = true
  MakeInternals = false
  MapMode = 5
  Placement = pos=(0,0,0) rot=(1,0,0;1.5708rad)
  sketch-geometry (4):
    g0: LineSegment StartX=-211.843 StartY=-60.3701 StartZ=0 EndX=-207.775 EndY=-60.3701 EndZ=0
    g1: LineSegment StartX=-207.775 StartY=-60.3701 StartZ=0 EndX=-207.775 EndY=-70.3701 EndZ=0
    g2: LineSegment StartX=-211.843 StartY=-60.3701 StartZ=0 EndX=-211.843 EndY=-70.3701 EndZ=0
    g3: LineSegment StartX=-207.775 StartY=-70.3701 StartZ=0 EndX=-211.843 EndY=-70.3701 EndZ=0
  constraints (11):
    c: Horizontal(g0)
    c: Distance(g1) = 10
    c: Coincident(g1,g0)
    c: Tangent(g1,g-3)
    c: PointOnObject(g0,g-4)
    c: Coincident(g2,g0)
    c: PointOnObject(g2,g-4)
    c: Coincident(g3,g1)
    c: Horizontal(g3)
    c: Coincident(g3,g2)
    c: DistanceY(g0,g-3) = 19
FEATURE [Part::Extrusion] Extrude084  label="Extrude084 - foro_areazione_alimentatore"
  Base = -> Sketch144
  Dir = (0,-1,2e-16)
  DirMode = 2
  FaceMakerClass = Part::FaceMakerBullseye
  FaceMakerMode = 3
  LengthFwd = 10
  LengthRev = 0
  Solid = true
  Symmetric = true
FEATURE [Part::Cut] Cut049
  Base = -> Cut048
  Refine = true
  Tool = -> Extrude084
FEATURE [Sketcher::SketchObject] Sketch145  label="foro_per_condesatore"
  ArcFitTolerance = 1e-06
  AttachmentSupport = -> [XZ_Plane]
  ExternalGeometry = -> [Sketch,Sketch139]
  FullyConstrained = true
  MakeInternals = false
  MapMode = 5
  Placement = pos=(0,0,0) rot=(1,0,0;1.5708rad)
  sketch-geometry (1):
    g0: Circle CenterX=-182.345 CenterY=7.02342 CenterZ=0 NormalX=0 NormalY=0 NormalZ=1 AngleXU=0 Radius=5.2
  constraints (3):
    c: Diameter(g0) = 10.4
    c: Tangent(g0,g-3)
    c: Tangent(g0,g-4)
FEATURE [Part::Extrusion] Extrude085  label="Extrude085 - foro_per_condesatore"
  Base = -> Sketch145
  Dir = (0,-1,2e-16)
  DirMode = 2
  FaceMakerClass = Part::FaceMakerBullseye
  FaceMakerMode = 3
  LengthFwd = 25.2
  LengthRev = 0
  Solid = true
  Symmetric = true
FEATURE [Part::Cut] Cut050
  Base = -> Cut049
  Refine = true
  Tool = -> Extrude085
FEATURE [Sketcher::SketchObject] Sketch146  label="scavo_pulsante_6x6_per_led_batteria"
  ArcFitTolerance = 1e-06
  AttachmentSupport = -> [XZ_Plane]
  ExternalGeometry = -> [Sketch016]
  FullyConstrained = true
  MakeInternals = false
  MapMode = 5
  Placement = pos=(0,0,0) rot=(1,0,0;1.5708rad)
  sketch-geometry (4):
    g0: LineSegment StartX=-217.243 StartY=-66.0316 StartZ=0 EndX=-217.243 EndY=-72.8316 EndZ=0
    g1: LineSegment StartX=-217.243 StartY=-72.8316 StartZ=0 EndX=-211.043 EndY=-72.8316 EndZ=0
    g2: LineSegment StartX=-211.043 StartY=-72.8316 StartZ=0 EndX=-211.043 EndY=-66.0316 EndZ=0
    g3: LineSegment StartX=-211.043 StartY=-66.0316 StartZ=0 EndX=-217.243 EndY=-66.0316 EndZ=0
  constraints (12):
    c: Coincident(g0,g1)
    c: Coincident(g1,g2)
    c: Coincident(g2,g3)
    c: Coincident(g3,g0)
    c: Vertical(g0)
    c: Vertical(g2)
    c: Horizontal(g1)
    c: Horizontal(g3)
    c: Distance(g0,g2) = 6.2
    c: Distance(g1,g3) = 6.8
    c: Tangent(g1,g-3)
    c: DistanceX(g0,g-3) = 3.8
FEATURE [Part::Extrusion] Extrude086  label="Extrude086 - scavo_pulsante_6x6_per_led_batteria"
  Base = -> Sketch146
  Dir = (0,-1,2e-16)
  DirMode = 2
  FaceMakerClass = Part::FaceMakerBullseye
  FaceMakerMode = 3
  LengthFwd = 4.2
  LengthRev = 0
  Placement = pos=(0,12.6,0) rot=(0,0,1;0rad)
  Solid = true
  Symmetric = false
FEATURE [Sketcher::SketchObject] Sketch147  label="scavo_led_stato_batteria"
  ArcFitTolerance = 1e-06
  AttachmentSupport = -> [XZ_Plane]
  ExternalGeometry = -> [Sketch016]
  FullyConstrained = true
  MakeInternals = false
  MapMode = 5
  Placement = pos=(0,0,0) rot=(1,0,0;1.5708rad)
  sketch-geometry (5):
    g0: LineSegment StartX=-215.743 StartY=-56.6316 StartZ=0 EndX=-215.743 EndY=-65.8316 EndZ=0
    g1: LineSegment StartX=-215.743 StartY=-65.8316 StartZ=0 EndX=-211.143 EndY=-65.8316 EndZ=0
    g2: LineSegment StartX=-211.143 StartY=-65.8316 StartZ=0 EndX=-211.143 EndY=-56.6316 EndZ=0
    g3: LineSegment StartX=-211.143 StartY=-56.6316 StartZ=0 EndX=-215.743 EndY=-56.6316 EndZ=0
    g4: GeomPoint [constr] X=-213.443 Y=-61.2316 Z=0
  constraints (13):
    c: Coincident(g0,g1)
    c: Coincident(g1,g2)
    c: Coincident(g2,g3)
    c: Coincident(g3,g0)
    c: Distance(g0,g2) = 4.6
    c: Distance(g1,g3) = 9.2
    c: Equal(g0,g2)
    c: Equal(g1,g3)
    c: Perpendicular(g3,g0)
    c: DistanceY(g-3,g0) = 11
    c: Vertical(g2)
    c: Symmetric(g0,g2,g4)
    c: Vertical(g4,g-3)
FEATURE [PartDesign::Body] Body  label="Struttura pistola"
  AllowCompound = false
  Group = -> [Sketch,Sketch002,Sketch004,DatumPlane,Sketch005,DatumPlane001,CopyCut,Sketch008,Sketch009,Sketch010,Sketch011,Sketch012,Sketch013,Sketch014,Sketch015,Sketch016,Sketch017,Sketch018,Sketch019,Sketch020,Sketch022,Sketch023,Sketch024,Sketch025,Sketch026,Sketch027,Sketch029,Sketch030,Sketch031,Sketch032,Sketch033,Sketch034,Sketch035,Sketch036,Sketch037,Sketch038,Sketch039,Sketch040,Sketch041,Sketch042,+27 more]
  Origin = -> Origin
FEATURE [Part::Extrusion] Extrude087  label="Extrude087 - scavo_led_stato_batteria"
  Base = -> Sketch147
  Dir = (0,-1,2e-16)
  DirMode = 2
  FaceMakerClass = Part::FaceMakerBullseye
  FaceMakerMode = 3
  LengthFwd = 2
  LengthRev = 0
  Placement = pos=(0,12.6,0) rot=(0,0,1;0rad)
  Solid = true
  Symmetric = false
FEATURE [Part::Cut] Cut051
  Base = -> Cut050
  Refine = true
  Tool = -> Extrude086
FEATURE [Part::Cut] Cut052
  Base = -> Cut051
  Refine = true
  Tool = -> Extrude087
FEATURE [Sketcher::SketchObject] Sketch148
  ArcFitTolerance = 1e-06
  AttachmentSupport = -> [Pad016]
  ExternalGeometry = -> [Pad016]
  FullyConstrained = true
  MakeInternals = false
  MapMode = 5
  Placement = pos=(0,0,-80.4316) rot=(1,0,0;3.14159rad)
  sketch-geometry (8):
    g0: LineSegment StartX=-176.685 StartY=3.6 StartZ=0 EndX=-186.685 EndY=3.6 EndZ=0
    g1: LineSegment StartX=-176.685 StartY=3.6 StartZ=0 EndX=-176.685 EndY=-9e-16 EndZ=0
    g2: LineSegment [constr] StartX=-186.685 StartY=3.6 StartZ=0 EndX=-186.685 EndY=-9e-16 EndZ=0
    g3: ArcOfEllipse CenterX=-186.685 CenterY=-1e-15 CenterZ=0 NormalX=0 NormalY=0 NormalZ=1 MajorRadius=10 MinorRadius=3.6 AngleXU=0 StartAngle=0 EndAngle=1.5708
    g4: LineSegment [constr] StartX=-176.685 StartY=-1e-15 StartZ=0 EndX=-196.685 EndY=-1e-15 EndZ=0
    g5: LineSegment [constr] StartX=-186.685 StartY=3.6 StartZ=0 EndX=-186.685 EndY=-3.6 EndZ=0
    g6: GeomPoint [constr] X=-177.356 Y=-1e-15 Z=0
    g7: GeomPoint [constr] X=-196.015 Y=-1e-15 Z=0
  constraints (13):
    c: Distance(g0) = 10
    c: Coincident(g0,g-5)
    c: PointOnObject(g0,g-3)
    c: Coincident(g1,g0)
    c: Coincident(g1,g-5)
    c: Coincident(g2,g0)
    c: Vertical(g2)
    c: PointOnObject(g2,g-4)
    c: InternalAlignment(g4-g7 -> g3) x4
    c: Coincident(g3,g2)
    c: Coincident(g3,g0)
    c: Coincident(g3,g1)
    c: Horizontal(g4)
FEATURE [PartDesign::SubtractivePipe] SubtractivePipe004
  AuxilleryCurvelinear = true
  AuxillerySpineTangent = false
  BaseFeature = -> Pad016
  Binormal = (0,0,0)
  Mode = 0
  Profile = -> Sketch148
  Refine = true
  Spine = -> Pad016 [Edge254]
  SpineTangent = false
  Suppressed = false
  Transformation = 0
  Transition = 0
FEATURE [Sketcher::SketchObject] Sketch149
  ArcFitTolerance = 1e-06
  AttachmentSupport = -> [Pad016]
  ExternalGeometry = -> [Pad016]
  FullyConstrained = true
  MakeInternals = false
  MapMode = 5
  Placement = pos=(0,0,-80.4316) rot=(1,0,0;3.14159rad)
  sketch-geometry (8):
    g0: LineSegment StartX=-215.932 StartY=3.6 StartZ=0 EndX=-205.932 EndY=3.6 EndZ=0
    g1: LineSegment StartX=-215.932 StartY=3.6 StartZ=0 EndX=-215.932 EndY=-4e-16 EndZ=0
    g2: LineSegment [constr] StartX=-205.932 StartY=3.6 StartZ=0 EndX=-205.932 EndY=-9e-16 EndZ=0
    g3: ArcOfEllipse CenterX=-205.932 CenterY=-1e-15 CenterZ=0 NormalX=0 NormalY=0 NormalZ=1 MajorRadius=10 MinorRadius=3.6 AngleXU=-3.14159 StartAngle=4.71239 EndAngle=6.28319
    g4: LineSegment [constr] StartX=-215.932 StartY=-1e-15 StartZ=0 EndX=-195.932 EndY=-1e-15 EndZ=0
    g5: LineSegment [constr] StartX=-205.932 StartY=-3.6 StartZ=0 EndX=-205.932 EndY=3.6 EndZ=0
    g6: GeomPoint [constr] X=-215.262 Y=-1.1e-15 Z=0
    g7: GeomPoint [constr] X=-196.602 Y=-9e-16 Z=0
  constraints (13):
    c: Distance(g0) = 10
    c: Coincident(g0,g-5)
    c: PointOnObject(g0,g-5)
    c: Coincident(g1,g0)
    c: Coincident(g1,g-4)
    c: Coincident(g2,g0)
    c: Vertical(g2)
    c: PointOnObject(g2,g-3)
    c: InternalAlignment(g4-g7 -> g3) x4
    c: Coincident(g3,g2)
    c: Coincident(g3,g0)
    c: Coincident(g3,g1)
    c: Horizontal(g4)
FEATURE [PartDesign::SubtractivePipe] SubtractivePipe005
  AuxilleryCurvelinear = true
  AuxillerySpineTangent = false
  BaseFeature = -> SubtractivePipe004
  Binormal = (0,0,0)
  Mode = 0
  Profile = -> Sketch149
  Refine = true
  Spine = -> Pad016 [Edge256,Edge251,Edge252]
  SpineTangent = false
  Suppressed = false
  Transformation = 0
  Transition = 0
FEATURE [PartDesign::SubtractiveLoft] SubtractiveLoft002
  BaseFeature = -> SubtractivePipe005
  Closed = false
  Profile = -> Sketch129
  Refine = true
  Ruled = false
  Sections = -> [Sketch130]
  Suppressed = false
FEATURE [PartDesign::SubtractiveLoft] SubtractiveLoft003
  BaseFeature = -> SubtractiveLoft002
  Closed = false
  Profile = -> Clone2D001
  Refine = true
  Ruled = false
  Sections = -> [Sketch131]
  Suppressed = false
FEATURE [PartDesign::Chamfer] Chamfer010
  Angle = 45
  Base = -> SubtractiveLoft003 [Edge203,Edge204,Edge202,Edge201,Edge195]
  BaseFeature = -> SubtractiveLoft003
  ChamferType = 0
  FlipDirection = false
  Refine = true
  Size = 1.5
  Size2 = 1
  SupportTransform = false
  Suppressed = false
  UseAllEdges = false
FEATURE [PartDesign::Chamfer] Chamfer011
  Angle = 45
  Base = -> Chamfer010 [Edge15]
  BaseFeature = -> Chamfer010
  ChamferType = 0
  FlipDirection = false
  Refine = true
  Size = 1.6
  Size2 = 1
  SupportTransform = false
  Suppressed = false
  UseAllEdges = false
FEATURE [PartDesign::Chamfer] Chamfer012
  Angle = 45
  Base = -> Chamfer011 [Edge10]
  BaseFeature = -> Chamfer011
  ChamferType = 0
  FlipDirection = false
  Refine = true
  Size = 3.5
  Size2 = 1
  SupportTransform = false
  Suppressed = false
  UseAllEdges = false
FEATURE [PartDesign::Chamfer] Chamfer013
  Angle = 45
  Base = -> Chamfer012 [Edge94]
  BaseFeature = -> Chamfer012
  ChamferType = 0
  FlipDirection = false
  Refine = true
  Size = 1.9
  Size2 = 1
  SupportTransform = false
  Suppressed = false
  UseAllEdges = false
FEATURE [PartDesign::Fillet] Fillet007
  Base = -> Chamfer013 [Edge83]
  BaseFeature = -> Chamfer013
  Radius = 1.1
  Refine = true
  SupportTransform = false
  Suppressed = false
  UseAllEdges = false
FEATURE [PartDesign::Fillet] Fillet008
  Base = -> Fillet007 [Edge75]
  BaseFeature = -> Fillet007
  Radius = 1.9
  Refine = true
  SupportTransform = false
  Suppressed = false
  UseAllEdges = false
FEATURE [PartDesign::Pocket] Pocket011
  BaseFeature = -> Fillet008
  Direction = (0,1,-2e-16)
  Length = 0.8
  Length2 = 5
  Profile = -> Sketch132
  ReferenceAxis = -> Sketch132 [N_Axis]
  Refine = true
  Suppressed = false
  Type = 0
FEATURE [PartDesign::Pocket] Pocket012
  BaseFeature = -> Pocket011
  Direction = (0,1,0)
  Length = 1
  Length2 = 5
  Profile = -> ShapeString
  ReferenceAxis = -> ShapeString [N_Axis]
  Refine = true
  Suppressed = false
  Type = 0
FEATURE [PartDesign::Body] Body007  label="lato DX"
  AllowCompound = false
  Group = -> [Binder001,Sketch114,Pad011,Chamfer014,Sketch115,Pocket006,Sketch116,Pad012,Sketch117,Pocket007,Sketch118,Pad013,Sketch119,Pocket008,Pad017,Chamfer009,Pocket009,Sketch123,Sketch120,Pad014,Pad018,Chamfer008,Pocket010,Sketch121,Pad015,Sketch122,Pad016,SubtractivePipe004,SubtractivePipe005,Sketch149,Sketch148,Sketch124,Sketch125,Sketch126,Sketch129,Sketch130,Clone2D001,Sketch131,SubtractiveLoft002,+11 more]
  Origin = -> Origin007
  Tip = -> Pocket012
FEATURE [Sketcher::SketchObject] Sketch150
  ArcFitTolerance = 1e-06
  AttachmentSupport = -> [Pad008]
  ExternalGeometry = -> [Pad008]
  FullyConstrained = true
  MakeInternals = false
  MapMode = 5
  Placement = pos=(0,3.6,0) rot=(0,0.707107,0.707107;3.14159rad)
  sketch-geometry (7):
    g0: LineSegment [constr] StartX=211.043 StartY=-66.0316 StartZ=0 EndX=211.043 EndY=-72.8316 EndZ=0
    g1: LineSegment [constr] StartX=211.043 StartY=-72.8316 StartZ=0 EndX=217.243 EndY=-72.8316 EndZ=0
    g2: LineSegment [constr] StartX=217.243 StartY=-72.8316 StartZ=0 EndX=217.243 EndY=-66.0316 EndZ=0
    g3: LineSegment [constr] StartX=217.243 StartY=-66.0316 StartZ=0 EndX=211.043 EndY=-66.0316 EndZ=0
    g4: LineSegment [constr] StartX=211.043 StartY=-72.8316 StartZ=0 EndX=217.243 EndY=-66.0316 EndZ=0
    g5: LineSegment [constr] StartX=211.043 StartY=-66.0316 StartZ=0 EndX=214.143 EndY=-69.4316 EndZ=0
    g6: Circle CenterX=214.143 CenterY=-69.4316 CenterZ=0 NormalX=0 NormalY=0 NormalZ=1 AngleXU=0 Radius=2
  constraints (18):
    c: Coincident(g0,g1)
    c: Coincident(g1,g2)
    c: Coincident(g2,g3)
    c: Coincident(g3,g0)
    c: Vertical(g0)
    c: Vertical(g2)
    c: Horizontal(g1)
    c: Horizontal(g3)
    c: Distance(g0,g2) = 6.2
    c: Distance(g1,g3) = 6.8
    c: DistanceY(g-3,g1) = 4
    c: DistanceX(g-3,g1) = 3.8
    c: Coincident(g4,g0)
    c: Coincident(g4,g2)
    c: Coincident(g5,g0)
    c: Symmetric(g0,g2,g5)
    c: Diameter(g6) = 4
    c: Coincident(g6,g5)
FEATURE [Sketcher::SketchObject] Sketch151
  ArcFitTolerance = 1e-06
  AttachmentSupport = -> [Pad008]
  ExternalGeometry = -> [Pad008]
  FullyConstrained = true
  MakeInternals = false
  MapMode = 5
  Placement = pos=(0,3.6,0) rot=(0,0.707107,0.707107;3.14159rad)
  sketch-geometry (10):
    g0: LineSegment [constr] StartX=211.143 StartY=-56.6316 StartZ=0 EndX=211.143 EndY=-65.8316 EndZ=0
    g1: LineSegment [constr] StartX=211.143 StartY=-65.8316 StartZ=0 EndX=215.743 EndY=-65.8316 EndZ=0
    g2: LineSegment [constr] StartX=215.743 StartY=-65.8316 StartZ=0 EndX=215.743 EndY=-56.6316 EndZ=0
    g3: LineSegment [constr] StartX=215.743 StartY=-56.6316 StartZ=0 EndX=211.143 EndY=-56.6316 EndZ=0
    g4: LineSegment StartX=212.243 StartY=-63.4316 StartZ=0 EndX=214.643 EndY=-63.4316 EndZ=0
    g5: LineSegment StartX=214.643 StartY=-63.4316 StartZ=0 EndX=214.643 EndY=-57.0316 EndZ=0
    g6: LineSegment StartX=214.643 StartY=-57.0316 StartZ=0 EndX=212.243 EndY=-57.0316 EndZ=0
    g7: LineSegment StartX=212.243 StartY=-57.0316 StartZ=0 EndX=212.243 EndY=-63.4316 EndZ=0
    g8: GeomPoint [constr] X=213.443 Y=-60.2316 Z=0
    g9: GeomPoint [constr] X=213.443 Y=-61.2316 Z=0
  constraints (26):
    c: Coincident(g0,g1)
    c: Coincident(g1,g2)
    c: Coincident(g2,g3)
    c: Coincident(g3,g0)
    c: Vertical(g0)
    c: Vertical(g2)
    c: Horizontal(g1)
    c: Horizontal(g3)
    c: Distance(g0,g2) = 4.6
    c: Distance(g1,g3) = 9.2
    c: DistanceY(g-3,g1) = 11
    c: Coincident(g4,g5)
    c: Coincident(g5,g6)
    c: Coincident(g6,g7)
    c: Coincident(g7,g4)
    c: Horizontal(g4)
    c: Horizontal(g6)
    c: Vertical(g5)
    c: Vertical(g7)
    c: Symmetric(g6,g4,g8)
    c: Distance(g5,g7) = 2.4
    c: Distance(g4,g6) = 6.4
    c: Symmetric(g2,g0,g9)
    c: Vertical(g8,g9)
    c: DistanceY(g1,g4) = 2.4
    c: Vertical(g9,g-3)
FEATURE [PartDesign::Pocket] Pocket019
  BaseFeature = -> Pocket013
  Direction = (0,-1,2e-16)
  Length = 3.6
  Length2 = 5
  Profile = -> Sketch151
  ReferenceAxis = -> Sketch151 [N_Axis]
  Refine = true
  Suppressed = false
  Type = 0
FEATURE [PartDesign::Pocket] Pocket018
  BaseFeature = -> Pocket019
  Direction = (0,-1,2e-16)
  Length = 3.6
  Length2 = 5
  Profile = -> Sketch150
  ReferenceAxis = -> Sketch150 [N_Axis]
  Refine = true
  Suppressed = false
  Type = 0
FEATURE [PartDesign::Point] DatumPoint
  AttacherType = Attacher::AttachEnginePoint
  AttachmentSupport = -> [Sketch150]
  MapMode = 36
  Placement = pos=(-214.143,3.6,-69.4316) rot=(0,1,0;3.14159rad)
FEATURE [PartDesign::Plane] DatumPlane002
  AttachmentSupport = -> [DatumPoint]
  Length = 265.655
  MapMode = 1
  Placement = pos=(-214.143,3.6,-69.4316) rot=(0,0,1;0rad)
  ResizeMode = 0
  Width = 72.0719
FEATURE [Sketcher::SketchObject] Sketch152
  ArcFitTolerance = 1e-06
  AttachmentSupport = -> [DatumPlane002]
  ExternalGeometry = -> [Sketch150]
  FullyConstrained = true
  MakeInternals = false
  MapMode = 5
  Placement = pos=(-214.143,3.6,-69.4316) rot=(0,0,1;0rad)
  sketch-geometry (7):
    g0: LineSegment StartX=0 StartY=0 StartZ=0 EndX=-4 EndY=3.8e-15 EndZ=0
    g1: ArcOfEllipse CenterX=0 CenterY=0 CenterZ=0 NormalX=0 NormalY=0 NormalZ=1 MajorRadius=4 MinorRadius=3.6 AngleXU=3.14159 StartAngle=2e-16 EndAngle=1.5708
    g2: LineSegment [constr] StartX=-4 StartY=9e-16 StartZ=0 EndX=4 EndY=-9e-16 EndZ=0
    g3: LineSegment [constr] StartX=0 StartY=-3.6 StartZ=0 EndX=0 EndY=3.6 EndZ=0
    g4: GeomPoint [constr] X=-1.74356 Y=2e-15 Z=0
    g5: GeomPoint [constr] X=1.74356 Y=-2e-15 Z=0
    g6: LineSegment StartX=0 StartY=0 StartZ=0 EndX=-4.4e-15 EndY=-3.6 EndZ=0
  constraints (11):
    c: PointOnObject(g1,g-2)
    c: Distance(g0) = 4
    c: PointOnObject(g0,g-1)
    c: InternalAlignment(g2-g5 -> g1) x4
    c: Coincident(g1,g0)
    c: Vertical(g3)
    c: Coincident(g1,g-1)
    c: Distance(g6) = 3.6
    c: Coincident(g6,g1)
    c: Coincident(g1,g6)
    c: Coincident(g0,g1)
FEATURE [PartDesign::Groove] Groove
  Angle = 360
  Angle2 = 60
  Axis = (0,1,0)
  Base = (-214.143,3.6,-69.4316)
  BaseFeature = -> Pocket018
  Profile = -> Sketch152
  ReferenceAxis = -> Sketch152 [V_Axis]
  Refine = true
  Reversed = true
  Suppressed = false
  Type = 0
FEATURE [PartDesign::Body] Body006  label="lato SX"
  AllowCompound = false
  Group = -> [Binder,Pad019,Chamfer015,Pocket002,Sketch133,Sketch091,Pad005,Sketch092,Pocket001,Sketch093,Sketch094,Pad006,Sketch095,Pad007,Sketch096,Pad008,Sketch097,Pad009,Chamfer005,Pocket004,Sketch098,Pad010,Chamfer006,Pocket003,SubtractivePipe,SubtractivePipe001,Sketch099,Sketch106,Sketch107,Sketch108,Clone2D,Sketch109,SubtractiveLoft,SubtractiveLoft001,Sketch110,Sketch111,Sketch112,Chamfer016,Chamfer017,+15 more]
  Origin = -> Origin006
  Tip = -> Groove
note: 2 file-system paths scrubbed to <path> (originals preserved in the JSON sidecar)
